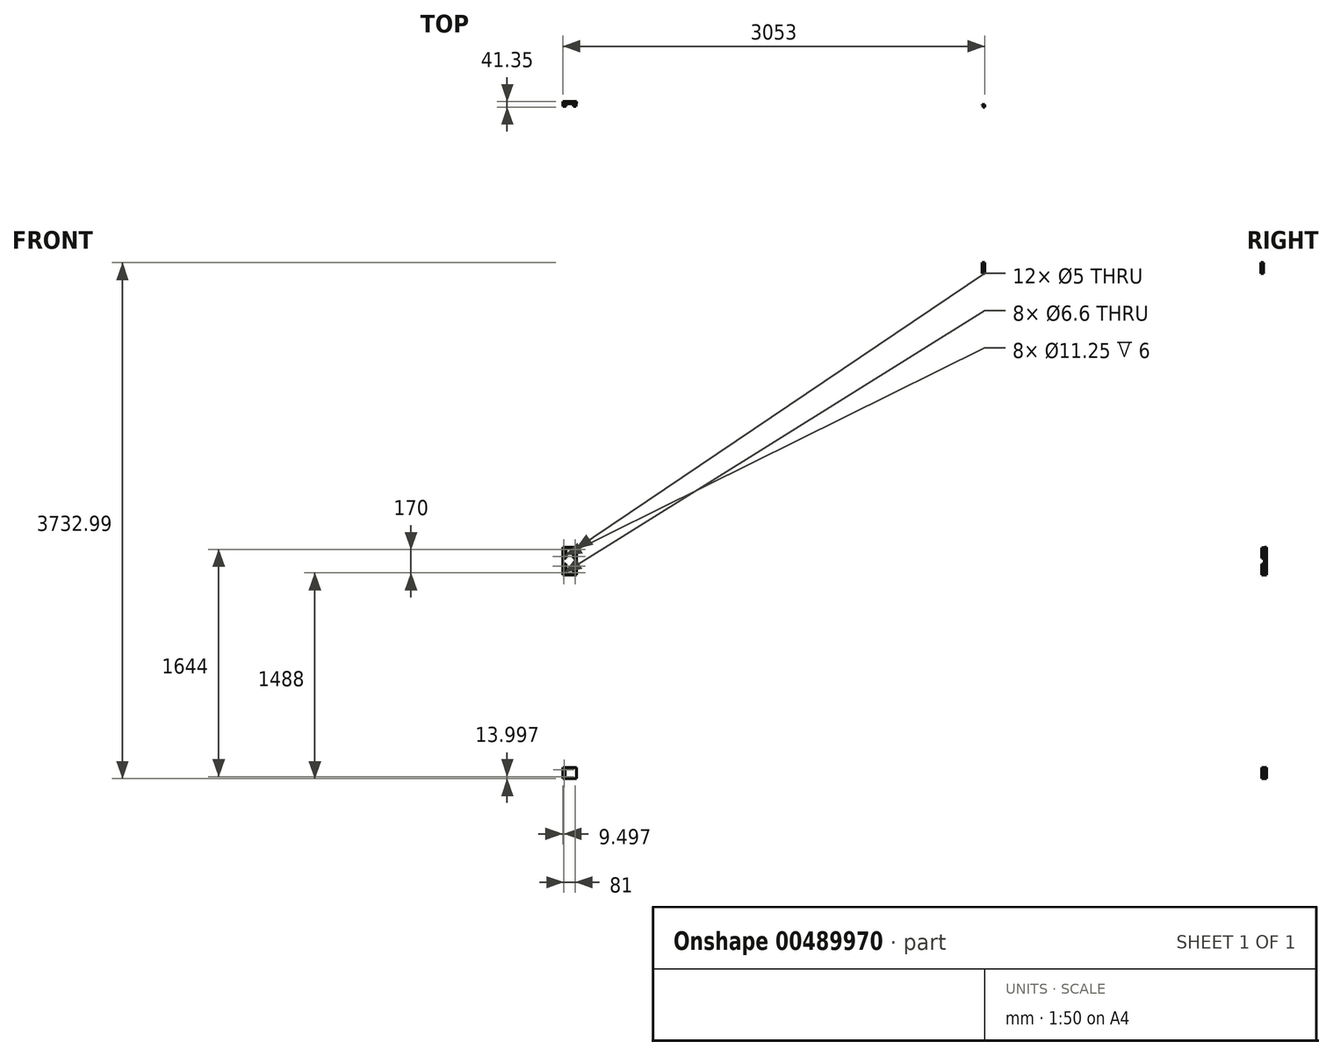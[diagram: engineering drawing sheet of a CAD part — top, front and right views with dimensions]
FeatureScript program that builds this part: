
annotation { "Feature Type Name" : "Feature", "Feature Type Description" : "" }
export const myFeature = defineFeature(function(context is Context, id is Id, definition is map)
    precondition{}
    {
        {
            var Q0;
            Q0=qCreatedBy(makeId("Front.planeOp"),FACE);
            var sketch = newSketch(context, id + "F0", { "sketchPlane" : qUnion([Q0])});
            skLineSegment(sketch, "E0", {"start": v(-4872.13, -1290) * mm, "end": v(-4872.13, -1364) * mm});
            skLineSegment(sketch, "E1", {"start": v(-2252.13, -1502) * mm, "end": v(-2252.13, -1432) * mm});
            skLineSegment(sketch, "E2", {"start": v(-2092.13, -1432) * mm, "end": v(-2092.13, -1502) * mm});
            skLineSegment(sketch, "E3", {"start": v(-2202.13, -1502) * mm, "end": v(-2252.13, -1502) * mm});
            skLineSegment(sketch, "E4", {"start": v(-2227.13, -1527.44) * mm, "end": v(-2227.13, -1552.44) * mm});
            skLineSegment(sketch, "E5", {"start": v(-2202.13, -1552.44) * mm, "end": v(-2241.95, -1552.44) * mm});
            skLineSegment(sketch, "E6", {"start": v(-2202.13, -1527.44) * mm, "end": v(-2252.13, -1527.44) * mm});
            skLineSegment(sketch, "E7", {"start": v(-2202.13, -1518.44) * mm, "end": v(-2252.13, -1518.44) * mm});
            skLineSegment(sketch, "E8", {"start": v(-2252.13, -1509.44) * mm, "end": v(-2202.13, -1509.44) * mm});
            skLineSegment(sketch, "E9", {"start": v(-2252.13, -1527.44) * mm, "end": v(-2252.13, -1509.44) * mm});
            skLineSegment(sketch, "E10", {"start": v(-2237.13, -1502) * mm, "end": v(-2237.13, -1509.44) * mm});
            skLineSegment(sketch, "E11", {"start": v(-2092.13, -1502) * mm, "end": v(-2142.13, -1502) * mm});
            skLineSegment(sketch, "E12", {"start": v(-2117.13, -1552.44) * mm, "end": v(-2117.13, -1527.44) * mm});
            skLineSegment(sketch, "E13", {"start": v(-2102.32, -1552.44) * mm, "end": v(-2142.13, -1552.44) * mm});
            skLineSegment(sketch, "E14", {"start": v(-2092.13, -1527.44) * mm, "end": v(-2142.13, -1527.44) * mm});
            skLineSegment(sketch, "E15", {"start": v(-2092.13, -1518.44) * mm, "end": v(-2142.13, -1518.44) * mm});
            skLineSegment(sketch, "E16", {"start": v(-2142.13, -1509.44) * mm, "end": v(-2092.13, -1509.44) * mm});
            skLineSegment(sketch, "E17", {"start": v(-2092.13, -1509.44) * mm, "end": v(-2092.13, -1527.44) * mm});
            skLineSegment(sketch, "E18", {"start": v(-2107.13, -1509.44) * mm, "end": v(-2107.13, -1502) * mm});
            skLineSegment(sketch, "E19", {"start": v(-2241.95, -1708.72) * mm, "end": v(-2241.95, -1552.44) * mm});
            skLineSegment(sketch, "E20", {"start": v(-2102.32, -1552.44) * mm, "end": v(-2102.32, -1708.72) * mm});
            skLineSegment(sketch, "E21", {"start": v(-2229.96, -1728.44) * mm, "end": v(-2202.13, -1728.44) * mm});
            skLineSegment(sketch, "E22", {"start": v(-2202.13, -1708.72) * mm, "end": v(-2241.95, -1708.72) * mm});
            skLineSegment(sketch, "E23", {"start": v(-2241.95, -1664.44) * mm, "end": v(-2202.13, -1664.44) * mm});
            skLineSegment(sketch, "E24", {"start": v(-2235.24, -1708.72) * mm, "end": v(-2229.96, -1728.44) * mm});
            skLineSegment(sketch, "E25", {"start": v(-2142.13, -1728.44) * mm, "end": v(-2114.3, -1728.44) * mm});
            skLineSegment(sketch, "E26", {"start": v(-2102.32, -1708.72) * mm, "end": v(-2142.13, -1708.72) * mm});
            skLineSegment(sketch, "E27", {"start": v(-2142.13, -1664.44) * mm, "end": v(-2102.32, -1664.44) * mm});
            skLineSegment(sketch, "E28", {"start": v(-2114.3, -1728.44) * mm, "end": v(-2109.02, -1708.72) * mm});
            skLineSegment(sketch, "E29", {"start": v(-2202.13, -1832) * mm, "end": v(-2202.13, -1432) * mm});
            skLineSegment(sketch, "E30", {"start": v(-2142.13, -1832) * mm, "end": v(-2142.13, -1432) * mm});
            skLineSegment(sketch, "E31", {"start": v(47.87, -1832) * mm, "end": v(47.87, -1432) * mm});
            skLineSegment(sketch, "E32", {"start": v(107.87, -1832) * mm, "end": v(107.87, -1432) * mm});
            skLineSegment(sketch, "E33", {"start": v(377.87, -1290) * mm, "end": v(377.87, -1364) * mm});
            skLineSegment(sketch, "E34", {"start": v(1373.62, -1832) * mm, "end": v(1373.62, -1432) * mm});
            skLineSegment(sketch, "E35", {"start": v(1433.62, -1832) * mm, "end": v(1433.62, -1432) * mm});
            skLineSegment(sketch, "E36", {"start": v(2247.87, -1502) * mm, "end": v(2247.87, -1432) * mm});
            skLineSegment(sketch, "E37", {"start": v(2407.87, -1432) * mm, "end": v(2407.87, -1502) * mm});
            skLineSegment(sketch, "E38", {"start": v(2297.87, -1502) * mm, "end": v(2247.87, -1502) * mm});
            skLineSegment(sketch, "E39", {"start": v(2272.87, -1527.44) * mm, "end": v(2272.87, -1552.44) * mm});
            skLineSegment(sketch, "E40", {"start": v(2297.87, -1552.44) * mm, "end": v(2258.05, -1552.44) * mm});
            skLineSegment(sketch, "E41", {"start": v(2297.87, -1527.44) * mm, "end": v(2247.87, -1527.44) * mm});
            skLineSegment(sketch, "E42", {"start": v(2297.87, -1518.44) * mm, "end": v(2247.87, -1518.44) * mm});
            skLineSegment(sketch, "E43", {"start": v(2247.87, -1509.44) * mm, "end": v(2297.87, -1509.44) * mm});
            skLineSegment(sketch, "E44", {"start": v(2247.87, -1527.44) * mm, "end": v(2247.87, -1509.44) * mm});
            skLineSegment(sketch, "E45", {"start": v(2262.87, -1502) * mm, "end": v(2262.87, -1509.44) * mm});
            skLineSegment(sketch, "E46", {"start": v(2407.87, -1502) * mm, "end": v(2357.87, -1502) * mm});
            skLineSegment(sketch, "E47", {"start": v(2382.87, -1552.44) * mm, "end": v(2382.87, -1527.44) * mm});
            skLineSegment(sketch, "E48", {"start": v(2397.68, -1552.44) * mm, "end": v(2357.87, -1552.44) * mm});
            skLineSegment(sketch, "E49", {"start": v(2407.87, -1527.44) * mm, "end": v(2357.87, -1527.44) * mm});
            skLineSegment(sketch, "E50", {"start": v(2407.87, -1518.44) * mm, "end": v(2357.87, -1518.44) * mm});
            skLineSegment(sketch, "E51", {"start": v(2357.87, -1509.44) * mm, "end": v(2407.87, -1509.44) * mm});
            skLineSegment(sketch, "E52", {"start": v(2407.87, -1509.44) * mm, "end": v(2407.87, -1527.44) * mm});
            skLineSegment(sketch, "E53", {"start": v(2392.87, -1509.44) * mm, "end": v(2392.87, -1502) * mm});
            skLineSegment(sketch, "E54", {"start": v(2258.05, -1664.44) * mm, "end": v(2297.87, -1664.44) * mm});
            skLineSegment(sketch, "E55", {"start": v(2357.87, -1664.44) * mm, "end": v(2397.68, -1664.44) * mm});
            skLineSegment(sketch, "E56", {"start": v(2397.68, -1552.44) * mm, "end": v(2397.68, -1708.72) * mm});
            skLineSegment(sketch, "E57", {"start": v(2258.05, -1708.72) * mm, "end": v(2258.05, -1552.44) * mm});
            skLineSegment(sketch, "E58", {"start": v(2270.04, -1728.44) * mm, "end": v(2297.87, -1728.44) * mm});
            skLineSegment(sketch, "E59", {"start": v(2297.87, -1708.72) * mm, "end": v(2258.05, -1708.72) * mm});
            skLineSegment(sketch, "E60", {"start": v(2264.76, -1708.72) * mm, "end": v(2270.04, -1728.44) * mm});
            skLineSegment(sketch, "E61", {"start": v(2397.68, -1708.72) * mm, "end": v(2357.87, -1708.72) * mm});
            skLineSegment(sketch, "E62", {"start": v(2385.7, -1728.44) * mm, "end": v(2390.98, -1708.72) * mm});
            skLineSegment(sketch, "E63", {"start": v(2357.87, -1728.44) * mm, "end": v(2385.7, -1728.44) * mm});
            skLineSegment(sketch, "E64", {"start": v(2357.87, -1832) * mm, "end": v(2357.87, -1432) * mm});
            skLineSegment(sketch, "E65", {"start": v(2297.87, -1832) * mm, "end": v(2297.87, -1432) * mm});
            skLineSegment(sketch, "E66", {"start": v(5047.87, -1832) * mm, "end": v(5047.87, -1907) * mm});
            skLineSegment(sketch, "E67", {"start": v(5027.87, -1364) * mm, "end": v(5027.87, -1290) * mm});
            skLineSegment(sketch, "E68", {"start": v(-813.13, -3157.5) * mm, "end": v(-1564.63, -3157.5) * mm});
            skLineSegment(sketch, "E69", {"start": v(-813.13, -3107.5) * mm, "end": v(-1564.63, -3107.5) * mm});
            skLineSegment(sketch, "E70", {"start": v(-4218.63, -3177.5) * mm, "end": v(-3029.63, -3177.5) * mm});
            skLineSegment(sketch, "E71", {"start": v(-813.13, -3177.5) * mm, "end": v(-813.13, -3087.5) * mm});
            skLineSegment(sketch, "E72", {"start": v(-813.13, -3087.5) * mm, "end": v(-1564.63, -3087.5) * mm});
            skLineSegment(sketch, "E73", {"start": v(-4245.63, -2962.5) * mm, "end": v(-4364.63, -2962.5) * mm});
            skLineSegment(sketch, "E74", {"start": v(-4245.63, -3302.5) * mm, "end": v(-4245.63, -2962.5) * mm});
            skLineSegment(sketch, "E75", {"start": v(-4245.63, -3072.5) * mm, "end": v(-4218.63, -3072.5) * mm});
            skLineSegment(sketch, "E76", {"start": v(-4218.63, -3072.5) * mm, "end": v(-4218.63, -3192.5) * mm});
            skLineSegment(sketch, "E77", {"start": v(-4218.63, -3192.5) * mm, "end": v(-4245.63, -3192.5) * mm});
            skLineSegment(sketch, "E78", {"start": v(-4245.63, -3007.5) * mm, "end": v(-4364.63, -3007.5) * mm});
            skLineSegment(sketch, "E79", {"start": v(-5062.13, -3735.9) * mm, "end": v(-4502.13, -3735.9) * mm});
            skLineSegment(sketch, "E80", {"start": v(-4567.13, -3735.9) * mm, "end": v(-4567.13, -3667.9) * mm});
            skLineSegment(sketch, "E81", {"start": v(-4928.15, -3475.9) * mm, "end": v(-4567.13, -3475.9) * mm});
            skLineSegment(sketch, "E82", {"start": v(-4586.13, -3265.9) * mm, "end": v(-4628.13, -3265.9) * mm});
            skLineSegment(sketch, "E83", {"start": v(-4579.63, -3250.02) * mm, "end": v(-4607.13, -3234.14) * mm});
            skLineSegment(sketch, "E84", {"start": v(-4579.63, -3281.77) * mm, "end": v(-4579.63, -3250.02) * mm});
            skLineSegment(sketch, "E85", {"start": v(-4607.13, -3297.65) * mm, "end": v(-4579.63, -3281.77) * mm});
            skLineSegment(sketch, "E86", {"start": v(-4628.13, -3685.9) * mm, "end": v(-4586.13, -3685.9) * mm});
            skLineSegment(sketch, "E87", {"start": v(-4607.13, -3717.65) * mm, "end": v(-4579.63, -3701.77) * mm});
            skLineSegment(sketch, "E88", {"start": v(-4579.63, -3701.77) * mm, "end": v(-4579.63, -3670.02) * mm});
            skLineSegment(sketch, "E89", {"start": v(-4579.63, -3670.02) * mm, "end": v(-4607.13, -3654.14) * mm});
            skLineSegment(sketch, "E90", {"start": v(-4502.13, -3215.9) * mm, "end": v(-5062.13, -3215.9) * mm});
            skLineSegment(sketch, "E91", {"start": v(-4567.13, -3302.5) * mm, "end": v(-4567.13, -3215.9) * mm});
            skLineSegment(sketch, "E92", {"start": v(-1779.63, -3321.5) * mm, "end": v(-1779.63, -3671.5) * mm});
            skLineSegment(sketch, "E93", {"start": v(-3228.13, -3760.9) * mm, "end": v(-3186.13, -3760.9) * mm});
            skLineSegment(sketch, "E94", {"start": v(-3207.13, -3781.9) * mm, "end": v(-3207.13, -3739.9) * mm});
            skLineSegment(sketch, "E95", {"start": v(-3207.13, -3774.75) * mm, "end": v(-3195.13, -3767.82) * mm});
            skLineSegment(sketch, "E96", {"start": v(-3195.13, -3767.82) * mm, "end": v(-3195.13, -3753.97) * mm});
            skLineSegment(sketch, "E97", {"start": v(-3195.13, -3753.97) * mm, "end": v(-3207.13, -3747.04) * mm});
            skLineSegment(sketch, "E98", {"start": v(-3207.13, -3747.04) * mm, "end": v(-3219.13, -3753.97) * mm});
            skLineSegment(sketch, "E99", {"start": v(-3219.13, -3753.97) * mm, "end": v(-3219.13, -3767.82) * mm});
            skLineSegment(sketch, "E100", {"start": v(-3219.13, -3767.82) * mm, "end": v(-3207.13, -3774.75) * mm});
            skLineSegment(sketch, "E101", {"start": v(-3186.13, -3190.9) * mm, "end": v(-3228.13, -3190.9) * mm});
            skLineSegment(sketch, "E102", {"start": v(-3207.13, -3211.9) * mm, "end": v(-3207.13, -3169.9) * mm});
            skLineSegment(sketch, "E103", {"start": v(-3195.13, -3183.97) * mm, "end": v(-3207.13, -3177.04) * mm});
            skLineSegment(sketch, "E104", {"start": v(-3195.13, -3197.82) * mm, "end": v(-3195.13, -3183.97) * mm});
            skLineSegment(sketch, "E105", {"start": v(-3207.13, -3204.75) * mm, "end": v(-3195.13, -3197.82) * mm});
            skLineSegment(sketch, "E106", {"start": v(-3219.13, -3197.82) * mm, "end": v(-3207.13, -3204.75) * mm});
            skLineSegment(sketch, "E107", {"start": v(-3219.13, -3183.97) * mm, "end": v(-3219.13, -3197.82) * mm});
            skLineSegment(sketch, "E108", {"start": v(-3207.13, -3177.04) * mm, "end": v(-3219.13, -3183.97) * mm});
            skLineSegment(sketch, "E109", {"start": v(-3557.13, -3169.9) * mm, "end": v(-3557.13, -3211.9) * mm});
            skLineSegment(sketch, "E110", {"start": v(-3536.13, -3190.9) * mm, "end": v(-3578.13, -3190.9) * mm});
            skLineSegment(sketch, "E111", {"start": v(-3557.13, -3177.04) * mm, "end": v(-3569.13, -3183.97) * mm});
            skLineSegment(sketch, "E112", {"start": v(-3569.13, -3183.97) * mm, "end": v(-3569.13, -3197.82) * mm});
            skLineSegment(sketch, "E113", {"start": v(-3569.13, -3197.82) * mm, "end": v(-3557.13, -3204.75) * mm});
            skLineSegment(sketch, "E114", {"start": v(-3557.13, -3204.75) * mm, "end": v(-3545.13, -3197.82) * mm});
            skLineSegment(sketch, "E115", {"start": v(-3545.13, -3197.82) * mm, "end": v(-3545.13, -3183.97) * mm});
            skLineSegment(sketch, "E116", {"start": v(-3545.13, -3183.97) * mm, "end": v(-3557.13, -3177.04) * mm});
            skLineSegment(sketch, "E117", {"start": v(-3569.13, -3767.82) * mm, "end": v(-3557.13, -3774.75) * mm});
            skLineSegment(sketch, "E118", {"start": v(-3569.13, -3753.97) * mm, "end": v(-3569.13, -3767.82) * mm});
            skLineSegment(sketch, "E119", {"start": v(-3557.13, -3747.04) * mm, "end": v(-3569.13, -3753.97) * mm});
            skLineSegment(sketch, "E120", {"start": v(-3545.13, -3753.97) * mm, "end": v(-3557.13, -3747.04) * mm});
            skLineSegment(sketch, "E121", {"start": v(-3545.13, -3767.82) * mm, "end": v(-3545.13, -3753.97) * mm});
            skLineSegment(sketch, "E122", {"start": v(-3557.13, -3774.75) * mm, "end": v(-3545.13, -3767.82) * mm});
            skLineSegment(sketch, "E123", {"start": v(-3557.13, -3739.9) * mm, "end": v(-3557.13, -3781.9) * mm});
            skLineSegment(sketch, "E124", {"start": v(-3578.13, -3760.9) * mm, "end": v(-3536.13, -3760.9) * mm});
            skLineSegment(sketch, "E125", {"start": v(-3597.13, -3790.9) * mm, "end": v(-3167.13, -3790.9) * mm});
            skLineSegment(sketch, "E126", {"start": v(-3597.13, -3160.9) * mm, "end": v(-3167.13, -3160.9) * mm});
            skLineSegment(sketch, "E127", {"start": v(-3377.13, -3496.5) * mm, "end": v(-3377.13, -3484.5) * mm});
            skLineSegment(sketch, "E128", {"start": v(-3427.13, -3358.55) * mm, "end": v(-3427.13, -3484.44) * mm});
            skLineSegment(sketch, "E129", {"start": v(-3377.13, -3496.5) * mm, "end": v(-3382.13, -3496.5) * mm});
            skLineSegment(sketch, "E130", {"start": v(-3377.13, -3484.5) * mm, "end": v(-3377.13, -3496.5) * mm});
            skLineSegment(sketch, "E131", {"start": v(-3382.13, -3496.5) * mm, "end": v(-3427.13, -3484.44) * mm});
            skLineSegment(sketch, "E132", {"start": v(-3382.13, -3346.5) * mm, "end": v(-3377.13, -3346.5) * mm});
            skLineSegment(sketch, "E133", {"start": v(-3427.13, -3358.55) * mm, "end": v(-3382.13, -3346.5) * mm});
            skLineSegment(sketch, "E134", {"start": v(-3382.13, -3582.8) * mm, "end": v(-3427.13, -3570.74) * mm});
            skLineSegment(sketch, "E135", {"start": v(-3377.13, -3517.2) * mm, "end": v(-3377.13, -3505.2) * mm});
            skLineSegment(sketch, "E136", {"start": v(-3377.13, -3570.8) * mm, "end": v(-3377.13, -3582.8) * mm});
            skLineSegment(sketch, "E137", {"start": v(-3377.13, -3582.8) * mm, "end": v(-3382.13, -3582.8) * mm});
            skLineSegment(sketch, "E138", {"start": v(-3427.13, -3505.2) * mm, "end": v(-3427.13, -3570.74) * mm});
            skLineSegment(sketch, "E139", {"start": v(-3427.13, -3505.2) * mm, "end": v(-3377.13, -3505.2) * mm});
            skLineSegment(sketch, "E140", {"start": v(-3282.13, -3595.9) * mm, "end": v(-3482.13, -3595.9) * mm});
            skLineSegment(sketch, "E141", {"start": v(-3482.13, -3355.9) * mm, "end": v(-3417.21, -3355.9) * mm});
            skLineSegment(sketch, "E142", {"start": v(-3463.73, -3383.9) * mm, "end": v(-3427.13, -3383.9) * mm});
            skLineSegment(sketch, "E143", {"start": v(-3482.13, -3375.9) * mm, "end": v(-3427.13, -3375.9) * mm});
            skLineSegment(sketch, "E144", {"start": v(-3463.73, -3567.9) * mm, "end": v(-3427.13, -3567.9) * mm});
            skLineSegment(sketch, "E145", {"start": v(-3482.13, -3575.9) * mm, "end": v(-3408.06, -3575.9) * mm});
            skLineSegment(sketch, "E146", {"start": v(-3474.13, -3394.3) * mm, "end": v(-3474.13, -3557.5) * mm});
            skLineSegment(sketch, "E147", {"start": v(-3497.13, -3602.9) * mm, "end": v(-3497.13, -3225.9) * mm});
            skLineSegment(sketch, "E148", {"start": v(-3482.13, -3225.9) * mm, "end": v(-3482.13, -3602.9) * mm});
            skLineSegment(sketch, "E149", {"start": v(-3497.13, -3225.9) * mm, "end": v(-3482.13, -3225.9) * mm});
            skLineSegment(sketch, "E150", {"start": v(-3597.13, -3160.9) * mm, "end": v(-3597.13, -3602.9) * mm});
            skLineSegment(sketch, "E151", {"start": v(-3597.13, -3735.9) * mm, "end": v(-3167.13, -3735.9) * mm});
            skLineSegment(sketch, "E152", {"start": v(-3536.13, -3265.9) * mm, "end": v(-3578.13, -3265.9) * mm});
            skLineSegment(sketch, "E153", {"start": v(-3557.13, -3244.9) * mm, "end": v(-3557.13, -3286.9) * mm});
            skLineSegment(sketch, "E154", {"start": v(-3167.13, -3790.9) * mm, "end": v(-3167.13, -3775.5) * mm});
            skLineSegment(sketch, "E155", {"start": v(-3167.13, -3215.9) * mm, "end": v(-3337.13, -3215.9) * mm});
            skLineSegment(sketch, "E156", {"start": v(-3528.15, -3475.9) * mm, "end": v(-3167.13, -3475.9) * mm});
            skLineSegment(sketch, "E157", {"start": v(-3557.13, -3234.14) * mm, "end": v(-3584.63, -3250.02) * mm});
            skLineSegment(sketch, "E158", {"start": v(-3584.63, -3250.02) * mm, "end": v(-3584.63, -3281.77) * mm});
            skLineSegment(sketch, "E159", {"start": v(-3584.63, -3281.77) * mm, "end": v(-3557.13, -3297.65) * mm});
            skLineSegment(sketch, "E160", {"start": v(-3557.13, -3297.65) * mm, "end": v(-3529.63, -3281.77) * mm});
            skLineSegment(sketch, "E161", {"start": v(-3529.63, -3281.77) * mm, "end": v(-3529.63, -3250.02) * mm});
            skLineSegment(sketch, "E162", {"start": v(-3529.63, -3250.02) * mm, "end": v(-3557.13, -3234.14) * mm});
            skLineSegment(sketch, "E163", {"start": v(-3578.13, -3685.9) * mm, "end": v(-3536.13, -3685.9) * mm});
            skLineSegment(sketch, "E164", {"start": v(-3557.13, -3664.9) * mm, "end": v(-3557.13, -3706.9) * mm});
            skLineSegment(sketch, "E165", {"start": v(-3584.63, -3701.77) * mm, "end": v(-3557.13, -3717.65) * mm});
            skLineSegment(sketch, "E166", {"start": v(-3584.63, -3670.02) * mm, "end": v(-3584.63, -3701.77) * mm});
            skLineSegment(sketch, "E167", {"start": v(-3557.13, -3654.14) * mm, "end": v(-3584.63, -3670.02) * mm});
            skLineSegment(sketch, "E168", {"start": v(-3529.63, -3670.02) * mm, "end": v(-3557.13, -3654.14) * mm});
            skLineSegment(sketch, "E169", {"start": v(-3529.63, -3701.77) * mm, "end": v(-3529.63, -3670.02) * mm});
            skLineSegment(sketch, "E170", {"start": v(-3557.13, -3717.65) * mm, "end": v(-3529.63, -3701.77) * mm});
            skLineSegment(sketch, "E171", {"start": v(-3186.13, -3265.9) * mm, "end": v(-3228.13, -3265.9) * mm});
            skLineSegment(sketch, "E172", {"start": v(-3207.13, -3286.9) * mm, "end": v(-3207.13, -3244.9) * mm});
            skLineSegment(sketch, "E173", {"start": v(-3179.63, -3250.02) * mm, "end": v(-3207.13, -3234.14) * mm});
            skLineSegment(sketch, "E174", {"start": v(-3179.63, -3281.77) * mm, "end": v(-3179.63, -3250.02) * mm});
            skLineSegment(sketch, "E175", {"start": v(-3207.13, -3297.65) * mm, "end": v(-3179.63, -3281.77) * mm});
            skLineSegment(sketch, "E176", {"start": v(-3234.63, -3281.77) * mm, "end": v(-3207.13, -3297.65) * mm});
            skLineSegment(sketch, "E177", {"start": v(-3234.63, -3250.02) * mm, "end": v(-3234.63, -3281.77) * mm});
            skLineSegment(sketch, "E178", {"start": v(-3207.13, -3234.14) * mm, "end": v(-3234.63, -3250.02) * mm});
            skLineSegment(sketch, "E179", {"start": v(-3359.63, -3431.4) * mm, "end": v(-3359.63, -3411.6) * mm});
            skLineSegment(sketch, "E180", {"start": v(-3389.63, -3409.8) * mm, "end": v(-3389.63, -3360.8) * mm});
            skLineSegment(sketch, "E181", {"start": v(-3304.63, -3360.8) * mm, "end": v(-3304.63, -3409.8) * mm});
            skLineSegment(sketch, "E182", {"start": v(-3389.13, -3360.3) * mm, "end": v(-3389.63, -3360.8) * mm});
            skLineSegment(sketch, "E183", {"start": v(-3389.13, -3410.3) * mm, "end": v(-3389.63, -3409.8) * mm});
            skLineSegment(sketch, "E184", {"start": v(-3305.13, -3410.3) * mm, "end": v(-3304.63, -3409.8) * mm});
            skLineSegment(sketch, "E185", {"start": v(-3305.13, -3360.3) * mm, "end": v(-3304.63, -3360.8) * mm});
            skLineSegment(sketch, "E186", {"start": v(-3305.13, -3410.3) * mm, "end": v(-3389.13, -3410.3) * mm});
            skLineSegment(sketch, "E187", {"start": v(-3389.13, -3360.3) * mm, "end": v(-3305.13, -3360.3) * mm});
            skLineSegment(sketch, "E188", {"start": v(-3347.13, -3375.54) * mm, "end": v(-3347.13, -3458.2) * mm});
            skLineSegment(sketch, "E189", {"start": v(-3377.13, -3358.5) * mm, "end": v(-3377.13, -3346.5) * mm});
            skLineSegment(sketch, "E190", {"start": v(-3317.13, -3346.5) * mm, "end": v(-3377.13, -3346.5) * mm});
            skLineSegment(sketch, "E191", {"start": v(-3317.13, -3505.2) * mm, "end": v(-3377.13, -3505.2) * mm});
            skLineSegment(sketch, "E192", {"start": v(-3389.63, -3568.5) * mm, "end": v(-3389.63, -3519.5) * mm});
            skLineSegment(sketch, "E193", {"start": v(-3305.13, -3569) * mm, "end": v(-3389.13, -3569) * mm});
            skLineSegment(sketch, "E194", {"start": v(-3304.63, -3519.5) * mm, "end": v(-3304.63, -3568.5) * mm});
            skLineSegment(sketch, "E195", {"start": v(-3389.63, -3568.5) * mm, "end": v(-3389.13, -3569) * mm});
            skLineSegment(sketch, "E196", {"start": v(-3389.63, -3519.5) * mm, "end": v(-3389.13, -3519) * mm});
            skLineSegment(sketch, "E197", {"start": v(-3304.63, -3519.5) * mm, "end": v(-3305.13, -3519) * mm});
            skLineSegment(sketch, "E198", {"start": v(-3304.63, -3568.5) * mm, "end": v(-3305.13, -3569) * mm});
            skLineSegment(sketch, "E199", {"start": v(-3389.13, -3519) * mm, "end": v(-3305.13, -3519) * mm});
            skLineSegment(sketch, "E200", {"start": v(-3347.13, -3485.8) * mm, "end": v(-3347.13, -3584.95) * mm});
            skLineSegment(sketch, "E201", {"start": v(-3377.13, -3582.8) * mm, "end": v(-3317.13, -3582.8) * mm});
            skLineSegment(sketch, "E202", {"start": v(-3389.63, -3482.2) * mm, "end": v(-3389.63, -3433.2) * mm});
            skLineSegment(sketch, "E203", {"start": v(-3305.13, -3482.7) * mm, "end": v(-3389.13, -3482.7) * mm});
            skLineSegment(sketch, "E204", {"start": v(-3304.63, -3433.2) * mm, "end": v(-3304.63, -3482.2) * mm});
            skLineSegment(sketch, "E205", {"start": v(-3389.63, -3482.2) * mm, "end": v(-3389.13, -3482.7) * mm});
            skLineSegment(sketch, "E206", {"start": v(-3389.63, -3433.2) * mm, "end": v(-3389.13, -3432.7) * mm});
            skLineSegment(sketch, "E207", {"start": v(-3304.63, -3433.2) * mm, "end": v(-3305.13, -3432.7) * mm});
            skLineSegment(sketch, "E208", {"start": v(-3304.63, -3482.2) * mm, "end": v(-3305.13, -3482.7) * mm});
            skLineSegment(sketch, "E209", {"start": v(-3389.13, -3432.7) * mm, "end": v(-3305.13, -3432.7) * mm});
            skLineSegment(sketch, "E210", {"start": v(-3334.63, -3411.6) * mm, "end": v(-3334.63, -3431.4) * mm});
            skLineSegment(sketch, "E211", {"start": v(-3377.13, -3496.5) * mm, "end": v(-3317.13, -3496.5) * mm});
            skLineSegment(sketch, "E212", {"start": v(-3387.13, -3432.7) * mm, "end": v(-3387.13, -3410.3) * mm});
            skLineSegment(sketch, "E213", {"start": v(-3307.13, -3432.7) * mm, "end": v(-3307.13, -3410.3) * mm});
            skLineSegment(sketch, "E214", {"start": v(-3317.13, -3346.5) * mm, "end": v(-3317.13, -3358.5) * mm});
            skLineSegment(sketch, "E215", {"start": v(-3317.13, -3484.5) * mm, "end": v(-3317.13, -3496.5) * mm});
            skLineSegment(sketch, "E216", {"start": v(-3317.13, -3505.2) * mm, "end": v(-3317.13, -3517.2) * mm});
            skLineSegment(sketch, "E217", {"start": v(-3317.13, -3570.8) * mm, "end": v(-3317.13, -3582.8) * mm});
            skLineSegment(sketch, "E218", {"start": v(-3317.13, -3579) * mm, "end": v(-3307.13, -3579) * mm});
            skLineSegment(sketch, "E219", {"start": v(-3307.13, -3579) * mm, "end": v(-3307.13, -3569) * mm});
            skLineSegment(sketch, "E220", {"start": v(-3317.13, -3509) * mm, "end": v(-3307.13, -3509) * mm});
            skLineSegment(sketch, "E221", {"start": v(-3307.13, -3509) * mm, "end": v(-3307.13, -3519) * mm});
            skLineSegment(sketch, "E222", {"start": v(-3317.13, -3352.5) * mm, "end": v(-3307.13, -3352.5) * mm});
            skLineSegment(sketch, "E223", {"start": v(-3307.13, -3352.5) * mm, "end": v(-3307.13, -3360.3) * mm});
            skLineSegment(sketch, "E224", {"start": v(-3317.13, -3490.5) * mm, "end": v(-3307.13, -3490.5) * mm});
            skLineSegment(sketch, "E225", {"start": v(-3307.13, -3490.5) * mm, "end": v(-3307.13, -3482.7) * mm});
            skLineSegment(sketch, "E226", {"start": v(-3282.13, -3602.9) * mm, "end": v(-3282.13, -3551.5) * mm});
            skLineSegment(sketch, "E227", {"start": v(-3282.13, -3225.9) * mm, "end": v(-3267.13, -3225.9) * mm});
            skLineSegment(sketch, "E228", {"start": v(-3267.13, -3225.9) * mm, "end": v(-3267.13, -3410) * mm});
            skLineSegment(sketch, "E229", {"start": v(-3228.13, -3685.9) * mm, "end": v(-3186.13, -3685.9) * mm});
            skLineSegment(sketch, "E230", {"start": v(-3207.13, -3706.9) * mm, "end": v(-3207.13, -3664.9) * mm});
            skLineSegment(sketch, "E231", {"start": v(-3207.13, -3717.65) * mm, "end": v(-3179.63, -3701.77) * mm});
            skLineSegment(sketch, "E232", {"start": v(-3179.63, -3701.77) * mm, "end": v(-3179.63, -3670.02) * mm});
            skLineSegment(sketch, "E233", {"start": v(-3179.63, -3670.02) * mm, "end": v(-3207.13, -3654.14) * mm});
            skLineSegment(sketch, "E234", {"start": v(-3207.13, -3654.14) * mm, "end": v(-3234.63, -3670.02) * mm});
            skLineSegment(sketch, "E235", {"start": v(-3234.63, -3670.02) * mm, "end": v(-3234.63, -3701.77) * mm});
            skLineSegment(sketch, "E236", {"start": v(-3234.63, -3701.77) * mm, "end": v(-3207.13, -3717.65) * mm});
            skLineSegment(sketch, "E237", {"start": v(-3282.13, -3575.9) * mm, "end": v(-3307.13, -3575.9) * mm});
            skLineSegment(sketch, "E238", {"start": v(-3282.13, -3375.9) * mm, "end": v(-3304.63, -3375.9) * mm});
            skLineSegment(sketch, "E239", {"start": v(-3290.13, -3557.5) * mm, "end": v(-3290.13, -3551.5) * mm});
            skLineSegment(sketch, "E240", {"start": v(-3307.13, -3355.9) * mm, "end": v(-3282.13, -3355.9) * mm});
            skLineSegment(sketch, "E241", {"start": v(-3300.53, -3383.9) * mm, "end": v(-3304.63, -3383.9) * mm});
            skLineSegment(sketch, "E242", {"start": v(-3300.53, -3567.9) * mm, "end": v(-3304.63, -3567.9) * mm});
            skLineSegment(sketch, "E243", {"start": v(-3304.63, -3536.5) * mm, "end": v(-3259, -3536.5) * mm});
            skLineSegment(sketch, "E244", {"start": v(-3259, -3536.5) * mm, "end": v(-3259, -3538) * mm});
            skLineSegment(sketch, "E245", {"start": v(-3259, -3538) * mm, "end": v(-3222, -3538) * mm});
            skLineSegment(sketch, "E246", {"start": v(-3259, -3550) * mm, "end": v(-3259, -3551.5) * mm});
            skLineSegment(sketch, "E247", {"start": v(-3259, -3551.5) * mm, "end": v(-3304.63, -3551.5) * mm});
            skLineSegment(sketch, "E248", {"start": v(-3234, -3535) * mm, "end": v(-3234, -3553) * mm});
            skLineSegment(sketch, "E249", {"start": v(-3222, -3550) * mm, "end": v(-3241, -3550) * mm});
            skLineSegment(sketch, "E250", {"start": v(-3241, -3550) * mm, "end": v(-3246, -3550) * mm});
            skLineSegment(sketch, "E251", {"start": v(-3246, -3550) * mm, "end": v(-3259, -3550) * mm});
            skLineSegment(sketch, "E252", {"start": v(-3259, -3410) * mm, "end": v(-3259, -3412) * mm});
            skLineSegment(sketch, "E253", {"start": v(-3259, -3412) * mm, "end": v(-3218, -3412) * mm});
            skLineSegment(sketch, "E254", {"start": v(-3259, -3428) * mm, "end": v(-3259, -3430) * mm});
            skLineSegment(sketch, "E255", {"start": v(-3234, -3408.5) * mm, "end": v(-3234, -3431.5) * mm});
            skLineSegment(sketch, "E256", {"start": v(-3218, -3433) * mm, "end": v(-3218, -3407) * mm});
            skLineSegment(sketch, "E257", {"start": v(-3218, -3428) * mm, "end": v(-3243, -3428) * mm});
            skLineSegment(sketch, "E258", {"start": v(-3246, -3428) * mm, "end": v(-3259, -3428) * mm});
            skLineSegment(sketch, "E259", {"start": v(-3304.63, -3410) * mm, "end": v(-3259, -3410) * mm});
            skLineSegment(sketch, "E260", {"start": v(-3259, -3430) * mm, "end": v(-3307.13, -3430) * mm});
            skLineSegment(sketch, "E261", {"start": v(-3219.07, -3420) * mm, "end": v(-3249.07, -3420) * mm});
            skLineSegment(sketch, "E262", {"start": v(-3259, -3412) * mm, "end": v(-3243, -3412) * mm});
            skLineSegment(sketch, "E263", {"start": v(-3243, -3428) * mm, "end": v(-3250, -3428) * mm});
            skLineSegment(sketch, "E264", {"start": v(-3250, -3428) * mm, "end": v(-3259, -3428) * mm});
            skLineSegment(sketch, "E265", {"start": v(-3246, -3534) * mm, "end": v(-3244, -3532) * mm});
            skLineSegment(sketch, "E266", {"start": v(-3224, -3532) * mm, "end": v(-3222, -3534) * mm});
            skLineSegment(sketch, "E267", {"start": v(-3224, -3532) * mm, "end": v(-3244, -3532) * mm});
            skLineSegment(sketch, "E268", {"start": v(-3222, -3554) * mm, "end": v(-3222, -3534) * mm});
            skLineSegment(sketch, "E269", {"start": v(-3246, -3554) * mm, "end": v(-3246, -3550) * mm});
            skLineSegment(sketch, "E270", {"start": v(-3224, -3556) * mm, "end": v(-3244, -3556) * mm});
            skLineSegment(sketch, "E271", {"start": v(-3246, -3554) * mm, "end": v(-3244, -3556) * mm});
            skLineSegment(sketch, "E272", {"start": v(-3224, -3556) * mm, "end": v(-3222, -3554) * mm});
            skLineSegment(sketch, "E273", {"start": v(-3246, -3538) * mm, "end": v(-3246, -3534) * mm});
            skLineSegment(sketch, "E274", {"start": v(-3209, -3525) * mm, "end": v(-3209, -3563) * mm});
            skLineSegment(sketch, "E275", {"start": v(-3259, -3563) * mm, "end": v(-3259, -3551.5) * mm});
            skLineSegment(sketch, "E276", {"start": v(-3215, -3519) * mm, "end": v(-3253, -3519) * mm});
            skLineSegment(sketch, "E277", {"start": v(-3215, -3569) * mm, "end": v(-3253, -3569) * mm});
            skLineSegment(sketch, "E278", {"start": v(-3259, -3536.5) * mm, "end": v(-3259, -3524.5) * mm});
            skLineSegment(sketch, "E279", {"start": v(-3290.13, -3536.5) * mm, "end": v(-3290.13, -3430) * mm});
            skLineSegment(sketch, "E280", {"start": v(-3282.13, -3536.5) * mm, "end": v(-3282.13, -3430) * mm});
            skLineSegment(sketch, "E281", {"start": v(-3267.13, -3551.5) * mm, "end": v(-3267.13, -3602.9) * mm});
            skLineSegment(sketch, "E282", {"start": v(-3290.13, -3410) * mm, "end": v(-3290.13, -3394.3) * mm});
            skLineSegment(sketch, "E283", {"start": v(-3282.13, -3410) * mm, "end": v(-3282.13, -3225.9) * mm});
            skLineSegment(sketch, "E284", {"start": v(-3267.13, -3430) * mm, "end": v(-3267.13, -3536.5) * mm});
            skLineSegment(sketch, "E285", {"start": v(-3203, -3394.76) * mm, "end": v(-3203, -3441.26) * mm});
            skLineSegment(sketch, "E286", {"start": v(-3210.54, -3388.75) * mm, "end": v(-3257.04, -3388.75) * mm});
            skLineSegment(sketch, "E287", {"start": v(-3210.54, -3451.24) * mm, "end": v(-3257.04, -3451.24) * mm});
            skLineSegment(sketch, "E288", {"start": v(-3265, -3441.26) * mm, "end": v(-3265, -3430) * mm});
            skLineSegment(sketch, "E289", {"start": v(-3218, -3407) * mm, "end": v(-3221, -3404) * mm});
            skLineSegment(sketch, "E290", {"start": v(-3221, -3404) * mm, "end": v(-3247, -3404) * mm});
            skLineSegment(sketch, "E291", {"start": v(-3225, -3404) * mm, "end": v(-3225, -3403) * mm});
            skLineSegment(sketch, "E292", {"start": v(-3221, -3436) * mm, "end": v(-3247, -3436) * mm});
            skLineSegment(sketch, "E293", {"start": v(-3250, -3433) * mm, "end": v(-3247, -3436) * mm});
            skLineSegment(sketch, "E294", {"start": v(-3250, -3433) * mm, "end": v(-3250, -3428) * mm});
            skLineSegment(sketch, "E295", {"start": v(-3247, -3404) * mm, "end": v(-3250, -3407) * mm});
            skLineSegment(sketch, "E296", {"start": v(-3221, -3436) * mm, "end": v(-3218, -3433) * mm});
            skLineSegment(sketch, "E297", {"start": v(-3250, -3412) * mm, "end": v(-3250, -3407) * mm});
            skLineSegment(sketch, "E298", {"start": v(-3265, -3410) * mm, "end": v(-3265, -3398.73) * mm});
            skLineSegment(sketch, "E299", {"start": v(-3282.13, -3338.9) * mm, "end": v(-3282.13, -3355.9) * mm});
            skLineSegment(sketch, "E300", {"start": v(-3382.13, -3776.6) * mm, "end": v(-3382.13, -3170) * mm});
            skLineSegment(sketch, "E301", {"start": v(-3337.13, -3177.5) * mm, "end": v(-3337.13, -3338.9) * mm});
            skLineSegment(sketch, "E302", {"start": v(-3427.13, -3177.5) * mm, "end": v(-3427.13, -3338.9) * mm});
            skLineSegment(sketch, "E303", {"start": v(-3482.13, -3355.9) * mm, "end": v(-3482.13, -3338.9) * mm});
            skLineSegment(sketch, "E304", {"start": v(-3482.13, -3338.9) * mm, "end": v(-3282.13, -3338.9) * mm});
            skLineSegment(sketch, "E305", {"start": v(-3427.13, -3215.9) * mm, "end": v(-3597.13, -3215.9) * mm});
            skLineSegment(sketch, "E306", {"start": v(-1779.63, -3671.5) * mm, "end": v(-5562.13, -3671.5) * mm});
            skLineSegment(sketch, "E307", {"start": v(-2592.13, -3321.5) * mm, "end": v(-2592.13, -3671.5) * mm});
            skLineSegment(sketch, "E308", {"start": v(-3167.13, -3602.9) * mm, "end": v(-3167.13, -3160.9) * mm});
            skLineSegment(sketch, "E309", {"start": v(-3167.13, -3775.5) * mm, "end": v(-3167.13, -3602.9) * mm});
            skLineSegment(sketch, "E310", {"start": v(-3597.13, -3602.9) * mm, "end": v(-3597.13, -3775.5) * mm});
            skLineSegment(sketch, "E311", {"start": v(-3597.13, -3775.5) * mm, "end": v(-3597.13, -3790.9) * mm});
            skLineSegment(sketch, "E312", {"start": v(-1828.13, -3760.9) * mm, "end": v(-1786.13, -3760.9) * mm});
            skLineSegment(sketch, "E313", {"start": v(-1807.13, -3781.9) * mm, "end": v(-1807.13, -3739.9) * mm});
            skLineSegment(sketch, "E314", {"start": v(-1807.13, -3774.75) * mm, "end": v(-1795.13, -3767.82) * mm});
            skLineSegment(sketch, "E315", {"start": v(-1795.13, -3767.82) * mm, "end": v(-1795.13, -3753.97) * mm});
            skLineSegment(sketch, "E316", {"start": v(-1795.13, -3753.97) * mm, "end": v(-1807.13, -3747.04) * mm});
            skLineSegment(sketch, "E317", {"start": v(-1807.13, -3747.04) * mm, "end": v(-1819.13, -3753.97) * mm});
            skLineSegment(sketch, "E318", {"start": v(-1819.13, -3753.97) * mm, "end": v(-1819.13, -3767.82) * mm});
            skLineSegment(sketch, "E319", {"start": v(-1819.13, -3767.82) * mm, "end": v(-1807.13, -3774.75) * mm});
            skLineSegment(sketch, "E320", {"start": v(-1786.13, -3190.9) * mm, "end": v(-1828.13, -3190.9) * mm});
            skLineSegment(sketch, "E321", {"start": v(-1807.13, -3211.9) * mm, "end": v(-1807.13, -3169.9) * mm});
            skLineSegment(sketch, "E322", {"start": v(-1795.13, -3183.97) * mm, "end": v(-1807.13, -3177.04) * mm});
            skLineSegment(sketch, "E323", {"start": v(-1795.13, -3197.82) * mm, "end": v(-1795.13, -3183.97) * mm});
            skLineSegment(sketch, "E324", {"start": v(-1807.13, -3204.75) * mm, "end": v(-1795.13, -3197.82) * mm});
            skLineSegment(sketch, "E325", {"start": v(-1819.13, -3197.82) * mm, "end": v(-1807.13, -3204.75) * mm});
            skLineSegment(sketch, "E326", {"start": v(-1819.13, -3183.97) * mm, "end": v(-1819.13, -3197.82) * mm});
            skLineSegment(sketch, "E327", {"start": v(-1807.13, -3177.04) * mm, "end": v(-1819.13, -3183.97) * mm});
            skLineSegment(sketch, "E328", {"start": v(-2157.13, -3169.9) * mm, "end": v(-2157.13, -3211.9) * mm});
            skLineSegment(sketch, "E329", {"start": v(-2136.13, -3190.9) * mm, "end": v(-2178.13, -3190.9) * mm});
            skLineSegment(sketch, "E330", {"start": v(-2157.13, -3177.04) * mm, "end": v(-2169.13, -3183.97) * mm});
            skLineSegment(sketch, "E331", {"start": v(-2169.13, -3183.97) * mm, "end": v(-2169.13, -3197.82) * mm});
            skLineSegment(sketch, "E332", {"start": v(-2169.13, -3197.82) * mm, "end": v(-2157.13, -3204.75) * mm});
            skLineSegment(sketch, "E333", {"start": v(-2157.13, -3204.75) * mm, "end": v(-2145.13, -3197.82) * mm});
            skLineSegment(sketch, "E334", {"start": v(-2145.13, -3197.82) * mm, "end": v(-2145.13, -3183.97) * mm});
            skLineSegment(sketch, "E335", {"start": v(-2145.13, -3183.97) * mm, "end": v(-2157.13, -3177.04) * mm});
            skLineSegment(sketch, "E336", {"start": v(-2169.13, -3767.82) * mm, "end": v(-2157.13, -3774.75) * mm});
            skLineSegment(sketch, "E337", {"start": v(-2169.13, -3753.97) * mm, "end": v(-2169.13, -3767.82) * mm});
            skLineSegment(sketch, "E338", {"start": v(-2157.13, -3747.04) * mm, "end": v(-2169.13, -3753.97) * mm});
            skLineSegment(sketch, "E339", {"start": v(-2145.13, -3753.97) * mm, "end": v(-2157.13, -3747.04) * mm});
            skLineSegment(sketch, "E340", {"start": v(-2145.13, -3767.82) * mm, "end": v(-2145.13, -3753.97) * mm});
            skLineSegment(sketch, "E341", {"start": v(-2157.13, -3774.75) * mm, "end": v(-2145.13, -3767.82) * mm});
            skLineSegment(sketch, "E342", {"start": v(-2157.13, -3739.9) * mm, "end": v(-2157.13, -3781.9) * mm});
            skLineSegment(sketch, "E343", {"start": v(-2178.13, -3760.9) * mm, "end": v(-2136.13, -3760.9) * mm});
            skLineSegment(sketch, "E344", {"start": v(-2197.13, -3790.9) * mm, "end": v(-1917.98, -3790.9) * mm});
            skLineSegment(sketch, "E345", {"start": v(-1977.13, -3496.5) * mm, "end": v(-1977.13, -3484.5) * mm});
            skLineSegment(sketch, "E346", {"start": v(-2027.13, -3358.55) * mm, "end": v(-2027.13, -3484.44) * mm});
            skLineSegment(sketch, "E347", {"start": v(-1977.13, -3496.5) * mm, "end": v(-1982.13, -3496.5) * mm});
            skLineSegment(sketch, "E348", {"start": v(-1977.13, -3484.5) * mm, "end": v(-1977.13, -3496.5) * mm});
            skLineSegment(sketch, "E349", {"start": v(-1982.13, -3496.5) * mm, "end": v(-2027.13, -3484.44) * mm});
            skLineSegment(sketch, "E350", {"start": v(-1982.13, -3346.5) * mm, "end": v(-1977.13, -3346.5) * mm});
            skLineSegment(sketch, "E351", {"start": v(-2027.13, -3358.55) * mm, "end": v(-1982.13, -3346.5) * mm});
            skLineSegment(sketch, "E352", {"start": v(-1982.13, -3582.8) * mm, "end": v(-2027.13, -3570.74) * mm});
            skLineSegment(sketch, "E353", {"start": v(-1977.13, -3517.2) * mm, "end": v(-1977.13, -3505.2) * mm});
            skLineSegment(sketch, "E354", {"start": v(-1977.13, -3570.8) * mm, "end": v(-1977.13, -3582.8) * mm});
            skLineSegment(sketch, "E355", {"start": v(-1977.13, -3582.8) * mm, "end": v(-1982.13, -3582.8) * mm});
            skLineSegment(sketch, "E356", {"start": v(-2027.13, -3505.2) * mm, "end": v(-2027.13, -3570.74) * mm});
            skLineSegment(sketch, "E357", {"start": v(-2027.13, -3505.2) * mm, "end": v(-1977.13, -3505.2) * mm});
            skLineSegment(sketch, "E358", {"start": v(-1882.13, -3595.9) * mm, "end": v(-2082.13, -3595.9) * mm});
            skLineSegment(sketch, "E359", {"start": v(-2082.13, -3355.9) * mm, "end": v(-2017.21, -3355.9) * mm});
            skLineSegment(sketch, "E360", {"start": v(-2063.73, -3383.9) * mm, "end": v(-2027.13, -3383.9) * mm});
            skLineSegment(sketch, "E361", {"start": v(-2082.13, -3375.9) * mm, "end": v(-2027.13, -3375.9) * mm});
            skLineSegment(sketch, "E362", {"start": v(-2063.73, -3567.9) * mm, "end": v(-2027.13, -3567.9) * mm});
            skLineSegment(sketch, "E363", {"start": v(-2082.13, -3575.9) * mm, "end": v(-2008.06, -3575.9) * mm});
            skLineSegment(sketch, "E364", {"start": v(-2074.13, -3394.3) * mm, "end": v(-2074.13, -3557.5) * mm});
            skLineSegment(sketch, "E365", {"start": v(-2097.13, -3602.9) * mm, "end": v(-2097.13, -3225.9) * mm});
            skLineSegment(sketch, "E366", {"start": v(-2082.13, -3225.9) * mm, "end": v(-2082.13, -3602.9) * mm});
            skLineSegment(sketch, "E367", {"start": v(-2097.13, -3225.9) * mm, "end": v(-2082.13, -3225.9) * mm});
            skLineSegment(sketch, "E368", {"start": v(-2197.13, -3160.9) * mm, "end": v(-2197.13, -3602.9) * mm});
            skLineSegment(sketch, "E369", {"start": v(-2197.13, -3735.9) * mm, "end": v(-1767.13, -3735.9) * mm});
            skLineSegment(sketch, "E370", {"start": v(-2136.13, -3265.9) * mm, "end": v(-2178.13, -3265.9) * mm});
            skLineSegment(sketch, "E371", {"start": v(-2157.13, -3244.9) * mm, "end": v(-2157.13, -3286.9) * mm});
            skLineSegment(sketch, "E372", {"start": v(-1767.13, -3215.9) * mm, "end": v(-1937.13, -3215.9) * mm});
            skLineSegment(sketch, "E373", {"start": v(-2128.15, -3475.9) * mm, "end": v(-1767.13, -3475.9) * mm});
            skLineSegment(sketch, "E374", {"start": v(-2157.13, -3234.14) * mm, "end": v(-2184.63, -3250.02) * mm});
            skLineSegment(sketch, "E375", {"start": v(-2184.63, -3250.02) * mm, "end": v(-2184.63, -3281.77) * mm});
            skLineSegment(sketch, "E376", {"start": v(-2184.63, -3281.77) * mm, "end": v(-2157.13, -3297.65) * mm});
            skLineSegment(sketch, "E377", {"start": v(-2157.13, -3297.65) * mm, "end": v(-2129.63, -3281.77) * mm});
            skLineSegment(sketch, "E378", {"start": v(-2129.63, -3281.77) * mm, "end": v(-2129.63, -3250.02) * mm});
            skLineSegment(sketch, "E379", {"start": v(-2129.63, -3250.02) * mm, "end": v(-2157.13, -3234.14) * mm});
            skLineSegment(sketch, "E380", {"start": v(-2178.13, -3685.9) * mm, "end": v(-2136.13, -3685.9) * mm});
            skLineSegment(sketch, "E381", {"start": v(-2157.13, -3664.9) * mm, "end": v(-2157.13, -3706.9) * mm});
            skLineSegment(sketch, "E382", {"start": v(-2184.63, -3701.77) * mm, "end": v(-2157.13, -3717.65) * mm});
            skLineSegment(sketch, "E383", {"start": v(-2184.63, -3670.02) * mm, "end": v(-2184.63, -3701.77) * mm});
            skLineSegment(sketch, "E384", {"start": v(-2157.13, -3654.14) * mm, "end": v(-2184.63, -3670.02) * mm});
            skLineSegment(sketch, "E385", {"start": v(-2129.63, -3670.02) * mm, "end": v(-2157.13, -3654.14) * mm});
            skLineSegment(sketch, "E386", {"start": v(-2129.63, -3701.77) * mm, "end": v(-2129.63, -3670.02) * mm});
            skLineSegment(sketch, "E387", {"start": v(-2157.13, -3717.65) * mm, "end": v(-2129.63, -3701.77) * mm});
            skLineSegment(sketch, "E388", {"start": v(-1786.13, -3265.9) * mm, "end": v(-1828.13, -3265.9) * mm});
            skLineSegment(sketch, "E389", {"start": v(-1807.13, -3286.9) * mm, "end": v(-1807.13, -3244.9) * mm});
            skLineSegment(sketch, "E390", {"start": v(-1779.63, -3250.02) * mm, "end": v(-1807.13, -3234.14) * mm});
            skLineSegment(sketch, "E391", {"start": v(-1779.63, -3281.77) * mm, "end": v(-1779.63, -3250.02) * mm});
            skLineSegment(sketch, "E392", {"start": v(-1807.13, -3297.65) * mm, "end": v(-1779.63, -3281.77) * mm});
            skLineSegment(sketch, "E393", {"start": v(-1834.63, -3281.77) * mm, "end": v(-1807.13, -3297.65) * mm});
            skLineSegment(sketch, "E394", {"start": v(-1834.63, -3250.02) * mm, "end": v(-1834.63, -3281.77) * mm});
            skLineSegment(sketch, "E395", {"start": v(-1807.13, -3234.14) * mm, "end": v(-1834.63, -3250.02) * mm});
            skLineSegment(sketch, "E396", {"start": v(-1959.63, -3431.4) * mm, "end": v(-1959.63, -3411.6) * mm});
            skLineSegment(sketch, "E397", {"start": v(-1989.63, -3409.8) * mm, "end": v(-1989.63, -3360.8) * mm});
            skLineSegment(sketch, "E398", {"start": v(-1904.63, -3360.8) * mm, "end": v(-1904.63, -3409.8) * mm});
            skLineSegment(sketch, "E399", {"start": v(-1989.13, -3360.3) * mm, "end": v(-1989.63, -3360.8) * mm});
            skLineSegment(sketch, "E400", {"start": v(-1989.13, -3410.3) * mm, "end": v(-1989.63, -3409.8) * mm});
            skLineSegment(sketch, "E401", {"start": v(-1905.13, -3410.3) * mm, "end": v(-1904.63, -3409.8) * mm});
            skLineSegment(sketch, "E402", {"start": v(-1905.13, -3360.3) * mm, "end": v(-1904.63, -3360.8) * mm});
            skLineSegment(sketch, "E403", {"start": v(-1905.13, -3410.3) * mm, "end": v(-1989.13, -3410.3) * mm});
            skLineSegment(sketch, "E404", {"start": v(-1989.13, -3360.3) * mm, "end": v(-1905.13, -3360.3) * mm});
            skLineSegment(sketch, "E405", {"start": v(-1947.13, -3375.54) * mm, "end": v(-1947.13, -3458.2) * mm});
            skLineSegment(sketch, "E406", {"start": v(-1977.13, -3358.5) * mm, "end": v(-1977.13, -3346.5) * mm});
            skLineSegment(sketch, "E407", {"start": v(-1917.13, -3346.5) * mm, "end": v(-1977.13, -3346.5) * mm});
            skLineSegment(sketch, "E408", {"start": v(-1917.13, -3505.2) * mm, "end": v(-1977.13, -3505.2) * mm});
            skLineSegment(sketch, "E409", {"start": v(-1989.63, -3568.5) * mm, "end": v(-1989.63, -3519.5) * mm});
            skLineSegment(sketch, "E410", {"start": v(-1905.13, -3569) * mm, "end": v(-1989.13, -3569) * mm});
            skLineSegment(sketch, "E411", {"start": v(-1904.63, -3519.5) * mm, "end": v(-1904.63, -3568.5) * mm});
            skLineSegment(sketch, "E412", {"start": v(-1989.63, -3568.5) * mm, "end": v(-1989.13, -3569) * mm});
            skLineSegment(sketch, "E413", {"start": v(-1989.63, -3519.5) * mm, "end": v(-1989.13, -3519) * mm});
            skLineSegment(sketch, "E414", {"start": v(-1904.63, -3519.5) * mm, "end": v(-1905.13, -3519) * mm});
            skLineSegment(sketch, "E415", {"start": v(-1904.63, -3568.5) * mm, "end": v(-1905.13, -3569) * mm});
            skLineSegment(sketch, "E416", {"start": v(-1989.13, -3519) * mm, "end": v(-1905.13, -3519) * mm});
            skLineSegment(sketch, "E417", {"start": v(-1947.13, -3485.8) * mm, "end": v(-1947.13, -3584.95) * mm});
            skLineSegment(sketch, "E418", {"start": v(-1977.13, -3582.8) * mm, "end": v(-1917.13, -3582.8) * mm});
            skLineSegment(sketch, "E419", {"start": v(-1989.63, -3482.2) * mm, "end": v(-1989.63, -3433.2) * mm});
            skLineSegment(sketch, "E420", {"start": v(-1905.13, -3482.7) * mm, "end": v(-1989.13, -3482.7) * mm});
            skLineSegment(sketch, "E421", {"start": v(-1904.63, -3433.2) * mm, "end": v(-1904.63, -3482.2) * mm});
            skLineSegment(sketch, "E422", {"start": v(-1989.63, -3482.2) * mm, "end": v(-1989.13, -3482.7) * mm});
            skLineSegment(sketch, "E423", {"start": v(-1989.63, -3433.2) * mm, "end": v(-1989.13, -3432.7) * mm});
            skLineSegment(sketch, "E424", {"start": v(-1904.63, -3433.2) * mm, "end": v(-1905.13, -3432.7) * mm});
            skLineSegment(sketch, "E425", {"start": v(-1904.63, -3482.2) * mm, "end": v(-1905.13, -3482.7) * mm});
            skLineSegment(sketch, "E426", {"start": v(-1989.13, -3432.7) * mm, "end": v(-1905.13, -3432.7) * mm});
            skLineSegment(sketch, "E427", {"start": v(-1934.63, -3411.6) * mm, "end": v(-1934.63, -3431.4) * mm});
            skLineSegment(sketch, "E428", {"start": v(-1977.13, -3496.5) * mm, "end": v(-1917.13, -3496.5) * mm});
            skLineSegment(sketch, "E429", {"start": v(-1987.13, -3432.7) * mm, "end": v(-1987.13, -3410.3) * mm});
            skLineSegment(sketch, "E430", {"start": v(-1907.13, -3432.7) * mm, "end": v(-1907.13, -3410.3) * mm});
            skLineSegment(sketch, "E431", {"start": v(-1917.13, -3346.5) * mm, "end": v(-1917.13, -3358.5) * mm});
            skLineSegment(sketch, "E432", {"start": v(-1917.13, -3484.5) * mm, "end": v(-1917.13, -3496.5) * mm});
            skLineSegment(sketch, "E433", {"start": v(-1917.13, -3505.2) * mm, "end": v(-1917.13, -3517.2) * mm});
            skLineSegment(sketch, "E434", {"start": v(-1917.13, -3570.8) * mm, "end": v(-1917.13, -3582.8) * mm});
            skLineSegment(sketch, "E435", {"start": v(-1917.13, -3579) * mm, "end": v(-1907.13, -3579) * mm});
            skLineSegment(sketch, "E436", {"start": v(-1907.13, -3579) * mm, "end": v(-1907.13, -3569) * mm});
            skLineSegment(sketch, "E437", {"start": v(-1917.13, -3509) * mm, "end": v(-1907.13, -3509) * mm});
            skLineSegment(sketch, "E438", {"start": v(-1907.13, -3509) * mm, "end": v(-1907.13, -3519) * mm});
            skLineSegment(sketch, "E439", {"start": v(-1917.13, -3352.5) * mm, "end": v(-1907.13, -3352.5) * mm});
            skLineSegment(sketch, "E440", {"start": v(-1907.13, -3352.5) * mm, "end": v(-1907.13, -3360.3) * mm});
            skLineSegment(sketch, "E441", {"start": v(-1917.13, -3490.5) * mm, "end": v(-1907.13, -3490.5) * mm});
            skLineSegment(sketch, "E442", {"start": v(-1907.13, -3490.5) * mm, "end": v(-1907.13, -3482.7) * mm});
            skLineSegment(sketch, "E443", {"start": v(-1882.13, -3602.9) * mm, "end": v(-1882.13, -3551.5) * mm});
            skLineSegment(sketch, "E444", {"start": v(-1882.13, -3225.9) * mm, "end": v(-1867.13, -3225.9) * mm});
            skLineSegment(sketch, "E445", {"start": v(-1867.13, -3225.9) * mm, "end": v(-1867.13, -3410) * mm});
            skLineSegment(sketch, "E446", {"start": v(-1828.13, -3685.9) * mm, "end": v(-1786.13, -3685.9) * mm});
            skLineSegment(sketch, "E447", {"start": v(-1807.13, -3706.9) * mm, "end": v(-1807.13, -3664.9) * mm});
            skLineSegment(sketch, "E448", {"start": v(-1807.13, -3717.65) * mm, "end": v(-1779.63, -3701.77) * mm});
            skLineSegment(sketch, "E449", {"start": v(-1779.63, -3701.77) * mm, "end": v(-1779.63, -3670.02) * mm});
            skLineSegment(sketch, "E450", {"start": v(-1779.63, -3670.02) * mm, "end": v(-1807.13, -3654.14) * mm});
            skLineSegment(sketch, "E451", {"start": v(-1807.13, -3654.14) * mm, "end": v(-1834.63, -3670.02) * mm});
            skLineSegment(sketch, "E452", {"start": v(-1834.63, -3670.02) * mm, "end": v(-1834.63, -3701.77) * mm});
            skLineSegment(sketch, "E453", {"start": v(-1834.63, -3701.77) * mm, "end": v(-1807.13, -3717.65) * mm});
            skLineSegment(sketch, "E454", {"start": v(-1882.13, -3575.9) * mm, "end": v(-1907.13, -3575.9) * mm});
            skLineSegment(sketch, "E455", {"start": v(-1882.13, -3375.9) * mm, "end": v(-1904.63, -3375.9) * mm});
            skLineSegment(sketch, "E456", {"start": v(-1890.13, -3557.5) * mm, "end": v(-1890.13, -3551.5) * mm});
            skLineSegment(sketch, "E457", {"start": v(-1907.13, -3355.9) * mm, "end": v(-1882.13, -3355.9) * mm});
            skLineSegment(sketch, "E458", {"start": v(-1900.53, -3383.9) * mm, "end": v(-1904.63, -3383.9) * mm});
            skLineSegment(sketch, "E459", {"start": v(-1900.53, -3567.9) * mm, "end": v(-1904.63, -3567.9) * mm});
            skLineSegment(sketch, "E460", {"start": v(-1904.63, -3536.5) * mm, "end": v(-1859, -3536.5) * mm});
            skLineSegment(sketch, "E461", {"start": v(-1859, -3536.5) * mm, "end": v(-1859, -3538) * mm});
            skLineSegment(sketch, "E462", {"start": v(-1859, -3538) * mm, "end": v(-1822, -3538) * mm});
            skLineSegment(sketch, "E463", {"start": v(-1859, -3550) * mm, "end": v(-1859, -3551.5) * mm});
            skLineSegment(sketch, "E464", {"start": v(-1859, -3551.5) * mm, "end": v(-1904.63, -3551.5) * mm});
            skLineSegment(sketch, "E465", {"start": v(-1834, -3535) * mm, "end": v(-1834, -3553) * mm});
            skLineSegment(sketch, "E466", {"start": v(-1822, -3550) * mm, "end": v(-1841, -3550) * mm});
            skLineSegment(sketch, "E467", {"start": v(-1841, -3550) * mm, "end": v(-1846, -3550) * mm});
            skLineSegment(sketch, "E468", {"start": v(-1846, -3550) * mm, "end": v(-1859, -3550) * mm});
            skLineSegment(sketch, "E469", {"start": v(-1859, -3410) * mm, "end": v(-1859, -3412) * mm});
            skLineSegment(sketch, "E470", {"start": v(-1859, -3412) * mm, "end": v(-1818, -3412) * mm});
            skLineSegment(sketch, "E471", {"start": v(-1859, -3428) * mm, "end": v(-1859, -3430) * mm});
            skLineSegment(sketch, "E472", {"start": v(-1834, -3408.5) * mm, "end": v(-1834, -3431.5) * mm});
            skLineSegment(sketch, "E473", {"start": v(-1818, -3433) * mm, "end": v(-1818, -3407) * mm});
            skLineSegment(sketch, "E474", {"start": v(-1818, -3428) * mm, "end": v(-1843, -3428) * mm});
            skLineSegment(sketch, "E475", {"start": v(-1846, -3428) * mm, "end": v(-1859, -3428) * mm});
            skLineSegment(sketch, "E476", {"start": v(-1904.63, -3410) * mm, "end": v(-1859, -3410) * mm});
            skLineSegment(sketch, "E477", {"start": v(-1859, -3430) * mm, "end": v(-1907.13, -3430) * mm});
            skLineSegment(sketch, "E478", {"start": v(-1819.07, -3420) * mm, "end": v(-1849.07, -3420) * mm});
            skLineSegment(sketch, "E479", {"start": v(-1859, -3412) * mm, "end": v(-1843, -3412) * mm});
            skLineSegment(sketch, "E480", {"start": v(-1843, -3428) * mm, "end": v(-1850, -3428) * mm});
            skLineSegment(sketch, "E481", {"start": v(-1850, -3428) * mm, "end": v(-1859, -3428) * mm});
            skLineSegment(sketch, "E482", {"start": v(-1846, -3534) * mm, "end": v(-1844, -3532) * mm});
            skLineSegment(sketch, "E483", {"start": v(-1824, -3532) * mm, "end": v(-1822, -3534) * mm});
            skLineSegment(sketch, "E484", {"start": v(-1824, -3532) * mm, "end": v(-1844, -3532) * mm});
            skLineSegment(sketch, "E485", {"start": v(-1822, -3554) * mm, "end": v(-1822, -3534) * mm});
            skLineSegment(sketch, "E486", {"start": v(-1846, -3554) * mm, "end": v(-1846, -3550) * mm});
            skLineSegment(sketch, "E487", {"start": v(-1824, -3556) * mm, "end": v(-1844, -3556) * mm});
            skLineSegment(sketch, "E488", {"start": v(-1846, -3554) * mm, "end": v(-1844, -3556) * mm});
            skLineSegment(sketch, "E489", {"start": v(-1824, -3556) * mm, "end": v(-1822, -3554) * mm});
            skLineSegment(sketch, "E490", {"start": v(-1846, -3538) * mm, "end": v(-1846, -3534) * mm});
            skLineSegment(sketch, "E491", {"start": v(-1809, -3525) * mm, "end": v(-1809, -3563) * mm});
            skLineSegment(sketch, "E492", {"start": v(-1859, -3563) * mm, "end": v(-1859, -3551.5) * mm});
            skLineSegment(sketch, "E493", {"start": v(-1815, -3519) * mm, "end": v(-1853, -3519) * mm});
            skLineSegment(sketch, "E494", {"start": v(-1815, -3569) * mm, "end": v(-1853, -3569) * mm});
            skLineSegment(sketch, "E495", {"start": v(-1859, -3536.5) * mm, "end": v(-1859, -3524.5) * mm});
            skLineSegment(sketch, "E496", {"start": v(-1890.13, -3536.5) * mm, "end": v(-1890.13, -3430) * mm});
            skLineSegment(sketch, "E497", {"start": v(-1882.13, -3536.5) * mm, "end": v(-1882.13, -3430) * mm});
            skLineSegment(sketch, "E498", {"start": v(-1867.13, -3551.5) * mm, "end": v(-1867.13, -3602.9) * mm});
            skLineSegment(sketch, "E499", {"start": v(-1890.13, -3410) * mm, "end": v(-1890.13, -3394.3) * mm});
            skLineSegment(sketch, "E500", {"start": v(-1882.13, -3410) * mm, "end": v(-1882.13, -3225.9) * mm});
            skLineSegment(sketch, "E501", {"start": v(-1867.13, -3430) * mm, "end": v(-1867.13, -3536.5) * mm});
            skLineSegment(sketch, "E502", {"start": v(-1803, -3394.76) * mm, "end": v(-1803, -3441.26) * mm});
            skLineSegment(sketch, "E503", {"start": v(-1810.54, -3388.75) * mm, "end": v(-1857.04, -3388.75) * mm});
            skLineSegment(sketch, "E504", {"start": v(-1810.54, -3451.24) * mm, "end": v(-1857.04, -3451.24) * mm});
            skLineSegment(sketch, "E505", {"start": v(-1865, -3441.26) * mm, "end": v(-1865, -3430) * mm});
            skLineSegment(sketch, "E506", {"start": v(-1818, -3407) * mm, "end": v(-1821, -3404) * mm});
            skLineSegment(sketch, "E507", {"start": v(-1821, -3404) * mm, "end": v(-1847, -3404) * mm});
            skLineSegment(sketch, "E508", {"start": v(-1825, -3404) * mm, "end": v(-1825, -3403) * mm});
            skLineSegment(sketch, "E509", {"start": v(-1821, -3436) * mm, "end": v(-1847, -3436) * mm});
            skLineSegment(sketch, "E510", {"start": v(-1850, -3433) * mm, "end": v(-1847, -3436) * mm});
            skLineSegment(sketch, "E511", {"start": v(-1850, -3433) * mm, "end": v(-1850, -3428) * mm});
            skLineSegment(sketch, "E512", {"start": v(-1847, -3404) * mm, "end": v(-1850, -3407) * mm});
            skLineSegment(sketch, "E513", {"start": v(-1821, -3436) * mm, "end": v(-1818, -3433) * mm});
            skLineSegment(sketch, "E514", {"start": v(-1850, -3412) * mm, "end": v(-1850, -3407) * mm});
            skLineSegment(sketch, "E515", {"start": v(-1865, -3410) * mm, "end": v(-1865, -3398.73) * mm});
            skLineSegment(sketch, "E516", {"start": v(-1882.13, -3338.9) * mm, "end": v(-1882.13, -3355.9) * mm});
            skLineSegment(sketch, "E517", {"start": v(-1982.13, -3776.6) * mm, "end": v(-1982.13, -3170) * mm});
            skLineSegment(sketch, "E518", {"start": v(-1937.13, -3177.5) * mm, "end": v(-1937.13, -3338.9) * mm});
            skLineSegment(sketch, "E519", {"start": v(-2027.13, -3177.5) * mm, "end": v(-2027.13, -3338.9) * mm});
            skLineSegment(sketch, "E520", {"start": v(-2082.13, -3355.9) * mm, "end": v(-2082.13, -3338.9) * mm});
            skLineSegment(sketch, "E521", {"start": v(-2082.13, -3338.9) * mm, "end": v(-1882.13, -3338.9) * mm});
            skLineSegment(sketch, "E522", {"start": v(-2027.13, -3215.9) * mm, "end": v(-2197.13, -3215.9) * mm});
            skLineSegment(sketch, "E523", {"start": v(-1767.13, -3602.9) * mm, "end": v(-1767.13, -3160.9) * mm});
            skLineSegment(sketch, "E524", {"start": v(-1767.13, -3790.9) * mm, "end": v(-1767.13, -3602.9) * mm});
            skLineSegment(sketch, "E525", {"start": v(-2197.13, -3602.9) * mm, "end": v(-2197.13, -3775.5) * mm});
            skLineSegment(sketch, "E526", {"start": v(-2197.13, -3775.5) * mm, "end": v(-2197.13, -3790.9) * mm});
            skLineSegment(sketch, "E527", {"start": v(371.87, -3760.9) * mm, "end": v(413.87, -3760.9) * mm});
            skLineSegment(sketch, "E528", {"start": v(392.87, -3781.9) * mm, "end": v(392.87, -3739.9) * mm});
            skLineSegment(sketch, "E529", {"start": v(392.87, -3774.75) * mm, "end": v(404.87, -3767.82) * mm});
            skLineSegment(sketch, "E530", {"start": v(404.87, -3767.82) * mm, "end": v(404.87, -3753.97) * mm});
            skLineSegment(sketch, "E531", {"start": v(404.87, -3753.97) * mm, "end": v(392.87, -3747.04) * mm});
            skLineSegment(sketch, "E532", {"start": v(392.87, -3747.04) * mm, "end": v(380.87, -3753.97) * mm});
            skLineSegment(sketch, "E533", {"start": v(380.87, -3753.97) * mm, "end": v(380.87, -3767.82) * mm});
            skLineSegment(sketch, "E534", {"start": v(380.87, -3767.82) * mm, "end": v(392.87, -3774.75) * mm});
            skLineSegment(sketch, "E535", {"start": v(413.87, -3190.9) * mm, "end": v(371.87, -3190.9) * mm});
            skLineSegment(sketch, "E536", {"start": v(392.87, -3211.9) * mm, "end": v(392.87, -3169.9) * mm});
            skLineSegment(sketch, "E537", {"start": v(404.87, -3183.97) * mm, "end": v(392.87, -3177.04) * mm});
            skLineSegment(sketch, "E538", {"start": v(404.87, -3197.82) * mm, "end": v(404.87, -3183.97) * mm});
            skLineSegment(sketch, "E539", {"start": v(392.87, -3204.75) * mm, "end": v(404.87, -3197.82) * mm});
            skLineSegment(sketch, "E540", {"start": v(380.87, -3197.82) * mm, "end": v(392.87, -3204.75) * mm});
            skLineSegment(sketch, "E541", {"start": v(380.87, -3183.97) * mm, "end": v(380.87, -3197.82) * mm});
            skLineSegment(sketch, "E542", {"start": v(392.87, -3177.04) * mm, "end": v(380.87, -3183.97) * mm});
            skLineSegment(sketch, "E543", {"start": v(42.87, -3169.9) * mm, "end": v(42.87, -3211.9) * mm});
            skLineSegment(sketch, "E544", {"start": v(63.87, -3190.9) * mm, "end": v(21.87, -3190.9) * mm});
            skLineSegment(sketch, "E545", {"start": v(42.87, -3177.04) * mm, "end": v(30.87, -3183.97) * mm});
            skLineSegment(sketch, "E546", {"start": v(30.87, -3183.97) * mm, "end": v(30.87, -3197.82) * mm});
            skLineSegment(sketch, "E547", {"start": v(30.87, -3197.82) * mm, "end": v(42.87, -3204.75) * mm});
            skLineSegment(sketch, "E548", {"start": v(42.87, -3204.75) * mm, "end": v(54.87, -3197.82) * mm});
            skLineSegment(sketch, "E549", {"start": v(54.87, -3197.82) * mm, "end": v(54.87, -3183.97) * mm});
            skLineSegment(sketch, "E550", {"start": v(54.87, -3183.97) * mm, "end": v(42.87, -3177.04) * mm});
            skLineSegment(sketch, "E551", {"start": v(30.87, -3767.82) * mm, "end": v(42.87, -3774.75) * mm});
            skLineSegment(sketch, "E552", {"start": v(30.87, -3753.97) * mm, "end": v(30.87, -3767.82) * mm});
            skLineSegment(sketch, "E553", {"start": v(42.87, -3747.04) * mm, "end": v(30.87, -3753.97) * mm});
            skLineSegment(sketch, "E554", {"start": v(54.87, -3753.97) * mm, "end": v(42.87, -3747.04) * mm});
            skLineSegment(sketch, "E555", {"start": v(54.87, -3767.82) * mm, "end": v(54.87, -3753.97) * mm});
            skLineSegment(sketch, "E556", {"start": v(42.87, -3774.75) * mm, "end": v(54.87, -3767.82) * mm});
            skLineSegment(sketch, "E557", {"start": v(42.87, -3739.9) * mm, "end": v(42.87, -3781.9) * mm});
            skLineSegment(sketch, "E558", {"start": v(21.87, -3760.9) * mm, "end": v(63.87, -3760.9) * mm});
            skLineSegment(sketch, "E559", {"start": v(2.87, -3790.9) * mm, "end": v(432.87, -3790.9) * mm});
            skLineSegment(sketch, "E560", {"start": v(2.87, -3160.9) * mm, "end": v(432.87, -3160.9) * mm});
            skLineSegment(sketch, "E561", {"start": v(222.87, -3496.5) * mm, "end": v(222.87, -3484.5) * mm});
            skLineSegment(sketch, "E562", {"start": v(172.87, -3358.55) * mm, "end": v(172.87, -3484.44) * mm});
            skLineSegment(sketch, "E563", {"start": v(222.87, -3496.5) * mm, "end": v(217.87, -3496.5) * mm});
            skLineSegment(sketch, "E564", {"start": v(222.87, -3484.5) * mm, "end": v(222.87, -3496.5) * mm});
            skLineSegment(sketch, "E565", {"start": v(217.87, -3496.5) * mm, "end": v(172.87, -3484.44) * mm});
            skLineSegment(sketch, "E566", {"start": v(217.87, -3346.5) * mm, "end": v(222.87, -3346.5) * mm});
            skLineSegment(sketch, "E567", {"start": v(172.87, -3358.55) * mm, "end": v(217.87, -3346.5) * mm});
            skLineSegment(sketch, "E568", {"start": v(217.87, -3582.8) * mm, "end": v(172.87, -3570.74) * mm});
            skLineSegment(sketch, "E569", {"start": v(222.87, -3517.2) * mm, "end": v(222.87, -3505.2) * mm});
            skLineSegment(sketch, "E570", {"start": v(222.87, -3570.8) * mm, "end": v(222.87, -3582.8) * mm});
            skLineSegment(sketch, "E571", {"start": v(222.87, -3582.8) * mm, "end": v(217.87, -3582.8) * mm});
            skLineSegment(sketch, "E572", {"start": v(172.87, -3505.2) * mm, "end": v(172.87, -3570.74) * mm});
            skLineSegment(sketch, "E573", {"start": v(172.87, -3505.2) * mm, "end": v(222.87, -3505.2) * mm});
            skLineSegment(sketch, "E574", {"start": v(317.87, -3595.9) * mm, "end": v(117.87, -3595.9) * mm});
            skLineSegment(sketch, "E575", {"start": v(117.87, -3355.9) * mm, "end": v(182.79, -3355.9) * mm});
            skLineSegment(sketch, "E576", {"start": v(136.27, -3383.9) * mm, "end": v(172.87, -3383.9) * mm});
            skLineSegment(sketch, "E577", {"start": v(117.87, -3375.9) * mm, "end": v(172.87, -3375.9) * mm});
            skLineSegment(sketch, "E578", {"start": v(136.27, -3567.9) * mm, "end": v(172.87, -3567.9) * mm});
            skLineSegment(sketch, "E579", {"start": v(117.87, -3575.9) * mm, "end": v(191.94, -3575.9) * mm});
            skLineSegment(sketch, "E580", {"start": v(125.87, -3394.3) * mm, "end": v(125.87, -3557.5) * mm});
            skLineSegment(sketch, "E581", {"start": v(102.87, -3602.9) * mm, "end": v(102.87, -3225.9) * mm});
            skLineSegment(sketch, "E582", {"start": v(117.87, -3225.9) * mm, "end": v(117.87, -3602.9) * mm});
            skLineSegment(sketch, "E583", {"start": v(102.87, -3225.9) * mm, "end": v(117.87, -3225.9) * mm});
            skLineSegment(sketch, "E584", {"start": v(2.87, -3160.9) * mm, "end": v(2.87, -3602.9) * mm});
            skLineSegment(sketch, "E585", {"start": v(2.87, -3735.9) * mm, "end": v(432.87, -3735.9) * mm});
            skLineSegment(sketch, "E586", {"start": v(63.87, -3265.9) * mm, "end": v(21.87, -3265.9) * mm});
            skLineSegment(sketch, "E587", {"start": v(42.87, -3244.9) * mm, "end": v(42.87, -3286.9) * mm});
            skLineSegment(sketch, "E588", {"start": v(432.87, -3790.9) * mm, "end": v(432.87, -3775.5) * mm});
            skLineSegment(sketch, "E589", {"start": v(71.85, -3475.9) * mm, "end": v(432.87, -3475.9) * mm});
            skLineSegment(sketch, "E590", {"start": v(42.87, -3234.14) * mm, "end": v(15.37, -3250.02) * mm});
            skLineSegment(sketch, "E591", {"start": v(15.37, -3250.02) * mm, "end": v(15.37, -3281.77) * mm});
            skLineSegment(sketch, "E592", {"start": v(15.37, -3281.77) * mm, "end": v(42.87, -3297.65) * mm});
            skLineSegment(sketch, "E593", {"start": v(42.87, -3297.65) * mm, "end": v(70.37, -3281.77) * mm});
            skLineSegment(sketch, "E594", {"start": v(70.37, -3281.77) * mm, "end": v(70.37, -3250.02) * mm});
            skLineSegment(sketch, "E595", {"start": v(70.37, -3250.02) * mm, "end": v(42.87, -3234.14) * mm});
            skLineSegment(sketch, "E596", {"start": v(21.87, -3685.9) * mm, "end": v(63.87, -3685.9) * mm});
            skLineSegment(sketch, "E597", {"start": v(42.87, -3664.9) * mm, "end": v(42.87, -3706.9) * mm});
            skLineSegment(sketch, "E598", {"start": v(15.37, -3701.77) * mm, "end": v(42.87, -3717.65) * mm});
            skLineSegment(sketch, "E599", {"start": v(15.37, -3670.02) * mm, "end": v(15.37, -3701.77) * mm});
            skLineSegment(sketch, "E600", {"start": v(42.87, -3654.14) * mm, "end": v(15.37, -3670.02) * mm});
            skLineSegment(sketch, "E601", {"start": v(70.37, -3670.02) * mm, "end": v(42.87, -3654.14) * mm});
            skLineSegment(sketch, "E602", {"start": v(70.37, -3701.77) * mm, "end": v(70.37, -3670.02) * mm});
            skLineSegment(sketch, "E603", {"start": v(42.87, -3717.65) * mm, "end": v(70.37, -3701.77) * mm});
            skLineSegment(sketch, "E604", {"start": v(413.87, -3265.9) * mm, "end": v(371.87, -3265.9) * mm});
            skLineSegment(sketch, "E605", {"start": v(392.87, -3286.9) * mm, "end": v(392.87, -3244.9) * mm});
            skLineSegment(sketch, "E606", {"start": v(420.37, -3250.02) * mm, "end": v(392.87, -3234.14) * mm});
            skLineSegment(sketch, "E607", {"start": v(420.37, -3281.77) * mm, "end": v(420.37, -3250.02) * mm});
            skLineSegment(sketch, "E608", {"start": v(392.87, -3297.65) * mm, "end": v(420.37, -3281.77) * mm});
            skLineSegment(sketch, "E609", {"start": v(365.37, -3281.77) * mm, "end": v(392.87, -3297.65) * mm});
            skLineSegment(sketch, "E610", {"start": v(365.37, -3250.02) * mm, "end": v(365.37, -3281.77) * mm});
            skLineSegment(sketch, "E611", {"start": v(392.87, -3234.14) * mm, "end": v(365.37, -3250.02) * mm});
            skLineSegment(sketch, "E612", {"start": v(240.37, -3431.4) * mm, "end": v(240.37, -3411.6) * mm});
            skLineSegment(sketch, "E613", {"start": v(210.37, -3409.8) * mm, "end": v(210.37, -3360.8) * mm});
            skLineSegment(sketch, "E614", {"start": v(295.37, -3360.8) * mm, "end": v(295.37, -3409.8) * mm});
            skLineSegment(sketch, "E615", {"start": v(210.87, -3360.3) * mm, "end": v(210.37, -3360.8) * mm});
            skLineSegment(sketch, "E616", {"start": v(210.87, -3410.3) * mm, "end": v(210.37, -3409.8) * mm});
            skLineSegment(sketch, "E617", {"start": v(294.87, -3410.3) * mm, "end": v(295.37, -3409.8) * mm});
            skLineSegment(sketch, "E618", {"start": v(294.87, -3360.3) * mm, "end": v(295.37, -3360.8) * mm});
            skLineSegment(sketch, "E619", {"start": v(294.87, -3410.3) * mm, "end": v(210.87, -3410.3) * mm});
            skLineSegment(sketch, "E620", {"start": v(210.87, -3360.3) * mm, "end": v(294.87, -3360.3) * mm});
            skLineSegment(sketch, "E621", {"start": v(252.87, -3375.54) * mm, "end": v(252.87, -3458.2) * mm});
            skLineSegment(sketch, "E622", {"start": v(222.87, -3358.5) * mm, "end": v(222.87, -3346.5) * mm});
            skLineSegment(sketch, "E623", {"start": v(282.87, -3346.5) * mm, "end": v(222.87, -3346.5) * mm});
            skLineSegment(sketch, "E624", {"start": v(282.87, -3505.2) * mm, "end": v(222.87, -3505.2) * mm});
            skLineSegment(sketch, "E625", {"start": v(210.37, -3568.5) * mm, "end": v(210.37, -3519.5) * mm});
            skLineSegment(sketch, "E626", {"start": v(294.87, -3569) * mm, "end": v(210.87, -3569) * mm});
            skLineSegment(sketch, "E627", {"start": v(295.37, -3519.5) * mm, "end": v(295.37, -3568.5) * mm});
            skLineSegment(sketch, "E628", {"start": v(210.37, -3568.5) * mm, "end": v(210.87, -3569) * mm});
            skLineSegment(sketch, "E629", {"start": v(210.37, -3519.5) * mm, "end": v(210.87, -3519) * mm});
            skLineSegment(sketch, "E630", {"start": v(295.37, -3519.5) * mm, "end": v(294.87, -3519) * mm});
            skLineSegment(sketch, "E631", {"start": v(295.37, -3568.5) * mm, "end": v(294.87, -3569) * mm});
            skLineSegment(sketch, "E632", {"start": v(210.87, -3519) * mm, "end": v(294.87, -3519) * mm});
            skLineSegment(sketch, "E633", {"start": v(252.87, -3485.8) * mm, "end": v(252.87, -3584.95) * mm});
            skLineSegment(sketch, "E634", {"start": v(222.87, -3582.8) * mm, "end": v(282.87, -3582.8) * mm});
            skLineSegment(sketch, "E635", {"start": v(210.37, -3482.2) * mm, "end": v(210.37, -3433.2) * mm});
            skLineSegment(sketch, "E636", {"start": v(294.87, -3482.7) * mm, "end": v(210.87, -3482.7) * mm});
            skLineSegment(sketch, "E637", {"start": v(295.37, -3433.2) * mm, "end": v(295.37, -3482.2) * mm});
            skLineSegment(sketch, "E638", {"start": v(210.37, -3482.2) * mm, "end": v(210.87, -3482.7) * mm});
            skLineSegment(sketch, "E639", {"start": v(210.37, -3433.2) * mm, "end": v(210.87, -3432.7) * mm});
            skLineSegment(sketch, "E640", {"start": v(295.37, -3433.2) * mm, "end": v(294.87, -3432.7) * mm});
            skLineSegment(sketch, "E641", {"start": v(295.37, -3482.2) * mm, "end": v(294.87, -3482.7) * mm});
            skLineSegment(sketch, "E642", {"start": v(210.87, -3432.7) * mm, "end": v(294.87, -3432.7) * mm});
            skLineSegment(sketch, "E643", {"start": v(265.37, -3411.6) * mm, "end": v(265.37, -3431.4) * mm});
            skLineSegment(sketch, "E644", {"start": v(222.87, -3496.5) * mm, "end": v(282.87, -3496.5) * mm});
            skLineSegment(sketch, "E645", {"start": v(212.87, -3432.7) * mm, "end": v(212.87, -3410.3) * mm});
            skLineSegment(sketch, "E646", {"start": v(292.87, -3432.7) * mm, "end": v(292.87, -3410.3) * mm});
            skLineSegment(sketch, "E647", {"start": v(282.87, -3346.5) * mm, "end": v(282.87, -3358.5) * mm});
            skLineSegment(sketch, "E648", {"start": v(282.87, -3484.5) * mm, "end": v(282.87, -3496.5) * mm});
            skLineSegment(sketch, "E649", {"start": v(282.87, -3505.2) * mm, "end": v(282.87, -3517.2) * mm});
            skLineSegment(sketch, "E650", {"start": v(282.87, -3570.8) * mm, "end": v(282.87, -3582.8) * mm});
            skLineSegment(sketch, "E651", {"start": v(282.87, -3579) * mm, "end": v(292.87, -3579) * mm});
            skLineSegment(sketch, "E652", {"start": v(292.87, -3579) * mm, "end": v(292.87, -3569) * mm});
            skLineSegment(sketch, "E653", {"start": v(282.87, -3509) * mm, "end": v(292.87, -3509) * mm});
            skLineSegment(sketch, "E654", {"start": v(292.87, -3509) * mm, "end": v(292.87, -3519) * mm});
            skLineSegment(sketch, "E655", {"start": v(282.87, -3352.5) * mm, "end": v(292.87, -3352.5) * mm});
            skLineSegment(sketch, "E656", {"start": v(292.87, -3352.5) * mm, "end": v(292.87, -3360.3) * mm});
            skLineSegment(sketch, "E657", {"start": v(282.87, -3490.5) * mm, "end": v(292.87, -3490.5) * mm});
            skLineSegment(sketch, "E658", {"start": v(292.87, -3490.5) * mm, "end": v(292.87, -3482.7) * mm});
            skLineSegment(sketch, "E659", {"start": v(317.87, -3602.9) * mm, "end": v(317.87, -3551.5) * mm});
            skLineSegment(sketch, "E660", {"start": v(317.87, -3225.9) * mm, "end": v(332.87, -3225.9) * mm});
            skLineSegment(sketch, "E661", {"start": v(332.87, -3225.9) * mm, "end": v(332.87, -3410) * mm});
            skLineSegment(sketch, "E662", {"start": v(371.87, -3685.9) * mm, "end": v(413.87, -3685.9) * mm});
            skLineSegment(sketch, "E663", {"start": v(392.87, -3706.9) * mm, "end": v(392.87, -3664.9) * mm});
            skLineSegment(sketch, "E664", {"start": v(392.87, -3717.65) * mm, "end": v(420.37, -3701.77) * mm});
            skLineSegment(sketch, "E665", {"start": v(420.37, -3701.77) * mm, "end": v(420.37, -3670.02) * mm});
            skLineSegment(sketch, "E666", {"start": v(420.37, -3670.02) * mm, "end": v(392.87, -3654.14) * mm});
            skLineSegment(sketch, "E667", {"start": v(392.87, -3654.14) * mm, "end": v(365.37, -3670.02) * mm});
            skLineSegment(sketch, "E668", {"start": v(365.37, -3670.02) * mm, "end": v(365.37, -3701.77) * mm});
            skLineSegment(sketch, "E669", {"start": v(365.37, -3701.77) * mm, "end": v(392.87, -3717.65) * mm});
            skLineSegment(sketch, "E670", {"start": v(317.87, -3575.9) * mm, "end": v(292.87, -3575.9) * mm});
            skLineSegment(sketch, "E671", {"start": v(317.87, -3375.9) * mm, "end": v(295.37, -3375.9) * mm});
            skLineSegment(sketch, "E672", {"start": v(309.87, -3557.5) * mm, "end": v(309.87, -3551.5) * mm});
            skLineSegment(sketch, "E673", {"start": v(292.87, -3355.9) * mm, "end": v(317.87, -3355.9) * mm});
            skLineSegment(sketch, "E674", {"start": v(299.47, -3383.9) * mm, "end": v(295.37, -3383.9) * mm});
            skLineSegment(sketch, "E675", {"start": v(299.47, -3567.9) * mm, "end": v(295.37, -3567.9) * mm});
            skLineSegment(sketch, "E676", {"start": v(295.37, -3536.5) * mm, "end": v(341, -3536.5) * mm});
            skLineSegment(sketch, "E677", {"start": v(341, -3536.5) * mm, "end": v(341, -3538) * mm});
            skLineSegment(sketch, "E678", {"start": v(341, -3538) * mm, "end": v(378, -3538) * mm});
            skLineSegment(sketch, "E679", {"start": v(341, -3550) * mm, "end": v(341, -3551.5) * mm});
            skLineSegment(sketch, "E680", {"start": v(341, -3551.5) * mm, "end": v(295.37, -3551.5) * mm});
            skLineSegment(sketch, "E681", {"start": v(366, -3535) * mm, "end": v(366, -3553) * mm});
            skLineSegment(sketch, "E682", {"start": v(378, -3550) * mm, "end": v(359, -3550) * mm});
            skLineSegment(sketch, "E683", {"start": v(359, -3550) * mm, "end": v(354, -3550) * mm});
            skLineSegment(sketch, "E684", {"start": v(354, -3550) * mm, "end": v(341, -3550) * mm});
            skLineSegment(sketch, "E685", {"start": v(341, -3410) * mm, "end": v(341, -3412) * mm});
            skLineSegment(sketch, "E686", {"start": v(341, -3412) * mm, "end": v(382, -3412) * mm});
            skLineSegment(sketch, "E687", {"start": v(341, -3428) * mm, "end": v(341, -3430) * mm});
            skLineSegment(sketch, "E688", {"start": v(366, -3408.5) * mm, "end": v(366, -3431.5) * mm});
            skLineSegment(sketch, "E689", {"start": v(382, -3433) * mm, "end": v(382, -3407) * mm});
            skLineSegment(sketch, "E690", {"start": v(382, -3428) * mm, "end": v(357, -3428) * mm});
            skLineSegment(sketch, "E691", {"start": v(354, -3428) * mm, "end": v(341, -3428) * mm});
            skLineSegment(sketch, "E692", {"start": v(295.37, -3410) * mm, "end": v(341, -3410) * mm});
            skLineSegment(sketch, "E693", {"start": v(341, -3430) * mm, "end": v(292.87, -3430) * mm});
            skLineSegment(sketch, "E694", {"start": v(380.93, -3420) * mm, "end": v(350.93, -3420) * mm});
            skLineSegment(sketch, "E695", {"start": v(341, -3412) * mm, "end": v(357, -3412) * mm});
            skLineSegment(sketch, "E696", {"start": v(357, -3428) * mm, "end": v(350, -3428) * mm});
            skLineSegment(sketch, "E697", {"start": v(350, -3428) * mm, "end": v(341, -3428) * mm});
            skLineSegment(sketch, "E698", {"start": v(354, -3534) * mm, "end": v(356, -3532) * mm});
            skLineSegment(sketch, "E699", {"start": v(376, -3532) * mm, "end": v(378, -3534) * mm});
            skLineSegment(sketch, "E700", {"start": v(376, -3532) * mm, "end": v(356, -3532) * mm});
            skLineSegment(sketch, "E701", {"start": v(378, -3554) * mm, "end": v(378, -3534) * mm});
            skLineSegment(sketch, "E702", {"start": v(354, -3554) * mm, "end": v(354, -3550) * mm});
            skLineSegment(sketch, "E703", {"start": v(376, -3556) * mm, "end": v(356, -3556) * mm});
            skLineSegment(sketch, "E704", {"start": v(354, -3554) * mm, "end": v(356, -3556) * mm});
            skLineSegment(sketch, "E705", {"start": v(376, -3556) * mm, "end": v(378, -3554) * mm});
            skLineSegment(sketch, "E706", {"start": v(354, -3538) * mm, "end": v(354, -3534) * mm});
            skLineSegment(sketch, "E707", {"start": v(391, -3525) * mm, "end": v(391, -3563) * mm});
            skLineSegment(sketch, "E708", {"start": v(341, -3563) * mm, "end": v(341, -3551.5) * mm});
            skLineSegment(sketch, "E709", {"start": v(385, -3519) * mm, "end": v(347, -3519) * mm});
            skLineSegment(sketch, "E710", {"start": v(385, -3569) * mm, "end": v(347, -3569) * mm});
            skLineSegment(sketch, "E711", {"start": v(341, -3536.5) * mm, "end": v(341, -3524.5) * mm});
            skLineSegment(sketch, "E712", {"start": v(309.87, -3536.5) * mm, "end": v(309.87, -3430) * mm});
            skLineSegment(sketch, "E713", {"start": v(317.87, -3536.5) * mm, "end": v(317.87, -3430) * mm});
            skLineSegment(sketch, "E714", {"start": v(332.87, -3551.5) * mm, "end": v(332.87, -3602.9) * mm});
            skLineSegment(sketch, "E715", {"start": v(309.87, -3410) * mm, "end": v(309.87, -3394.3) * mm});
            skLineSegment(sketch, "E716", {"start": v(317.87, -3410) * mm, "end": v(317.87, -3225.9) * mm});
            skLineSegment(sketch, "E717", {"start": v(332.87, -3430) * mm, "end": v(332.87, -3536.5) * mm});
            skLineSegment(sketch, "E718", {"start": v(397, -3394.76) * mm, "end": v(397, -3441.26) * mm});
            skLineSegment(sketch, "E719", {"start": v(389.46, -3388.75) * mm, "end": v(342.96, -3388.75) * mm});
            skLineSegment(sketch, "E720", {"start": v(389.46, -3451.24) * mm, "end": v(342.96, -3451.24) * mm});
            skLineSegment(sketch, "E721", {"start": v(335, -3441.26) * mm, "end": v(335, -3430) * mm});
            skLineSegment(sketch, "E722", {"start": v(382, -3407) * mm, "end": v(379, -3404) * mm});
            skLineSegment(sketch, "E723", {"start": v(379, -3404) * mm, "end": v(353, -3404) * mm});
            skLineSegment(sketch, "E724", {"start": v(375, -3404) * mm, "end": v(375, -3403) * mm});
            skLineSegment(sketch, "E725", {"start": v(379, -3436) * mm, "end": v(353, -3436) * mm});
            skLineSegment(sketch, "E726", {"start": v(350, -3433) * mm, "end": v(353, -3436) * mm});
            skLineSegment(sketch, "E727", {"start": v(350, -3433) * mm, "end": v(350, -3428) * mm});
            skLineSegment(sketch, "E728", {"start": v(353, -3404) * mm, "end": v(350, -3407) * mm});
            skLineSegment(sketch, "E729", {"start": v(379, -3436) * mm, "end": v(382, -3433) * mm});
            skLineSegment(sketch, "E730", {"start": v(350, -3412) * mm, "end": v(350, -3407) * mm});
            skLineSegment(sketch, "E731", {"start": v(335, -3410) * mm, "end": v(335, -3398.73) * mm});
            skLineSegment(sketch, "E732", {"start": v(317.87, -3338.9) * mm, "end": v(317.87, -3355.9) * mm});
            skLineSegment(sketch, "E733", {"start": v(217.87, -3776.6) * mm, "end": v(217.87, -3170) * mm});
            skLineSegment(sketch, "E734", {"start": v(117.87, -3355.9) * mm, "end": v(117.87, -3338.9) * mm});
            skLineSegment(sketch, "E735", {"start": v(117.87, -3338.9) * mm, "end": v(317.87, -3338.9) * mm});
            skLineSegment(sketch, "E736", {"start": v(432.87, -3215.9) * mm, "end": v(2.87, -3215.9) * mm});
            skLineSegment(sketch, "E737", {"start": v(432.87, -3602.9) * mm, "end": v(432.87, -3160.9) * mm});
            skLineSegment(sketch, "E738", {"start": v(432.87, -3775.5) * mm, "end": v(432.87, -3602.9) * mm});
            skLineSegment(sketch, "E739", {"start": v(2.87, -3602.9) * mm, "end": v(2.87, -3775.5) * mm});
            skLineSegment(sketch, "E740", {"start": v(2.87, -3775.5) * mm, "end": v(2.87, -3790.9) * mm});
            skLineSegment(sketch, "E741", {"start": v(2871.87, -3760.9) * mm, "end": v(2913.87, -3760.9) * mm});
            skLineSegment(sketch, "E742", {"start": v(2892.87, -3781.9) * mm, "end": v(2892.87, -3739.9) * mm});
            skLineSegment(sketch, "E743", {"start": v(2892.87, -3774.75) * mm, "end": v(2904.87, -3767.82) * mm});
            skLineSegment(sketch, "E744", {"start": v(2904.87, -3767.82) * mm, "end": v(2904.87, -3753.97) * mm});
            skLineSegment(sketch, "E745", {"start": v(2904.87, -3753.97) * mm, "end": v(2892.87, -3747.04) * mm});
            skLineSegment(sketch, "E746", {"start": v(2892.87, -3747.04) * mm, "end": v(2880.87, -3753.97) * mm});
            skLineSegment(sketch, "E747", {"start": v(2880.87, -3753.97) * mm, "end": v(2880.87, -3767.82) * mm});
            skLineSegment(sketch, "E748", {"start": v(2880.87, -3767.82) * mm, "end": v(2892.87, -3774.75) * mm});
            skLineSegment(sketch, "E749", {"start": v(2913.87, -3190.9) * mm, "end": v(2871.87, -3190.9) * mm});
            skLineSegment(sketch, "E750", {"start": v(2892.87, -3211.9) * mm, "end": v(2892.87, -3169.9) * mm});
            skLineSegment(sketch, "E751", {"start": v(2904.87, -3183.97) * mm, "end": v(2892.87, -3177.04) * mm});
            skLineSegment(sketch, "E752", {"start": v(2904.87, -3197.82) * mm, "end": v(2904.87, -3183.97) * mm});
            skLineSegment(sketch, "E753", {"start": v(2892.87, -3204.75) * mm, "end": v(2904.87, -3197.82) * mm});
            skLineSegment(sketch, "E754", {"start": v(2880.87, -3197.82) * mm, "end": v(2892.87, -3204.75) * mm});
            skLineSegment(sketch, "E755", {"start": v(2880.87, -3183.97) * mm, "end": v(2880.87, -3197.82) * mm});
            skLineSegment(sketch, "E756", {"start": v(2892.87, -3177.04) * mm, "end": v(2880.87, -3183.97) * mm});
            skLineSegment(sketch, "E757", {"start": v(2542.87, -3169.9) * mm, "end": v(2542.87, -3211.9) * mm});
            skLineSegment(sketch, "E758", {"start": v(2563.87, -3190.9) * mm, "end": v(2521.87, -3190.9) * mm});
            skLineSegment(sketch, "E759", {"start": v(2542.87, -3177.04) * mm, "end": v(2530.87, -3183.97) * mm});
            skLineSegment(sketch, "E760", {"start": v(2530.87, -3183.97) * mm, "end": v(2530.87, -3197.82) * mm});
            skLineSegment(sketch, "E761", {"start": v(2530.87, -3197.82) * mm, "end": v(2542.87, -3204.75) * mm});
            skLineSegment(sketch, "E762", {"start": v(2542.87, -3204.75) * mm, "end": v(2554.87, -3197.82) * mm});
            skLineSegment(sketch, "E763", {"start": v(2554.87, -3197.82) * mm, "end": v(2554.87, -3183.97) * mm});
            skLineSegment(sketch, "E764", {"start": v(2554.87, -3183.97) * mm, "end": v(2542.87, -3177.04) * mm});
            skLineSegment(sketch, "E765", {"start": v(2530.87, -3767.82) * mm, "end": v(2542.87, -3774.75) * mm});
            skLineSegment(sketch, "E766", {"start": v(2530.87, -3753.97) * mm, "end": v(2530.87, -3767.82) * mm});
            skLineSegment(sketch, "E767", {"start": v(2542.87, -3747.04) * mm, "end": v(2530.87, -3753.97) * mm});
            skLineSegment(sketch, "E768", {"start": v(2554.87, -3753.97) * mm, "end": v(2542.87, -3747.04) * mm});
            skLineSegment(sketch, "E769", {"start": v(2554.87, -3767.82) * mm, "end": v(2554.87, -3753.97) * mm});
            skLineSegment(sketch, "E770", {"start": v(2542.87, -3774.75) * mm, "end": v(2554.87, -3767.82) * mm});
            skLineSegment(sketch, "E771", {"start": v(2542.87, -3739.9) * mm, "end": v(2542.87, -3781.9) * mm});
            skLineSegment(sketch, "E772", {"start": v(2521.87, -3760.9) * mm, "end": v(2563.87, -3760.9) * mm});
            skLineSegment(sketch, "E773", {"start": v(2502.87, -3790.9) * mm, "end": v(2932.87, -3790.9) * mm});
            skLineSegment(sketch, "E774", {"start": v(2502.87, -3160.9) * mm, "end": v(2932.87, -3160.9) * mm});
            skLineSegment(sketch, "E775", {"start": v(2722.87, -3496.5) * mm, "end": v(2722.87, -3484.5) * mm});
            skLineSegment(sketch, "E776", {"start": v(2672.87, -3358.55) * mm, "end": v(2672.87, -3484.44) * mm});
            skLineSegment(sketch, "E777", {"start": v(2722.87, -3496.5) * mm, "end": v(2717.87, -3496.5) * mm});
            skLineSegment(sketch, "E778", {"start": v(2722.87, -3484.5) * mm, "end": v(2722.87, -3496.5) * mm});
            skLineSegment(sketch, "E779", {"start": v(2717.87, -3496.5) * mm, "end": v(2672.87, -3484.44) * mm});
            skLineSegment(sketch, "E780", {"start": v(2717.87, -3346.5) * mm, "end": v(2722.87, -3346.5) * mm});
            skLineSegment(sketch, "E781", {"start": v(2672.87, -3358.55) * mm, "end": v(2717.87, -3346.5) * mm});
            skLineSegment(sketch, "E782", {"start": v(2717.87, -3582.8) * mm, "end": v(2672.87, -3570.74) * mm});
            skLineSegment(sketch, "E783", {"start": v(2722.87, -3517.2) * mm, "end": v(2722.87, -3505.2) * mm});
            skLineSegment(sketch, "E784", {"start": v(2722.87, -3570.8) * mm, "end": v(2722.87, -3582.8) * mm});
            skLineSegment(sketch, "E785", {"start": v(2722.87, -3582.8) * mm, "end": v(2717.87, -3582.8) * mm});
            skLineSegment(sketch, "E786", {"start": v(2672.87, -3505.2) * mm, "end": v(2672.87, -3570.74) * mm});
            skLineSegment(sketch, "E787", {"start": v(2672.87, -3505.2) * mm, "end": v(2722.87, -3505.2) * mm});
            skLineSegment(sketch, "E788", {"start": v(2817.87, -3595.9) * mm, "end": v(2617.87, -3595.9) * mm});
            skLineSegment(sketch, "E789", {"start": v(2617.87, -3355.9) * mm, "end": v(2682.79, -3355.9) * mm});
            skLineSegment(sketch, "E790", {"start": v(2636.27, -3383.9) * mm, "end": v(2672.87, -3383.9) * mm});
            skLineSegment(sketch, "E791", {"start": v(2617.87, -3375.9) * mm, "end": v(2672.87, -3375.9) * mm});
            skLineSegment(sketch, "E792", {"start": v(2636.27, -3567.9) * mm, "end": v(2672.87, -3567.9) * mm});
            skLineSegment(sketch, "E793", {"start": v(2617.87, -3575.9) * mm, "end": v(2691.94, -3575.9) * mm});
            skLineSegment(sketch, "E794", {"start": v(2625.87, -3394.3) * mm, "end": v(2625.87, -3557.5) * mm});
            skLineSegment(sketch, "E795", {"start": v(2602.87, -3602.9) * mm, "end": v(2602.87, -3225.9) * mm});
            skLineSegment(sketch, "E796", {"start": v(2617.87, -3225.9) * mm, "end": v(2617.87, -3602.9) * mm});
            skLineSegment(sketch, "E797", {"start": v(2602.87, -3225.9) * mm, "end": v(2617.87, -3225.9) * mm});
            skLineSegment(sketch, "E798", {"start": v(2502.87, -3160.9) * mm, "end": v(2502.87, -3602.9) * mm});
            skLineSegment(sketch, "E799", {"start": v(2502.87, -3735.9) * mm, "end": v(2932.87, -3735.9) * mm});
            skLineSegment(sketch, "E800", {"start": v(2563.87, -3265.9) * mm, "end": v(2521.87, -3265.9) * mm});
            skLineSegment(sketch, "E801", {"start": v(2542.87, -3244.9) * mm, "end": v(2542.87, -3286.9) * mm});
            skLineSegment(sketch, "E802", {"start": v(2932.87, -3790.9) * mm, "end": v(2932.87, -3775.5) * mm});
            skLineSegment(sketch, "E803", {"start": v(2571.85, -3475.9) * mm, "end": v(2932.87, -3475.9) * mm});
            skLineSegment(sketch, "E804", {"start": v(2542.87, -3234.14) * mm, "end": v(2515.37, -3250.02) * mm});
            skLineSegment(sketch, "E805", {"start": v(2515.37, -3250.02) * mm, "end": v(2515.37, -3281.77) * mm});
            skLineSegment(sketch, "E806", {"start": v(2515.37, -3281.77) * mm, "end": v(2542.87, -3297.65) * mm});
            skLineSegment(sketch, "E807", {"start": v(2542.87, -3297.65) * mm, "end": v(2570.37, -3281.77) * mm});
            skLineSegment(sketch, "E808", {"start": v(2570.37, -3281.77) * mm, "end": v(2570.37, -3250.02) * mm});
            skLineSegment(sketch, "E809", {"start": v(2570.37, -3250.02) * mm, "end": v(2542.87, -3234.14) * mm});
            skLineSegment(sketch, "E810", {"start": v(2521.87, -3685.9) * mm, "end": v(2563.87, -3685.9) * mm});
            skLineSegment(sketch, "E811", {"start": v(2542.87, -3664.9) * mm, "end": v(2542.87, -3706.9) * mm});
            skLineSegment(sketch, "E812", {"start": v(2515.37, -3701.77) * mm, "end": v(2542.87, -3717.65) * mm});
            skLineSegment(sketch, "E813", {"start": v(2515.37, -3670.02) * mm, "end": v(2515.37, -3701.77) * mm});
            skLineSegment(sketch, "E814", {"start": v(2542.87, -3654.14) * mm, "end": v(2515.37, -3670.02) * mm});
            skLineSegment(sketch, "E815", {"start": v(2570.37, -3670.02) * mm, "end": v(2542.87, -3654.14) * mm});
            skLineSegment(sketch, "E816", {"start": v(2570.37, -3701.77) * mm, "end": v(2570.37, -3670.02) * mm});
            skLineSegment(sketch, "E817", {"start": v(2542.87, -3717.65) * mm, "end": v(2570.37, -3701.77) * mm});
            skLineSegment(sketch, "E818", {"start": v(2913.87, -3265.9) * mm, "end": v(2871.87, -3265.9) * mm});
            skLineSegment(sketch, "E819", {"start": v(2892.87, -3286.9) * mm, "end": v(2892.87, -3244.9) * mm});
            skLineSegment(sketch, "E820", {"start": v(2920.37, -3250.02) * mm, "end": v(2892.87, -3234.14) * mm});
            skLineSegment(sketch, "E821", {"start": v(2920.37, -3281.77) * mm, "end": v(2920.37, -3250.02) * mm});
            skLineSegment(sketch, "E822", {"start": v(2892.87, -3297.65) * mm, "end": v(2920.37, -3281.77) * mm});
            skLineSegment(sketch, "E823", {"start": v(2865.37, -3281.77) * mm, "end": v(2892.87, -3297.65) * mm});
            skLineSegment(sketch, "E824", {"start": v(2865.37, -3250.02) * mm, "end": v(2865.37, -3281.77) * mm});
            skLineSegment(sketch, "E825", {"start": v(2892.87, -3234.14) * mm, "end": v(2865.37, -3250.02) * mm});
            skLineSegment(sketch, "E826", {"start": v(2740.37, -3431.4) * mm, "end": v(2740.37, -3411.6) * mm});
            skLineSegment(sketch, "E827", {"start": v(2710.37, -3409.8) * mm, "end": v(2710.37, -3360.8) * mm});
            skLineSegment(sketch, "E828", {"start": v(2795.37, -3360.8) * mm, "end": v(2795.37, -3409.8) * mm});
            skLineSegment(sketch, "E829", {"start": v(2710.87, -3360.3) * mm, "end": v(2710.37, -3360.8) * mm});
            skLineSegment(sketch, "E830", {"start": v(2710.87, -3410.3) * mm, "end": v(2710.37, -3409.8) * mm});
            skLineSegment(sketch, "E831", {"start": v(2794.87, -3410.3) * mm, "end": v(2795.37, -3409.8) * mm});
            skLineSegment(sketch, "E832", {"start": v(2794.87, -3360.3) * mm, "end": v(2795.37, -3360.8) * mm});
            skLineSegment(sketch, "E833", {"start": v(2794.87, -3410.3) * mm, "end": v(2710.87, -3410.3) * mm});
            skLineSegment(sketch, "E834", {"start": v(2710.87, -3360.3) * mm, "end": v(2794.87, -3360.3) * mm});
            skLineSegment(sketch, "E835", {"start": v(2752.87, -3375.54) * mm, "end": v(2752.87, -3458.2) * mm});
            skLineSegment(sketch, "E836", {"start": v(2722.87, -3358.5) * mm, "end": v(2722.87, -3346.5) * mm});
            skLineSegment(sketch, "E837", {"start": v(2782.87, -3346.5) * mm, "end": v(2722.87, -3346.5) * mm});
            skLineSegment(sketch, "E838", {"start": v(2782.87, -3505.2) * mm, "end": v(2722.87, -3505.2) * mm});
            skLineSegment(sketch, "E839", {"start": v(2710.37, -3568.5) * mm, "end": v(2710.37, -3519.5) * mm});
            skLineSegment(sketch, "E840", {"start": v(2794.87, -3569) * mm, "end": v(2710.87, -3569) * mm});
            skLineSegment(sketch, "E841", {"start": v(2795.37, -3519.5) * mm, "end": v(2795.37, -3568.5) * mm});
            skLineSegment(sketch, "E842", {"start": v(2710.37, -3568.5) * mm, "end": v(2710.87, -3569) * mm});
            skLineSegment(sketch, "E843", {"start": v(2710.37, -3519.5) * mm, "end": v(2710.87, -3519) * mm});
            skLineSegment(sketch, "E844", {"start": v(2795.37, -3519.5) * mm, "end": v(2794.87, -3519) * mm});
            skLineSegment(sketch, "E845", {"start": v(2795.37, -3568.5) * mm, "end": v(2794.87, -3569) * mm});
            skLineSegment(sketch, "E846", {"start": v(2710.87, -3519) * mm, "end": v(2794.87, -3519) * mm});
            skLineSegment(sketch, "E847", {"start": v(2752.87, -3485.8) * mm, "end": v(2752.87, -3584.95) * mm});
            skLineSegment(sketch, "E848", {"start": v(2722.87, -3582.8) * mm, "end": v(2782.87, -3582.8) * mm});
            skLineSegment(sketch, "E849", {"start": v(2710.37, -3482.2) * mm, "end": v(2710.37, -3433.2) * mm});
            skLineSegment(sketch, "E850", {"start": v(2794.87, -3482.7) * mm, "end": v(2710.87, -3482.7) * mm});
            skLineSegment(sketch, "E851", {"start": v(2795.37, -3433.2) * mm, "end": v(2795.37, -3482.2) * mm});
            skLineSegment(sketch, "E852", {"start": v(2710.37, -3482.2) * mm, "end": v(2710.87, -3482.7) * mm});
            skLineSegment(sketch, "E853", {"start": v(2710.37, -3433.2) * mm, "end": v(2710.87, -3432.7) * mm});
            skLineSegment(sketch, "E854", {"start": v(2795.37, -3433.2) * mm, "end": v(2794.87, -3432.7) * mm});
            skLineSegment(sketch, "E855", {"start": v(2795.37, -3482.2) * mm, "end": v(2794.87, -3482.7) * mm});
            skLineSegment(sketch, "E856", {"start": v(2710.87, -3432.7) * mm, "end": v(2794.87, -3432.7) * mm});
            skLineSegment(sketch, "E857", {"start": v(2765.37, -3411.6) * mm, "end": v(2765.37, -3431.4) * mm});
            skLineSegment(sketch, "E858", {"start": v(2722.87, -3496.5) * mm, "end": v(2782.87, -3496.5) * mm});
            skLineSegment(sketch, "E859", {"start": v(2712.87, -3432.7) * mm, "end": v(2712.87, -3410.3) * mm});
            skLineSegment(sketch, "E860", {"start": v(2792.87, -3432.7) * mm, "end": v(2792.87, -3410.3) * mm});
            skLineSegment(sketch, "E861", {"start": v(2782.87, -3346.5) * mm, "end": v(2782.87, -3358.5) * mm});
            skLineSegment(sketch, "E862", {"start": v(2782.87, -3484.5) * mm, "end": v(2782.87, -3496.5) * mm});
            skLineSegment(sketch, "E863", {"start": v(2782.87, -3505.2) * mm, "end": v(2782.87, -3517.2) * mm});
            skLineSegment(sketch, "E864", {"start": v(2782.87, -3570.8) * mm, "end": v(2782.87, -3582.8) * mm});
            skLineSegment(sketch, "E865", {"start": v(2782.87, -3579) * mm, "end": v(2792.87, -3579) * mm});
            skLineSegment(sketch, "E866", {"start": v(2792.87, -3579) * mm, "end": v(2792.87, -3569) * mm});
            skLineSegment(sketch, "E867", {"start": v(2782.87, -3509) * mm, "end": v(2792.87, -3509) * mm});
            skLineSegment(sketch, "E868", {"start": v(2792.87, -3509) * mm, "end": v(2792.87, -3519) * mm});
            skLineSegment(sketch, "E869", {"start": v(2782.87, -3352.5) * mm, "end": v(2792.87, -3352.5) * mm});
            skLineSegment(sketch, "E870", {"start": v(2792.87, -3352.5) * mm, "end": v(2792.87, -3360.3) * mm});
            skLineSegment(sketch, "E871", {"start": v(2782.87, -3490.5) * mm, "end": v(2792.87, -3490.5) * mm});
            skLineSegment(sketch, "E872", {"start": v(2792.87, -3490.5) * mm, "end": v(2792.87, -3482.7) * mm});
            skLineSegment(sketch, "E873", {"start": v(2817.87, -3602.9) * mm, "end": v(2817.87, -3551.5) * mm});
            skLineSegment(sketch, "E874", {"start": v(2817.87, -3225.9) * mm, "end": v(2832.87, -3225.9) * mm});
            skLineSegment(sketch, "E875", {"start": v(2832.87, -3225.9) * mm, "end": v(2832.87, -3410) * mm});
            skLineSegment(sketch, "E876", {"start": v(2871.87, -3685.9) * mm, "end": v(2913.87, -3685.9) * mm});
            skLineSegment(sketch, "E877", {"start": v(2892.87, -3706.9) * mm, "end": v(2892.87, -3664.9) * mm});
            skLineSegment(sketch, "E878", {"start": v(2892.87, -3717.65) * mm, "end": v(2920.37, -3701.77) * mm});
            skLineSegment(sketch, "E879", {"start": v(2920.37, -3701.77) * mm, "end": v(2920.37, -3670.02) * mm});
            skLineSegment(sketch, "E880", {"start": v(2920.37, -3670.02) * mm, "end": v(2892.87, -3654.14) * mm});
            skLineSegment(sketch, "E881", {"start": v(2892.87, -3654.14) * mm, "end": v(2865.37, -3670.02) * mm});
            skLineSegment(sketch, "E882", {"start": v(2865.37, -3670.02) * mm, "end": v(2865.37, -3701.77) * mm});
            skLineSegment(sketch, "E883", {"start": v(2865.37, -3701.77) * mm, "end": v(2892.87, -3717.65) * mm});
            skLineSegment(sketch, "E884", {"start": v(2817.87, -3575.9) * mm, "end": v(2792.87, -3575.9) * mm});
            skLineSegment(sketch, "E885", {"start": v(2817.87, -3375.9) * mm, "end": v(2795.37, -3375.9) * mm});
            skLineSegment(sketch, "E886", {"start": v(2809.87, -3557.5) * mm, "end": v(2809.87, -3551.5) * mm});
            skLineSegment(sketch, "E887", {"start": v(2792.87, -3355.9) * mm, "end": v(2817.87, -3355.9) * mm});
            skLineSegment(sketch, "E888", {"start": v(2799.47, -3383.9) * mm, "end": v(2795.37, -3383.9) * mm});
            skLineSegment(sketch, "E889", {"start": v(2799.47, -3567.9) * mm, "end": v(2795.37, -3567.9) * mm});
            skLineSegment(sketch, "E890", {"start": v(2795.37, -3536.5) * mm, "end": v(2841, -3536.5) * mm});
            skLineSegment(sketch, "E891", {"start": v(2841, -3536.5) * mm, "end": v(2841, -3538) * mm});
            skLineSegment(sketch, "E892", {"start": v(2841, -3538) * mm, "end": v(2878, -3538) * mm});
            skLineSegment(sketch, "E893", {"start": v(2841, -3550) * mm, "end": v(2841, -3551.5) * mm});
            skLineSegment(sketch, "E894", {"start": v(2841, -3551.5) * mm, "end": v(2795.37, -3551.5) * mm});
            skLineSegment(sketch, "E895", {"start": v(2866, -3535) * mm, "end": v(2866, -3553) * mm});
            skLineSegment(sketch, "E896", {"start": v(2878, -3550) * mm, "end": v(2859, -3550) * mm});
            skLineSegment(sketch, "E897", {"start": v(2859, -3550) * mm, "end": v(2854, -3550) * mm});
            skLineSegment(sketch, "E898", {"start": v(2854, -3550) * mm, "end": v(2841, -3550) * mm});
            skLineSegment(sketch, "E899", {"start": v(2841, -3410) * mm, "end": v(2841, -3412) * mm});
            skLineSegment(sketch, "E900", {"start": v(2841, -3412) * mm, "end": v(2882, -3412) * mm});
            skLineSegment(sketch, "E901", {"start": v(2841, -3428) * mm, "end": v(2841, -3430) * mm});
            skLineSegment(sketch, "E902", {"start": v(2866, -3408.5) * mm, "end": v(2866, -3431.5) * mm});
            skLineSegment(sketch, "E903", {"start": v(2882, -3433) * mm, "end": v(2882, -3407) * mm});
            skLineSegment(sketch, "E904", {"start": v(2882, -3428) * mm, "end": v(2857, -3428) * mm});
            skLineSegment(sketch, "E905", {"start": v(2854, -3428) * mm, "end": v(2841, -3428) * mm});
            skLineSegment(sketch, "E906", {"start": v(2795.37, -3410) * mm, "end": v(2841, -3410) * mm});
            skLineSegment(sketch, "E907", {"start": v(2841, -3430) * mm, "end": v(2792.87, -3430) * mm});
            skLineSegment(sketch, "E908", {"start": v(2880.93, -3420) * mm, "end": v(2850.93, -3420) * mm});
            skLineSegment(sketch, "E909", {"start": v(2841, -3412) * mm, "end": v(2857, -3412) * mm});
            skLineSegment(sketch, "E910", {"start": v(2857, -3428) * mm, "end": v(2850, -3428) * mm});
            skLineSegment(sketch, "E911", {"start": v(2850, -3428) * mm, "end": v(2841, -3428) * mm});
            skLineSegment(sketch, "E912", {"start": v(2854, -3534) * mm, "end": v(2856, -3532) * mm});
            skLineSegment(sketch, "E913", {"start": v(2876, -3532) * mm, "end": v(2878, -3534) * mm});
            skLineSegment(sketch, "E914", {"start": v(2876, -3532) * mm, "end": v(2856, -3532) * mm});
            skLineSegment(sketch, "E915", {"start": v(2878, -3554) * mm, "end": v(2878, -3534) * mm});
            skLineSegment(sketch, "E916", {"start": v(2854, -3554) * mm, "end": v(2854, -3550) * mm});
            skLineSegment(sketch, "E917", {"start": v(2876, -3556) * mm, "end": v(2856, -3556) * mm});
            skLineSegment(sketch, "E918", {"start": v(2854, -3554) * mm, "end": v(2856, -3556) * mm});
            skLineSegment(sketch, "E919", {"start": v(2876, -3556) * mm, "end": v(2878, -3554) * mm});
            skLineSegment(sketch, "E920", {"start": v(2854, -3538) * mm, "end": v(2854, -3534) * mm});
            skLineSegment(sketch, "E921", {"start": v(2891, -3525) * mm, "end": v(2891, -3563) * mm});
            skLineSegment(sketch, "E922", {"start": v(2841, -3563) * mm, "end": v(2841, -3551.5) * mm});
            skLineSegment(sketch, "E923", {"start": v(2885, -3519) * mm, "end": v(2847, -3519) * mm});
            skLineSegment(sketch, "E924", {"start": v(2885, -3569) * mm, "end": v(2847, -3569) * mm});
            skLineSegment(sketch, "E925", {"start": v(2841, -3536.5) * mm, "end": v(2841, -3524.5) * mm});
            skLineSegment(sketch, "E926", {"start": v(2809.87, -3536.5) * mm, "end": v(2809.87, -3430) * mm});
            skLineSegment(sketch, "E927", {"start": v(2817.87, -3536.5) * mm, "end": v(2817.87, -3430) * mm});
            skLineSegment(sketch, "E928", {"start": v(2832.87, -3551.5) * mm, "end": v(2832.87, -3602.9) * mm});
            skLineSegment(sketch, "E929", {"start": v(2809.87, -3410) * mm, "end": v(2809.87, -3394.3) * mm});
            skLineSegment(sketch, "E930", {"start": v(2817.87, -3410) * mm, "end": v(2817.87, -3225.9) * mm});
            skLineSegment(sketch, "E931", {"start": v(2832.87, -3430) * mm, "end": v(2832.87, -3536.5) * mm});
            skLineSegment(sketch, "E932", {"start": v(2897, -3394.76) * mm, "end": v(2897, -3441.26) * mm});
            skLineSegment(sketch, "E933", {"start": v(2889.46, -3388.75) * mm, "end": v(2842.96, -3388.75) * mm});
            skLineSegment(sketch, "E934", {"start": v(2889.46, -3451.24) * mm, "end": v(2842.96, -3451.24) * mm});
            skLineSegment(sketch, "E935", {"start": v(2835, -3441.26) * mm, "end": v(2835, -3430) * mm});
            skLineSegment(sketch, "E936", {"start": v(2882, -3407) * mm, "end": v(2879, -3404) * mm});
            skLineSegment(sketch, "E937", {"start": v(2879, -3404) * mm, "end": v(2853, -3404) * mm});
            skLineSegment(sketch, "E938", {"start": v(2875, -3404) * mm, "end": v(2875, -3403) * mm});
            skLineSegment(sketch, "E939", {"start": v(2879, -3436) * mm, "end": v(2853, -3436) * mm});
            skLineSegment(sketch, "E940", {"start": v(2850, -3433) * mm, "end": v(2853, -3436) * mm});
            skLineSegment(sketch, "E941", {"start": v(2850, -3433) * mm, "end": v(2850, -3428) * mm});
            skLineSegment(sketch, "E942", {"start": v(2853, -3404) * mm, "end": v(2850, -3407) * mm});
            skLineSegment(sketch, "E943", {"start": v(2879, -3436) * mm, "end": v(2882, -3433) * mm});
            skLineSegment(sketch, "E944", {"start": v(2850, -3412) * mm, "end": v(2850, -3407) * mm});
            skLineSegment(sketch, "E945", {"start": v(2835, -3410) * mm, "end": v(2835, -3398.73) * mm});
            skLineSegment(sketch, "E946", {"start": v(2817.87, -3338.9) * mm, "end": v(2817.87, -3355.9) * mm});
            skLineSegment(sketch, "E947", {"start": v(2717.87, -3776.6) * mm, "end": v(2717.87, -3170) * mm});
            skLineSegment(sketch, "E948", {"start": v(2617.87, -3355.9) * mm, "end": v(2617.87, -3338.9) * mm});
            skLineSegment(sketch, "E949", {"start": v(2617.87, -3338.9) * mm, "end": v(2817.87, -3338.9) * mm});
            skLineSegment(sketch, "E950", {"start": v(2932.87, -3215.9) * mm, "end": v(2502.87, -3215.9) * mm});
            skLineSegment(sketch, "E951", {"start": v(2932.87, -3602.9) * mm, "end": v(2932.87, -3160.9) * mm});
            skLineSegment(sketch, "E952", {"start": v(2932.87, -3775.5) * mm, "end": v(2932.87, -3602.9) * mm});
            skLineSegment(sketch, "E953", {"start": v(2502.87, -3602.9) * mm, "end": v(2502.87, -3775.5) * mm});
            skLineSegment(sketch, "E954", {"start": v(2502.87, -3775.5) * mm, "end": v(2502.87, -3790.9) * mm});
            skLineSegment(sketch, "E955", {"start": v(678.87, -3735.5) * mm, "end": v(2999.87, -3735.5) * mm});
            skLineSegment(sketch, "E956", {"start": v(-1526.13, -3735.5) * mm, "end": v(499.87, -3735.5) * mm});
            skLineSegment(sketch, "E957", {"start": v(-1747.13, -3679.5) * mm, "end": v(-1747.13, -3667.9) * mm});
            skLineSegment(sketch, "E958", {"start": v(-1867.13, -3679.5) * mm, "end": v(-1747.13, -3679.5) * mm});
            skLineSegment(sketch, "E959", {"start": v(-1867.13, -3667.9) * mm, "end": v(-1867.13, -3679.5) * mm});
            skLineSegment(sketch, "E960", {"start": v(-4428.13, -3700) * mm, "end": v(-4428.13, -3280) * mm});
            skLineSegment(sketch, "E961", {"start": v(-4428.13, -3280) * mm, "end": v(-4366.13, -3280) * mm});
            skLineSegment(sketch, "E962", {"start": v(-4366.13, -3280) * mm, "end": v(-4366.13, -3700) * mm});
            skLineSegment(sketch, "E963", {"start": v(-4366.13, -3700) * mm, "end": v(-4428.13, -3700) * mm});
            skLineSegment(sketch, "E964", {"start": v(-4428.13, -3290) * mm, "end": v(-4366.13, -3290) * mm});
            skLineSegment(sketch, "E965", {"start": v(-4428.13, -3690) * mm, "end": v(-4366.13, -3690) * mm});
            skLineSegment(sketch, "E966", {"start": v(-4368.13, -3290) * mm, "end": v(-4368.13, -3690) * mm});
            skLineSegment(sketch, "E967", {"start": v(-4382.13, -3290) * mm, "end": v(-4382.13, -3690) * mm});
            skLineSegment(sketch, "E968", {"start": v(-4412.13, -3290) * mm, "end": v(-4412.13, -3690) * mm});
            skLineSegment(sketch, "E969", {"start": v(-4426.13, -3290) * mm, "end": v(-4426.13, -3690) * mm});
            skLineSegment(sketch, "E970", {"start": v(-4447.13, -3655) * mm, "end": v(-4447.13, -3575) * mm});
            skLineSegment(sketch, "E971", {"start": v(-4447.13, -3575) * mm, "end": v(-4429.63, -3575) * mm});
            skLineSegment(sketch, "E972", {"start": v(-4347.13, -3575) * mm, "end": v(-4347.13, -3655) * mm});
            skLineSegment(sketch, "E973", {"start": v(-4347.13, -3655) * mm, "end": v(-4364.63, -3655) * mm});
            skLineSegment(sketch, "E974", {"start": v(-4429.63, -3654) * mm, "end": v(-4444.63, -3654) * mm});
            skLineSegment(sketch, "E975", {"start": v(-4444.63, -3654) * mm, "end": v(-4444.63, -3576) * mm});
            skLineSegment(sketch, "E976", {"start": v(-4444.63, -3576) * mm, "end": v(-4429.63, -3576) * mm});
            skLineSegment(sketch, "E977", {"start": v(-4429.63, -3655) * mm, "end": v(-4447.13, -3655) * mm});
            skLineSegment(sketch, "E978", {"start": v(-4364.63, -3575) * mm, "end": v(-4347.13, -3575) * mm});
            skLineSegment(sketch, "E979", {"start": v(-4349.63, -3576) * mm, "end": v(-4349.63, -3654) * mm});
            skLineSegment(sketch, "E980", {"start": v(-4349.63, -3654) * mm, "end": v(-4364.63, -3654) * mm});
            skLineSegment(sketch, "E981", {"start": v(-4364.63, -3576) * mm, "end": v(-4349.63, -3576) * mm});
            skLineSegment(sketch, "E982", {"start": v(-3028.13, -3700) * mm, "end": v(-3028.13, -3280) * mm});
            skLineSegment(sketch, "E983", {"start": v(-3028.13, -3280) * mm, "end": v(-2966.13, -3280) * mm});
            skLineSegment(sketch, "E984", {"start": v(-2966.13, -3280) * mm, "end": v(-2966.13, -3700) * mm});
            skLineSegment(sketch, "E985", {"start": v(-2966.13, -3700) * mm, "end": v(-3028.13, -3700) * mm});
            skLineSegment(sketch, "E986", {"start": v(-3028.13, -3290) * mm, "end": v(-2966.13, -3290) * mm});
            skLineSegment(sketch, "E987", {"start": v(-3028.13, -3690) * mm, "end": v(-2966.13, -3690) * mm});
            skLineSegment(sketch, "E988", {"start": v(-2968.13, -3290) * mm, "end": v(-2968.13, -3690) * mm});
            skLineSegment(sketch, "E989", {"start": v(-2982.13, -3290) * mm, "end": v(-2982.13, -3690) * mm});
            skLineSegment(sketch, "E990", {"start": v(-3012.13, -3290) * mm, "end": v(-3012.13, -3690) * mm});
            skLineSegment(sketch, "E991", {"start": v(-3026.13, -3290) * mm, "end": v(-3026.13, -3690) * mm});
            skLineSegment(sketch, "E992", {"start": v(-3047.13, -3655) * mm, "end": v(-3047.13, -3575) * mm});
            skLineSegment(sketch, "E993", {"start": v(-3047.13, -3575) * mm, "end": v(-3029.63, -3575) * mm});
            skLineSegment(sketch, "E994", {"start": v(-2947.13, -3575) * mm, "end": v(-2947.13, -3655) * mm});
            skLineSegment(sketch, "E995", {"start": v(-2947.13, -3655) * mm, "end": v(-2964.63, -3655) * mm});
            skLineSegment(sketch, "E996", {"start": v(-3029.63, -3654) * mm, "end": v(-3044.63, -3654) * mm});
            skLineSegment(sketch, "E997", {"start": v(-3044.63, -3654) * mm, "end": v(-3044.63, -3576) * mm});
            skLineSegment(sketch, "E998", {"start": v(-3044.63, -3576) * mm, "end": v(-3029.63, -3576) * mm});
            skLineSegment(sketch, "E999", {"start": v(-3029.63, -3655) * mm, "end": v(-3047.13, -3655) * mm});
            skLineSegment(sketch, "E1000", {"start": v(-2964.63, -3575) * mm, "end": v(-2947.13, -3575) * mm});
            skLineSegment(sketch, "E1001", {"start": v(-2949.63, -3576) * mm, "end": v(-2949.63, -3654) * mm});
            skLineSegment(sketch, "E1002", {"start": v(-2949.63, -3654) * mm, "end": v(-2964.63, -3654) * mm});
            skLineSegment(sketch, "E1003", {"start": v(-2964.63, -3576) * mm, "end": v(-2949.63, -3576) * mm});
            skLineSegment(sketch, "E1004", {"start": v(-1628.13, -3700) * mm, "end": v(-1628.13, -3280) * mm});
            skLineSegment(sketch, "E1005", {"start": v(-1628.13, -3280) * mm, "end": v(-1566.13, -3280) * mm});
            skLineSegment(sketch, "E1006", {"start": v(-1566.13, -3280) * mm, "end": v(-1566.13, -3700) * mm});
            skLineSegment(sketch, "E1007", {"start": v(-1566.13, -3700) * mm, "end": v(-1628.13, -3700) * mm});
            skLineSegment(sketch, "E1008", {"start": v(-1628.13, -3290) * mm, "end": v(-1566.13, -3290) * mm});
            skLineSegment(sketch, "E1009", {"start": v(-1628.13, -3690) * mm, "end": v(-1566.13, -3690) * mm});
            skLineSegment(sketch, "E1010", {"start": v(-1568.13, -3290) * mm, "end": v(-1568.13, -3690) * mm});
            skLineSegment(sketch, "E1011", {"start": v(-1582.13, -3290) * mm, "end": v(-1582.13, -3690) * mm});
            skLineSegment(sketch, "E1012", {"start": v(-1612.13, -3290) * mm, "end": v(-1612.13, -3690) * mm});
            skLineSegment(sketch, "E1013", {"start": v(-1626.13, -3290) * mm, "end": v(-1626.13, -3690) * mm});
            skLineSegment(sketch, "E1014", {"start": v(-1647.13, -3655) * mm, "end": v(-1647.13, -3575) * mm});
            skLineSegment(sketch, "E1015", {"start": v(-1647.13, -3575) * mm, "end": v(-1629.63, -3575) * mm});
            skLineSegment(sketch, "E1016", {"start": v(-1547.13, -3575) * mm, "end": v(-1547.13, -3655) * mm});
            skLineSegment(sketch, "E1017", {"start": v(-1547.13, -3655) * mm, "end": v(-1564.63, -3655) * mm});
            skLineSegment(sketch, "E1018", {"start": v(-1629.63, -3654) * mm, "end": v(-1644.63, -3654) * mm});
            skLineSegment(sketch, "E1019", {"start": v(-1644.63, -3654) * mm, "end": v(-1644.63, -3576) * mm});
            skLineSegment(sketch, "E1020", {"start": v(-1644.63, -3576) * mm, "end": v(-1629.63, -3576) * mm});
            skLineSegment(sketch, "E1021", {"start": v(-1629.63, -3655) * mm, "end": v(-1647.13, -3655) * mm});
            skLineSegment(sketch, "E1022", {"start": v(-1564.63, -3575) * mm, "end": v(-1547.13, -3575) * mm});
            skLineSegment(sketch, "E1023", {"start": v(-1549.63, -3576) * mm, "end": v(-1549.63, -3654) * mm});
            skLineSegment(sketch, "E1024", {"start": v(-1549.63, -3654) * mm, "end": v(-1564.63, -3654) * mm});
            skLineSegment(sketch, "E1025", {"start": v(-1564.63, -3576) * mm, "end": v(-1549.63, -3576) * mm});
            skLineSegment(sketch, "E1026", {"start": v(571.87, -3700) * mm, "end": v(571.87, -3280) * mm});
            skLineSegment(sketch, "E1027", {"start": v(571.87, -3280) * mm, "end": v(633.87, -3280) * mm});
            skLineSegment(sketch, "E1028", {"start": v(633.87, -3280) * mm, "end": v(633.87, -3700) * mm});
            skLineSegment(sketch, "E1029", {"start": v(633.87, -3700) * mm, "end": v(571.87, -3700) * mm});
            skLineSegment(sketch, "E1030", {"start": v(571.87, -3290) * mm, "end": v(633.87, -3290) * mm});
            skLineSegment(sketch, "E1031", {"start": v(571.87, -3690) * mm, "end": v(633.87, -3690) * mm});
            skLineSegment(sketch, "E1032", {"start": v(631.87, -3290) * mm, "end": v(631.87, -3690) * mm});
            skLineSegment(sketch, "E1033", {"start": v(617.87, -3290) * mm, "end": v(617.87, -3690) * mm});
            skLineSegment(sketch, "E1034", {"start": v(587.87, -3290) * mm, "end": v(587.87, -3690) * mm});
            skLineSegment(sketch, "E1035", {"start": v(573.87, -3290) * mm, "end": v(573.87, -3690) * mm});
            skLineSegment(sketch, "E1036", {"start": v(552.87, -3655) * mm, "end": v(552.87, -3575) * mm});
            skLineSegment(sketch, "E1037", {"start": v(552.87, -3575) * mm, "end": v(570.37, -3575) * mm});
            skLineSegment(sketch, "E1038", {"start": v(652.87, -3575) * mm, "end": v(652.87, -3655) * mm});
            skLineSegment(sketch, "E1039", {"start": v(652.87, -3655) * mm, "end": v(635.37, -3655) * mm});
            skLineSegment(sketch, "E1040", {"start": v(570.37, -3654) * mm, "end": v(555.37, -3654) * mm});
            skLineSegment(sketch, "E1041", {"start": v(555.37, -3654) * mm, "end": v(555.37, -3576) * mm});
            skLineSegment(sketch, "E1042", {"start": v(555.37, -3576) * mm, "end": v(570.37, -3576) * mm});
            skLineSegment(sketch, "E1043", {"start": v(570.37, -3655) * mm, "end": v(552.87, -3655) * mm});
            skLineSegment(sketch, "E1044", {"start": v(635.37, -3575) * mm, "end": v(652.87, -3575) * mm});
            skLineSegment(sketch, "E1045", {"start": v(650.37, -3576) * mm, "end": v(650.37, -3654) * mm});
            skLineSegment(sketch, "E1046", {"start": v(650.37, -3654) * mm, "end": v(635.37, -3654) * mm});
            skLineSegment(sketch, "E1047", {"start": v(635.37, -3576) * mm, "end": v(650.37, -3576) * mm});
            skLineSegment(sketch, "E1048", {"start": v(3071.87, -3700) * mm, "end": v(3071.87, -3280) * mm});
            skLineSegment(sketch, "E1049", {"start": v(3071.87, -3280) * mm, "end": v(3133.87, -3280) * mm});
            skLineSegment(sketch, "E1050", {"start": v(3133.87, -3280) * mm, "end": v(3133.87, -3700) * mm});
            skLineSegment(sketch, "E1051", {"start": v(3133.87, -3700) * mm, "end": v(3071.87, -3700) * mm});
            skLineSegment(sketch, "E1052", {"start": v(3071.87, -3290) * mm, "end": v(3133.87, -3290) * mm});
            skLineSegment(sketch, "E1053", {"start": v(3071.87, -3690) * mm, "end": v(3133.87, -3690) * mm});
            skLineSegment(sketch, "E1054", {"start": v(3131.87, -3290) * mm, "end": v(3131.87, -3690) * mm});
            skLineSegment(sketch, "E1055", {"start": v(3117.87, -3290) * mm, "end": v(3117.87, -3690) * mm});
            skLineSegment(sketch, "E1056", {"start": v(3087.87, -3290) * mm, "end": v(3087.87, -3690) * mm});
            skLineSegment(sketch, "E1057", {"start": v(3073.87, -3290) * mm, "end": v(3073.87, -3690) * mm});
            skLineSegment(sketch, "E1058", {"start": v(3052.87, -3655) * mm, "end": v(3052.87, -3575) * mm});
            skLineSegment(sketch, "E1059", {"start": v(3052.87, -3575) * mm, "end": v(3070.37, -3575) * mm});
            skLineSegment(sketch, "E1060", {"start": v(3152.87, -3575) * mm, "end": v(3152.87, -3655) * mm});
            skLineSegment(sketch, "E1061", {"start": v(3152.87, -3655) * mm, "end": v(3135.37, -3655) * mm});
            skLineSegment(sketch, "E1062", {"start": v(3070.37, -3654) * mm, "end": v(3055.37, -3654) * mm});
            skLineSegment(sketch, "E1063", {"start": v(3055.37, -3654) * mm, "end": v(3055.37, -3576) * mm});
            skLineSegment(sketch, "E1064", {"start": v(3055.37, -3576) * mm, "end": v(3070.37, -3576) * mm});
            skLineSegment(sketch, "E1065", {"start": v(3070.37, -3655) * mm, "end": v(3052.87, -3655) * mm});
            skLineSegment(sketch, "E1066", {"start": v(3135.37, -3575) * mm, "end": v(3152.87, -3575) * mm});
            skLineSegment(sketch, "E1067", {"start": v(3150.37, -3576) * mm, "end": v(3150.37, -3654) * mm});
            skLineSegment(sketch, "E1068", {"start": v(3150.37, -3654) * mm, "end": v(3135.37, -3654) * mm});
            skLineSegment(sketch, "E1069", {"start": v(3135.37, -3576) * mm, "end": v(3150.37, -3576) * mm});
            skLineSegment(sketch, "E1070", {"start": v(-3047.13, -2182) * mm, "end": v(-3047.13, -1982) * mm});
            skLineSegment(sketch, "E1071", {"start": v(-3047.13, -1982) * mm, "end": v(-3029.63, -1982) * mm});
            skLineSegment(sketch, "E1072", {"start": v(-2947.13, -1982) * mm, "end": v(-2947.13, -2182) * mm});
            skLineSegment(sketch, "E1073", {"start": v(-2947.13, -2182) * mm, "end": v(-2964.63, -2182) * mm});
            skLineSegment(sketch, "E1074", {"start": v(-3029.63, -2181) * mm, "end": v(-3044.63, -2181) * mm});
            skLineSegment(sketch, "E1075", {"start": v(-3044.63, -2181) * mm, "end": v(-3044.63, -2103) * mm});
            skLineSegment(sketch, "E1076", {"start": v(-3044.63, -2103) * mm, "end": v(-3029.63, -2103) * mm});
            skLineSegment(sketch, "E1077", {"start": v(-3029.63, -1982) * mm, "end": v(-2964.63, -1982) * mm});
            skLineSegment(sketch, "E1078", {"start": v(-3029.63, -2182) * mm, "end": v(-3047.13, -2182) * mm});
            skLineSegment(sketch, "E1079", {"start": v(-3037.63, -2164.1) * mm, "end": v(-3040.13, -2165.55) * mm});
            skLineSegment(sketch, "E1080", {"start": v(-3040.13, -2165.55) * mm, "end": v(-3040.13, -2168.44) * mm});
            skLineSegment(sketch, "E1081", {"start": v(-3040.13, -2168.44) * mm, "end": v(-3037.63, -2169.88) * mm});
            skLineSegment(sketch, "E1082", {"start": v(-3037.63, -2169.88) * mm, "end": v(-3035.13, -2168.44) * mm});
            skLineSegment(sketch, "E1083", {"start": v(-3035.13, -2168.44) * mm, "end": v(-3035.13, -2165.55) * mm});
            skLineSegment(sketch, "E1084", {"start": v(-3035.13, -2165.55) * mm, "end": v(-3037.63, -2164.1) * mm});
            skLineSegment(sketch, "E1085", {"start": v(-3037.63, -2114.1) * mm, "end": v(-3040.13, -2115.55) * mm});
            skLineSegment(sketch, "E1086", {"start": v(-3040.13, -2115.55) * mm, "end": v(-3040.13, -2118.44) * mm});
            skLineSegment(sketch, "E1087", {"start": v(-3040.13, -2118.44) * mm, "end": v(-3037.63, -2119.88) * mm});
            skLineSegment(sketch, "E1088", {"start": v(-3037.63, -2119.88) * mm, "end": v(-3035.13, -2118.44) * mm});
            skLineSegment(sketch, "E1089", {"start": v(-3035.13, -2118.44) * mm, "end": v(-3035.13, -2115.55) * mm});
            skLineSegment(sketch, "E1090", {"start": v(-3035.13, -2115.55) * mm, "end": v(-3037.63, -2114.1) * mm});
            skLineSegment(sketch, "E1091", {"start": v(-3037.63, -2125) * mm, "end": v(-3037.63, -2109) * mm});
            skLineSegment(sketch, "E1092", {"start": v(-3029.63, -2117) * mm, "end": v(-3045.63, -2117) * mm});
            skLineSegment(sketch, "E1093", {"start": v(-3037.63, -2175) * mm, "end": v(-3037.63, -2159) * mm});
            skLineSegment(sketch, "E1094", {"start": v(-3029.63, -2167) * mm, "end": v(-3045.63, -2167) * mm});
            skLineSegment(sketch, "E1095", {"start": v(-2964.63, -1982) * mm, "end": v(-2947.13, -1982) * mm});
            skLineSegment(sketch, "E1096", {"start": v(-2964.63, -2182) * mm, "end": v(-3029.63, -2182) * mm});
            skLineSegment(sketch, "E1097", {"start": v(-2954.13, -2165.55) * mm, "end": v(-2956.63, -2164.1) * mm});
            skLineSegment(sketch, "E1098", {"start": v(-2954.13, -2168.44) * mm, "end": v(-2954.13, -2165.55) * mm});
            skLineSegment(sketch, "E1099", {"start": v(-2956.63, -2169.88) * mm, "end": v(-2954.13, -2168.44) * mm});
            skLineSegment(sketch, "E1100", {"start": v(-2959.13, -2168.44) * mm, "end": v(-2956.63, -2169.88) * mm});
            skLineSegment(sketch, "E1101", {"start": v(-2959.13, -2165.55) * mm, "end": v(-2959.13, -2168.44) * mm});
            skLineSegment(sketch, "E1102", {"start": v(-2956.63, -2164.1) * mm, "end": v(-2959.13, -2165.55) * mm});
            skLineSegment(sketch, "E1103", {"start": v(-2954.13, -2115.55) * mm, "end": v(-2956.63, -2114.1) * mm});
            skLineSegment(sketch, "E1104", {"start": v(-2954.13, -2118.44) * mm, "end": v(-2954.13, -2115.55) * mm});
            skLineSegment(sketch, "E1105", {"start": v(-2956.63, -2119.88) * mm, "end": v(-2954.13, -2118.44) * mm});
            skLineSegment(sketch, "E1106", {"start": v(-2959.13, -2118.44) * mm, "end": v(-2956.63, -2119.88) * mm});
            skLineSegment(sketch, "E1107", {"start": v(-2959.13, -2115.55) * mm, "end": v(-2959.13, -2118.44) * mm});
            skLineSegment(sketch, "E1108", {"start": v(-2956.63, -2114.1) * mm, "end": v(-2959.13, -2115.55) * mm});
            skLineSegment(sketch, "E1109", {"start": v(-2956.63, -2109) * mm, "end": v(-2956.63, -2125) * mm});
            skLineSegment(sketch, "E1110", {"start": v(-2948.63, -2117) * mm, "end": v(-2964.63, -2117) * mm});
            skLineSegment(sketch, "E1111", {"start": v(-2956.63, -2159) * mm, "end": v(-2956.63, -2175) * mm});
            skLineSegment(sketch, "E1112", {"start": v(-2948.63, -2167) * mm, "end": v(-2964.63, -2167) * mm});
            skLineSegment(sketch, "E1113", {"start": v(-2949.63, -2103) * mm, "end": v(-2949.63, -2181) * mm});
            skLineSegment(sketch, "E1114", {"start": v(-2949.63, -2181) * mm, "end": v(-2964.63, -2181) * mm});
            skLineSegment(sketch, "E1115", {"start": v(-2964.63, -2103) * mm, "end": v(-2949.63, -2103) * mm});
            skLineSegment(sketch, "E1116", {"start": v(-3029.63, -2061) * mm, "end": v(-3044.63, -2061) * mm});
            skLineSegment(sketch, "E1117", {"start": v(-3040.13, -1998.44) * mm, "end": v(-3037.63, -1999.88) * mm});
            skLineSegment(sketch, "E1118", {"start": v(-3040.13, -1995.55) * mm, "end": v(-3040.13, -1998.44) * mm});
            skLineSegment(sketch, "E1119", {"start": v(-3037.63, -1994.1) * mm, "end": v(-3040.13, -1995.55) * mm});
            skLineSegment(sketch, "E1120", {"start": v(-3035.13, -1995.55) * mm, "end": v(-3037.63, -1994.1) * mm});
            skLineSegment(sketch, "E1121", {"start": v(-3035.13, -1998.44) * mm, "end": v(-3035.13, -1995.55) * mm});
            skLineSegment(sketch, "E1122", {"start": v(-3037.63, -1999.88) * mm, "end": v(-3035.13, -1998.44) * mm});
            skLineSegment(sketch, "E1123", {"start": v(-3040.13, -2048.44) * mm, "end": v(-3037.63, -2049.88) * mm});
            skLineSegment(sketch, "E1124", {"start": v(-3040.13, -2045.55) * mm, "end": v(-3040.13, -2048.44) * mm});
            skLineSegment(sketch, "E1125", {"start": v(-3037.63, -2044.1) * mm, "end": v(-3040.13, -2045.55) * mm});
            skLineSegment(sketch, "E1126", {"start": v(-3035.13, -2045.55) * mm, "end": v(-3037.63, -2044.1) * mm});
            skLineSegment(sketch, "E1127", {"start": v(-3035.13, -2048.44) * mm, "end": v(-3035.13, -2045.55) * mm});
            skLineSegment(sketch, "E1128", {"start": v(-3037.63, -2049.88) * mm, "end": v(-3035.13, -2048.44) * mm});
            skLineSegment(sketch, "E1129", {"start": v(-3037.63, -2055) * mm, "end": v(-3037.63, -2039) * mm});
            skLineSegment(sketch, "E1130", {"start": v(-3045.63, -2047) * mm, "end": v(-3029.63, -2047) * mm});
            skLineSegment(sketch, "E1131", {"start": v(-3037.63, -2005) * mm, "end": v(-3037.63, -1989) * mm});
            skLineSegment(sketch, "E1132", {"start": v(-3045.63, -1997) * mm, "end": v(-3029.63, -1997) * mm});
            skLineSegment(sketch, "E1133", {"start": v(-2956.63, -1999.88) * mm, "end": v(-2954.13, -1998.44) * mm});
            skLineSegment(sketch, "E1134", {"start": v(-2954.13, -1998.44) * mm, "end": v(-2954.13, -1995.55) * mm});
            skLineSegment(sketch, "E1135", {"start": v(-2954.13, -1995.55) * mm, "end": v(-2956.63, -1994.1) * mm});
            skLineSegment(sketch, "E1136", {"start": v(-2956.63, -1994.1) * mm, "end": v(-2959.13, -1995.55) * mm});
            skLineSegment(sketch, "E1137", {"start": v(-2959.13, -1995.55) * mm, "end": v(-2959.13, -1998.44) * mm});
            skLineSegment(sketch, "E1138", {"start": v(-2959.13, -1998.44) * mm, "end": v(-2956.63, -1999.88) * mm});
            skLineSegment(sketch, "E1139", {"start": v(-2956.63, -2049.88) * mm, "end": v(-2954.13, -2048.44) * mm});
            skLineSegment(sketch, "E1140", {"start": v(-2954.13, -2048.44) * mm, "end": v(-2954.13, -2045.55) * mm});
            skLineSegment(sketch, "E1141", {"start": v(-2954.13, -2045.55) * mm, "end": v(-2956.63, -2044.1) * mm});
            skLineSegment(sketch, "E1142", {"start": v(-2956.63, -2044.1) * mm, "end": v(-2959.13, -2045.55) * mm});
            skLineSegment(sketch, "E1143", {"start": v(-2959.13, -2045.55) * mm, "end": v(-2959.13, -2048.44) * mm});
            skLineSegment(sketch, "E1144", {"start": v(-2959.13, -2048.44) * mm, "end": v(-2956.63, -2049.88) * mm});
            skLineSegment(sketch, "E1145", {"start": v(-2956.63, -2039) * mm, "end": v(-2956.63, -2055) * mm});
            skLineSegment(sketch, "E1146", {"start": v(-2964.63, -2047) * mm, "end": v(-2948.63, -2047) * mm});
            skLineSegment(sketch, "E1147", {"start": v(-2956.63, -1989) * mm, "end": v(-2956.63, -2005) * mm});
            skLineSegment(sketch, "E1148", {"start": v(-2964.63, -1997) * mm, "end": v(-2948.63, -1997) * mm});
            skLineSegment(sketch, "E1149", {"start": v(-2949.63, -2061) * mm, "end": v(-2964.63, -2061) * mm});
            skLineSegment(sketch, "E1150", {"start": v(-2949.63, -1983) * mm, "end": v(-2949.63, -2061) * mm});
            skLineSegment(sketch, "E1151", {"start": v(-2964.63, -1983) * mm, "end": v(-2949.63, -1983) * mm});
            skLineSegment(sketch, "E1152", {"start": v(-3044.63, -1983) * mm, "end": v(-3029.63, -1983) * mm});
            skLineSegment(sketch, "E1153", {"start": v(-3044.63, -2061) * mm, "end": v(-3044.63, -1983) * mm});
            skLineSegment(sketch, "E1154", {"start": v(-4447.13, -2182) * mm, "end": v(-4447.13, -1982) * mm});
            skLineSegment(sketch, "E1155", {"start": v(-4447.13, -1982) * mm, "end": v(-4429.63, -1982) * mm});
            skLineSegment(sketch, "E1156", {"start": v(-4347.13, -1982) * mm, "end": v(-4347.13, -2182) * mm});
            skLineSegment(sketch, "E1157", {"start": v(-4347.13, -2182) * mm, "end": v(-4364.63, -2182) * mm});
            skLineSegment(sketch, "E1158", {"start": v(-4429.63, -2181) * mm, "end": v(-4444.63, -2181) * mm});
            skLineSegment(sketch, "E1159", {"start": v(-4444.63, -2181) * mm, "end": v(-4444.63, -2103) * mm});
            skLineSegment(sketch, "E1160", {"start": v(-4444.63, -2103) * mm, "end": v(-4429.63, -2103) * mm});
            skLineSegment(sketch, "E1161", {"start": v(-4429.63, -2182) * mm, "end": v(-4447.13, -2182) * mm});
            skLineSegment(sketch, "E1162", {"start": v(-4364.63, -1982) * mm, "end": v(-4347.13, -1982) * mm});
            skLineSegment(sketch, "E1163", {"start": v(-4349.63, -2103) * mm, "end": v(-4349.63, -2181) * mm});
            skLineSegment(sketch, "E1164", {"start": v(-4349.63, -2181) * mm, "end": v(-4364.63, -2181) * mm});
            skLineSegment(sketch, "E1165", {"start": v(-4364.63, -2103) * mm, "end": v(-4349.63, -2103) * mm});
            skLineSegment(sketch, "E1166", {"start": v(-4429.63, -2061) * mm, "end": v(-4444.63, -2061) * mm});
            skLineSegment(sketch, "E1167", {"start": v(-4349.63, -2061) * mm, "end": v(-4364.63, -2061) * mm});
            skLineSegment(sketch, "E1168", {"start": v(-4349.63, -1983) * mm, "end": v(-4349.63, -2061) * mm});
            skLineSegment(sketch, "E1169", {"start": v(-4364.63, -1983) * mm, "end": v(-4349.63, -1983) * mm});
            skLineSegment(sketch, "E1170", {"start": v(-4444.63, -1983) * mm, "end": v(-4429.63, -1983) * mm});
            skLineSegment(sketch, "E1171", {"start": v(-4444.63, -2061) * mm, "end": v(-4444.63, -1983) * mm});
            skLineSegment(sketch, "E1172", {"start": v(-1647.13, -2182) * mm, "end": v(-1647.13, -1982) * mm});
            skLineSegment(sketch, "E1173", {"start": v(-1647.13, -1982) * mm, "end": v(-1629.63, -1982) * mm});
            skLineSegment(sketch, "E1174", {"start": v(-1547.13, -1982) * mm, "end": v(-1547.13, -2182) * mm});
            skLineSegment(sketch, "E1175", {"start": v(-1547.13, -2182) * mm, "end": v(-1564.63, -2182) * mm});
            skLineSegment(sketch, "E1176", {"start": v(-1629.63, -2181) * mm, "end": v(-1644.63, -2181) * mm});
            skLineSegment(sketch, "E1177", {"start": v(-1644.63, -2181) * mm, "end": v(-1644.63, -2103) * mm});
            skLineSegment(sketch, "E1178", {"start": v(-1644.63, -2103) * mm, "end": v(-1629.63, -2103) * mm});
            skLineSegment(sketch, "E1179", {"start": v(-1629.63, -2182) * mm, "end": v(-1647.13, -2182) * mm});
            skLineSegment(sketch, "E1180", {"start": v(-1564.63, -1982) * mm, "end": v(-1547.13, -1982) * mm});
            skLineSegment(sketch, "E1181", {"start": v(-1549.63, -2103) * mm, "end": v(-1549.63, -2181) * mm});
            skLineSegment(sketch, "E1182", {"start": v(-1549.63, -2181) * mm, "end": v(-1564.63, -2181) * mm});
            skLineSegment(sketch, "E1183", {"start": v(-1564.63, -2103) * mm, "end": v(-1549.63, -2103) * mm});
            skLineSegment(sketch, "E1184", {"start": v(-1629.63, -2061) * mm, "end": v(-1644.63, -2061) * mm});
            skLineSegment(sketch, "E1185", {"start": v(-1549.63, -2061) * mm, "end": v(-1564.63, -2061) * mm});
            skLineSegment(sketch, "E1186", {"start": v(-1549.63, -1983) * mm, "end": v(-1549.63, -2061) * mm});
            skLineSegment(sketch, "E1187", {"start": v(-1564.63, -1983) * mm, "end": v(-1549.63, -1983) * mm});
            skLineSegment(sketch, "E1188", {"start": v(-1644.63, -1983) * mm, "end": v(-1629.63, -1983) * mm});
            skLineSegment(sketch, "E1189", {"start": v(-1644.63, -2061) * mm, "end": v(-1644.63, -1983) * mm});
            skLineSegment(sketch, "E1190", {"start": v(552.87, -2182) * mm, "end": v(552.87, -1982) * mm});
            skLineSegment(sketch, "E1191", {"start": v(552.87, -1982) * mm, "end": v(570.37, -1982) * mm});
            skLineSegment(sketch, "E1192", {"start": v(652.87, -1982) * mm, "end": v(652.87, -2182) * mm});
            skLineSegment(sketch, "E1193", {"start": v(652.87, -2182) * mm, "end": v(635.37, -2182) * mm});
            skLineSegment(sketch, "E1194", {"start": v(570.37, -2181) * mm, "end": v(555.37, -2181) * mm});
            skLineSegment(sketch, "E1195", {"start": v(555.37, -2181) * mm, "end": v(555.37, -2103) * mm});
            skLineSegment(sketch, "E1196", {"start": v(555.37, -2103) * mm, "end": v(570.37, -2103) * mm});
            skLineSegment(sketch, "E1197", {"start": v(570.37, -2182) * mm, "end": v(552.87, -2182) * mm});
            skLineSegment(sketch, "E1198", {"start": v(635.37, -1982) * mm, "end": v(652.87, -1982) * mm});
            skLineSegment(sketch, "E1199", {"start": v(650.37, -2103) * mm, "end": v(650.37, -2181) * mm});
            skLineSegment(sketch, "E1200", {"start": v(650.37, -2181) * mm, "end": v(635.37, -2181) * mm});
            skLineSegment(sketch, "E1201", {"start": v(635.37, -2103) * mm, "end": v(650.37, -2103) * mm});
            skLineSegment(sketch, "E1202", {"start": v(570.37, -2061) * mm, "end": v(555.37, -2061) * mm});
            skLineSegment(sketch, "E1203", {"start": v(650.37, -2061) * mm, "end": v(635.37, -2061) * mm});
            skLineSegment(sketch, "E1204", {"start": v(650.37, -1983) * mm, "end": v(650.37, -2061) * mm});
            skLineSegment(sketch, "E1205", {"start": v(635.37, -1983) * mm, "end": v(650.37, -1983) * mm});
            skLineSegment(sketch, "E1206", {"start": v(555.37, -1983) * mm, "end": v(570.37, -1983) * mm});
            skLineSegment(sketch, "E1207", {"start": v(555.37, -2061) * mm, "end": v(555.37, -1983) * mm});
            skLineSegment(sketch, "E1208", {"start": v(3052.87, -2182) * mm, "end": v(3052.87, -1982) * mm});
            skLineSegment(sketch, "E1209", {"start": v(3052.87, -1982) * mm, "end": v(3070.37, -1982) * mm});
            skLineSegment(sketch, "E1210", {"start": v(3152.87, -1982) * mm, "end": v(3152.87, -2182) * mm});
            skLineSegment(sketch, "E1211", {"start": v(3152.87, -2182) * mm, "end": v(3135.37, -2182) * mm});
            skLineSegment(sketch, "E1212", {"start": v(3070.37, -2181) * mm, "end": v(3055.37, -2181) * mm});
            skLineSegment(sketch, "E1213", {"start": v(3055.37, -2181) * mm, "end": v(3055.37, -2103) * mm});
            skLineSegment(sketch, "E1214", {"start": v(3055.37, -2103) * mm, "end": v(3070.37, -2103) * mm});
            skLineSegment(sketch, "E1215", {"start": v(3070.37, -2182) * mm, "end": v(3052.87, -2182) * mm});
            skLineSegment(sketch, "E1216", {"start": v(3135.37, -1982) * mm, "end": v(3152.87, -1982) * mm});
            skLineSegment(sketch, "E1217", {"start": v(3150.37, -2103) * mm, "end": v(3150.37, -2181) * mm});
            skLineSegment(sketch, "E1218", {"start": v(3150.37, -2181) * mm, "end": v(3135.37, -2181) * mm});
            skLineSegment(sketch, "E1219", {"start": v(3135.37, -2103) * mm, "end": v(3150.37, -2103) * mm});
            skLineSegment(sketch, "E1220", {"start": v(3070.37, -2061) * mm, "end": v(3055.37, -2061) * mm});
            skLineSegment(sketch, "E1221", {"start": v(3150.37, -2061) * mm, "end": v(3135.37, -2061) * mm});
            skLineSegment(sketch, "E1222", {"start": v(3150.37, -1983) * mm, "end": v(3150.37, -2061) * mm});
            skLineSegment(sketch, "E1223", {"start": v(3135.37, -1983) * mm, "end": v(3150.37, -1983) * mm});
            skLineSegment(sketch, "E1224", {"start": v(3055.37, -1983) * mm, "end": v(3070.37, -1983) * mm});
            skLineSegment(sketch, "E1225", {"start": v(3055.37, -2061) * mm, "end": v(3055.37, -1983) * mm});
            skLineSegment(sketch, "E1226", {"start": v(3157.87, -2044.5) * mm, "end": v(3157.87, -2119.5) * mm});
            skLineSegment(sketch, "E1227", {"start": v(3157.87, -2119.5) * mm, "end": v(3152.87, -2119.5) * mm});
            skLineSegment(sketch, "E1228", {"start": v(-4452.13, -2119.5) * mm, "end": v(-4452.13, -2044.5) * mm});
            skLineSegment(sketch, "E1229", {"start": v(-4452.13, -2044.5) * mm, "end": v(-4447.13, -2044.5) * mm});
            skLineSegment(sketch, "E1230", {"start": v(-4347.13, -2044.5) * mm, "end": v(-3047.13, -2044.5) * mm});
            skLineSegment(sketch, "E1231", {"start": v(-4447.13, -2119.5) * mm, "end": v(-4452.13, -2119.5) * mm});
            skLineSegment(sketch, "E1232", {"start": v(-2947.13, -2119.5) * mm, "end": v(-3047.13, -2119.5) * mm});
            skLineSegment(sketch, "E1233", {"start": v(-2947.13, -2044.5) * mm, "end": v(-1647.13, -2044.5) * mm});
            skLineSegment(sketch, "E1234", {"start": v(-3047.13, -2044.5) * mm, "end": v(-2947.13, -2044.5) * mm});
            skLineSegment(sketch, "E1235", {"start": v(-3047.13, -2119.5) * mm, "end": v(-4347.13, -2119.5) * mm});
            skLineSegment(sketch, "E1236", {"start": v(-1547.13, -2044.5) * mm, "end": v(552.87, -2044.5) * mm});
            skLineSegment(sketch, "E1237", {"start": v(-1647.13, -2119.5) * mm, "end": v(-2947.13, -2119.5) * mm});
            skLineSegment(sketch, "E1238", {"start": v(652.87, -2044.5) * mm, "end": v(3052.87, -2044.5) * mm});
            skLineSegment(sketch, "E1239", {"start": v(552.87, -2119.5) * mm, "end": v(-1547.13, -2119.5) * mm});
            skLineSegment(sketch, "E1240", {"start": v(3052.87, -2119.5) * mm, "end": v(652.87, -2119.5) * mm});
            skLineSegment(sketch, "E1241", {"start": v(3152.87, -2044.5) * mm, "end": v(3157.87, -2044.5) * mm});
            skLineSegment(sketch, "E1242", {"start": v(-4447.13, -3602.9) * mm, "end": v(-4882.13, -3602.9) * mm});
            skLineSegment(sketch, "E1243", {"start": v(-4882.13, -3667.9) * mm, "end": v(-4435.63, -3667.9) * mm});
            skLineSegment(sketch, "E1244", {"start": v(-3047.13, -3602.9) * mm, "end": v(-4347.13, -3602.9) * mm});
            skLineSegment(sketch, "E1245", {"start": v(-4358.63, -3667.9) * mm, "end": v(-3035.63, -3667.9) * mm});
            skLineSegment(sketch, "E1246", {"start": v(-3482.13, -3602.9) * mm, "end": v(-3482.13, -3595.9) * mm});
            skLineSegment(sketch, "E1247", {"start": v(-3282.13, -3595.9) * mm, "end": v(-3282.13, -3602.9) * mm});
            skLineSegment(sketch, "E1248", {"start": v(-1647.13, -3602.9) * mm, "end": v(-2947.13, -3602.9) * mm});
            skLineSegment(sketch, "E1249", {"start": v(-2958.63, -3667.9) * mm, "end": v(-1635.63, -3667.9) * mm});
            skLineSegment(sketch, "E1250", {"start": v(-1859.13, -3667.9) * mm, "end": v(-1859.13, -3607.9) * mm});
            skLineSegment(sketch, "E1251", {"start": v(-1859.13, -3607.9) * mm, "end": v(-1853.13, -3607.9) * mm});
            skLineSegment(sketch, "E1252", {"start": v(-1853.13, -3607.9) * mm, "end": v(-1853.13, -3667.9) * mm});
            skLineSegment(sketch, "E1253", {"start": v(-1761.13, -3607.9) * mm, "end": v(-1755.13, -3607.9) * mm});
            skLineSegment(sketch, "E1254", {"start": v(-1761.13, -3667.9) * mm, "end": v(-1761.13, -3607.9) * mm});
            skLineSegment(sketch, "E1255", {"start": v(-1755.13, -3607.9) * mm, "end": v(-1755.13, -3667.9) * mm});
            skLineSegment(sketch, "E1256", {"start": v(-2082.13, -3602.9) * mm, "end": v(-2082.13, -3595.9) * mm});
            skLineSegment(sketch, "E1257", {"start": v(-1882.13, -3595.9) * mm, "end": v(-1882.13, -3602.9) * mm});
            skLineSegment(sketch, "E1258", {"start": v(552.87, -3602.9) * mm, "end": v(-1547.13, -3602.9) * mm});
            skLineSegment(sketch, "E1259", {"start": v(-1558.63, -3667.9) * mm, "end": v(564.37, -3667.9) * mm});
            skLineSegment(sketch, "E1260", {"start": v(117.87, -3602.9) * mm, "end": v(117.87, -3595.9) * mm});
            skLineSegment(sketch, "E1261", {"start": v(317.87, -3595.9) * mm, "end": v(317.87, -3602.9) * mm});
            skLineSegment(sketch, "E1262", {"start": v(3052.87, -3602.9) * mm, "end": v(652.87, -3602.9) * mm});
            skLineSegment(sketch, "E1263", {"start": v(641.37, -3667.9) * mm, "end": v(3064.37, -3667.9) * mm});
            skLineSegment(sketch, "E1264", {"start": v(3152.87, -3602.9) * mm, "end": v(3157.87, -3602.9) * mm});
            skLineSegment(sketch, "E1265", {"start": v(3141.37, -3667.9) * mm, "end": v(3157.87, -3667.9) * mm});
            skLineSegment(sketch, "E1266", {"start": v(3157.87, -3602.9) * mm, "end": v(3157.87, -3667.9) * mm});
            skLineSegment(sketch, "E1267", {"start": v(2617.87, -3602.9) * mm, "end": v(2617.87, -3595.9) * mm});
            skLineSegment(sketch, "E1268", {"start": v(2817.87, -3595.9) * mm, "end": v(2817.87, -3602.9) * mm});
            skLineSegment(sketch, "E1269", {"start": v(-4358.63, -3775.5) * mm, "end": v(-4358.63, -3695.5) * mm});
            skLineSegment(sketch, "E1270", {"start": v(-3035.83, -3775.5) * mm, "end": v(-4358.63, -3775.5) * mm});
            skLineSegment(sketch, "E1271", {"start": v(-3035.83, -3695.5) * mm, "end": v(-3035.83, -3775.5) * mm});
            skLineSegment(sketch, "E1272", {"start": v(-4358.63, -3695.5) * mm, "end": v(-3035.83, -3695.5) * mm});
            skLineSegment(sketch, "E1273", {"start": v(-2958.43, -3695.5) * mm, "end": v(-1858.63, -3695.5) * mm});
            skLineSegment(sketch, "E1274", {"start": v(-2958.43, -3775.5) * mm, "end": v(-2958.43, -3695.5) * mm});
            skLineSegment(sketch, "E1275", {"start": v(-1635.63, -3775.5) * mm, "end": v(-1755.63, -3775.5) * mm});
            skLineSegment(sketch, "E1276", {"start": v(-1755.63, -3695.5) * mm, "end": v(-1755.63, -3775.5) * mm});
            skLineSegment(sketch, "E1277", {"start": v(-1858.63, -3775.5) * mm, "end": v(-1858.63, -3695.5) * mm});
            skLineSegment(sketch, "E1278", {"start": v(-1755.63, -3695.5) * mm, "end": v(-1635.63, -3695.5) * mm});
            skLineSegment(sketch, "E1279", {"start": v(-1858.63, -3775.5) * mm, "end": v(-2958.43, -3775.5) * mm});
            skLineSegment(sketch, "E1280", {"start": v(564.37, -3775.5) * mm, "end": v(-1558.63, -3775.5) * mm});
            skLineSegment(sketch, "E1281", {"start": v(-1558.63, -3695.5) * mm, "end": v(564.37, -3695.5) * mm});
            skLineSegment(sketch, "E1282", {"start": v(641.37, -3695.5) * mm, "end": v(3064.37, -3695.5) * mm});
            skLineSegment(sketch, "E1283", {"start": v(3064.37, -3775.5) * mm, "end": v(641.37, -3775.5) * mm});
            skLineSegment(sketch, "E1284", {"start": v(-1763.13, -3789.5) * mm, "end": v(-1758.13, -3784.5) * mm});
            skLineSegment(sketch, "E1285", {"start": v(-1758.13, -3784.5) * mm, "end": v(-1758.13, -3686.5) * mm});
            skLineSegment(sketch, "E1286", {"start": v(-1758.13, -3686.5) * mm, "end": v(-1763.13, -3681.5) * mm});
            skLineSegment(sketch, "E1287", {"start": v(-1856.13, -3784.5) * mm, "end": v(-1851.13, -3789.5) * mm});
            skLineSegment(sketch, "E1288", {"start": v(-1856.13, -3686.5) * mm, "end": v(-1856.13, -3784.5) * mm});
            skLineSegment(sketch, "E1289", {"start": v(-1851.13, -3681.5) * mm, "end": v(-1856.13, -3686.5) * mm});
            skLineSegment(sketch, "E1290", {"start": v(-1864.13, -3735.5) * mm, "end": v(-1750.13, -3735.5) * mm});
            skLineSegment(sketch, "E1291", {"start": v(-1763.13, -3819.5) * mm, "end": v(-1851.13, -3819.5) * mm});
            skLineSegment(sketch, "E1292", {"start": v(-1763.13, -3679.5) * mm, "end": v(-1763.13, -3819.5) * mm});
            skLineSegment(sketch, "E1293", {"start": v(-1851.13, -3819.5) * mm, "end": v(-1851.13, -3679.5) * mm});
            skLineSegment(sketch, "E1294", {"start": v(-1807.13, -3708) * mm, "end": v(-1807.13, -3853) * mm});
            skLineSegment(sketch, "E1295", {"start": v(-1734.63, -3780.5) * mm, "end": v(-1879.63, -3780.5) * mm});
            skLineSegment(sketch, "E1296", {"start": v(-1881.52, -3775.5) * mm, "end": v(-1881.52, -3823.6) * mm});
            skLineSegment(sketch, "E1297", {"start": v(-1861.65, -3823.6) * mm, "end": v(-1915.47, -3823.6) * mm});
            skLineSegment(sketch, "E1298", {"start": v(-1915.47, -3775.5) * mm, "end": v(-1915.47, -3823.6) * mm});
            skLineSegment(sketch, "E1299", {"start": v(-1597.13, -1375.1) * mm, "end": v(-1597.13, -3774) * mm});
            skLineSegment(sketch, "E1300", {"start": v(-1627.93, -1470.6) * mm, "end": v(-1627.93, -1459.1) * mm});
            skLineSegment(sketch, "E1301", {"start": v(-1627.93, -3685.5) * mm, "end": v(-1635.63, -3685.5) * mm});
            skLineSegment(sketch, "E1302", {"start": v(-1627.93, -3690.5) * mm, "end": v(-1633.63, -3690.5) * mm});
            skLineSegment(sketch, "E1303", {"start": v(-1621.63, -3700) * mm, "end": v(-1621.63, -3704.5) * mm});
            skLineSegment(sketch, "E1304", {"start": v(-1627.93, -3676.5) * mm, "end": v(-1635.63, -3676.5) * mm});
            skLineSegment(sketch, "E1305", {"start": v(-1628.13, -3665) * mm, "end": v(-1635.63, -3665) * mm});
            skLineSegment(sketch, "E1306", {"start": v(-1558.63, -3685.5) * mm, "end": v(-1558.63, -3676.5) * mm});
            skLineSegment(sketch, "E1307", {"start": v(-1635.63, -3695.5) * mm, "end": v(-1635.63, -3775.5) * mm});
            skLineSegment(sketch, "E1308", {"start": v(-1564.63, -1470.6) * mm, "end": v(-1564.63, -3665) * mm});
            skLineSegment(sketch, "E1309", {"start": v(-1629.63, -1470.6) * mm, "end": v(-1629.63, -3665) * mm});
            skLineSegment(sketch, "E1310", {"start": v(-1647.63, -3735.5) * mm, "end": v(-1548.67, -3735.5) * mm});
            skLineSegment(sketch, "E1311", {"start": v(-1621.63, -3704.5) * mm, "end": v(-1635.63, -3704.5) * mm});
            skLineSegment(sketch, "E1312", {"start": v(-1633.63, -3690.5) * mm, "end": v(-1634.4, -3690.05) * mm});
            skLineSegment(sketch, "E1313", {"start": v(-1634.4, -3685.94) * mm, "end": v(-1633.63, -3685.5) * mm});
            skLineSegment(sketch, "E1314", {"start": v(-1634.4, -3690.05) * mm, "end": v(-1634.4, -3685.94) * mm});
            skLineSegment(sketch, "E1315", {"start": v(-1572.63, -3704.5) * mm, "end": v(-1572.63, -3700) * mm});
            skLineSegment(sketch, "E1316", {"start": v(-1564.63, -1388.1) * mm, "end": v(-1629.63, -1388.1) * mm});
            skLineSegment(sketch, "E1317", {"start": v(-1566.33, -1459.1) * mm, "end": v(-1566.33, -1470.6) * mm});
            skLineSegment(sketch, "E1318", {"start": v(-1629.63, -1470.6) * mm, "end": v(-1564.63, -1470.6) * mm});
            skLineSegment(sketch, "E1319", {"start": v(-1629.63, -1378.1) * mm, "end": v(-1629.63, -1459.1) * mm});
            skLineSegment(sketch, "E1320", {"start": v(-1564.63, -1378.1) * mm, "end": v(-1629.63, -1378.1) * mm});
            skLineSegment(sketch, "E1321", {"start": v(-1564.63, -1459.1) * mm, "end": v(-1564.63, -1378.1) * mm});
            skLineSegment(sketch, "E1322", {"start": v(-1627.93, -1459.1) * mm, "end": v(-1566.33, -1459.1) * mm});
            skLineSegment(sketch, "E1323", {"start": v(-1559.86, -3690.05) * mm, "end": v(-1560.63, -3690.5) * mm});
            skLineSegment(sketch, "E1324", {"start": v(-1560.63, -3690.5) * mm, "end": v(-1565.93, -3690.5) * mm});
            skLineSegment(sketch, "E1325", {"start": v(-1560.63, -3685.5) * mm, "end": v(-1559.86, -3685.94) * mm});
            skLineSegment(sketch, "E1326", {"start": v(-1559.86, -3685.94) * mm, "end": v(-1559.86, -3690.05) * mm});
            skLineSegment(sketch, "E1327", {"start": v(-1558.63, -3685.5) * mm, "end": v(-1565.93, -3685.5) * mm});
            skLineSegment(sketch, "E1328", {"start": v(-1558.63, -3704.5) * mm, "end": v(-1572.63, -3704.5) * mm});
            skLineSegment(sketch, "E1329", {"start": v(-1562.03, -3676.5) * mm, "end": v(-1562.03, -3665) * mm});
            skLineSegment(sketch, "E1330", {"start": v(-1632.23, -3676.5) * mm, "end": v(-1632.23, -3665) * mm});
            skLineSegment(sketch, "E1331", {"start": v(-1558.63, -3665) * mm, "end": v(-1558.63, -3676.5) * mm});
            skLineSegment(sketch, "E1332", {"start": v(-1558.63, -3665) * mm, "end": v(-1566.13, -3665) * mm});
            skLineSegment(sketch, "E1333", {"start": v(-1635.63, -3676.5) * mm, "end": v(-1635.63, -3685.5) * mm});
            skLineSegment(sketch, "E1334", {"start": v(-1635.63, -3766.5) * mm, "end": v(-1558.63, -3766.5) * mm});
            skLineSegment(sketch, "E1335", {"start": v(-1558.63, -3775.5) * mm, "end": v(-1558.63, -3695.5) * mm});
            skLineSegment(sketch, "E1336", {"start": v(-1558.63, -3676.5) * mm, "end": v(-1565.93, -3676.5) * mm});
            skLineSegment(sketch, "E1337", {"start": v(-1635.63, -3676.5) * mm, "end": v(-1635.63, -3665) * mm});
            skLineSegment(sketch, "E1338", {"start": v(-3035.63, -3676.5) * mm, "end": v(-3035.63, -3665) * mm});
            skLineSegment(sketch, "E1339", {"start": v(-2958.63, -3676.5) * mm, "end": v(-2965.93, -3676.5) * mm});
            skLineSegment(sketch, "E1340", {"start": v(-2958.63, -3766.5) * mm, "end": v(-2958.63, -3704.5) * mm});
            skLineSegment(sketch, "E1341", {"start": v(-3035.63, -3766.5) * mm, "end": v(-2958.63, -3766.5) * mm});
            skLineSegment(sketch, "E1342", {"start": v(-3035.63, -3676.5) * mm, "end": v(-3035.63, -3685.5) * mm});
            skLineSegment(sketch, "E1343", {"start": v(-2958.63, -3665) * mm, "end": v(-2966.13, -3665) * mm});
            skLineSegment(sketch, "E1344", {"start": v(-2958.63, -3665) * mm, "end": v(-2958.63, -3676.5) * mm});
            skLineSegment(sketch, "E1345", {"start": v(-3032.23, -3676.5) * mm, "end": v(-3032.23, -3665) * mm});
            skLineSegment(sketch, "E1346", {"start": v(-2962.03, -3676.5) * mm, "end": v(-2962.03, -3665) * mm});
            skLineSegment(sketch, "E1347", {"start": v(-2958.63, -3704.5) * mm, "end": v(-2972.63, -3704.5) * mm});
            skLineSegment(sketch, "E1348", {"start": v(-2958.63, -3685.5) * mm, "end": v(-2965.93, -3685.5) * mm});
            skLineSegment(sketch, "E1349", {"start": v(-2962.75, -3685.94) * mm, "end": v(-2962.75, -3690.05) * mm});
            skLineSegment(sketch, "E1350", {"start": v(-2959.86, -3685.94) * mm, "end": v(-2959.86, -3690.05) * mm});
            skLineSegment(sketch, "E1351", {"start": v(-2960.63, -3685.5) * mm, "end": v(-2959.86, -3685.94) * mm});
            skLineSegment(sketch, "E1352", {"start": v(-2960.63, -3690.5) * mm, "end": v(-2965.93, -3690.5) * mm});
            skLineSegment(sketch, "E1353", {"start": v(-2959.86, -3690.05) * mm, "end": v(-2960.63, -3690.5) * mm});
            skLineSegment(sketch, "E1354", {"start": v(-3027.93, -1459.1) * mm, "end": v(-2966.33, -1459.1) * mm});
            skLineSegment(sketch, "E1355", {"start": v(-2964.63, -1459.1) * mm, "end": v(-2964.63, -1378.1) * mm});
            skLineSegment(sketch, "E1356", {"start": v(-2964.63, -1378.1) * mm, "end": v(-3029.63, -1378.1) * mm});
            skLineSegment(sketch, "E1357", {"start": v(-3029.63, -1378.1) * mm, "end": v(-3029.63, -1459.1) * mm});
            skLineSegment(sketch, "E1358", {"start": v(-3029.63, -1470.6) * mm, "end": v(-2964.63, -1470.6) * mm});
            skLineSegment(sketch, "E1359", {"start": v(-2966.33, -1459.1) * mm, "end": v(-2966.33, -1470.6) * mm});
            skLineSegment(sketch, "E1360", {"start": v(-2964.63, -1388.1) * mm, "end": v(-3029.63, -1388.1) * mm});
            skLineSegment(sketch, "E1361", {"start": v(-2972.63, -3704.5) * mm, "end": v(-2972.63, -3700) * mm});
            skLineSegment(sketch, "E1362", {"start": v(-3031.52, -3690.05) * mm, "end": v(-3031.52, -3685.94) * mm});
            skLineSegment(sketch, "E1363", {"start": v(-3034.4, -3690.05) * mm, "end": v(-3034.4, -3685.94) * mm});
            skLineSegment(sketch, "E1364", {"start": v(-3034.4, -3685.94) * mm, "end": v(-3033.63, -3685.5) * mm});
            skLineSegment(sketch, "E1365", {"start": v(-3033.63, -3690.5) * mm, "end": v(-3034.4, -3690.05) * mm});
            skLineSegment(sketch, "E1366", {"start": v(-3021.63, -3704.5) * mm, "end": v(-3035.63, -3704.5) * mm});
            skLineSegment(sketch, "E1367", {"start": v(-3047.63, -3735.5) * mm, "end": v(-2948.67, -3735.5) * mm});
            skLineSegment(sketch, "E1368", {"start": v(-3029.63, -1470.6) * mm, "end": v(-3029.63, -3665) * mm});
            skLineSegment(sketch, "E1369", {"start": v(-2964.63, -1470.6) * mm, "end": v(-2964.63, -3665) * mm});
            skLineSegment(sketch, "E1370", {"start": v(-3035.63, -3704.5) * mm, "end": v(-3035.63, -3766.5) * mm});
            skLineSegment(sketch, "E1371", {"start": v(-2958.63, -3685.5) * mm, "end": v(-2958.63, -3676.5) * mm});
            skLineSegment(sketch, "E1372", {"start": v(-3028.13, -3665) * mm, "end": v(-3035.63, -3665) * mm});
            skLineSegment(sketch, "E1373", {"start": v(-3027.93, -3676.5) * mm, "end": v(-3035.63, -3676.5) * mm});
            skLineSegment(sketch, "E1374", {"start": v(-3021.63, -3700) * mm, "end": v(-3021.63, -3704.5) * mm});
            skLineSegment(sketch, "E1375", {"start": v(-3027.93, -3690.5) * mm, "end": v(-3033.63, -3690.5) * mm});
            skLineSegment(sketch, "E1376", {"start": v(-3027.93, -3685.5) * mm, "end": v(-3035.63, -3685.5) * mm});
            skLineSegment(sketch, "E1377", {"start": v(-3027.93, -1470.6) * mm, "end": v(-3027.93, -1459.1) * mm});
            skLineSegment(sketch, "E1378", {"start": v(-2997.13, -1375.1) * mm, "end": v(-2997.13, -3774) * mm});
            skLineSegment(sketch, "E1379", {"start": v(-4397.13, -1375.1) * mm, "end": v(-4397.13, -3774) * mm});
            skLineSegment(sketch, "E1380", {"start": v(-4427.93, -1470.6) * mm, "end": v(-4427.93, -1459.1) * mm});
            skLineSegment(sketch, "E1381", {"start": v(-4427.93, -3685.5) * mm, "end": v(-4435.63, -3685.5) * mm});
            skLineSegment(sketch, "E1382", {"start": v(-4427.93, -3690.5) * mm, "end": v(-4433.63, -3690.5) * mm});
            skLineSegment(sketch, "E1383", {"start": v(-4421.63, -3700) * mm, "end": v(-4421.63, -3704.5) * mm});
            skLineSegment(sketch, "E1384", {"start": v(-4427.93, -3676.5) * mm, "end": v(-4435.63, -3676.5) * mm});
            skLineSegment(sketch, "E1385", {"start": v(-4428.13, -3665) * mm, "end": v(-4435.63, -3665) * mm});
            skLineSegment(sketch, "E1386", {"start": v(-4358.63, -3685.5) * mm, "end": v(-4358.63, -3676.5) * mm});
            skLineSegment(sketch, "E1387", {"start": v(-4435.63, -3704.5) * mm, "end": v(-4435.63, -3766.5) * mm});
            skLineSegment(sketch, "E1388", {"start": v(-4364.63, -1470.6) * mm, "end": v(-4364.63, -3665) * mm});
            skLineSegment(sketch, "E1389", {"start": v(-4429.63, -1470.6) * mm, "end": v(-4429.63, -3665) * mm});
            skLineSegment(sketch, "E1390", {"start": v(-4447.63, -3735.5) * mm, "end": v(-4348.67, -3735.5) * mm});
            skLineSegment(sketch, "E1391", {"start": v(-4435.63, -3743.5) * mm, "end": v(-4466.63, -3743.5) * mm});
            skLineSegment(sketch, "E1392", {"start": v(-4467.13, -3743) * mm, "end": v(-4467.13, -3728) * mm});
            skLineSegment(sketch, "E1393", {"start": v(-4466.63, -3727.5) * mm, "end": v(-4435.63, -3727.5) * mm});
            skLineSegment(sketch, "E1394", {"start": v(-4467.13, -3743) * mm, "end": v(-4466.63, -3743.5) * mm});
            skLineSegment(sketch, "E1395", {"start": v(-4466.63, -3727.5) * mm, "end": v(-4467.13, -3728) * mm});
            skLineSegment(sketch, "E1396", {"start": v(-4421.63, -3704.5) * mm, "end": v(-4435.63, -3704.5) * mm});
            skLineSegment(sketch, "E1397", {"start": v(-4433.63, -3690.5) * mm, "end": v(-4434.4, -3690.05) * mm});
            skLineSegment(sketch, "E1398", {"start": v(-4434.4, -3685.94) * mm, "end": v(-4433.63, -3685.5) * mm});
            skLineSegment(sketch, "E1399", {"start": v(-4434.4, -3690.05) * mm, "end": v(-4434.4, -3685.94) * mm});
            skLineSegment(sketch, "E1400", {"start": v(-4431.52, -3690.05) * mm, "end": v(-4431.52, -3685.94) * mm});
            skLineSegment(sketch, "E1401", {"start": v(-4372.63, -3704.5) * mm, "end": v(-4372.63, -3700) * mm});
            skLineSegment(sketch, "E1402", {"start": v(-4364.63, -1388.1) * mm, "end": v(-4429.63, -1388.1) * mm});
            skLineSegment(sketch, "E1403", {"start": v(-4366.33, -1459.1) * mm, "end": v(-4366.33, -1470.6) * mm});
            skLineSegment(sketch, "E1404", {"start": v(-4429.63, -1470.6) * mm, "end": v(-4364.63, -1470.6) * mm});
            skLineSegment(sketch, "E1405", {"start": v(-4429.63, -1378.1) * mm, "end": v(-4429.63, -1459.1) * mm});
            skLineSegment(sketch, "E1406", {"start": v(-4364.63, -1378.1) * mm, "end": v(-4429.63, -1378.1) * mm});
            skLineSegment(sketch, "E1407", {"start": v(-4364.63, -1459.1) * mm, "end": v(-4364.63, -1378.1) * mm});
            skLineSegment(sketch, "E1408", {"start": v(-4427.93, -1459.1) * mm, "end": v(-4366.33, -1459.1) * mm});
            skLineSegment(sketch, "E1409", {"start": v(-4359.86, -3690.05) * mm, "end": v(-4360.63, -3690.5) * mm});
            skLineSegment(sketch, "E1410", {"start": v(-4360.63, -3690.5) * mm, "end": v(-4365.93, -3690.5) * mm});
            skLineSegment(sketch, "E1411", {"start": v(-4360.63, -3685.5) * mm, "end": v(-4359.86, -3685.94) * mm});
            skLineSegment(sketch, "E1412", {"start": v(-4359.86, -3685.94) * mm, "end": v(-4359.86, -3690.05) * mm});
            skLineSegment(sketch, "E1413", {"start": v(-4362.75, -3685.94) * mm, "end": v(-4362.75, -3690.05) * mm});
            skLineSegment(sketch, "E1414", {"start": v(-4358.63, -3685.5) * mm, "end": v(-4365.93, -3685.5) * mm});
            skLineSegment(sketch, "E1415", {"start": v(-4358.63, -3704.5) * mm, "end": v(-4372.63, -3704.5) * mm});
            skLineSegment(sketch, "E1416", {"start": v(-4362.03, -3676.5) * mm, "end": v(-4362.03, -3665) * mm});
            skLineSegment(sketch, "E1417", {"start": v(-4432.23, -3676.5) * mm, "end": v(-4432.23, -3665) * mm});
            skLineSegment(sketch, "E1418", {"start": v(-4358.63, -3665) * mm, "end": v(-4358.63, -3676.5) * mm});
            skLineSegment(sketch, "E1419", {"start": v(-4358.63, -3665) * mm, "end": v(-4366.13, -3665) * mm});
            skLineSegment(sketch, "E1420", {"start": v(-4435.63, -3676.5) * mm, "end": v(-4435.63, -3685.5) * mm});
            skLineSegment(sketch, "E1421", {"start": v(-4435.63, -3766.5) * mm, "end": v(-4358.63, -3766.5) * mm});
            skLineSegment(sketch, "E1422", {"start": v(-4358.63, -3766.5) * mm, "end": v(-4358.63, -3704.5) * mm});
            skLineSegment(sketch, "E1423", {"start": v(-4358.63, -3676.5) * mm, "end": v(-4365.93, -3676.5) * mm});
            skLineSegment(sketch, "E1424", {"start": v(-4435.63, -3676.5) * mm, "end": v(-4435.63, -3665) * mm});
            skLineSegment(sketch, "E1425", {"start": v(602.87, -1375.1) * mm, "end": v(602.87, -3774) * mm});
            skLineSegment(sketch, "E1426", {"start": v(572.07, -1470.6) * mm, "end": v(572.07, -1459.1) * mm});
            skLineSegment(sketch, "E1427", {"start": v(572.07, -3685.5) * mm, "end": v(564.37, -3685.5) * mm});
            skLineSegment(sketch, "E1428", {"start": v(572.07, -3690.5) * mm, "end": v(566.37, -3690.5) * mm});
            skLineSegment(sketch, "E1429", {"start": v(578.37, -3700) * mm, "end": v(578.37, -3704.5) * mm});
            skLineSegment(sketch, "E1430", {"start": v(572.07, -3676.5) * mm, "end": v(564.37, -3676.5) * mm});
            skLineSegment(sketch, "E1431", {"start": v(571.87, -3665) * mm, "end": v(564.37, -3665) * mm});
            skLineSegment(sketch, "E1432", {"start": v(641.37, -3685.5) * mm, "end": v(641.37, -3676.5) * mm});
            skLineSegment(sketch, "E1433", {"start": v(564.37, -3695.5) * mm, "end": v(564.37, -3775.5) * mm});
            skLineSegment(sketch, "E1434", {"start": v(635.37, -1470.6) * mm, "end": v(635.37, -3665) * mm});
            skLineSegment(sketch, "E1435", {"start": v(570.37, -1470.6) * mm, "end": v(570.37, -3665) * mm});
            skLineSegment(sketch, "E1436", {"start": v(552.37, -3735.5) * mm, "end": v(651.33, -3735.5) * mm});
            skLineSegment(sketch, "E1437", {"start": v(578.37, -3704.5) * mm, "end": v(564.37, -3704.5) * mm});
            skLineSegment(sketch, "E1438", {"start": v(566.37, -3690.5) * mm, "end": v(565.6, -3690.05) * mm});
            skLineSegment(sketch, "E1439", {"start": v(565.6, -3685.94) * mm, "end": v(566.37, -3685.5) * mm});
            skLineSegment(sketch, "E1440", {"start": v(565.6, -3690.05) * mm, "end": v(565.6, -3685.94) * mm});
            skLineSegment(sketch, "E1441", {"start": v(627.37, -3704.5) * mm, "end": v(627.37, -3700) * mm});
            skLineSegment(sketch, "E1442", {"start": v(635.37, -1388.1) * mm, "end": v(570.37, -1388.1) * mm});
            skLineSegment(sketch, "E1443", {"start": v(633.67, -1459.1) * mm, "end": v(633.67, -1470.6) * mm});
            skLineSegment(sketch, "E1444", {"start": v(570.37, -1470.6) * mm, "end": v(635.37, -1470.6) * mm});
            skLineSegment(sketch, "E1445", {"start": v(570.37, -1378.1) * mm, "end": v(570.37, -1459.1) * mm});
            skLineSegment(sketch, "E1446", {"start": v(635.37, -1378.1) * mm, "end": v(570.37, -1378.1) * mm});
            skLineSegment(sketch, "E1447", {"start": v(635.37, -1459.1) * mm, "end": v(635.37, -1378.1) * mm});
            skLineSegment(sketch, "E1448", {"start": v(572.07, -1459.1) * mm, "end": v(633.67, -1459.1) * mm});
            skLineSegment(sketch, "E1449", {"start": v(640.14, -3690.05) * mm, "end": v(639.37, -3690.5) * mm});
            skLineSegment(sketch, "E1450", {"start": v(639.37, -3690.5) * mm, "end": v(634.07, -3690.5) * mm});
            skLineSegment(sketch, "E1451", {"start": v(639.37, -3685.5) * mm, "end": v(640.14, -3685.94) * mm});
            skLineSegment(sketch, "E1452", {"start": v(640.14, -3685.94) * mm, "end": v(640.14, -3690.05) * mm});
            skLineSegment(sketch, "E1453", {"start": v(641.37, -3685.5) * mm, "end": v(634.07, -3685.5) * mm});
            skLineSegment(sketch, "E1454", {"start": v(641.37, -3704.5) * mm, "end": v(627.37, -3704.5) * mm});
            skLineSegment(sketch, "E1455", {"start": v(637.97, -3676.5) * mm, "end": v(637.97, -3665) * mm});
            skLineSegment(sketch, "E1456", {"start": v(567.77, -3676.5) * mm, "end": v(567.77, -3665) * mm});
            skLineSegment(sketch, "E1457", {"start": v(641.37, -3665) * mm, "end": v(641.37, -3676.5) * mm});
            skLineSegment(sketch, "E1458", {"start": v(641.37, -3665) * mm, "end": v(633.87, -3665) * mm});
            skLineSegment(sketch, "E1459", {"start": v(564.37, -3676.5) * mm, "end": v(564.37, -3685.5) * mm});
            skLineSegment(sketch, "E1460", {"start": v(564.37, -3766.5) * mm, "end": v(641.37, -3766.5) * mm});
            skLineSegment(sketch, "E1461", {"start": v(641.37, -3775.5) * mm, "end": v(641.37, -3695.5) * mm});
            skLineSegment(sketch, "E1462", {"start": v(641.37, -3676.5) * mm, "end": v(634.07, -3676.5) * mm});
            skLineSegment(sketch, "E1463", {"start": v(564.37, -3676.5) * mm, "end": v(564.37, -3665) * mm});
            skLineSegment(sketch, "E1464", {"start": v(3102.87, -1375.1) * mm, "end": v(3102.87, -3774) * mm});
            skLineSegment(sketch, "E1465", {"start": v(3072.07, -1470.6) * mm, "end": v(3072.07, -1459.1) * mm});
            skLineSegment(sketch, "E1466", {"start": v(3072.07, -3685.5) * mm, "end": v(3064.37, -3685.5) * mm});
            skLineSegment(sketch, "E1467", {"start": v(3072.07, -3690.5) * mm, "end": v(3066.37, -3690.5) * mm});
            skLineSegment(sketch, "E1468", {"start": v(3078.37, -3700) * mm, "end": v(3078.37, -3704.5) * mm});
            skLineSegment(sketch, "E1469", {"start": v(3072.07, -3676.5) * mm, "end": v(3064.37, -3676.5) * mm});
            skLineSegment(sketch, "E1470", {"start": v(3071.87, -3665) * mm, "end": v(3064.37, -3665) * mm});
            skLineSegment(sketch, "E1471", {"start": v(3141.37, -3685.5) * mm, "end": v(3141.37, -3676.5) * mm});
            skLineSegment(sketch, "E1472", {"start": v(3064.37, -3695.5) * mm, "end": v(3064.37, -3775.5) * mm});
            skLineSegment(sketch, "E1473", {"start": v(3135.37, -1470.6) * mm, "end": v(3135.37, -3665) * mm});
            skLineSegment(sketch, "E1474", {"start": v(3070.37, -1470.6) * mm, "end": v(3070.37, -3665) * mm});
            skLineSegment(sketch, "E1475", {"start": v(3052.37, -3735.5) * mm, "end": v(3151.33, -3735.5) * mm});
            skLineSegment(sketch, "E1476", {"start": v(3078.37, -3704.5) * mm, "end": v(3064.37, -3704.5) * mm});
            skLineSegment(sketch, "E1477", {"start": v(3066.37, -3690.5) * mm, "end": v(3065.6, -3690.05) * mm});
            skLineSegment(sketch, "E1478", {"start": v(3065.6, -3685.94) * mm, "end": v(3066.37, -3685.5) * mm});
            skLineSegment(sketch, "E1479", {"start": v(3065.6, -3690.05) * mm, "end": v(3065.6, -3685.94) * mm});
            skLineSegment(sketch, "E1480", {"start": v(3127.37, -3704.5) * mm, "end": v(3127.37, -3700) * mm});
            skLineSegment(sketch, "E1481", {"start": v(3135.37, -1388.1) * mm, "end": v(3070.37, -1388.1) * mm});
            skLineSegment(sketch, "E1482", {"start": v(3133.67, -1459.1) * mm, "end": v(3133.67, -1470.6) * mm});
            skLineSegment(sketch, "E1483", {"start": v(3070.37, -1470.6) * mm, "end": v(3135.37, -1470.6) * mm});
            skLineSegment(sketch, "E1484", {"start": v(3070.37, -1378.1) * mm, "end": v(3070.37, -1459.1) * mm});
            skLineSegment(sketch, "E1485", {"start": v(3135.37, -1378.1) * mm, "end": v(3070.37, -1378.1) * mm});
            skLineSegment(sketch, "E1486", {"start": v(3135.37, -1459.1) * mm, "end": v(3135.37, -1378.1) * mm});
            skLineSegment(sketch, "E1487", {"start": v(3072.07, -1459.1) * mm, "end": v(3133.67, -1459.1) * mm});
            skLineSegment(sketch, "E1488", {"start": v(3140.14, -3690.05) * mm, "end": v(3139.37, -3690.5) * mm});
            skLineSegment(sketch, "E1489", {"start": v(3139.37, -3690.5) * mm, "end": v(3134.07, -3690.5) * mm});
            skLineSegment(sketch, "E1490", {"start": v(3139.37, -3685.5) * mm, "end": v(3140.14, -3685.94) * mm});
            skLineSegment(sketch, "E1491", {"start": v(3140.14, -3685.94) * mm, "end": v(3140.14, -3690.05) * mm});
            skLineSegment(sketch, "E1492", {"start": v(3141.37, -3685.5) * mm, "end": v(3134.07, -3685.5) * mm});
            skLineSegment(sketch, "E1493", {"start": v(3141.37, -3704.5) * mm, "end": v(3127.37, -3704.5) * mm});
            skLineSegment(sketch, "E1494", {"start": v(3137.97, -3676.5) * mm, "end": v(3137.97, -3665) * mm});
            skLineSegment(sketch, "E1495", {"start": v(3067.77, -3676.5) * mm, "end": v(3067.77, -3665) * mm});
            skLineSegment(sketch, "E1496", {"start": v(3141.37, -3665) * mm, "end": v(3141.37, -3676.5) * mm});
            skLineSegment(sketch, "E1497", {"start": v(3141.37, -3665) * mm, "end": v(3133.87, -3665) * mm});
            skLineSegment(sketch, "E1498", {"start": v(3064.37, -3676.5) * mm, "end": v(3064.37, -3685.5) * mm});
            skLineSegment(sketch, "E1499", {"start": v(3064.37, -3766.5) * mm, "end": v(3141.37, -3766.5) * mm});
            skLineSegment(sketch, "E1500", {"start": v(3141.37, -3766.5) * mm, "end": v(3141.37, -3704.5) * mm});
            skLineSegment(sketch, "E1501", {"start": v(3141.37, -3676.5) * mm, "end": v(3134.07, -3676.5) * mm});
            skLineSegment(sketch, "E1502", {"start": v(3064.37, -3676.5) * mm, "end": v(3064.37, -3665) * mm});
            skLineSegment(sketch, "E1503", {"start": v(3135.37, -2157.5) * mm, "end": v(3182.87, -2157.5) * mm});
            skLineSegment(sketch, "E1504", {"start": v(3022.87, -2042.02) * mm, "end": v(2852.87, -2042.02) * mm});
            skLineSegment(sketch, "E1505", {"start": v(3022.87, -1987.02) * mm, "end": v(2852.87, -1987.02) * mm});
            skLineSegment(sketch, "E1506", {"start": v(-2964.63, -2157.5) * mm, "end": v(-2917.13, -2157.5) * mm});
            skLineSegment(sketch, "E1507", {"start": v(3182.87, -2157.5) * mm, "end": v(3182.87, -1907) * mm});
            skLineSegment(sketch, "E1508", {"start": v(3022.87, -2157.5) * mm, "end": v(3070.37, -2157.5) * mm});
            skLineSegment(sketch, "E1509", {"start": v(3022.87, -1907) * mm, "end": v(3022.87, -2157.5) * mm});
            skLineSegment(sketch, "E1510", {"start": v(-222.13, -1357) * mm, "end": v(377.87, -1357) * mm});
            skLineSegment(sketch, "E1511", {"start": v(-4872.13, -1832) * mm, "end": v(-4872.13, -1432) * mm});
            skLineSegment(sketch, "E1512", {"start": v(-4809.63, -1899.5) * mm, "end": v(-4809.13, -1900) * mm});
            skLineSegment(sketch, "E1513", {"start": v(-4812.13, -1865) * mm, "end": v(-4812.13, -1860) * mm});
            skLineSegment(sketch, "E1514", {"start": v(-4830.63, -1860) * mm, "end": v(-4838.63, -1852) * mm});
            skLineSegment(sketch, "E1515", {"start": v(-4838.63, -1852) * mm, "end": v(-4838.63, -1846.5) * mm});
            skLineSegment(sketch, "E1516", {"start": v(-4841.13, -1844) * mm, "end": v(-4838.63, -1846.5) * mm});
            skLineSegment(sketch, "E1517", {"start": v(-4844.63, -1840) * mm, "end": v(-4841.13, -1843.5) * mm});
            skLineSegment(sketch, "E1518", {"start": v(-4841.13, -1843.5) * mm, "end": v(-4841.13, -1844) * mm});
            skLineSegment(sketch, "E1519", {"start": v(-4852.13, -1840) * mm, "end": v(-4852.13, -1834.67) * mm});
            skLineSegment(sketch, "E1520", {"start": v(-4852.13, -1834.67) * mm, "end": v(-4842.13, -1832) * mm});
            skLineSegment(sketch, "E1521", {"start": v(-4842.13, -1832) * mm, "end": v(-4842.13, -1432) * mm});
            skLineSegment(sketch, "E1522", {"start": v(-4782.13, -1860) * mm, "end": v(-4782.13, -1865) * mm});
            skLineSegment(sketch, "E1523", {"start": v(-4742.13, -1834.67) * mm, "end": v(-4852.13, -1834.67) * mm});
            skLineSegment(sketch, "E1524", {"start": v(-4755.63, -1852) * mm, "end": v(-4838.63, -1852) * mm});
            skLineSegment(sketch, "E1525", {"start": v(-4763.63, -1860) * mm, "end": v(-4830.63, -1860) * mm});
            skLineSegment(sketch, "E1526", {"start": v(-4755.63, -1852) * mm, "end": v(-4763.63, -1860) * mm});
            skLineSegment(sketch, "E1527", {"start": v(-4755.63, -1846.5) * mm, "end": v(-4755.63, -1852) * mm});
            skLineSegment(sketch, "E1528", {"start": v(-4755.63, -1846.5) * mm, "end": v(-4753.13, -1844) * mm});
            skLineSegment(sketch, "E1529", {"start": v(-4753.13, -1843.5) * mm, "end": v(-4749.63, -1840) * mm});
            skLineSegment(sketch, "E1530", {"start": v(-4753.13, -1844) * mm, "end": v(-4753.13, -1843.5) * mm});
            skLineSegment(sketch, "E1531", {"start": v(-4842.13, -1832) * mm, "end": v(-4752.13, -1832) * mm});
            skLineSegment(sketch, "E1532", {"start": v(-4852.13, -1840) * mm, "end": v(-4742.13, -1840) * mm});
            skLineSegment(sketch, "E1533", {"start": v(-4742.13, -1834.67) * mm, "end": v(-4742.13, -1840) * mm});
            skLineSegment(sketch, "E1534", {"start": v(-4752.13, -1832) * mm, "end": v(-4742.13, -1834.67) * mm});
            skLineSegment(sketch, "E1535", {"start": v(-4797.13, -1405.05) * mm, "end": v(-4797.13, -1854) * mm});
            skLineSegment(sketch, "E1536", {"start": v(-4752.13, -1432) * mm, "end": v(-4752.13, -1832) * mm});
            skLineSegment(sketch, "E1537", {"start": v(-4892.13, -1832) * mm, "end": v(-4892.13, -1907) * mm});
            skLineSegment(sketch, "E1538", {"start": v(-4364.63, -1832) * mm, "end": v(-3029.63, -1832) * mm});
            skLineSegment(sketch, "E1539", {"start": v(-4364.63, -1907) * mm, "end": v(-3029.63, -1907) * mm});
            skLineSegment(sketch, "E1540", {"start": v(-4364.63, -1432) * mm, "end": v(-3029.63, -1432) * mm});
            skLineSegment(sketch, "E1541", {"start": v(-2964.63, -1907) * mm, "end": v(-1629.63, -1907) * mm});
            skLineSegment(sketch, "E1542", {"start": v(-2964.63, -1832) * mm, "end": v(-1629.63, -1832) * mm});
            skLineSegment(sketch, "E1543", {"start": v(-2964.63, -1432) * mm, "end": v(-1629.63, -1432) * mm});
            skLineSegment(sketch, "E1544", {"start": v(-1564.63, -1832) * mm, "end": v(570.37, -1832) * mm});
            skLineSegment(sketch, "E1545", {"start": v(-1564.63, -1907) * mm, "end": v(570.37, -1907) * mm});
            skLineSegment(sketch, "E1546", {"start": v(-1564.63, -1432) * mm, "end": v(570.37, -1432) * mm});
            skLineSegment(sketch, "E1547", {"start": v(635.37, -1832) * mm, "end": v(3070.37, -1832) * mm});
            skLineSegment(sketch, "E1548", {"start": v(635.37, -1907) * mm, "end": v(3070.37, -1907) * mm});
            skLineSegment(sketch, "E1549", {"start": v(635.37, -1432) * mm, "end": v(3070.37, -1432) * mm});
            skLineSegment(sketch, "E1550", {"start": v(3135.37, -1907) * mm, "end": v(5047.87, -1907) * mm});
            skLineSegment(sketch, "E1551", {"start": v(3135.37, -1832) * mm, "end": v(5047.87, -1832) * mm});
            skLineSegment(sketch, "E1552", {"start": v(3135.37, -1432) * mm, "end": v(5047.87, -1432) * mm});
            skLineSegment(sketch, "E1553", {"start": v(5047.87, -1364) * mm, "end": v(5047.87, -1432) * mm});
            skLineSegment(sketch, "E1554", {"start": v(-4892.13, -1364) * mm, "end": v(-4892.13, -1432) * mm});
            skLineSegment(sketch, "E1555", {"start": v(-4892.13, -1907) * mm, "end": v(-4429.63, -1907) * mm});
            skLineSegment(sketch, "E1556", {"start": v(-4892.13, -1832) * mm, "end": v(-4841.13, -1832) * mm});
            skLineSegment(sketch, "E1557", {"start": v(-4892.13, -1432) * mm, "end": v(-4429.63, -1432) * mm});
            skLineSegment(sketch, "E1558", {"start": v(-2744.13, -1632) * mm, "end": v(-3250.13, -1632) * mm});
            skLineSegment(sketch, "E1559", {"start": v(-2997.13, -1229) * mm, "end": v(-2997.13, -2055.02) * mm});
            skLineSegment(sketch, "E1560", {"start": v(-3181.26, -1964.52) * mm, "end": v(-3165.38, -1937.02) * mm});
            skLineSegment(sketch, "E1561", {"start": v(-3213, -1964.52) * mm, "end": v(-3181.26, -1964.52) * mm});
            skLineSegment(sketch, "E1562", {"start": v(-3228.89, -1937.02) * mm, "end": v(-3213, -1964.52) * mm});
            skLineSegment(sketch, "E1563", {"start": v(-3217.32, -1917) * mm, "end": v(-3228.89, -1937.02) * mm});
            skLineSegment(sketch, "E1564", {"start": v(-3165.38, -1937.02) * mm, "end": v(-3176.94, -1917) * mm});
            skLineSegment(sketch, "E1565", {"start": v(-2781.26, -1964.52) * mm, "end": v(-2765.38, -1937.02) * mm});
            skLineSegment(sketch, "E1566", {"start": v(-2813, -1964.52) * mm, "end": v(-2781.26, -1964.52) * mm});
            skLineSegment(sketch, "E1567", {"start": v(-2828.89, -1937.02) * mm, "end": v(-2813, -1964.52) * mm});
            skLineSegment(sketch, "E1568", {"start": v(-2817.32, -1917) * mm, "end": v(-2828.89, -1937.02) * mm});
            skLineSegment(sketch, "E1569", {"start": v(-2765.38, -1937.02) * mm, "end": v(-2776.94, -1917) * mm});
            skLineSegment(sketch, "E1570", {"start": v(-3176.93, -1347) * mm, "end": v(-3165.38, -1327) * mm});
            skLineSegment(sketch, "E1571", {"start": v(-3228.89, -1327) * mm, "end": v(-3217.34, -1347) * mm});
            skLineSegment(sketch, "E1572", {"start": v(-3213, -1299.5) * mm, "end": v(-3228.89, -1327) * mm});
            skLineSegment(sketch, "E1573", {"start": v(-3165.38, -1327) * mm, "end": v(-3181.26, -1299.5) * mm});
            skLineSegment(sketch, "E1574", {"start": v(-2776.93, -1347) * mm, "end": v(-2765.38, -1327) * mm});
            skLineSegment(sketch, "E1575", {"start": v(-2828.89, -1327) * mm, "end": v(-2817.34, -1347) * mm});
            skLineSegment(sketch, "E1576", {"start": v(-2813, -1299.5) * mm, "end": v(-2828.89, -1327) * mm});
            skLineSegment(sketch, "E1577", {"start": v(-2765.38, -1327) * mm, "end": v(-2781.26, -1299.5) * mm});
            skLineSegment(sketch, "E1578", {"start": v(-2790.2, -1339) * mm, "end": v(-2783.28, -1327) * mm});
            skLineSegment(sketch, "E1579", {"start": v(-2804.06, -1339) * mm, "end": v(-2790.2, -1339) * mm});
            skLineSegment(sketch, "E1580", {"start": v(-2810.99, -1327) * mm, "end": v(-2804.06, -1339) * mm});
            skLineSegment(sketch, "E1581", {"start": v(-2804.06, -1315) * mm, "end": v(-2810.99, -1327) * mm});
            skLineSegment(sketch, "E1582", {"start": v(-2783.28, -1327) * mm, "end": v(-2790.2, -1315) * mm});
            skLineSegment(sketch, "E1583", {"start": v(-3190.2, -1339) * mm, "end": v(-3183.28, -1327) * mm});
            skLineSegment(sketch, "E1584", {"start": v(-3204.06, -1339) * mm, "end": v(-3190.2, -1339) * mm});
            skLineSegment(sketch, "E1585", {"start": v(-3210.99, -1327) * mm, "end": v(-3204.06, -1339) * mm});
            skLineSegment(sketch, "E1586", {"start": v(-3204.06, -1315) * mm, "end": v(-3210.99, -1327) * mm});
            skLineSegment(sketch, "E1587", {"start": v(-3183.28, -1327) * mm, "end": v(-3190.2, -1315) * mm});
            skLineSegment(sketch, "E1588", {"start": v(-3190.2, -1949.02) * mm, "end": v(-3183.28, -1937.02) * mm});
            skLineSegment(sketch, "E1589", {"start": v(-3204.06, -1949.02) * mm, "end": v(-3190.2, -1949.02) * mm});
            skLineSegment(sketch, "E1590", {"start": v(-3210.99, -1937.02) * mm, "end": v(-3204.06, -1949.02) * mm});
            skLineSegment(sketch, "E1591", {"start": v(-3204.06, -1925.02) * mm, "end": v(-3210.99, -1937.02) * mm});
            skLineSegment(sketch, "E1592", {"start": v(-3190.2, -1925.02) * mm, "end": v(-3204.06, -1925.02) * mm});
            skLineSegment(sketch, "E1593", {"start": v(-3183.28, -1937.02) * mm, "end": v(-3190.2, -1925.02) * mm});
            skLineSegment(sketch, "E1594", {"start": v(-2790.2, -1949.02) * mm, "end": v(-2783.28, -1937.02) * mm});
            skLineSegment(sketch, "E1595", {"start": v(-2804.06, -1949.02) * mm, "end": v(-2790.2, -1949.02) * mm});
            skLineSegment(sketch, "E1596", {"start": v(-2810.99, -1937.02) * mm, "end": v(-2804.06, -1949.02) * mm});
            skLineSegment(sketch, "E1597", {"start": v(-2804.06, -1925.02) * mm, "end": v(-2810.99, -1937.02) * mm});
            skLineSegment(sketch, "E1598", {"start": v(-2790.2, -1925.02) * mm, "end": v(-2804.06, -1925.02) * mm});
            skLineSegment(sketch, "E1599", {"start": v(-2783.28, -1937.02) * mm, "end": v(-2790.2, -1925.02) * mm});
            skLineSegment(sketch, "E1600", {"start": v(-2790.2, -2024.02) * mm, "end": v(-2783.28, -2012.02) * mm});
            skLineSegment(sketch, "E1601", {"start": v(-2804.06, -2024.02) * mm, "end": v(-2790.2, -2024.02) * mm});
            skLineSegment(sketch, "E1602", {"start": v(-2810.99, -2012.02) * mm, "end": v(-2804.06, -2024.02) * mm});
            skLineSegment(sketch, "E1603", {"start": v(-2804.06, -2000.02) * mm, "end": v(-2810.99, -2012.02) * mm});
            skLineSegment(sketch, "E1604", {"start": v(-2790.2, -2000.02) * mm, "end": v(-2804.06, -2000.02) * mm});
            skLineSegment(sketch, "E1605", {"start": v(-2783.28, -2012.02) * mm, "end": v(-2790.2, -2000.02) * mm});
            skLineSegment(sketch, "E1606", {"start": v(-3190.2, -2024.02) * mm, "end": v(-3183.28, -2012.02) * mm});
            skLineSegment(sketch, "E1607", {"start": v(-3204.06, -2024.02) * mm, "end": v(-3190.2, -2024.02) * mm});
            skLineSegment(sketch, "E1608", {"start": v(-3210.99, -2012.02) * mm, "end": v(-3204.06, -2024.02) * mm});
            skLineSegment(sketch, "E1609", {"start": v(-3204.06, -2000.02) * mm, "end": v(-3210.99, -2012.02) * mm});
            skLineSegment(sketch, "E1610", {"start": v(-3190.2, -2000.02) * mm, "end": v(-3204.06, -2000.02) * mm});
            skLineSegment(sketch, "E1611", {"start": v(-3183.28, -2012.02) * mm, "end": v(-3190.2, -2000.02) * mm});
            skLineSegment(sketch, "E1612", {"start": v(-3190.2, -1264) * mm, "end": v(-3183.28, -1252) * mm});
            skLineSegment(sketch, "E1613", {"start": v(-3204.06, -1264) * mm, "end": v(-3190.2, -1264) * mm});
            skLineSegment(sketch, "E1614", {"start": v(-3210.99, -1252) * mm, "end": v(-3204.06, -1264) * mm});
            skLineSegment(sketch, "E1615", {"start": v(-3204.06, -1240) * mm, "end": v(-3210.99, -1252) * mm});
            skLineSegment(sketch, "E1616", {"start": v(-3190.2, -1240) * mm, "end": v(-3204.06, -1240) * mm});
            skLineSegment(sketch, "E1617", {"start": v(-3183.28, -1252) * mm, "end": v(-3190.2, -1240) * mm});
            skLineSegment(sketch, "E1618", {"start": v(-2790.2, -1264) * mm, "end": v(-2783.28, -1252) * mm});
            skLineSegment(sketch, "E1619", {"start": v(-2804.06, -1264) * mm, "end": v(-2790.2, -1264) * mm});
            skLineSegment(sketch, "E1620", {"start": v(-2810.99, -1252) * mm, "end": v(-2804.06, -1264) * mm});
            skLineSegment(sketch, "E1621", {"start": v(-2804.06, -1240) * mm, "end": v(-2810.99, -1252) * mm});
            skLineSegment(sketch, "E1622", {"start": v(-2790.2, -1240) * mm, "end": v(-2804.06, -1240) * mm});
            skLineSegment(sketch, "E1623", {"start": v(-2783.28, -1252) * mm, "end": v(-2790.2, -1240) * mm});
            skLineSegment(sketch, "E1624", {"start": v(-2747.13, -1277) * mm, "end": v(-3247.13, -1277) * mm});
            skLineSegment(sketch, "E1625", {"start": v(-2747.13, -1987.02) * mm, "end": v(-2917.13, -1987.02) * mm});
            skLineSegment(sketch, "E1626", {"start": v(-3247.13, -1222) * mm, "end": v(-2747.13, -1222) * mm});
            skLineSegment(sketch, "E1627", {"start": v(-3247.13, -2042.02) * mm, "end": v(-3247.13, -1907) * mm});
            skLineSegment(sketch, "E1628", {"start": v(-2747.13, -2042.02) * mm, "end": v(-2917.13, -2042.02) * mm});
            skLineSegment(sketch, "E1629", {"start": v(-2747.13, -1222) * mm, "end": v(-2747.13, -1290) * mm});
            skLineSegment(sketch, "E1630", {"start": v(3102.87, -1229) * mm, "end": v(3102.87, -2055.02) * mm});
            skLineSegment(sketch, "E1631", {"start": v(-3247.13, -1290) * mm, "end": v(-3247.13, -1222) * mm});
            skLineSegment(sketch, "E1632", {"start": v(-2747.13, -1432) * mm, "end": v(-2747.13, -1832) * mm});
            skLineSegment(sketch, "E1633", {"start": v(-2747.13, -1907) * mm, "end": v(-2747.13, -2042.02) * mm});
            skLineSegment(sketch, "E1634", {"start": v(3355.87, -1632) * mm, "end": v(2849.87, -1632) * mm});
            skLineSegment(sketch, "E1635", {"start": v(2918.74, -1964.52) * mm, "end": v(2934.62, -1937.02) * mm});
            skLineSegment(sketch, "E1636", {"start": v(2887, -1964.52) * mm, "end": v(2918.74, -1964.52) * mm});
            skLineSegment(sketch, "E1637", {"start": v(2871.11, -1937.02) * mm, "end": v(2887, -1964.52) * mm});
            skLineSegment(sketch, "E1638", {"start": v(2882.68, -1917) * mm, "end": v(2871.11, -1937.02) * mm});
            skLineSegment(sketch, "E1639", {"start": v(2934.62, -1937.02) * mm, "end": v(2923.06, -1917) * mm});
            skLineSegment(sketch, "E1640", {"start": v(3318.74, -1964.52) * mm, "end": v(3334.62, -1937.02) * mm});
            skLineSegment(sketch, "E1641", {"start": v(3287, -1964.52) * mm, "end": v(3318.74, -1964.52) * mm});
            skLineSegment(sketch, "E1642", {"start": v(3271.11, -1937.02) * mm, "end": v(3287, -1964.52) * mm});
            skLineSegment(sketch, "E1643", {"start": v(3282.68, -1917) * mm, "end": v(3271.11, -1937.02) * mm});
            skLineSegment(sketch, "E1644", {"start": v(3334.62, -1937.02) * mm, "end": v(3323.06, -1917) * mm});
            skLineSegment(sketch, "E1645", {"start": v(2923.07, -1347) * mm, "end": v(2934.62, -1327) * mm});
            skLineSegment(sketch, "E1646", {"start": v(2871.11, -1327) * mm, "end": v(2882.66, -1347) * mm});
            skLineSegment(sketch, "E1647", {"start": v(2887, -1299.5) * mm, "end": v(2871.11, -1327) * mm});
            skLineSegment(sketch, "E1648", {"start": v(2934.62, -1327) * mm, "end": v(2918.74, -1299.5) * mm});
            skLineSegment(sketch, "E1649", {"start": v(3323.07, -1347) * mm, "end": v(3334.62, -1327) * mm});
            skLineSegment(sketch, "E1650", {"start": v(3271.11, -1327) * mm, "end": v(3282.66, -1347) * mm});
            skLineSegment(sketch, "E1651", {"start": v(3287, -1299.5) * mm, "end": v(3271.11, -1327) * mm});
            skLineSegment(sketch, "E1652", {"start": v(3334.62, -1327) * mm, "end": v(3318.74, -1299.5) * mm});
            skLineSegment(sketch, "E1653", {"start": v(3309.8, -1339) * mm, "end": v(3316.72, -1327) * mm});
            skLineSegment(sketch, "E1654", {"start": v(3295.94, -1339) * mm, "end": v(3309.8, -1339) * mm});
            skLineSegment(sketch, "E1655", {"start": v(3289.01, -1327) * mm, "end": v(3295.94, -1339) * mm});
            skLineSegment(sketch, "E1656", {"start": v(3295.94, -1315) * mm, "end": v(3289.01, -1327) * mm});
            skLineSegment(sketch, "E1657", {"start": v(3316.72, -1327) * mm, "end": v(3309.8, -1315) * mm});
            skLineSegment(sketch, "E1658", {"start": v(2909.8, -1339) * mm, "end": v(2916.72, -1327) * mm});
            skLineSegment(sketch, "E1659", {"start": v(2895.94, -1339) * mm, "end": v(2909.8, -1339) * mm});
            skLineSegment(sketch, "E1660", {"start": v(2889.01, -1327) * mm, "end": v(2895.94, -1339) * mm});
            skLineSegment(sketch, "E1661", {"start": v(2895.94, -1315) * mm, "end": v(2889.01, -1327) * mm});
            skLineSegment(sketch, "E1662", {"start": v(2916.72, -1327) * mm, "end": v(2909.8, -1315) * mm});
            skLineSegment(sketch, "E1663", {"start": v(2909.8, -1949.02) * mm, "end": v(2916.72, -1937.02) * mm});
            skLineSegment(sketch, "E1664", {"start": v(2895.94, -1949.02) * mm, "end": v(2909.8, -1949.02) * mm});
            skLineSegment(sketch, "E1665", {"start": v(2889.01, -1937.02) * mm, "end": v(2895.94, -1949.02) * mm});
            skLineSegment(sketch, "E1666", {"start": v(2895.94, -1925.02) * mm, "end": v(2889.01, -1937.02) * mm});
            skLineSegment(sketch, "E1667", {"start": v(2909.8, -1925.02) * mm, "end": v(2895.94, -1925.02) * mm});
            skLineSegment(sketch, "E1668", {"start": v(2916.72, -1937.02) * mm, "end": v(2909.8, -1925.02) * mm});
            skLineSegment(sketch, "E1669", {"start": v(3309.8, -1949.02) * mm, "end": v(3316.72, -1937.02) * mm});
            skLineSegment(sketch, "E1670", {"start": v(3295.94, -1949.02) * mm, "end": v(3309.8, -1949.02) * mm});
            skLineSegment(sketch, "E1671", {"start": v(3289.01, -1937.02) * mm, "end": v(3295.94, -1949.02) * mm});
            skLineSegment(sketch, "E1672", {"start": v(3295.94, -1925.02) * mm, "end": v(3289.01, -1937.02) * mm});
            skLineSegment(sketch, "E1673", {"start": v(3309.8, -1925.02) * mm, "end": v(3295.94, -1925.02) * mm});
            skLineSegment(sketch, "E1674", {"start": v(3316.72, -1937.02) * mm, "end": v(3309.8, -1925.02) * mm});
            skLineSegment(sketch, "E1675", {"start": v(3309.8, -2024.02) * mm, "end": v(3316.72, -2012.02) * mm});
            skLineSegment(sketch, "E1676", {"start": v(3295.94, -2024.02) * mm, "end": v(3309.8, -2024.02) * mm});
            skLineSegment(sketch, "E1677", {"start": v(3289.01, -2012.02) * mm, "end": v(3295.94, -2024.02) * mm});
            skLineSegment(sketch, "E1678", {"start": v(3295.94, -2000.02) * mm, "end": v(3289.01, -2012.02) * mm});
            skLineSegment(sketch, "E1679", {"start": v(3309.8, -2000.02) * mm, "end": v(3295.94, -2000.02) * mm});
            skLineSegment(sketch, "E1680", {"start": v(3316.72, -2012.02) * mm, "end": v(3309.8, -2000.02) * mm});
            skLineSegment(sketch, "E1681", {"start": v(2909.8, -2024.02) * mm, "end": v(2916.72, -2012.02) * mm});
            skLineSegment(sketch, "E1682", {"start": v(2895.94, -2024.02) * mm, "end": v(2909.8, -2024.02) * mm});
            skLineSegment(sketch, "E1683", {"start": v(2889.01, -2012.02) * mm, "end": v(2895.94, -2024.02) * mm});
            skLineSegment(sketch, "E1684", {"start": v(2895.94, -2000.02) * mm, "end": v(2889.01, -2012.02) * mm});
            skLineSegment(sketch, "E1685", {"start": v(2909.8, -2000.02) * mm, "end": v(2895.94, -2000.02) * mm});
            skLineSegment(sketch, "E1686", {"start": v(2916.72, -2012.02) * mm, "end": v(2909.8, -2000.02) * mm});
            skLineSegment(sketch, "E1687", {"start": v(2909.8, -1264) * mm, "end": v(2916.72, -1252) * mm});
            skLineSegment(sketch, "E1688", {"start": v(2895.94, -1264) * mm, "end": v(2909.8, -1264) * mm});
            skLineSegment(sketch, "E1689", {"start": v(2889.01, -1252) * mm, "end": v(2895.94, -1264) * mm});
            skLineSegment(sketch, "E1690", {"start": v(2895.94, -1240) * mm, "end": v(2889.01, -1252) * mm});
            skLineSegment(sketch, "E1691", {"start": v(2909.8, -1240) * mm, "end": v(2895.94, -1240) * mm});
            skLineSegment(sketch, "E1692", {"start": v(2916.72, -1252) * mm, "end": v(2909.8, -1240) * mm});
            skLineSegment(sketch, "E1693", {"start": v(3309.8, -1264) * mm, "end": v(3316.72, -1252) * mm});
            skLineSegment(sketch, "E1694", {"start": v(3295.94, -1264) * mm, "end": v(3309.8, -1264) * mm});
            skLineSegment(sketch, "E1695", {"start": v(3289.01, -1252) * mm, "end": v(3295.94, -1264) * mm});
            skLineSegment(sketch, "E1696", {"start": v(3295.94, -1240) * mm, "end": v(3289.01, -1252) * mm});
            skLineSegment(sketch, "E1697", {"start": v(3309.8, -1240) * mm, "end": v(3295.94, -1240) * mm});
            skLineSegment(sketch, "E1698", {"start": v(3316.72, -1252) * mm, "end": v(3309.8, -1240) * mm});
            skLineSegment(sketch, "E1699", {"start": v(3352.87, -1277) * mm, "end": v(2852.87, -1277) * mm});
            skLineSegment(sketch, "E1700", {"start": v(3352.87, -1987.02) * mm, "end": v(3182.87, -1987.02) * mm});
            skLineSegment(sketch, "E1701", {"start": v(2852.87, -1222) * mm, "end": v(3352.87, -1222) * mm});
            skLineSegment(sketch, "E1702", {"start": v(2852.87, -2042.02) * mm, "end": v(2852.87, -1907) * mm});
            skLineSegment(sketch, "E1703", {"start": v(3352.87, -2042.02) * mm, "end": v(3182.87, -2042.02) * mm});
            skLineSegment(sketch, "E1704", {"start": v(3352.87, -1222) * mm, "end": v(3352.87, -1290) * mm});
            skLineSegment(sketch, "E1705", {"start": v(2852.87, -1832) * mm, "end": v(2852.87, -1432) * mm});
            skLineSegment(sketch, "E1706", {"start": v(2852.87, -1290) * mm, "end": v(2852.87, -1222) * mm});
            skLineSegment(sketch, "E1707", {"start": v(3352.87, -1432) * mm, "end": v(3352.87, -1832) * mm});
            skLineSegment(sketch, "E1708", {"start": v(3352.87, -1907) * mm, "end": v(3352.87, -2042.02) * mm});
            skLineSegment(sketch, "E1709", {"start": v(-4758.53, -1893.1) * mm, "end": v(-4758.53, -1865.94) * mm});
            skLineSegment(sketch, "E1710", {"start": v(-4722.04, -1879.5) * mm, "end": v(-4872.23, -1879.5) * mm});
            skLineSegment(sketch, "E1711", {"start": v(-4744.63, -1891.3) * mm, "end": v(-4744.63, -1867.6) * mm});
            skLineSegment(sketch, "E1712", {"start": v(-4769.13, -1863.9) * mm, "end": v(-4769.13, -1864.6) * mm});
            skLineSegment(sketch, "E1713", {"start": v(-4730.53, -1860.5) * mm, "end": v(-4765.73, -1860.5) * mm});
            skLineSegment(sketch, "E1714", {"start": v(-4727.13, -1895.1) * mm, "end": v(-4727.13, -1863.9) * mm});
            skLineSegment(sketch, "E1715", {"start": v(-4765.73, -1898.5) * mm, "end": v(-4730.53, -1898.5) * mm});
            skLineSegment(sketch, "E1716", {"start": v(-4797.13, -1906.75) * mm, "end": v(-4797.13, -1854) * mm});
            skLineSegment(sketch, "E1717", {"start": v(-4777.43, -1867.82) * mm, "end": v(-4758.53, -1860.5) * mm});
            skLineSegment(sketch, "E1718", {"start": v(-4811.14, -1869.07) * mm, "end": v(-4783.12, -1869.07) * mm});
            skLineSegment(sketch, "E1719", {"start": v(-4783.12, -1889.92) * mm, "end": v(-4811.14, -1889.92) * mm});
            skLineSegment(sketch, "E1720", {"start": v(-4758.53, -1898.5) * mm, "end": v(-4777.43, -1891.17) * mm});
            skLineSegment(sketch, "E1721", {"start": v(-4769.13, -1894.38) * mm, "end": v(-4769.13, -1895.1) * mm});
            skLineSegment(sketch, "E1722", {"start": v(-4835.73, -1865.94) * mm, "end": v(-4835.73, -1893.1) * mm});
            skLineSegment(sketch, "E1723", {"start": v(-4849.63, -1867.6) * mm, "end": v(-4849.63, -1891.3) * mm});
            skLineSegment(sketch, "E1724", {"start": v(-4825.13, -1864.6) * mm, "end": v(-4825.13, -1863.9) * mm});
            skLineSegment(sketch, "E1725", {"start": v(-4828.53, -1860.5) * mm, "end": v(-4863.73, -1860.5) * mm});
            skLineSegment(sketch, "E1726", {"start": v(-4867.13, -1863.9) * mm, "end": v(-4867.13, -1895.1) * mm});
            skLineSegment(sketch, "E1727", {"start": v(-4863.73, -1898.5) * mm, "end": v(-4828.53, -1898.5) * mm});
            skLineSegment(sketch, "E1728", {"start": v(-4825.13, -1895.1) * mm, "end": v(-4825.13, -1894.38) * mm});
            skLineSegment(sketch, "E1729", {"start": v(-4835.73, -1860.5) * mm, "end": v(-4816.83, -1867.82) * mm});
            skLineSegment(sketch, "E1730", {"start": v(-4816.83, -1891.17) * mm, "end": v(-4835.73, -1898.5) * mm});
            skLineSegment(sketch, "E1731", {"start": v(-4814.08, -1890.24) * mm, "end": v(-4814.08, -1899.2) * mm});
            skLineSegment(sketch, "E1732", {"start": v(-4814.08, -1899.2) * mm, "end": v(-4780.18, -1899.2) * mm});
            skLineSegment(sketch, "E1733", {"start": v(-4780.18, -1899.2) * mm, "end": v(-4780.18, -1890.24) * mm});
            skLineSegment(sketch, "E1734", {"start": v(-4814.08, -1868.75) * mm, "end": v(-4814.08, -1865.2) * mm});
            skLineSegment(sketch, "E1735", {"start": v(-4814.08, -1865.2) * mm, "end": v(-4780.18, -1865.2) * mm});
            skLineSegment(sketch, "E1736", {"start": v(-4780.18, -1865.2) * mm, "end": v(-4780.18, -1868.75) * mm});
            skLineSegment(sketch, "E1737", {"start": v(-4753.13, -1832) * mm, "end": v(-4429.63, -1832) * mm});
            skLineSegment(sketch, "E1738", {"start": v(-4812.13, -1404) * mm, "end": v(-4812.13, -1399) * mm});
            skLineSegment(sketch, "E1739", {"start": v(-4838.63, -1412) * mm, "end": v(-4830.63, -1404) * mm});
            skLineSegment(sketch, "E1740", {"start": v(-4838.63, -1417.5) * mm, "end": v(-4838.63, -1412) * mm});
            skLineSegment(sketch, "E1741", {"start": v(-4838.63, -1417.5) * mm, "end": v(-4841.13, -1420) * mm});
            skLineSegment(sketch, "E1742", {"start": v(-4841.13, -1420.5) * mm, "end": v(-4844.63, -1424) * mm});
            skLineSegment(sketch, "E1743", {"start": v(-4841.13, -1420) * mm, "end": v(-4841.13, -1420.5) * mm});
            skLineSegment(sketch, "E1744", {"start": v(-4852.13, -1429.31) * mm, "end": v(-4852.13, -1424) * mm});
            skLineSegment(sketch, "E1745", {"start": v(-4842.13, -1432) * mm, "end": v(-4852.13, -1429.31) * mm});
            skLineSegment(sketch, "E1746", {"start": v(-4782.13, -1399) * mm, "end": v(-4782.13, -1404) * mm});
            skLineSegment(sketch, "E1747", {"start": v(-4852.13, -1429.31) * mm, "end": v(-4742.13, -1429.31) * mm});
            skLineSegment(sketch, "E1748", {"start": v(-4838.63, -1412) * mm, "end": v(-4755.63, -1412) * mm});
            skLineSegment(sketch, "E1749", {"start": v(-4830.63, -1404) * mm, "end": v(-4763.63, -1404) * mm});
            skLineSegment(sketch, "E1750", {"start": v(-4763.63, -1404) * mm, "end": v(-4755.63, -1412) * mm});
            skLineSegment(sketch, "E1751", {"start": v(-4755.63, -1412) * mm, "end": v(-4755.63, -1417.5) * mm});
            skLineSegment(sketch, "E1752", {"start": v(-4753.13, -1420) * mm, "end": v(-4755.63, -1417.5) * mm});
            skLineSegment(sketch, "E1753", {"start": v(-4749.63, -1424) * mm, "end": v(-4753.13, -1420.5) * mm});
            skLineSegment(sketch, "E1754", {"start": v(-4753.13, -1420.5) * mm, "end": v(-4753.13, -1420) * mm});
            skLineSegment(sketch, "E1755", {"start": v(-4752.13, -1432) * mm, "end": v(-4842.13, -1432) * mm});
            skLineSegment(sketch, "E1756", {"start": v(-4742.13, -1424) * mm, "end": v(-4852.13, -1424) * mm});
            skLineSegment(sketch, "E1757", {"start": v(-4742.13, -1424) * mm, "end": v(-4742.13, -1429.31) * mm});
            skLineSegment(sketch, "E1758", {"start": v(-4742.13, -1429.31) * mm, "end": v(-4752.13, -1432) * mm});
            skLineSegment(sketch, "E1759", {"start": v(-4758.53, -1398.05) * mm, "end": v(-4758.53, -1370.9) * mm});
            skLineSegment(sketch, "E1760", {"start": v(-4872.23, -1384.5) * mm, "end": v(-4722.04, -1384.5) * mm});
            skLineSegment(sketch, "E1761", {"start": v(-4744.63, -1396.39) * mm, "end": v(-4744.63, -1372.68) * mm});
            skLineSegment(sketch, "E1762", {"start": v(-4769.13, -1399.38) * mm, "end": v(-4769.13, -1400.1) * mm});
            skLineSegment(sketch, "E1763", {"start": v(-4765.73, -1403.5) * mm, "end": v(-4730.53, -1403.5) * mm});
            skLineSegment(sketch, "E1764", {"start": v(-4727.13, -1400.1) * mm, "end": v(-4727.13, -1368.9) * mm});
            skLineSegment(sketch, "E1765", {"start": v(-4730.53, -1365.5) * mm, "end": v(-4765.73, -1365.5) * mm});
            skLineSegment(sketch, "E1766", {"start": v(-4783.12, -1394.92) * mm, "end": v(-4811.14, -1394.92) * mm});
            skLineSegment(sketch, "E1767", {"start": v(-4758.53, -1403.5) * mm, "end": v(-4777.43, -1396.17) * mm});
            skLineSegment(sketch, "E1768", {"start": v(-4811.14, -1374.07) * mm, "end": v(-4783.12, -1374.07) * mm});
            skLineSegment(sketch, "E1769", {"start": v(-4777.43, -1372.82) * mm, "end": v(-4758.53, -1365.5) * mm});
            skLineSegment(sketch, "E1770", {"start": v(-4769.13, -1368.9) * mm, "end": v(-4769.13, -1369.6) * mm});
            skLineSegment(sketch, "E1771", {"start": v(-4835.73, -1370.9) * mm, "end": v(-4835.73, -1398.05) * mm});
            skLineSegment(sketch, "E1772", {"start": v(-4849.63, -1372.68) * mm, "end": v(-4849.63, -1396.39) * mm});
            skLineSegment(sketch, "E1773", {"start": v(-4825.13, -1400.1) * mm, "end": v(-4825.13, -1399.38) * mm});
            skLineSegment(sketch, "E1774", {"start": v(-4863.73, -1403.5) * mm, "end": v(-4828.53, -1403.5) * mm});
            skLineSegment(sketch, "E1775", {"start": v(-4867.13, -1368.9) * mm, "end": v(-4867.13, -1400.1) * mm});
            skLineSegment(sketch, "E1776", {"start": v(-4828.53, -1365.5) * mm, "end": v(-4863.73, -1365.5) * mm});
            skLineSegment(sketch, "E1777", {"start": v(-4825.13, -1369.6) * mm, "end": v(-4825.13, -1368.9) * mm});
            skLineSegment(sketch, "E1778", {"start": v(-4816.83, -1396.17) * mm, "end": v(-4835.73, -1403.5) * mm});
            skLineSegment(sketch, "E1779", {"start": v(-4835.73, -1365.5) * mm, "end": v(-4816.83, -1372.82) * mm});
            skLineSegment(sketch, "E1780", {"start": v(-4814.08, -1364.8) * mm, "end": v(-4814.08, -1373.75) * mm});
            skLineSegment(sketch, "E1781", {"start": v(-4780.18, -1373.75) * mm, "end": v(-4780.18, -1364.8) * mm});
            skLineSegment(sketch, "E1782", {"start": v(-4814.08, -1398.8) * mm, "end": v(-4814.08, -1395.24) * mm});
            skLineSegment(sketch, "E1783", {"start": v(-4780.18, -1398.8) * mm, "end": v(-4814.08, -1398.8) * mm});
            skLineSegment(sketch, "E1784", {"start": v(-4780.18, -1395.24) * mm, "end": v(-4780.18, -1398.8) * mm});
            skLineSegment(sketch, "E1785", {"start": v(-4062.13, -1865) * mm, "end": v(-4062.13, -1860) * mm});
            skLineSegment(sketch, "E1786", {"start": v(-4080.63, -1860) * mm, "end": v(-4088.63, -1852) * mm});
            skLineSegment(sketch, "E1787", {"start": v(-4088.63, -1852) * mm, "end": v(-4088.63, -1846.5) * mm});
            skLineSegment(sketch, "E1788", {"start": v(-4091.13, -1844) * mm, "end": v(-4088.63, -1846.5) * mm});
            skLineSegment(sketch, "E1789", {"start": v(-4094.63, -1840) * mm, "end": v(-4091.13, -1843.5) * mm});
            skLineSegment(sketch, "E1790", {"start": v(-4091.13, -1843.5) * mm, "end": v(-4091.13, -1844) * mm});
            skLineSegment(sketch, "E1791", {"start": v(-4102.13, -1840) * mm, "end": v(-4102.13, -1834.67) * mm});
            skLineSegment(sketch, "E1792", {"start": v(-4102.13, -1834.67) * mm, "end": v(-4092.13, -1832) * mm});
            skLineSegment(sketch, "E1793", {"start": v(-4092.13, -1832) * mm, "end": v(-4092.13, -1432) * mm});
            skLineSegment(sketch, "E1794", {"start": v(-4032.13, -1860) * mm, "end": v(-4032.13, -1865) * mm});
            skLineSegment(sketch, "E1795", {"start": v(-3992.13, -1834.67) * mm, "end": v(-4102.13, -1834.67) * mm});
            skLineSegment(sketch, "E1796", {"start": v(-4005.63, -1852) * mm, "end": v(-4088.63, -1852) * mm});
            skLineSegment(sketch, "E1797", {"start": v(-4013.63, -1860) * mm, "end": v(-4080.63, -1860) * mm});
            skLineSegment(sketch, "E1798", {"start": v(-4005.63, -1852) * mm, "end": v(-4013.63, -1860) * mm});
            skLineSegment(sketch, "E1799", {"start": v(-4005.63, -1846.5) * mm, "end": v(-4005.63, -1852) * mm});
            skLineSegment(sketch, "E1800", {"start": v(-4005.63, -1846.5) * mm, "end": v(-4003.13, -1844) * mm});
            skLineSegment(sketch, "E1801", {"start": v(-4003.13, -1843.5) * mm, "end": v(-3999.63, -1840) * mm});
            skLineSegment(sketch, "E1802", {"start": v(-4003.13, -1844) * mm, "end": v(-4003.13, -1843.5) * mm});
            skLineSegment(sketch, "E1803", {"start": v(-4092.13, -1832) * mm, "end": v(-4002.13, -1832) * mm});
            skLineSegment(sketch, "E1804", {"start": v(-4102.13, -1840) * mm, "end": v(-3992.13, -1840) * mm});
            skLineSegment(sketch, "E1805", {"start": v(-3992.13, -1834.67) * mm, "end": v(-3992.13, -1840) * mm});
            skLineSegment(sketch, "E1806", {"start": v(-4002.13, -1832) * mm, "end": v(-3992.13, -1834.67) * mm});
            skLineSegment(sketch, "E1807", {"start": v(-4047.13, -1405.05) * mm, "end": v(-4047.13, -1854) * mm});
            skLineSegment(sketch, "E1808", {"start": v(-4002.13, -1432) * mm, "end": v(-4002.13, -1832) * mm});
            skLineSegment(sketch, "E1809", {"start": v(-4008.53, -1893.1) * mm, "end": v(-4008.53, -1865.94) * mm});
            skLineSegment(sketch, "E1810", {"start": v(-3972.04, -1879.5) * mm, "end": v(-4122.23, -1879.5) * mm});
            skLineSegment(sketch, "E1811", {"start": v(-3994.63, -1891.3) * mm, "end": v(-3994.63, -1867.6) * mm});
            skLineSegment(sketch, "E1812", {"start": v(-4019.13, -1863.9) * mm, "end": v(-4019.13, -1864.6) * mm});
            skLineSegment(sketch, "E1813", {"start": v(-3980.53, -1860.5) * mm, "end": v(-4015.73, -1860.5) * mm});
            skLineSegment(sketch, "E1814", {"start": v(-3977.13, -1895.1) * mm, "end": v(-3977.13, -1863.9) * mm});
            skLineSegment(sketch, "E1815", {"start": v(-4015.73, -1898.5) * mm, "end": v(-3980.53, -1898.5) * mm});
            skLineSegment(sketch, "E1816", {"start": v(-4047.13, -1906.75) * mm, "end": v(-4047.13, -1854) * mm});
            skLineSegment(sketch, "E1817", {"start": v(-4061.14, -1869.07) * mm, "end": v(-4033.12, -1869.07) * mm});
            skLineSegment(sketch, "E1818", {"start": v(-4027.43, -1867.82) * mm, "end": v(-4008.53, -1860.5) * mm});
            skLineSegment(sketch, "E1819", {"start": v(-4033.12, -1889.92) * mm, "end": v(-4061.14, -1889.92) * mm});
            skLineSegment(sketch, "E1820", {"start": v(-4008.53, -1898.5) * mm, "end": v(-4027.43, -1891.17) * mm});
            skLineSegment(sketch, "E1821", {"start": v(-4019.13, -1894.38) * mm, "end": v(-4019.13, -1895.1) * mm});
            skLineSegment(sketch, "E1822", {"start": v(-4085.73, -1865.94) * mm, "end": v(-4085.73, -1893.1) * mm});
            skLineSegment(sketch, "E1823", {"start": v(-4099.63, -1867.6) * mm, "end": v(-4099.63, -1891.3) * mm});
            skLineSegment(sketch, "E1824", {"start": v(-4075.13, -1864.6) * mm, "end": v(-4075.13, -1863.9) * mm});
            skLineSegment(sketch, "E1825", {"start": v(-4078.53, -1860.5) * mm, "end": v(-4113.73, -1860.5) * mm});
            skLineSegment(sketch, "E1826", {"start": v(-4117.13, -1863.9) * mm, "end": v(-4117.13, -1895.1) * mm});
            skLineSegment(sketch, "E1827", {"start": v(-4113.73, -1898.5) * mm, "end": v(-4078.53, -1898.5) * mm});
            skLineSegment(sketch, "E1828", {"start": v(-4075.13, -1895.1) * mm, "end": v(-4075.13, -1894.38) * mm});
            skLineSegment(sketch, "E1829", {"start": v(-4085.73, -1860.5) * mm, "end": v(-4066.83, -1867.82) * mm});
            skLineSegment(sketch, "E1830", {"start": v(-4066.83, -1891.17) * mm, "end": v(-4085.73, -1898.5) * mm});
            skLineSegment(sketch, "E1831", {"start": v(-4064.08, -1890.24) * mm, "end": v(-4064.08, -1899.2) * mm});
            skLineSegment(sketch, "E1832", {"start": v(-4064.08, -1899.2) * mm, "end": v(-4030.18, -1899.2) * mm});
            skLineSegment(sketch, "E1833", {"start": v(-4030.18, -1899.2) * mm, "end": v(-4030.18, -1890.24) * mm});
            skLineSegment(sketch, "E1834", {"start": v(-4064.08, -1868.75) * mm, "end": v(-4064.08, -1865.2) * mm});
            skLineSegment(sketch, "E1835", {"start": v(-4064.08, -1865.2) * mm, "end": v(-4030.18, -1865.2) * mm});
            skLineSegment(sketch, "E1836", {"start": v(-4030.18, -1865.2) * mm, "end": v(-4030.18, -1868.75) * mm});
            skLineSegment(sketch, "E1837", {"start": v(-4062.13, -1404) * mm, "end": v(-4062.13, -1399) * mm});
            skLineSegment(sketch, "E1838", {"start": v(-4088.63, -1412) * mm, "end": v(-4080.63, -1404) * mm});
            skLineSegment(sketch, "E1839", {"start": v(-4088.63, -1417.5) * mm, "end": v(-4088.63, -1412) * mm});
            skLineSegment(sketch, "E1840", {"start": v(-4088.63, -1417.5) * mm, "end": v(-4091.13, -1420) * mm});
            skLineSegment(sketch, "E1841", {"start": v(-4091.13, -1420.5) * mm, "end": v(-4094.63, -1424) * mm});
            skLineSegment(sketch, "E1842", {"start": v(-4091.13, -1420) * mm, "end": v(-4091.13, -1420.5) * mm});
            skLineSegment(sketch, "E1843", {"start": v(-4102.13, -1429.31) * mm, "end": v(-4102.13, -1424) * mm});
            skLineSegment(sketch, "E1844", {"start": v(-4092.13, -1432) * mm, "end": v(-4102.13, -1429.31) * mm});
            skLineSegment(sketch, "E1845", {"start": v(-4032.13, -1399) * mm, "end": v(-4032.13, -1404) * mm});
            skLineSegment(sketch, "E1846", {"start": v(-4102.13, -1429.31) * mm, "end": v(-3992.13, -1429.31) * mm});
            skLineSegment(sketch, "E1847", {"start": v(-4088.63, -1412) * mm, "end": v(-4005.63, -1412) * mm});
            skLineSegment(sketch, "E1848", {"start": v(-4080.63, -1404) * mm, "end": v(-4013.63, -1404) * mm});
            skLineSegment(sketch, "E1849", {"start": v(-4013.63, -1404) * mm, "end": v(-4005.63, -1412) * mm});
            skLineSegment(sketch, "E1850", {"start": v(-4005.63, -1412) * mm, "end": v(-4005.63, -1417.5) * mm});
            skLineSegment(sketch, "E1851", {"start": v(-4003.13, -1420) * mm, "end": v(-4005.63, -1417.5) * mm});
            skLineSegment(sketch, "E1852", {"start": v(-3999.63, -1424) * mm, "end": v(-4003.13, -1420.5) * mm});
            skLineSegment(sketch, "E1853", {"start": v(-4003.13, -1420.5) * mm, "end": v(-4003.13, -1420) * mm});
            skLineSegment(sketch, "E1854", {"start": v(-4002.13, -1432) * mm, "end": v(-4092.13, -1432) * mm});
            skLineSegment(sketch, "E1855", {"start": v(-3992.13, -1424) * mm, "end": v(-4102.13, -1424) * mm});
            skLineSegment(sketch, "E1856", {"start": v(-3992.13, -1424) * mm, "end": v(-3992.13, -1429.31) * mm});
            skLineSegment(sketch, "E1857", {"start": v(-3992.13, -1429.31) * mm, "end": v(-4002.13, -1432) * mm});
            skLineSegment(sketch, "E1858", {"start": v(-4008.53, -1398.05) * mm, "end": v(-4008.53, -1370.9) * mm});
            skLineSegment(sketch, "E1859", {"start": v(-4122.23, -1384.5) * mm, "end": v(-3972.04, -1384.5) * mm});
            skLineSegment(sketch, "E1860", {"start": v(-3994.63, -1396.39) * mm, "end": v(-3994.63, -1372.68) * mm});
            skLineSegment(sketch, "E1861", {"start": v(-4019.13, -1399.38) * mm, "end": v(-4019.13, -1400.1) * mm});
            skLineSegment(sketch, "E1862", {"start": v(-4015.73, -1403.5) * mm, "end": v(-3980.53, -1403.5) * mm});
            skLineSegment(sketch, "E1863", {"start": v(-3977.13, -1400.1) * mm, "end": v(-3977.13, -1368.9) * mm});
            skLineSegment(sketch, "E1864", {"start": v(-3980.53, -1365.5) * mm, "end": v(-4015.73, -1365.5) * mm});
            skLineSegment(sketch, "E1865", {"start": v(-4047.13, -1399.98) * mm, "end": v(-4047.13, -1357.24) * mm});
            skLineSegment(sketch, "E1866", {"start": v(-4008.53, -1403.5) * mm, "end": v(-4027.43, -1396.17) * mm});
            skLineSegment(sketch, "E1867", {"start": v(-4033.12, -1394.92) * mm, "end": v(-4061.14, -1394.92) * mm});
            skLineSegment(sketch, "E1868", {"start": v(-4061.14, -1374.07) * mm, "end": v(-4033.12, -1374.07) * mm});
            skLineSegment(sketch, "E1869", {"start": v(-4027.43, -1372.82) * mm, "end": v(-4008.53, -1365.5) * mm});
            skLineSegment(sketch, "E1870", {"start": v(-4019.13, -1368.9) * mm, "end": v(-4019.13, -1369.6) * mm});
            skLineSegment(sketch, "E1871", {"start": v(-4085.73, -1370.9) * mm, "end": v(-4085.73, -1398.05) * mm});
            skLineSegment(sketch, "E1872", {"start": v(-4099.63, -1372.68) * mm, "end": v(-4099.63, -1396.39) * mm});
            skLineSegment(sketch, "E1873", {"start": v(-4075.13, -1400.1) * mm, "end": v(-4075.13, -1399.38) * mm});
            skLineSegment(sketch, "E1874", {"start": v(-4113.73, -1403.5) * mm, "end": v(-4078.53, -1403.5) * mm});
            skLineSegment(sketch, "E1875", {"start": v(-4117.13, -1368.9) * mm, "end": v(-4117.13, -1400.1) * mm});
            skLineSegment(sketch, "E1876", {"start": v(-4078.53, -1365.5) * mm, "end": v(-4113.73, -1365.5) * mm});
            skLineSegment(sketch, "E1877", {"start": v(-4075.13, -1369.6) * mm, "end": v(-4075.13, -1368.9) * mm});
            skLineSegment(sketch, "E1878", {"start": v(-4066.83, -1396.17) * mm, "end": v(-4085.73, -1403.5) * mm});
            skLineSegment(sketch, "E1879", {"start": v(-4085.73, -1365.5) * mm, "end": v(-4066.83, -1372.82) * mm});
            skLineSegment(sketch, "E1880", {"start": v(-4064.08, -1364.8) * mm, "end": v(-4064.08, -1373.75) * mm});
            skLineSegment(sketch, "E1881", {"start": v(-4030.18, -1364.8) * mm, "end": v(-4064.08, -1364.8) * mm});
            skLineSegment(sketch, "E1882", {"start": v(-4030.18, -1373.75) * mm, "end": v(-4030.18, -1364.8) * mm});
            skLineSegment(sketch, "E1883", {"start": v(-4064.08, -1398.8) * mm, "end": v(-4064.08, -1395.24) * mm});
            skLineSegment(sketch, "E1884", {"start": v(-4030.18, -1398.8) * mm, "end": v(-4064.08, -1398.8) * mm});
            skLineSegment(sketch, "E1885", {"start": v(-4030.18, -1395.24) * mm, "end": v(-4030.18, -1398.8) * mm});
            skLineSegment(sketch, "E1886", {"start": v(-3312.13, -1865) * mm, "end": v(-3312.13, -1860) * mm});
            skLineSegment(sketch, "E1887", {"start": v(-3330.63, -1860) * mm, "end": v(-3338.63, -1852) * mm});
            skLineSegment(sketch, "E1888", {"start": v(-3338.63, -1852) * mm, "end": v(-3338.63, -1846.5) * mm});
            skLineSegment(sketch, "E1889", {"start": v(-3341.13, -1844) * mm, "end": v(-3338.63, -1846.5) * mm});
            skLineSegment(sketch, "E1890", {"start": v(-3344.63, -1840) * mm, "end": v(-3341.13, -1843.5) * mm});
            skLineSegment(sketch, "E1891", {"start": v(-3341.13, -1843.5) * mm, "end": v(-3341.13, -1844) * mm});
            skLineSegment(sketch, "E1892", {"start": v(-3352.13, -1840) * mm, "end": v(-3352.13, -1834.67) * mm});
            skLineSegment(sketch, "E1893", {"start": v(-3352.13, -1834.67) * mm, "end": v(-3342.13, -1832) * mm});
            skLineSegment(sketch, "E1894", {"start": v(-3342.13, -1832) * mm, "end": v(-3342.13, -1432) * mm});
            skLineSegment(sketch, "E1895", {"start": v(-3282.13, -1860) * mm, "end": v(-3282.13, -1865) * mm});
            skLineSegment(sketch, "E1896", {"start": v(-3242.13, -1834.67) * mm, "end": v(-3352.13, -1834.67) * mm});
            skLineSegment(sketch, "E1897", {"start": v(-3255.63, -1852) * mm, "end": v(-3338.63, -1852) * mm});
            skLineSegment(sketch, "E1898", {"start": v(-3263.63, -1860) * mm, "end": v(-3330.63, -1860) * mm});
            skLineSegment(sketch, "E1899", {"start": v(-3255.63, -1852) * mm, "end": v(-3263.63, -1860) * mm});
            skLineSegment(sketch, "E1900", {"start": v(-3255.63, -1846.5) * mm, "end": v(-3255.63, -1852) * mm});
            skLineSegment(sketch, "E1901", {"start": v(-3255.63, -1846.5) * mm, "end": v(-3253.13, -1844) * mm});
            skLineSegment(sketch, "E1902", {"start": v(-3253.13, -1843.5) * mm, "end": v(-3249.63, -1840) * mm});
            skLineSegment(sketch, "E1903", {"start": v(-3253.13, -1844) * mm, "end": v(-3253.13, -1843.5) * mm});
            skLineSegment(sketch, "E1904", {"start": v(-3342.13, -1832) * mm, "end": v(-3252.13, -1832) * mm});
            skLineSegment(sketch, "E1905", {"start": v(-3352.13, -1840) * mm, "end": v(-3242.13, -1840) * mm});
            skLineSegment(sketch, "E1906", {"start": v(-3242.13, -1834.67) * mm, "end": v(-3242.13, -1840) * mm});
            skLineSegment(sketch, "E1907", {"start": v(-3252.13, -1832) * mm, "end": v(-3242.13, -1834.67) * mm});
            skLineSegment(sketch, "E1908", {"start": v(-3297.13, -1405.05) * mm, "end": v(-3297.13, -1864) * mm});
            skLineSegment(sketch, "E1909", {"start": v(-3252.13, -1432) * mm, "end": v(-3252.13, -1832) * mm});
            skLineSegment(sketch, "E1910", {"start": v(-3258.53, -1893.1) * mm, "end": v(-3258.53, -1865.94) * mm});
            skLineSegment(sketch, "E1911", {"start": v(-3222.04, -1879.5) * mm, "end": v(-3372.23, -1879.5) * mm});
            skLineSegment(sketch, "E1912", {"start": v(-3244.63, -1891.3) * mm, "end": v(-3244.63, -1867.6) * mm});
            skLineSegment(sketch, "E1913", {"start": v(-3269.13, -1863.9) * mm, "end": v(-3269.13, -1864.6) * mm});
            skLineSegment(sketch, "E1914", {"start": v(-3230.53, -1860.5) * mm, "end": v(-3265.73, -1860.5) * mm});
            skLineSegment(sketch, "E1915", {"start": v(-3227.13, -1895.1) * mm, "end": v(-3227.13, -1863.9) * mm});
            skLineSegment(sketch, "E1916", {"start": v(-3265.73, -1898.5) * mm, "end": v(-3230.53, -1898.5) * mm});
            skLineSegment(sketch, "E1917", {"start": v(-3297.13, -1916.75) * mm, "end": v(-3297.13, -1864) * mm});
            skLineSegment(sketch, "E1918", {"start": v(-3277.43, -1867.82) * mm, "end": v(-3258.53, -1860.5) * mm});
            skLineSegment(sketch, "E1919", {"start": v(-3311.14, -1869.07) * mm, "end": v(-3283.12, -1869.07) * mm});
            skLineSegment(sketch, "E1920", {"start": v(-3283.12, -1889.92) * mm, "end": v(-3311.14, -1889.92) * mm});
            skLineSegment(sketch, "E1921", {"start": v(-3258.53, -1898.5) * mm, "end": v(-3277.43, -1891.17) * mm});
            skLineSegment(sketch, "E1922", {"start": v(-3269.13, -1894.38) * mm, "end": v(-3269.13, -1895.1) * mm});
            skLineSegment(sketch, "E1923", {"start": v(-3335.73, -1865.94) * mm, "end": v(-3335.73, -1893.1) * mm});
            skLineSegment(sketch, "E1924", {"start": v(-3349.63, -1867.6) * mm, "end": v(-3349.63, -1891.3) * mm});
            skLineSegment(sketch, "E1925", {"start": v(-3325.13, -1864.6) * mm, "end": v(-3325.13, -1863.9) * mm});
            skLineSegment(sketch, "E1926", {"start": v(-3328.53, -1860.5) * mm, "end": v(-3363.73, -1860.5) * mm});
            skLineSegment(sketch, "E1927", {"start": v(-3367.13, -1863.9) * mm, "end": v(-3367.13, -1895.1) * mm});
            skLineSegment(sketch, "E1928", {"start": v(-3363.73, -1898.5) * mm, "end": v(-3328.53, -1898.5) * mm});
            skLineSegment(sketch, "E1929", {"start": v(-3325.13, -1895.1) * mm, "end": v(-3325.13, -1894.38) * mm});
            skLineSegment(sketch, "E1930", {"start": v(-3335.73, -1860.5) * mm, "end": v(-3316.83, -1867.82) * mm});
            skLineSegment(sketch, "E1931", {"start": v(-3316.83, -1891.17) * mm, "end": v(-3335.73, -1898.5) * mm});
            skLineSegment(sketch, "E1932", {"start": v(-3314.08, -1890.24) * mm, "end": v(-3314.08, -1899.2) * mm});
            skLineSegment(sketch, "E1933", {"start": v(-3314.08, -1899.2) * mm, "end": v(-3280.18, -1899.2) * mm});
            skLineSegment(sketch, "E1934", {"start": v(-3280.18, -1899.2) * mm, "end": v(-3280.18, -1890.24) * mm});
            skLineSegment(sketch, "E1935", {"start": v(-3314.08, -1868.75) * mm, "end": v(-3314.08, -1865.2) * mm});
            skLineSegment(sketch, "E1936", {"start": v(-3314.08, -1865.2) * mm, "end": v(-3280.18, -1865.2) * mm});
            skLineSegment(sketch, "E1937", {"start": v(-3280.18, -1865.2) * mm, "end": v(-3280.18, -1868.75) * mm});
            skLineSegment(sketch, "E1938", {"start": v(-3312.13, -1404) * mm, "end": v(-3312.13, -1399) * mm});
            skLineSegment(sketch, "E1939", {"start": v(-3338.63, -1412) * mm, "end": v(-3330.63, -1404) * mm});
            skLineSegment(sketch, "E1940", {"start": v(-3338.63, -1417.5) * mm, "end": v(-3338.63, -1412) * mm});
            skLineSegment(sketch, "E1941", {"start": v(-3338.63, -1417.5) * mm, "end": v(-3341.13, -1420) * mm});
            skLineSegment(sketch, "E1942", {"start": v(-3341.13, -1420.5) * mm, "end": v(-3344.63, -1424) * mm});
            skLineSegment(sketch, "E1943", {"start": v(-3341.13, -1420) * mm, "end": v(-3341.13, -1420.5) * mm});
            skLineSegment(sketch, "E1944", {"start": v(-3352.13, -1429.31) * mm, "end": v(-3352.13, -1424) * mm});
            skLineSegment(sketch, "E1945", {"start": v(-3342.13, -1432) * mm, "end": v(-3352.13, -1429.31) * mm});
            skLineSegment(sketch, "E1946", {"start": v(-3282.13, -1399) * mm, "end": v(-3282.13, -1404) * mm});
            skLineSegment(sketch, "E1947", {"start": v(-3352.13, -1429.31) * mm, "end": v(-3242.13, -1429.31) * mm});
            skLineSegment(sketch, "E1948", {"start": v(-3338.63, -1412) * mm, "end": v(-3255.63, -1412) * mm});
            skLineSegment(sketch, "E1949", {"start": v(-3330.63, -1404) * mm, "end": v(-3263.63, -1404) * mm});
            skLineSegment(sketch, "E1950", {"start": v(-3263.63, -1404) * mm, "end": v(-3255.63, -1412) * mm});
            skLineSegment(sketch, "E1951", {"start": v(-3255.63, -1412) * mm, "end": v(-3255.63, -1417.5) * mm});
            skLineSegment(sketch, "E1952", {"start": v(-3253.13, -1420) * mm, "end": v(-3255.63, -1417.5) * mm});
            skLineSegment(sketch, "E1953", {"start": v(-3249.63, -1424) * mm, "end": v(-3253.13, -1420.5) * mm});
            skLineSegment(sketch, "E1954", {"start": v(-3253.13, -1420.5) * mm, "end": v(-3253.13, -1420) * mm});
            skLineSegment(sketch, "E1955", {"start": v(-3252.13, -1432) * mm, "end": v(-3342.13, -1432) * mm});
            skLineSegment(sketch, "E1956", {"start": v(-3242.13, -1424) * mm, "end": v(-3352.13, -1424) * mm});
            skLineSegment(sketch, "E1957", {"start": v(-3242.13, -1424) * mm, "end": v(-3242.13, -1429.31) * mm});
            skLineSegment(sketch, "E1958", {"start": v(-3242.13, -1429.31) * mm, "end": v(-3252.13, -1432) * mm});
            skLineSegment(sketch, "E1959", {"start": v(-3258.53, -1398.05) * mm, "end": v(-3258.53, -1370.9) * mm});
            skLineSegment(sketch, "E1960", {"start": v(-3372.23, -1384.5) * mm, "end": v(-3222.04, -1384.5) * mm});
            skLineSegment(sketch, "E1961", {"start": v(-3244.63, -1396.39) * mm, "end": v(-3244.63, -1372.68) * mm});
            skLineSegment(sketch, "E1962", {"start": v(-3269.13, -1399.38) * mm, "end": v(-3269.13, -1400.1) * mm});
            skLineSegment(sketch, "E1963", {"start": v(-3265.73, -1403.5) * mm, "end": v(-3230.53, -1403.5) * mm});
            skLineSegment(sketch, "E1964", {"start": v(-3227.13, -1400.1) * mm, "end": v(-3227.13, -1368.9) * mm});
            skLineSegment(sketch, "E1965", {"start": v(-3230.53, -1365.5) * mm, "end": v(-3265.73, -1365.5) * mm});
            skLineSegment(sketch, "E1966", {"start": v(-3283.12, -1394.92) * mm, "end": v(-3311.14, -1394.92) * mm});
            skLineSegment(sketch, "E1967", {"start": v(-3258.53, -1403.5) * mm, "end": v(-3277.43, -1396.17) * mm});
            skLineSegment(sketch, "E1968", {"start": v(-3311.14, -1374.07) * mm, "end": v(-3283.12, -1374.07) * mm});
            skLineSegment(sketch, "E1969", {"start": v(-3277.43, -1372.82) * mm, "end": v(-3258.53, -1365.5) * mm});
            skLineSegment(sketch, "E1970", {"start": v(-3269.13, -1368.9) * mm, "end": v(-3269.13, -1369.6) * mm});
            skLineSegment(sketch, "E1971", {"start": v(-3335.73, -1370.9) * mm, "end": v(-3335.73, -1398.05) * mm});
            skLineSegment(sketch, "E1972", {"start": v(-3349.63, -1372.68) * mm, "end": v(-3349.63, -1396.39) * mm});
            skLineSegment(sketch, "E1973", {"start": v(-3325.13, -1400.1) * mm, "end": v(-3325.13, -1399.38) * mm});
            skLineSegment(sketch, "E1974", {"start": v(-3363.73, -1403.5) * mm, "end": v(-3328.53, -1403.5) * mm});
            skLineSegment(sketch, "E1975", {"start": v(-3367.13, -1368.9) * mm, "end": v(-3367.13, -1400.1) * mm});
            skLineSegment(sketch, "E1976", {"start": v(-3328.53, -1365.5) * mm, "end": v(-3363.73, -1365.5) * mm});
            skLineSegment(sketch, "E1977", {"start": v(-3325.13, -1369.6) * mm, "end": v(-3325.13, -1368.9) * mm});
            skLineSegment(sketch, "E1978", {"start": v(-3316.83, -1396.17) * mm, "end": v(-3335.73, -1403.5) * mm});
            skLineSegment(sketch, "E1979", {"start": v(-3335.73, -1365.5) * mm, "end": v(-3316.83, -1372.82) * mm});
            skLineSegment(sketch, "E1980", {"start": v(-3314.08, -1364.8) * mm, "end": v(-3314.08, -1373.75) * mm});
            skLineSegment(sketch, "E1981", {"start": v(-3280.18, -1364.8) * mm, "end": v(-3314.08, -1364.8) * mm});
            skLineSegment(sketch, "E1982", {"start": v(-3280.18, -1373.75) * mm, "end": v(-3280.18, -1364.8) * mm});
            skLineSegment(sketch, "E1983", {"start": v(-3314.08, -1398.8) * mm, "end": v(-3314.08, -1395.24) * mm});
            skLineSegment(sketch, "E1984", {"start": v(-3280.18, -1398.8) * mm, "end": v(-3314.08, -1398.8) * mm});
            skLineSegment(sketch, "E1985", {"start": v(-3280.18, -1395.24) * mm, "end": v(-3280.18, -1398.8) * mm});
            skLineSegment(sketch, "E1986", {"start": v(-2562.13, -1865) * mm, "end": v(-2562.13, -1860) * mm});
            skLineSegment(sketch, "E1987", {"start": v(-2580.63, -1860) * mm, "end": v(-2588.63, -1852) * mm});
            skLineSegment(sketch, "E1988", {"start": v(-2588.63, -1852) * mm, "end": v(-2588.63, -1846.5) * mm});
            skLineSegment(sketch, "E1989", {"start": v(-2591.13, -1844) * mm, "end": v(-2588.63, -1846.5) * mm});
            skLineSegment(sketch, "E1990", {"start": v(-2594.63, -1840) * mm, "end": v(-2591.13, -1843.5) * mm});
            skLineSegment(sketch, "E1991", {"start": v(-2591.13, -1843.5) * mm, "end": v(-2591.13, -1844) * mm});
            skLineSegment(sketch, "E1992", {"start": v(-2602.13, -1840) * mm, "end": v(-2602.13, -1834.67) * mm});
            skLineSegment(sketch, "E1993", {"start": v(-2602.13, -1834.67) * mm, "end": v(-2592.13, -1832) * mm});
            skLineSegment(sketch, "E1994", {"start": v(-2592.13, -1832) * mm, "end": v(-2592.13, -1432) * mm});
            skLineSegment(sketch, "E1995", {"start": v(-2532.13, -1860) * mm, "end": v(-2532.13, -1865) * mm});
            skLineSegment(sketch, "E1996", {"start": v(-2492.13, -1834.67) * mm, "end": v(-2602.13, -1834.67) * mm});
            skLineSegment(sketch, "E1997", {"start": v(-2505.63, -1852) * mm, "end": v(-2588.63, -1852) * mm});
            skLineSegment(sketch, "E1998", {"start": v(-2513.63, -1860) * mm, "end": v(-2580.63, -1860) * mm});
            skLineSegment(sketch, "E1999", {"start": v(-2505.63, -1852) * mm, "end": v(-2513.63, -1860) * mm});
            skLineSegment(sketch, "E2000", {"start": v(-2505.63, -1846.5) * mm, "end": v(-2505.63, -1852) * mm});
            skLineSegment(sketch, "E2001", {"start": v(-2505.63, -1846.5) * mm, "end": v(-2503.13, -1844) * mm});
            skLineSegment(sketch, "E2002", {"start": v(-2503.13, -1843.5) * mm, "end": v(-2499.63, -1840) * mm});
            skLineSegment(sketch, "E2003", {"start": v(-2503.13, -1844) * mm, "end": v(-2503.13, -1843.5) * mm});
            skLineSegment(sketch, "E2004", {"start": v(-2592.13, -1832) * mm, "end": v(-2502.13, -1832) * mm});
            skLineSegment(sketch, "E2005", {"start": v(-2602.13, -1840) * mm, "end": v(-2492.13, -1840) * mm});
            skLineSegment(sketch, "E2006", {"start": v(-2492.13, -1834.67) * mm, "end": v(-2492.13, -1840) * mm});
            skLineSegment(sketch, "E2007", {"start": v(-2502.13, -1832) * mm, "end": v(-2492.13, -1834.67) * mm});
            skLineSegment(sketch, "E2008", {"start": v(-2547.13, -1405.05) * mm, "end": v(-2547.13, -1854) * mm});
            skLineSegment(sketch, "E2009", {"start": v(-2502.13, -1432) * mm, "end": v(-2502.13, -1832) * mm});
            skLineSegment(sketch, "E2010", {"start": v(-2508.53, -1893.1) * mm, "end": v(-2508.53, -1865.94) * mm});
            skLineSegment(sketch, "E2011", {"start": v(-2472.04, -1879.5) * mm, "end": v(-2622.23, -1879.5) * mm});
            skLineSegment(sketch, "E2012", {"start": v(-2494.63, -1891.3) * mm, "end": v(-2494.63, -1867.6) * mm});
            skLineSegment(sketch, "E2013", {"start": v(-2519.13, -1863.9) * mm, "end": v(-2519.13, -1864.6) * mm});
            skLineSegment(sketch, "E2014", {"start": v(-2480.53, -1860.5) * mm, "end": v(-2515.73, -1860.5) * mm});
            skLineSegment(sketch, "E2015", {"start": v(-2477.13, -1895.1) * mm, "end": v(-2477.13, -1863.9) * mm});
            skLineSegment(sketch, "E2016", {"start": v(-2515.73, -1898.5) * mm, "end": v(-2480.53, -1898.5) * mm});
            skLineSegment(sketch, "E2017", {"start": v(-2547.13, -1906.75) * mm, "end": v(-2547.13, -1854) * mm});
            skLineSegment(sketch, "E2018", {"start": v(-2561.14, -1869.07) * mm, "end": v(-2533.12, -1869.07) * mm});
            skLineSegment(sketch, "E2019", {"start": v(-2527.43, -1867.82) * mm, "end": v(-2508.53, -1860.5) * mm});
            skLineSegment(sketch, "E2020", {"start": v(-2533.12, -1889.92) * mm, "end": v(-2561.14, -1889.92) * mm});
            skLineSegment(sketch, "E2021", {"start": v(-2508.53, -1898.5) * mm, "end": v(-2527.43, -1891.17) * mm});
            skLineSegment(sketch, "E2022", {"start": v(-2519.13, -1894.38) * mm, "end": v(-2519.13, -1895.1) * mm});
            skLineSegment(sketch, "E2023", {"start": v(-2585.73, -1865.94) * mm, "end": v(-2585.73, -1893.1) * mm});
            skLineSegment(sketch, "E2024", {"start": v(-2599.63, -1867.6) * mm, "end": v(-2599.63, -1891.3) * mm});
            skLineSegment(sketch, "E2025", {"start": v(-2575.13, -1864.6) * mm, "end": v(-2575.13, -1863.9) * mm});
            skLineSegment(sketch, "E2026", {"start": v(-2578.53, -1860.5) * mm, "end": v(-2613.73, -1860.5) * mm});
            skLineSegment(sketch, "E2027", {"start": v(-2617.13, -1863.9) * mm, "end": v(-2617.13, -1895.1) * mm});
            skLineSegment(sketch, "E2028", {"start": v(-2613.73, -1898.5) * mm, "end": v(-2578.53, -1898.5) * mm});
            skLineSegment(sketch, "E2029", {"start": v(-2575.13, -1895.1) * mm, "end": v(-2575.13, -1894.38) * mm});
            skLineSegment(sketch, "E2030", {"start": v(-2585.73, -1860.5) * mm, "end": v(-2566.83, -1867.82) * mm});
            skLineSegment(sketch, "E2031", {"start": v(-2566.83, -1891.17) * mm, "end": v(-2585.73, -1898.5) * mm});
            skLineSegment(sketch, "E2032", {"start": v(-2564.08, -1890.24) * mm, "end": v(-2564.08, -1899.2) * mm});
            skLineSegment(sketch, "E2033", {"start": v(-2564.08, -1899.2) * mm, "end": v(-2530.18, -1899.2) * mm});
            skLineSegment(sketch, "E2034", {"start": v(-2530.18, -1899.2) * mm, "end": v(-2530.18, -1890.24) * mm});
            skLineSegment(sketch, "E2035", {"start": v(-2564.08, -1868.75) * mm, "end": v(-2564.08, -1865.2) * mm});
            skLineSegment(sketch, "E2036", {"start": v(-2564.08, -1865.2) * mm, "end": v(-2530.18, -1865.2) * mm});
            skLineSegment(sketch, "E2037", {"start": v(-2530.18, -1865.2) * mm, "end": v(-2530.18, -1868.75) * mm});
            skLineSegment(sketch, "E2038", {"start": v(-2562.13, -1404) * mm, "end": v(-2562.13, -1399) * mm});
            skLineSegment(sketch, "E2039", {"start": v(-2588.63, -1412) * mm, "end": v(-2580.63, -1404) * mm});
            skLineSegment(sketch, "E2040", {"start": v(-2588.63, -1417.5) * mm, "end": v(-2588.63, -1412) * mm});
            skLineSegment(sketch, "E2041", {"start": v(-2588.63, -1417.5) * mm, "end": v(-2591.13, -1420) * mm});
            skLineSegment(sketch, "E2042", {"start": v(-2591.13, -1420.5) * mm, "end": v(-2594.63, -1424) * mm});
            skLineSegment(sketch, "E2043", {"start": v(-2591.13, -1420) * mm, "end": v(-2591.13, -1420.5) * mm});
            skLineSegment(sketch, "E2044", {"start": v(-2602.13, -1429.31) * mm, "end": v(-2602.13, -1424) * mm});
            skLineSegment(sketch, "E2045", {"start": v(-2592.13, -1432) * mm, "end": v(-2602.13, -1429.31) * mm});
            skLineSegment(sketch, "E2046", {"start": v(-2532.13, -1399) * mm, "end": v(-2532.13, -1404) * mm});
            skLineSegment(sketch, "E2047", {"start": v(-2602.13, -1429.31) * mm, "end": v(-2492.13, -1429.31) * mm});
            skLineSegment(sketch, "E2048", {"start": v(-2588.63, -1412) * mm, "end": v(-2505.63, -1412) * mm});
            skLineSegment(sketch, "E2049", {"start": v(-2580.63, -1404) * mm, "end": v(-2513.63, -1404) * mm});
            skLineSegment(sketch, "E2050", {"start": v(-2513.63, -1404) * mm, "end": v(-2505.63, -1412) * mm});
            skLineSegment(sketch, "E2051", {"start": v(-2505.63, -1412) * mm, "end": v(-2505.63, -1417.5) * mm});
            skLineSegment(sketch, "E2052", {"start": v(-2503.13, -1420) * mm, "end": v(-2505.63, -1417.5) * mm});
            skLineSegment(sketch, "E2053", {"start": v(-2499.63, -1424) * mm, "end": v(-2503.13, -1420.5) * mm});
            skLineSegment(sketch, "E2054", {"start": v(-2503.13, -1420.5) * mm, "end": v(-2503.13, -1420) * mm});
            skLineSegment(sketch, "E2055", {"start": v(-2502.13, -1432) * mm, "end": v(-2592.13, -1432) * mm});
            skLineSegment(sketch, "E2056", {"start": v(-2492.13, -1424) * mm, "end": v(-2602.13, -1424) * mm});
            skLineSegment(sketch, "E2057", {"start": v(-2492.13, -1424) * mm, "end": v(-2492.13, -1429.31) * mm});
            skLineSegment(sketch, "E2058", {"start": v(-2492.13, -1429.31) * mm, "end": v(-2502.13, -1432) * mm});
            skLineSegment(sketch, "E2059", {"start": v(-2508.53, -1398.05) * mm, "end": v(-2508.53, -1370.9) * mm});
            skLineSegment(sketch, "E2060", {"start": v(-2622.23, -1384.5) * mm, "end": v(-2472.04, -1384.5) * mm});
            skLineSegment(sketch, "E2061", {"start": v(-2494.63, -1396.39) * mm, "end": v(-2494.63, -1372.68) * mm});
            skLineSegment(sketch, "E2062", {"start": v(-2519.13, -1399.38) * mm, "end": v(-2519.13, -1400.1) * mm});
            skLineSegment(sketch, "E2063", {"start": v(-2515.73, -1403.5) * mm, "end": v(-2480.53, -1403.5) * mm});
            skLineSegment(sketch, "E2064", {"start": v(-2477.13, -1400.1) * mm, "end": v(-2477.13, -1368.9) * mm});
            skLineSegment(sketch, "E2065", {"start": v(-2480.53, -1365.5) * mm, "end": v(-2515.73, -1365.5) * mm});
            skLineSegment(sketch, "E2066", {"start": v(-2533.12, -1394.92) * mm, "end": v(-2561.14, -1394.92) * mm});
            skLineSegment(sketch, "E2067", {"start": v(-2508.53, -1403.5) * mm, "end": v(-2527.43, -1396.17) * mm});
            skLineSegment(sketch, "E2068", {"start": v(-2561.14, -1374.07) * mm, "end": v(-2533.12, -1374.07) * mm});
            skLineSegment(sketch, "E2069", {"start": v(-2527.43, -1372.82) * mm, "end": v(-2508.53, -1365.5) * mm});
            skLineSegment(sketch, "E2070", {"start": v(-2519.13, -1368.9) * mm, "end": v(-2519.13, -1369.6) * mm});
            skLineSegment(sketch, "E2071", {"start": v(-2585.73, -1370.9) * mm, "end": v(-2585.73, -1398.05) * mm});
            skLineSegment(sketch, "E2072", {"start": v(-2599.63, -1372.68) * mm, "end": v(-2599.63, -1396.39) * mm});
            skLineSegment(sketch, "E2073", {"start": v(-2575.13, -1400.1) * mm, "end": v(-2575.13, -1399.38) * mm});
            skLineSegment(sketch, "E2074", {"start": v(-2613.73, -1403.5) * mm, "end": v(-2578.53, -1403.5) * mm});
            skLineSegment(sketch, "E2075", {"start": v(-2617.13, -1368.9) * mm, "end": v(-2617.13, -1400.1) * mm});
            skLineSegment(sketch, "E2076", {"start": v(-2578.53, -1365.5) * mm, "end": v(-2613.73, -1365.5) * mm});
            skLineSegment(sketch, "E2077", {"start": v(-2575.13, -1369.6) * mm, "end": v(-2575.13, -1368.9) * mm});
            skLineSegment(sketch, "E2078", {"start": v(-2566.83, -1396.17) * mm, "end": v(-2585.73, -1403.5) * mm});
            skLineSegment(sketch, "E2079", {"start": v(-2585.73, -1365.5) * mm, "end": v(-2566.83, -1372.82) * mm});
            skLineSegment(sketch, "E2080", {"start": v(-2564.08, -1364.8) * mm, "end": v(-2564.08, -1373.75) * mm});
            skLineSegment(sketch, "E2081", {"start": v(-2530.18, -1364.8) * mm, "end": v(-2564.08, -1364.8) * mm});
            skLineSegment(sketch, "E2082", {"start": v(-2530.18, -1373.75) * mm, "end": v(-2530.18, -1364.8) * mm});
            skLineSegment(sketch, "E2083", {"start": v(-2564.08, -1398.8) * mm, "end": v(-2564.08, -1395.24) * mm});
            skLineSegment(sketch, "E2084", {"start": v(-2530.18, -1398.8) * mm, "end": v(-2564.08, -1398.8) * mm});
            skLineSegment(sketch, "E2085", {"start": v(-2530.18, -1395.24) * mm, "end": v(-2530.18, -1398.8) * mm});
            skLineSegment(sketch, "E2086", {"start": v(-1812.13, -1865) * mm, "end": v(-1812.13, -1860) * mm});
            skLineSegment(sketch, "E2087", {"start": v(-1830.63, -1860) * mm, "end": v(-1838.63, -1852) * mm});
            skLineSegment(sketch, "E2088", {"start": v(-1838.63, -1852) * mm, "end": v(-1838.63, -1846.5) * mm});
            skLineSegment(sketch, "E2089", {"start": v(-1841.13, -1844) * mm, "end": v(-1838.63, -1846.5) * mm});
            skLineSegment(sketch, "E2090", {"start": v(-1844.63, -1840) * mm, "end": v(-1841.13, -1843.5) * mm});
            skLineSegment(sketch, "E2091", {"start": v(-1841.13, -1843.5) * mm, "end": v(-1841.13, -1844) * mm});
            skLineSegment(sketch, "E2092", {"start": v(-1852.13, -1840) * mm, "end": v(-1852.13, -1834.67) * mm});
            skLineSegment(sketch, "E2093", {"start": v(-1852.13, -1834.67) * mm, "end": v(-1842.13, -1832) * mm});
            skLineSegment(sketch, "E2094", {"start": v(-1842.13, -1832) * mm, "end": v(-1842.13, -1432) * mm});
            skLineSegment(sketch, "E2095", {"start": v(-1782.13, -1860) * mm, "end": v(-1782.13, -1865) * mm});
            skLineSegment(sketch, "E2096", {"start": v(-1742.13, -1834.67) * mm, "end": v(-1852.13, -1834.67) * mm});
            skLineSegment(sketch, "E2097", {"start": v(-1755.63, -1852) * mm, "end": v(-1838.63, -1852) * mm});
            skLineSegment(sketch, "E2098", {"start": v(-1763.63, -1860) * mm, "end": v(-1830.63, -1860) * mm});
            skLineSegment(sketch, "E2099", {"start": v(-1755.63, -1852) * mm, "end": v(-1763.63, -1860) * mm});
            skLineSegment(sketch, "E2100", {"start": v(-1755.63, -1846.5) * mm, "end": v(-1755.63, -1852) * mm});
            skLineSegment(sketch, "E2101", {"start": v(-1755.63, -1846.5) * mm, "end": v(-1753.13, -1844) * mm});
            skLineSegment(sketch, "E2102", {"start": v(-1753.13, -1843.5) * mm, "end": v(-1749.63, -1840) * mm});
            skLineSegment(sketch, "E2103", {"start": v(-1753.13, -1844) * mm, "end": v(-1753.13, -1843.5) * mm});
            skLineSegment(sketch, "E2104", {"start": v(-1842.13, -1832) * mm, "end": v(-1752.13, -1832) * mm});
            skLineSegment(sketch, "E2105", {"start": v(-1852.13, -1840) * mm, "end": v(-1742.13, -1840) * mm});
            skLineSegment(sketch, "E2106", {"start": v(-1742.13, -1834.67) * mm, "end": v(-1742.13, -1840) * mm});
            skLineSegment(sketch, "E2107", {"start": v(-1752.13, -1832) * mm, "end": v(-1742.13, -1834.67) * mm});
            skLineSegment(sketch, "E2108", {"start": v(-1797.13, -1405.05) * mm, "end": v(-1797.13, -1854) * mm});
            skLineSegment(sketch, "E2109", {"start": v(-1752.13, -1432) * mm, "end": v(-1752.13, -1832) * mm});
            skLineSegment(sketch, "E2110", {"start": v(-1758.53, -1893.1) * mm, "end": v(-1758.53, -1865.94) * mm});
            skLineSegment(sketch, "E2111", {"start": v(-1722.04, -1879.5) * mm, "end": v(-1872.23, -1879.5) * mm});
            skLineSegment(sketch, "E2112", {"start": v(-1744.63, -1891.3) * mm, "end": v(-1744.63, -1867.6) * mm});
            skLineSegment(sketch, "E2113", {"start": v(-1769.13, -1863.9) * mm, "end": v(-1769.13, -1864.6) * mm});
            skLineSegment(sketch, "E2114", {"start": v(-1730.53, -1860.5) * mm, "end": v(-1765.73, -1860.5) * mm});
            skLineSegment(sketch, "E2115", {"start": v(-1727.13, -1895.1) * mm, "end": v(-1727.13, -1863.9) * mm});
            skLineSegment(sketch, "E2116", {"start": v(-1765.73, -1898.5) * mm, "end": v(-1730.53, -1898.5) * mm});
            skLineSegment(sketch, "E2117", {"start": v(-1797.13, -1906.75) * mm, "end": v(-1797.13, -1854) * mm});
            skLineSegment(sketch, "E2118", {"start": v(-1811.14, -1869.07) * mm, "end": v(-1783.12, -1869.07) * mm});
            skLineSegment(sketch, "E2119", {"start": v(-1777.43, -1867.82) * mm, "end": v(-1758.53, -1860.5) * mm});
            skLineSegment(sketch, "E2120", {"start": v(-1783.12, -1889.92) * mm, "end": v(-1811.14, -1889.92) * mm});
            skLineSegment(sketch, "E2121", {"start": v(-1758.53, -1898.5) * mm, "end": v(-1777.43, -1891.17) * mm});
            skLineSegment(sketch, "E2122", {"start": v(-1769.13, -1894.38) * mm, "end": v(-1769.13, -1895.1) * mm});
            skLineSegment(sketch, "E2123", {"start": v(-1835.73, -1865.94) * mm, "end": v(-1835.73, -1893.1) * mm});
            skLineSegment(sketch, "E2124", {"start": v(-1849.63, -1867.6) * mm, "end": v(-1849.63, -1891.3) * mm});
            skLineSegment(sketch, "E2125", {"start": v(-1825.13, -1864.6) * mm, "end": v(-1825.13, -1863.9) * mm});
            skLineSegment(sketch, "E2126", {"start": v(-1828.53, -1860.5) * mm, "end": v(-1863.73, -1860.5) * mm});
            skLineSegment(sketch, "E2127", {"start": v(-1867.13, -1863.9) * mm, "end": v(-1867.13, -1895.1) * mm});
            skLineSegment(sketch, "E2128", {"start": v(-1863.73, -1898.5) * mm, "end": v(-1828.53, -1898.5) * mm});
            skLineSegment(sketch, "E2129", {"start": v(-1825.13, -1895.1) * mm, "end": v(-1825.13, -1894.38) * mm});
            skLineSegment(sketch, "E2130", {"start": v(-1835.73, -1860.5) * mm, "end": v(-1816.83, -1867.82) * mm});
            skLineSegment(sketch, "E2131", {"start": v(-1816.83, -1891.17) * mm, "end": v(-1835.73, -1898.5) * mm});
            skLineSegment(sketch, "E2132", {"start": v(-1814.08, -1890.24) * mm, "end": v(-1814.08, -1899.2) * mm});
            skLineSegment(sketch, "E2133", {"start": v(-1814.08, -1899.2) * mm, "end": v(-1780.18, -1899.2) * mm});
            skLineSegment(sketch, "E2134", {"start": v(-1780.18, -1899.2) * mm, "end": v(-1780.18, -1890.24) * mm});
            skLineSegment(sketch, "E2135", {"start": v(-1814.08, -1868.75) * mm, "end": v(-1814.08, -1865.2) * mm});
            skLineSegment(sketch, "E2136", {"start": v(-1814.08, -1865.2) * mm, "end": v(-1780.18, -1865.2) * mm});
            skLineSegment(sketch, "E2137", {"start": v(-1780.18, -1865.2) * mm, "end": v(-1780.18, -1868.75) * mm});
            skLineSegment(sketch, "E2138", {"start": v(-1812.13, -1404) * mm, "end": v(-1812.13, -1399) * mm});
            skLineSegment(sketch, "E2139", {"start": v(-1838.63, -1412) * mm, "end": v(-1830.63, -1404) * mm});
            skLineSegment(sketch, "E2140", {"start": v(-1838.63, -1417.5) * mm, "end": v(-1838.63, -1412) * mm});
            skLineSegment(sketch, "E2141", {"start": v(-1838.63, -1417.5) * mm, "end": v(-1841.13, -1420) * mm});
            skLineSegment(sketch, "E2142", {"start": v(-1841.13, -1420.5) * mm, "end": v(-1844.63, -1424) * mm});
            skLineSegment(sketch, "E2143", {"start": v(-1841.13, -1420) * mm, "end": v(-1841.13, -1420.5) * mm});
            skLineSegment(sketch, "E2144", {"start": v(-1852.13, -1429.31) * mm, "end": v(-1852.13, -1424) * mm});
            skLineSegment(sketch, "E2145", {"start": v(-1842.13, -1432) * mm, "end": v(-1852.13, -1429.31) * mm});
            skLineSegment(sketch, "E2146", {"start": v(-1782.13, -1399) * mm, "end": v(-1782.13, -1404) * mm});
            skLineSegment(sketch, "E2147", {"start": v(-1852.13, -1429.31) * mm, "end": v(-1742.13, -1429.31) * mm});
            skLineSegment(sketch, "E2148", {"start": v(-1838.63, -1412) * mm, "end": v(-1755.63, -1412) * mm});
            skLineSegment(sketch, "E2149", {"start": v(-1830.63, -1404) * mm, "end": v(-1763.63, -1404) * mm});
            skLineSegment(sketch, "E2150", {"start": v(-1763.63, -1404) * mm, "end": v(-1755.63, -1412) * mm});
            skLineSegment(sketch, "E2151", {"start": v(-1755.63, -1412) * mm, "end": v(-1755.63, -1417.5) * mm});
            skLineSegment(sketch, "E2152", {"start": v(-1753.13, -1420) * mm, "end": v(-1755.63, -1417.5) * mm});
            skLineSegment(sketch, "E2153", {"start": v(-1749.63, -1424) * mm, "end": v(-1753.13, -1420.5) * mm});
            skLineSegment(sketch, "E2154", {"start": v(-1753.13, -1420.5) * mm, "end": v(-1753.13, -1420) * mm});
            skLineSegment(sketch, "E2155", {"start": v(-1752.13, -1432) * mm, "end": v(-1842.13, -1432) * mm});
            skLineSegment(sketch, "E2156", {"start": v(-1742.13, -1424) * mm, "end": v(-1852.13, -1424) * mm});
            skLineSegment(sketch, "E2157", {"start": v(-1742.13, -1424) * mm, "end": v(-1742.13, -1429.31) * mm});
            skLineSegment(sketch, "E2158", {"start": v(-1742.13, -1429.31) * mm, "end": v(-1752.13, -1432) * mm});
            skLineSegment(sketch, "E2159", {"start": v(-1758.53, -1398.05) * mm, "end": v(-1758.53, -1370.9) * mm});
            skLineSegment(sketch, "E2160", {"start": v(-1872.23, -1384.5) * mm, "end": v(-1722.04, -1384.5) * mm});
            skLineSegment(sketch, "E2161", {"start": v(-1744.63, -1396.39) * mm, "end": v(-1744.63, -1372.68) * mm});
            skLineSegment(sketch, "E2162", {"start": v(-1769.13, -1399.38) * mm, "end": v(-1769.13, -1400.1) * mm});
            skLineSegment(sketch, "E2163", {"start": v(-1765.73, -1403.5) * mm, "end": v(-1730.53, -1403.5) * mm});
            skLineSegment(sketch, "E2164", {"start": v(-1727.13, -1400.1) * mm, "end": v(-1727.13, -1368.9) * mm});
            skLineSegment(sketch, "E2165", {"start": v(-1730.53, -1365.5) * mm, "end": v(-1765.73, -1365.5) * mm});
            skLineSegment(sketch, "E2166", {"start": v(-1758.53, -1403.5) * mm, "end": v(-1777.43, -1396.17) * mm});
            skLineSegment(sketch, "E2167", {"start": v(-1783.12, -1394.92) * mm, "end": v(-1811.14, -1394.92) * mm});
            skLineSegment(sketch, "E2168", {"start": v(-1811.14, -1374.07) * mm, "end": v(-1783.12, -1374.07) * mm});
            skLineSegment(sketch, "E2169", {"start": v(-1777.43, -1372.82) * mm, "end": v(-1758.53, -1365.5) * mm});
            skLineSegment(sketch, "E2170", {"start": v(-1769.13, -1368.9) * mm, "end": v(-1769.13, -1369.6) * mm});
            skLineSegment(sketch, "E2171", {"start": v(-1835.73, -1370.9) * mm, "end": v(-1835.73, -1398.05) * mm});
            skLineSegment(sketch, "E2172", {"start": v(-1849.63, -1372.68) * mm, "end": v(-1849.63, -1396.39) * mm});
            skLineSegment(sketch, "E2173", {"start": v(-1825.13, -1400.1) * mm, "end": v(-1825.13, -1399.38) * mm});
            skLineSegment(sketch, "E2174", {"start": v(-1863.73, -1403.5) * mm, "end": v(-1828.53, -1403.5) * mm});
            skLineSegment(sketch, "E2175", {"start": v(-1867.13, -1368.9) * mm, "end": v(-1867.13, -1400.1) * mm});
            skLineSegment(sketch, "E2176", {"start": v(-1828.53, -1365.5) * mm, "end": v(-1863.73, -1365.5) * mm});
            skLineSegment(sketch, "E2177", {"start": v(-1825.13, -1369.6) * mm, "end": v(-1825.13, -1368.9) * mm});
            skLineSegment(sketch, "E2178", {"start": v(-1816.83, -1396.17) * mm, "end": v(-1835.73, -1403.5) * mm});
            skLineSegment(sketch, "E2179", {"start": v(-1835.73, -1365.5) * mm, "end": v(-1816.83, -1372.82) * mm});
            skLineSegment(sketch, "E2180", {"start": v(-1814.08, -1364.8) * mm, "end": v(-1814.08, -1373.75) * mm});
            skLineSegment(sketch, "E2181", {"start": v(-1780.18, -1364.8) * mm, "end": v(-1814.08, -1364.8) * mm});
            skLineSegment(sketch, "E2182", {"start": v(-1780.18, -1373.75) * mm, "end": v(-1780.18, -1364.8) * mm});
            skLineSegment(sketch, "E2183", {"start": v(-1814.08, -1398.8) * mm, "end": v(-1814.08, -1395.24) * mm});
            skLineSegment(sketch, "E2184", {"start": v(-1780.18, -1398.8) * mm, "end": v(-1814.08, -1398.8) * mm});
            skLineSegment(sketch, "E2185", {"start": v(-1780.18, -1395.24) * mm, "end": v(-1780.18, -1398.8) * mm});
            skLineSegment(sketch, "E2186", {"start": v(-1062.13, -1865) * mm, "end": v(-1062.13, -1860) * mm});
            skLineSegment(sketch, "E2187", {"start": v(-1080.63, -1860) * mm, "end": v(-1088.63, -1852) * mm});
            skLineSegment(sketch, "E2188", {"start": v(-1088.63, -1852) * mm, "end": v(-1088.63, -1846.5) * mm});
            skLineSegment(sketch, "E2189", {"start": v(-1091.13, -1844) * mm, "end": v(-1088.63, -1846.5) * mm});
            skLineSegment(sketch, "E2190", {"start": v(-1094.63, -1840) * mm, "end": v(-1091.13, -1843.5) * mm});
            skLineSegment(sketch, "E2191", {"start": v(-1091.13, -1843.5) * mm, "end": v(-1091.13, -1844) * mm});
            skLineSegment(sketch, "E2192", {"start": v(-1102.13, -1840) * mm, "end": v(-1102.13, -1834.67) * mm});
            skLineSegment(sketch, "E2193", {"start": v(-1102.13, -1834.67) * mm, "end": v(-1092.13, -1832) * mm});
            skLineSegment(sketch, "E2194", {"start": v(-1092.13, -1832) * mm, "end": v(-1092.13, -1432) * mm});
            skLineSegment(sketch, "E2195", {"start": v(-1032.13, -1860) * mm, "end": v(-1032.13, -1865) * mm});
            skLineSegment(sketch, "E2196", {"start": v(-992.13, -1834.67) * mm, "end": v(-1102.13, -1834.67) * mm});
            skLineSegment(sketch, "E2197", {"start": v(-1005.63, -1852) * mm, "end": v(-1088.63, -1852) * mm});
            skLineSegment(sketch, "E2198", {"start": v(-1013.63, -1860) * mm, "end": v(-1080.63, -1860) * mm});
            skLineSegment(sketch, "E2199", {"start": v(-1005.63, -1852) * mm, "end": v(-1013.63, -1860) * mm});
            skLineSegment(sketch, "E2200", {"start": v(-1005.63, -1846.5) * mm, "end": v(-1005.63, -1852) * mm});
            skLineSegment(sketch, "E2201", {"start": v(-1005.63, -1846.5) * mm, "end": v(-1003.13, -1844) * mm});
            skLineSegment(sketch, "E2202", {"start": v(-1003.13, -1843.5) * mm, "end": v(-999.63, -1840) * mm});
            skLineSegment(sketch, "E2203", {"start": v(-1003.13, -1844) * mm, "end": v(-1003.13, -1843.5) * mm});
            skLineSegment(sketch, "E2204", {"start": v(-1092.13, -1832) * mm, "end": v(-1002.13, -1832) * mm});
            skLineSegment(sketch, "E2205", {"start": v(-1102.13, -1840) * mm, "end": v(-992.13, -1840) * mm});
            skLineSegment(sketch, "E2206", {"start": v(-992.13, -1834.67) * mm, "end": v(-992.13, -1840) * mm});
            skLineSegment(sketch, "E2207", {"start": v(-1002.13, -1832) * mm, "end": v(-992.13, -1834.67) * mm});
            skLineSegment(sketch, "E2208", {"start": v(-1047.13, -1405.05) * mm, "end": v(-1047.13, -1864) * mm});
            skLineSegment(sketch, "E2209", {"start": v(-1002.13, -1432) * mm, "end": v(-1002.13, -1832) * mm});
            skLineSegment(sketch, "E2210", {"start": v(-1008.53, -1893.1) * mm, "end": v(-1008.53, -1865.94) * mm});
            skLineSegment(sketch, "E2211", {"start": v(-972.04, -1879.5) * mm, "end": v(-1122.23, -1879.5) * mm});
            skLineSegment(sketch, "E2212", {"start": v(-994.63, -1891.3) * mm, "end": v(-994.63, -1867.6) * mm});
            skLineSegment(sketch, "E2213", {"start": v(-1019.13, -1863.9) * mm, "end": v(-1019.13, -1864.6) * mm});
            skLineSegment(sketch, "E2214", {"start": v(-980.53, -1860.5) * mm, "end": v(-1015.73, -1860.5) * mm});
            skLineSegment(sketch, "E2215", {"start": v(-977.13, -1895.1) * mm, "end": v(-977.13, -1863.9) * mm});
            skLineSegment(sketch, "E2216", {"start": v(-1015.73, -1898.5) * mm, "end": v(-980.53, -1898.5) * mm});
            skLineSegment(sketch, "E2217", {"start": v(-1047.13, -1906.75) * mm, "end": v(-1047.13, -1864) * mm});
            skLineSegment(sketch, "E2218", {"start": v(-1027.43, -1867.82) * mm, "end": v(-1008.53, -1860.5) * mm});
            skLineSegment(sketch, "E2219", {"start": v(-1061.14, -1869.07) * mm, "end": v(-1033.12, -1869.07) * mm});
            skLineSegment(sketch, "E2220", {"start": v(-1033.12, -1889.92) * mm, "end": v(-1061.14, -1889.92) * mm});
            skLineSegment(sketch, "E2221", {"start": v(-1008.53, -1898.5) * mm, "end": v(-1027.43, -1891.17) * mm});
            skLineSegment(sketch, "E2222", {"start": v(-1019.13, -1894.38) * mm, "end": v(-1019.13, -1895.1) * mm});
            skLineSegment(sketch, "E2223", {"start": v(-1085.73, -1865.94) * mm, "end": v(-1085.73, -1893.1) * mm});
            skLineSegment(sketch, "E2224", {"start": v(-1099.63, -1867.6) * mm, "end": v(-1099.63, -1891.3) * mm});
            skLineSegment(sketch, "E2225", {"start": v(-1075.13, -1864.6) * mm, "end": v(-1075.13, -1863.9) * mm});
            skLineSegment(sketch, "E2226", {"start": v(-1078.53, -1860.5) * mm, "end": v(-1113.73, -1860.5) * mm});
            skLineSegment(sketch, "E2227", {"start": v(-1117.13, -1863.9) * mm, "end": v(-1117.13, -1895.1) * mm});
            skLineSegment(sketch, "E2228", {"start": v(-1113.73, -1898.5) * mm, "end": v(-1078.53, -1898.5) * mm});
            skLineSegment(sketch, "E2229", {"start": v(-1075.13, -1895.1) * mm, "end": v(-1075.13, -1894.38) * mm});
            skLineSegment(sketch, "E2230", {"start": v(-1085.73, -1860.5) * mm, "end": v(-1066.83, -1867.82) * mm});
            skLineSegment(sketch, "E2231", {"start": v(-1066.83, -1891.17) * mm, "end": v(-1085.73, -1898.5) * mm});
            skLineSegment(sketch, "E2232", {"start": v(-1064.08, -1890.24) * mm, "end": v(-1064.08, -1899.2) * mm});
            skLineSegment(sketch, "E2233", {"start": v(-1064.08, -1899.2) * mm, "end": v(-1030.18, -1899.2) * mm});
            skLineSegment(sketch, "E2234", {"start": v(-1030.18, -1899.2) * mm, "end": v(-1030.18, -1890.24) * mm});
            skLineSegment(sketch, "E2235", {"start": v(-1064.08, -1868.75) * mm, "end": v(-1064.08, -1865.2) * mm});
            skLineSegment(sketch, "E2236", {"start": v(-1064.08, -1865.2) * mm, "end": v(-1030.18, -1865.2) * mm});
            skLineSegment(sketch, "E2237", {"start": v(-1030.18, -1865.2) * mm, "end": v(-1030.18, -1868.75) * mm});
            skLineSegment(sketch, "E2238", {"start": v(-1062.13, -1404) * mm, "end": v(-1062.13, -1399) * mm});
            skLineSegment(sketch, "E2239", {"start": v(-1088.63, -1412) * mm, "end": v(-1080.63, -1404) * mm});
            skLineSegment(sketch, "E2240", {"start": v(-1088.63, -1417.5) * mm, "end": v(-1088.63, -1412) * mm});
            skLineSegment(sketch, "E2241", {"start": v(-1088.63, -1417.5) * mm, "end": v(-1091.13, -1420) * mm});
            skLineSegment(sketch, "E2242", {"start": v(-1091.13, -1420.5) * mm, "end": v(-1094.63, -1424) * mm});
            skLineSegment(sketch, "E2243", {"start": v(-1091.13, -1420) * mm, "end": v(-1091.13, -1420.5) * mm});
            skLineSegment(sketch, "E2244", {"start": v(-1102.13, -1429.31) * mm, "end": v(-1102.13, -1424) * mm});
            skLineSegment(sketch, "E2245", {"start": v(-1092.13, -1432) * mm, "end": v(-1102.13, -1429.31) * mm});
            skLineSegment(sketch, "E2246", {"start": v(-1032.13, -1399) * mm, "end": v(-1032.13, -1404) * mm});
            skLineSegment(sketch, "E2247", {"start": v(-1102.13, -1429.31) * mm, "end": v(-992.13, -1429.31) * mm});
            skLineSegment(sketch, "E2248", {"start": v(-1088.63, -1412) * mm, "end": v(-1005.63, -1412) * mm});
            skLineSegment(sketch, "E2249", {"start": v(-1080.63, -1404) * mm, "end": v(-1013.63, -1404) * mm});
            skLineSegment(sketch, "E2250", {"start": v(-1013.63, -1404) * mm, "end": v(-1005.63, -1412) * mm});
            skLineSegment(sketch, "E2251", {"start": v(-1005.63, -1412) * mm, "end": v(-1005.63, -1417.5) * mm});
            skLineSegment(sketch, "E2252", {"start": v(-1003.13, -1420) * mm, "end": v(-1005.63, -1417.5) * mm});
            skLineSegment(sketch, "E2253", {"start": v(-999.63, -1424) * mm, "end": v(-1003.13, -1420.5) * mm});
            skLineSegment(sketch, "E2254", {"start": v(-1003.13, -1420.5) * mm, "end": v(-1003.13, -1420) * mm});
            skLineSegment(sketch, "E2255", {"start": v(-1002.13, -1432) * mm, "end": v(-1092.13, -1432) * mm});
            skLineSegment(sketch, "E2256", {"start": v(-992.13, -1424) * mm, "end": v(-1102.13, -1424) * mm});
            skLineSegment(sketch, "E2257", {"start": v(-992.13, -1424) * mm, "end": v(-992.13, -1429.31) * mm});
            skLineSegment(sketch, "E2258", {"start": v(-992.13, -1429.31) * mm, "end": v(-1002.13, -1432) * mm});
            skLineSegment(sketch, "E2259", {"start": v(-1008.53, -1398.05) * mm, "end": v(-1008.53, -1370.9) * mm});
            skLineSegment(sketch, "E2260", {"start": v(-1122.23, -1384.5) * mm, "end": v(-972.04, -1384.5) * mm});
            skLineSegment(sketch, "E2261", {"start": v(-994.63, -1396.39) * mm, "end": v(-994.63, -1372.68) * mm});
            skLineSegment(sketch, "E2262", {"start": v(-1019.13, -1399.38) * mm, "end": v(-1019.13, -1400.1) * mm});
            skLineSegment(sketch, "E2263", {"start": v(-1015.73, -1403.5) * mm, "end": v(-980.53, -1403.5) * mm});
            skLineSegment(sketch, "E2264", {"start": v(-977.13, -1400.1) * mm, "end": v(-977.13, -1368.9) * mm});
            skLineSegment(sketch, "E2265", {"start": v(-980.53, -1365.5) * mm, "end": v(-1015.73, -1365.5) * mm});
            skLineSegment(sketch, "E2266", {"start": v(-1033.12, -1394.92) * mm, "end": v(-1061.14, -1394.92) * mm});
            skLineSegment(sketch, "E2267", {"start": v(-1008.53, -1403.5) * mm, "end": v(-1027.43, -1396.17) * mm});
            skLineSegment(sketch, "E2268", {"start": v(-1061.14, -1374.07) * mm, "end": v(-1033.12, -1374.07) * mm});
            skLineSegment(sketch, "E2269", {"start": v(-1027.43, -1372.82) * mm, "end": v(-1008.53, -1365.5) * mm});
            skLineSegment(sketch, "E2270", {"start": v(-1019.13, -1368.9) * mm, "end": v(-1019.13, -1369.6) * mm});
            skLineSegment(sketch, "E2271", {"start": v(-1085.73, -1370.9) * mm, "end": v(-1085.73, -1398.05) * mm});
            skLineSegment(sketch, "E2272", {"start": v(-1099.63, -1372.68) * mm, "end": v(-1099.63, -1396.39) * mm});
            skLineSegment(sketch, "E2273", {"start": v(-1075.13, -1400.1) * mm, "end": v(-1075.13, -1399.38) * mm});
            skLineSegment(sketch, "E2274", {"start": v(-1113.73, -1403.5) * mm, "end": v(-1078.53, -1403.5) * mm});
            skLineSegment(sketch, "E2275", {"start": v(-1117.13, -1368.9) * mm, "end": v(-1117.13, -1400.1) * mm});
            skLineSegment(sketch, "E2276", {"start": v(-1078.53, -1365.5) * mm, "end": v(-1113.73, -1365.5) * mm});
            skLineSegment(sketch, "E2277", {"start": v(-1075.13, -1369.6) * mm, "end": v(-1075.13, -1368.9) * mm});
            skLineSegment(sketch, "E2278", {"start": v(-1066.83, -1396.17) * mm, "end": v(-1085.73, -1403.5) * mm});
            skLineSegment(sketch, "E2279", {"start": v(-1085.73, -1365.5) * mm, "end": v(-1066.83, -1372.82) * mm});
            skLineSegment(sketch, "E2280", {"start": v(-1064.08, -1364.8) * mm, "end": v(-1064.08, -1373.75) * mm});
            skLineSegment(sketch, "E2281", {"start": v(-1030.18, -1364.8) * mm, "end": v(-1064.08, -1364.8) * mm});
            skLineSegment(sketch, "E2282", {"start": v(-1030.18, -1373.75) * mm, "end": v(-1030.18, -1364.8) * mm});
            skLineSegment(sketch, "E2283", {"start": v(-1064.08, -1398.8) * mm, "end": v(-1064.08, -1395.24) * mm});
            skLineSegment(sketch, "E2284", {"start": v(-1030.18, -1398.8) * mm, "end": v(-1064.08, -1398.8) * mm});
            skLineSegment(sketch, "E2285", {"start": v(-1030.18, -1395.24) * mm, "end": v(-1030.18, -1398.8) * mm});
            skLineSegment(sketch, "E2286", {"start": v(-312.13, -1865) * mm, "end": v(-312.13, -1860) * mm});
            skLineSegment(sketch, "E2287", {"start": v(-330.63, -1860) * mm, "end": v(-338.63, -1852) * mm});
            skLineSegment(sketch, "E2288", {"start": v(-338.63, -1852) * mm, "end": v(-338.63, -1846.5) * mm});
            skLineSegment(sketch, "E2289", {"start": v(-341.13, -1844) * mm, "end": v(-338.63, -1846.5) * mm});
            skLineSegment(sketch, "E2290", {"start": v(-344.63, -1840) * mm, "end": v(-341.13, -1843.5) * mm});
            skLineSegment(sketch, "E2291", {"start": v(-341.13, -1843.5) * mm, "end": v(-341.13, -1844) * mm});
            skLineSegment(sketch, "E2292", {"start": v(-352.13, -1840) * mm, "end": v(-352.13, -1834.67) * mm});
            skLineSegment(sketch, "E2293", {"start": v(-352.13, -1834.67) * mm, "end": v(-342.13, -1832) * mm});
            skLineSegment(sketch, "E2294", {"start": v(-342.13, -1832) * mm, "end": v(-342.13, -1432) * mm});
            skLineSegment(sketch, "E2295", {"start": v(-282.13, -1860) * mm, "end": v(-282.13, -1865) * mm});
            skLineSegment(sketch, "E2296", {"start": v(-242.13, -1834.67) * mm, "end": v(-352.13, -1834.67) * mm});
            skLineSegment(sketch, "E2297", {"start": v(-255.63, -1852) * mm, "end": v(-338.63, -1852) * mm});
            skLineSegment(sketch, "E2298", {"start": v(-263.63, -1860) * mm, "end": v(-330.63, -1860) * mm});
            skLineSegment(sketch, "E2299", {"start": v(-255.63, -1852) * mm, "end": v(-263.63, -1860) * mm});
            skLineSegment(sketch, "E2300", {"start": v(-255.63, -1846.5) * mm, "end": v(-255.63, -1852) * mm});
            skLineSegment(sketch, "E2301", {"start": v(-255.63, -1846.5) * mm, "end": v(-253.13, -1844) * mm});
            skLineSegment(sketch, "E2302", {"start": v(-253.13, -1843.5) * mm, "end": v(-249.63, -1840) * mm});
            skLineSegment(sketch, "E2303", {"start": v(-253.13, -1844) * mm, "end": v(-253.13, -1843.5) * mm});
            skLineSegment(sketch, "E2304", {"start": v(-342.13, -1832) * mm, "end": v(-252.13, -1832) * mm});
            skLineSegment(sketch, "E2305", {"start": v(-352.13, -1840) * mm, "end": v(-242.13, -1840) * mm});
            skLineSegment(sketch, "E2306", {"start": v(-242.13, -1834.67) * mm, "end": v(-242.13, -1840) * mm});
            skLineSegment(sketch, "E2307", {"start": v(-252.13, -1832) * mm, "end": v(-242.13, -1834.67) * mm});
            skLineSegment(sketch, "E2308", {"start": v(-297.13, -1405.05) * mm, "end": v(-297.13, -1854) * mm});
            skLineSegment(sketch, "E2309", {"start": v(-252.13, -1432) * mm, "end": v(-252.13, -1832) * mm});
            skLineSegment(sketch, "E2310", {"start": v(-258.53, -1893.1) * mm, "end": v(-258.53, -1865.94) * mm});
            skLineSegment(sketch, "E2311", {"start": v(-222.04, -1879.5) * mm, "end": v(-372.23, -1879.5) * mm});
            skLineSegment(sketch, "E2312", {"start": v(-244.63, -1891.3) * mm, "end": v(-244.63, -1867.6) * mm});
            skLineSegment(sketch, "E2313", {"start": v(-269.13, -1863.9) * mm, "end": v(-269.13, -1864.6) * mm});
            skLineSegment(sketch, "E2314", {"start": v(-230.53, -1860.5) * mm, "end": v(-265.73, -1860.5) * mm});
            skLineSegment(sketch, "E2315", {"start": v(-227.13, -1895.1) * mm, "end": v(-227.13, -1863.9) * mm});
            skLineSegment(sketch, "E2316", {"start": v(-265.73, -1898.5) * mm, "end": v(-230.53, -1898.5) * mm});
            skLineSegment(sketch, "E2317", {"start": v(-297.13, -1906.75) * mm, "end": v(-297.13, -1854) * mm});
            skLineSegment(sketch, "E2318", {"start": v(-277.43, -1867.82) * mm, "end": v(-258.53, -1860.5) * mm});
            skLineSegment(sketch, "E2319", {"start": v(-311.14, -1869.07) * mm, "end": v(-283.12, -1869.07) * mm});
            skLineSegment(sketch, "E2320", {"start": v(-283.12, -1889.92) * mm, "end": v(-311.14, -1889.92) * mm});
            skLineSegment(sketch, "E2321", {"start": v(-258.53, -1898.5) * mm, "end": v(-277.43, -1891.17) * mm});
            skLineSegment(sketch, "E2322", {"start": v(-269.13, -1894.38) * mm, "end": v(-269.13, -1895.1) * mm});
            skLineSegment(sketch, "E2323", {"start": v(-335.73, -1865.94) * mm, "end": v(-335.73, -1893.1) * mm});
            skLineSegment(sketch, "E2324", {"start": v(-349.63, -1867.6) * mm, "end": v(-349.63, -1891.3) * mm});
            skLineSegment(sketch, "E2325", {"start": v(-325.13, -1864.6) * mm, "end": v(-325.13, -1863.9) * mm});
            skLineSegment(sketch, "E2326", {"start": v(-328.53, -1860.5) * mm, "end": v(-363.73, -1860.5) * mm});
            skLineSegment(sketch, "E2327", {"start": v(-367.13, -1863.9) * mm, "end": v(-367.13, -1895.1) * mm});
            skLineSegment(sketch, "E2328", {"start": v(-363.73, -1898.5) * mm, "end": v(-328.53, -1898.5) * mm});
            skLineSegment(sketch, "E2329", {"start": v(-325.13, -1895.1) * mm, "end": v(-325.13, -1894.38) * mm});
            skLineSegment(sketch, "E2330", {"start": v(-335.73, -1860.5) * mm, "end": v(-316.83, -1867.82) * mm});
            skLineSegment(sketch, "E2331", {"start": v(-316.83, -1891.17) * mm, "end": v(-335.73, -1898.5) * mm});
            skLineSegment(sketch, "E2332", {"start": v(-314.08, -1890.24) * mm, "end": v(-314.08, -1899.2) * mm});
            skLineSegment(sketch, "E2333", {"start": v(-314.08, -1899.2) * mm, "end": v(-280.18, -1899.2) * mm});
            skLineSegment(sketch, "E2334", {"start": v(-280.18, -1899.2) * mm, "end": v(-280.18, -1890.24) * mm});
            skLineSegment(sketch, "E2335", {"start": v(-314.08, -1868.75) * mm, "end": v(-314.08, -1865.2) * mm});
            skLineSegment(sketch, "E2336", {"start": v(-314.08, -1865.2) * mm, "end": v(-280.18, -1865.2) * mm});
            skLineSegment(sketch, "E2337", {"start": v(-280.18, -1865.2) * mm, "end": v(-280.18, -1868.75) * mm});
            skLineSegment(sketch, "E2338", {"start": v(-312.13, -1404) * mm, "end": v(-312.13, -1399) * mm});
            skLineSegment(sketch, "E2339", {"start": v(-338.63, -1412) * mm, "end": v(-330.63, -1404) * mm});
            skLineSegment(sketch, "E2340", {"start": v(-338.63, -1417.5) * mm, "end": v(-338.63, -1412) * mm});
            skLineSegment(sketch, "E2341", {"start": v(-338.63, -1417.5) * mm, "end": v(-341.13, -1420) * mm});
            skLineSegment(sketch, "E2342", {"start": v(-341.13, -1420.5) * mm, "end": v(-344.63, -1424) * mm});
            skLineSegment(sketch, "E2343", {"start": v(-341.13, -1420) * mm, "end": v(-341.13, -1420.5) * mm});
            skLineSegment(sketch, "E2344", {"start": v(-352.13, -1429.31) * mm, "end": v(-352.13, -1424) * mm});
            skLineSegment(sketch, "E2345", {"start": v(-342.13, -1432) * mm, "end": v(-352.13, -1429.31) * mm});
            skLineSegment(sketch, "E2346", {"start": v(-282.13, -1399) * mm, "end": v(-282.13, -1404) * mm});
            skLineSegment(sketch, "E2347", {"start": v(-352.13, -1429.31) * mm, "end": v(-242.13, -1429.31) * mm});
            skLineSegment(sketch, "E2348", {"start": v(-338.63, -1412) * mm, "end": v(-255.63, -1412) * mm});
            skLineSegment(sketch, "E2349", {"start": v(-330.63, -1404) * mm, "end": v(-263.63, -1404) * mm});
            skLineSegment(sketch, "E2350", {"start": v(-263.63, -1404) * mm, "end": v(-255.63, -1412) * mm});
            skLineSegment(sketch, "E2351", {"start": v(-255.63, -1412) * mm, "end": v(-255.63, -1417.5) * mm});
            skLineSegment(sketch, "E2352", {"start": v(-253.13, -1420) * mm, "end": v(-255.63, -1417.5) * mm});
            skLineSegment(sketch, "E2353", {"start": v(-249.63, -1424) * mm, "end": v(-253.13, -1420.5) * mm});
            skLineSegment(sketch, "E2354", {"start": v(-253.13, -1420.5) * mm, "end": v(-253.13, -1420) * mm});
            skLineSegment(sketch, "E2355", {"start": v(-252.13, -1432) * mm, "end": v(-342.13, -1432) * mm});
            skLineSegment(sketch, "E2356", {"start": v(-242.13, -1424) * mm, "end": v(-352.13, -1424) * mm});
            skLineSegment(sketch, "E2357", {"start": v(-242.13, -1424) * mm, "end": v(-242.13, -1429.31) * mm});
            skLineSegment(sketch, "E2358", {"start": v(-242.13, -1429.31) * mm, "end": v(-252.13, -1432) * mm});
            skLineSegment(sketch, "E2359", {"start": v(-258.53, -1398.05) * mm, "end": v(-258.53, -1370.9) * mm});
            skLineSegment(sketch, "E2360", {"start": v(-372.23, -1384.5) * mm, "end": v(-222.04, -1384.5) * mm});
            skLineSegment(sketch, "E2361", {"start": v(-244.63, -1396.39) * mm, "end": v(-244.63, -1372.68) * mm});
            skLineSegment(sketch, "E2362", {"start": v(-269.13, -1399.38) * mm, "end": v(-269.13, -1400.1) * mm});
            skLineSegment(sketch, "E2363", {"start": v(-265.73, -1403.5) * mm, "end": v(-230.53, -1403.5) * mm});
            skLineSegment(sketch, "E2364", {"start": v(-227.13, -1400.1) * mm, "end": v(-227.13, -1368.9) * mm});
            skLineSegment(sketch, "E2365", {"start": v(-230.53, -1365.5) * mm, "end": v(-265.73, -1365.5) * mm});
            skLineSegment(sketch, "E2366", {"start": v(-283.12, -1394.92) * mm, "end": v(-311.14, -1394.92) * mm});
            skLineSegment(sketch, "E2367", {"start": v(-258.53, -1403.5) * mm, "end": v(-277.43, -1396.17) * mm});
            skLineSegment(sketch, "E2368", {"start": v(-311.14, -1374.07) * mm, "end": v(-283.12, -1374.07) * mm});
            skLineSegment(sketch, "E2369", {"start": v(-277.43, -1372.82) * mm, "end": v(-258.53, -1365.5) * mm});
            skLineSegment(sketch, "E2370", {"start": v(-269.13, -1368.9) * mm, "end": v(-269.13, -1369.6) * mm});
            skLineSegment(sketch, "E2371", {"start": v(-335.73, -1370.9) * mm, "end": v(-335.73, -1398.05) * mm});
            skLineSegment(sketch, "E2372", {"start": v(-349.63, -1372.68) * mm, "end": v(-349.63, -1396.39) * mm});
            skLineSegment(sketch, "E2373", {"start": v(-325.13, -1400.1) * mm, "end": v(-325.13, -1399.38) * mm});
            skLineSegment(sketch, "E2374", {"start": v(-363.73, -1403.5) * mm, "end": v(-328.53, -1403.5) * mm});
            skLineSegment(sketch, "E2375", {"start": v(-367.13, -1368.9) * mm, "end": v(-367.13, -1400.1) * mm});
            skLineSegment(sketch, "E2376", {"start": v(-328.53, -1365.5) * mm, "end": v(-363.73, -1365.5) * mm});
            skLineSegment(sketch, "E2377", {"start": v(-325.13, -1369.6) * mm, "end": v(-325.13, -1368.9) * mm});
            skLineSegment(sketch, "E2378", {"start": v(-316.83, -1396.17) * mm, "end": v(-335.73, -1403.5) * mm});
            skLineSegment(sketch, "E2379", {"start": v(-335.73, -1365.5) * mm, "end": v(-316.83, -1372.82) * mm});
            skLineSegment(sketch, "E2380", {"start": v(-314.08, -1364.8) * mm, "end": v(-314.08, -1373.75) * mm});
            skLineSegment(sketch, "E2381", {"start": v(-280.18, -1364.8) * mm, "end": v(-314.08, -1364.8) * mm});
            skLineSegment(sketch, "E2382", {"start": v(-280.18, -1373.75) * mm, "end": v(-280.18, -1364.8) * mm});
            skLineSegment(sketch, "E2383", {"start": v(-314.08, -1398.8) * mm, "end": v(-314.08, -1395.24) * mm});
            skLineSegment(sketch, "E2384", {"start": v(-280.18, -1398.8) * mm, "end": v(-314.08, -1398.8) * mm});
            skLineSegment(sketch, "E2385", {"start": v(-280.18, -1395.24) * mm, "end": v(-280.18, -1398.8) * mm});
            skLineSegment(sketch, "E2386", {"start": v(437.87, -1865) * mm, "end": v(437.87, -1860) * mm});
            skLineSegment(sketch, "E2387", {"start": v(419.37, -1860) * mm, "end": v(411.37, -1852) * mm});
            skLineSegment(sketch, "E2388", {"start": v(411.37, -1852) * mm, "end": v(411.37, -1846.5) * mm});
            skLineSegment(sketch, "E2389", {"start": v(408.87, -1844) * mm, "end": v(411.37, -1846.5) * mm});
            skLineSegment(sketch, "E2390", {"start": v(405.37, -1840) * mm, "end": v(408.87, -1843.5) * mm});
            skLineSegment(sketch, "E2391", {"start": v(408.87, -1843.5) * mm, "end": v(408.87, -1844) * mm});
            skLineSegment(sketch, "E2392", {"start": v(397.87, -1840) * mm, "end": v(397.87, -1834.67) * mm});
            skLineSegment(sketch, "E2393", {"start": v(397.87, -1834.67) * mm, "end": v(407.87, -1832) * mm});
            skLineSegment(sketch, "E2394", {"start": v(407.87, -1832) * mm, "end": v(407.87, -1432) * mm});
            skLineSegment(sketch, "E2395", {"start": v(467.87, -1860) * mm, "end": v(467.87, -1865) * mm});
            skLineSegment(sketch, "E2396", {"start": v(507.87, -1834.67) * mm, "end": v(397.87, -1834.67) * mm});
            skLineSegment(sketch, "E2397", {"start": v(494.37, -1852) * mm, "end": v(411.37, -1852) * mm});
            skLineSegment(sketch, "E2398", {"start": v(486.37, -1860) * mm, "end": v(419.37, -1860) * mm});
            skLineSegment(sketch, "E2399", {"start": v(494.37, -1852) * mm, "end": v(486.37, -1860) * mm});
            skLineSegment(sketch, "E2400", {"start": v(494.37, -1846.5) * mm, "end": v(494.37, -1852) * mm});
            skLineSegment(sketch, "E2401", {"start": v(494.37, -1846.5) * mm, "end": v(496.87, -1844) * mm});
            skLineSegment(sketch, "E2402", {"start": v(496.87, -1843.5) * mm, "end": v(500.37, -1840) * mm});
            skLineSegment(sketch, "E2403", {"start": v(496.87, -1844) * mm, "end": v(496.87, -1843.5) * mm});
            skLineSegment(sketch, "E2404", {"start": v(407.87, -1832) * mm, "end": v(497.87, -1832) * mm});
            skLineSegment(sketch, "E2405", {"start": v(397.87, -1840) * mm, "end": v(507.87, -1840) * mm});
            skLineSegment(sketch, "E2406", {"start": v(507.87, -1834.67) * mm, "end": v(507.87, -1840) * mm});
            skLineSegment(sketch, "E2407", {"start": v(497.87, -1832) * mm, "end": v(507.87, -1834.67) * mm});
            skLineSegment(sketch, "E2408", {"start": v(452.87, -1405.05) * mm, "end": v(452.87, -1854) * mm});
            skLineSegment(sketch, "E2409", {"start": v(497.87, -1432) * mm, "end": v(497.87, -1832) * mm});
            skLineSegment(sketch, "E2410", {"start": v(491.47, -1893.1) * mm, "end": v(491.47, -1865.94) * mm});
            skLineSegment(sketch, "E2411", {"start": v(527.96, -1879.5) * mm, "end": v(377.77, -1879.5) * mm});
            skLineSegment(sketch, "E2412", {"start": v(505.37, -1891.3) * mm, "end": v(505.37, -1867.6) * mm});
            skLineSegment(sketch, "E2413", {"start": v(480.87, -1863.9) * mm, "end": v(480.87, -1864.6) * mm});
            skLineSegment(sketch, "E2414", {"start": v(519.47, -1860.5) * mm, "end": v(484.27, -1860.5) * mm});
            skLineSegment(sketch, "E2415", {"start": v(522.87, -1895.1) * mm, "end": v(522.87, -1863.9) * mm});
            skLineSegment(sketch, "E2416", {"start": v(484.27, -1898.5) * mm, "end": v(519.47, -1898.5) * mm});
            skLineSegment(sketch, "E2417", {"start": v(452.87, -1906.75) * mm, "end": v(452.87, -1854) * mm});
            skLineSegment(sketch, "E2418", {"start": v(472.57, -1867.82) * mm, "end": v(491.47, -1860.5) * mm});
            skLineSegment(sketch, "E2419", {"start": v(438.86, -1869.07) * mm, "end": v(466.88, -1869.07) * mm});
            skLineSegment(sketch, "E2420", {"start": v(466.88, -1889.92) * mm, "end": v(438.86, -1889.92) * mm});
            skLineSegment(sketch, "E2421", {"start": v(491.47, -1898.5) * mm, "end": v(472.57, -1891.17) * mm});
            skLineSegment(sketch, "E2422", {"start": v(480.87, -1894.38) * mm, "end": v(480.87, -1895.1) * mm});
            skLineSegment(sketch, "E2423", {"start": v(414.27, -1865.94) * mm, "end": v(414.27, -1893.1) * mm});
            skLineSegment(sketch, "E2424", {"start": v(400.37, -1867.6) * mm, "end": v(400.37, -1891.3) * mm});
            skLineSegment(sketch, "E2425", {"start": v(424.87, -1864.6) * mm, "end": v(424.87, -1863.9) * mm});
            skLineSegment(sketch, "E2426", {"start": v(421.47, -1860.5) * mm, "end": v(386.27, -1860.5) * mm});
            skLineSegment(sketch, "E2427", {"start": v(382.87, -1863.9) * mm, "end": v(382.87, -1895.1) * mm});
            skLineSegment(sketch, "E2428", {"start": v(386.27, -1898.5) * mm, "end": v(421.47, -1898.5) * mm});
            skLineSegment(sketch, "E2429", {"start": v(424.87, -1895.1) * mm, "end": v(424.87, -1894.38) * mm});
            skLineSegment(sketch, "E2430", {"start": v(414.27, -1860.5) * mm, "end": v(433.17, -1867.82) * mm});
            skLineSegment(sketch, "E2431", {"start": v(433.17, -1891.17) * mm, "end": v(414.27, -1898.5) * mm});
            skLineSegment(sketch, "E2432", {"start": v(435.92, -1890.24) * mm, "end": v(435.92, -1899.2) * mm});
            skLineSegment(sketch, "E2433", {"start": v(435.92, -1899.2) * mm, "end": v(469.82, -1899.2) * mm});
            skLineSegment(sketch, "E2434", {"start": v(469.82, -1899.2) * mm, "end": v(469.82, -1890.24) * mm});
            skLineSegment(sketch, "E2435", {"start": v(435.92, -1868.75) * mm, "end": v(435.92, -1865.2) * mm});
            skLineSegment(sketch, "E2436", {"start": v(435.92, -1865.2) * mm, "end": v(469.82, -1865.2) * mm});
            skLineSegment(sketch, "E2437", {"start": v(469.82, -1865.2) * mm, "end": v(469.82, -1868.75) * mm});
            skLineSegment(sketch, "E2438", {"start": v(437.87, -1404) * mm, "end": v(437.87, -1399) * mm});
            skLineSegment(sketch, "E2439", {"start": v(411.37, -1412) * mm, "end": v(419.37, -1404) * mm});
            skLineSegment(sketch, "E2440", {"start": v(411.37, -1417.5) * mm, "end": v(411.37, -1412) * mm});
            skLineSegment(sketch, "E2441", {"start": v(411.37, -1417.5) * mm, "end": v(408.87, -1420) * mm});
            skLineSegment(sketch, "E2442", {"start": v(408.87, -1420.5) * mm, "end": v(405.37, -1424) * mm});
            skLineSegment(sketch, "E2443", {"start": v(408.87, -1420) * mm, "end": v(408.87, -1420.5) * mm});
            skLineSegment(sketch, "E2444", {"start": v(397.87, -1429.31) * mm, "end": v(397.87, -1424) * mm});
            skLineSegment(sketch, "E2445", {"start": v(407.87, -1432) * mm, "end": v(397.87, -1429.31) * mm});
            skLineSegment(sketch, "E2446", {"start": v(467.87, -1399) * mm, "end": v(467.87, -1404) * mm});
            skLineSegment(sketch, "E2447", {"start": v(397.87, -1429.31) * mm, "end": v(507.87, -1429.31) * mm});
            skLineSegment(sketch, "E2448", {"start": v(411.37, -1412) * mm, "end": v(494.37, -1412) * mm});
            skLineSegment(sketch, "E2449", {"start": v(419.37, -1404) * mm, "end": v(486.37, -1404) * mm});
            skLineSegment(sketch, "E2450", {"start": v(486.37, -1404) * mm, "end": v(494.37, -1412) * mm});
            skLineSegment(sketch, "E2451", {"start": v(494.37, -1412) * mm, "end": v(494.37, -1417.5) * mm});
            skLineSegment(sketch, "E2452", {"start": v(496.87, -1420) * mm, "end": v(494.37, -1417.5) * mm});
            skLineSegment(sketch, "E2453", {"start": v(500.37, -1424) * mm, "end": v(496.87, -1420.5) * mm});
            skLineSegment(sketch, "E2454", {"start": v(496.87, -1420.5) * mm, "end": v(496.87, -1420) * mm});
            skLineSegment(sketch, "E2455", {"start": v(497.87, -1432) * mm, "end": v(407.87, -1432) * mm});
            skLineSegment(sketch, "E2456", {"start": v(507.87, -1424) * mm, "end": v(397.87, -1424) * mm});
            skLineSegment(sketch, "E2457", {"start": v(507.87, -1424) * mm, "end": v(507.87, -1429.31) * mm});
            skLineSegment(sketch, "E2458", {"start": v(507.87, -1429.31) * mm, "end": v(497.87, -1432) * mm});
            skLineSegment(sketch, "E2459", {"start": v(491.47, -1398.05) * mm, "end": v(491.47, -1370.9) * mm});
            skLineSegment(sketch, "E2460", {"start": v(377.77, -1384.5) * mm, "end": v(527.96, -1384.5) * mm});
            skLineSegment(sketch, "E2461", {"start": v(505.37, -1396.39) * mm, "end": v(505.37, -1372.68) * mm});
            skLineSegment(sketch, "E2462", {"start": v(480.87, -1399.38) * mm, "end": v(480.87, -1400.1) * mm});
            skLineSegment(sketch, "E2463", {"start": v(484.27, -1403.5) * mm, "end": v(519.47, -1403.5) * mm});
            skLineSegment(sketch, "E2464", {"start": v(522.87, -1400.1) * mm, "end": v(522.87, -1368.9) * mm});
            skLineSegment(sketch, "E2465", {"start": v(519.47, -1365.5) * mm, "end": v(484.27, -1365.5) * mm});
            skLineSegment(sketch, "E2466", {"start": v(491.47, -1403.5) * mm, "end": v(472.57, -1396.17) * mm});
            skLineSegment(sketch, "E2467", {"start": v(466.88, -1394.92) * mm, "end": v(438.86, -1394.92) * mm});
            skLineSegment(sketch, "E2468", {"start": v(438.86, -1374.07) * mm, "end": v(466.88, -1374.07) * mm});
            skLineSegment(sketch, "E2469", {"start": v(472.57, -1372.82) * mm, "end": v(491.47, -1365.5) * mm});
            skLineSegment(sketch, "E2470", {"start": v(480.87, -1368.9) * mm, "end": v(480.87, -1369.6) * mm});
            skLineSegment(sketch, "E2471", {"start": v(414.27, -1370.9) * mm, "end": v(414.27, -1398.05) * mm});
            skLineSegment(sketch, "E2472", {"start": v(400.37, -1372.68) * mm, "end": v(400.37, -1396.39) * mm});
            skLineSegment(sketch, "E2473", {"start": v(424.87, -1400.1) * mm, "end": v(424.87, -1399.38) * mm});
            skLineSegment(sketch, "E2474", {"start": v(386.27, -1403.5) * mm, "end": v(421.47, -1403.5) * mm});
            skLineSegment(sketch, "E2475", {"start": v(382.87, -1368.9) * mm, "end": v(382.87, -1400.1) * mm});
            skLineSegment(sketch, "E2476", {"start": v(421.47, -1365.5) * mm, "end": v(386.27, -1365.5) * mm});
            skLineSegment(sketch, "E2477", {"start": v(424.87, -1369.6) * mm, "end": v(424.87, -1368.9) * mm});
            skLineSegment(sketch, "E2478", {"start": v(433.17, -1396.17) * mm, "end": v(414.27, -1403.5) * mm});
            skLineSegment(sketch, "E2479", {"start": v(414.27, -1365.5) * mm, "end": v(433.17, -1372.82) * mm});
            skLineSegment(sketch, "E2480", {"start": v(435.92, -1364.8) * mm, "end": v(435.92, -1373.75) * mm});
            skLineSegment(sketch, "E2481", {"start": v(469.82, -1373.75) * mm, "end": v(469.82, -1364.8) * mm});
            skLineSegment(sketch, "E2482", {"start": v(435.92, -1398.8) * mm, "end": v(435.92, -1395.24) * mm});
            skLineSegment(sketch, "E2483", {"start": v(469.82, -1398.8) * mm, "end": v(435.92, -1398.8) * mm});
            skLineSegment(sketch, "E2484", {"start": v(469.82, -1395.24) * mm, "end": v(469.82, -1398.8) * mm});
            skLineSegment(sketch, "E2485", {"start": v(1187.87, -1865) * mm, "end": v(1187.87, -1860) * mm});
            skLineSegment(sketch, "E2486", {"start": v(1169.37, -1860) * mm, "end": v(1161.37, -1852) * mm});
            skLineSegment(sketch, "E2487", {"start": v(1161.37, -1852) * mm, "end": v(1161.37, -1846.5) * mm});
            skLineSegment(sketch, "E2488", {"start": v(1158.87, -1844) * mm, "end": v(1161.37, -1846.5) * mm});
            skLineSegment(sketch, "E2489", {"start": v(1155.37, -1840) * mm, "end": v(1158.87, -1843.5) * mm});
            skLineSegment(sketch, "E2490", {"start": v(1158.87, -1843.5) * mm, "end": v(1158.87, -1844) * mm});
            skLineSegment(sketch, "E2491", {"start": v(1147.87, -1840) * mm, "end": v(1147.87, -1834.67) * mm});
            skLineSegment(sketch, "E2492", {"start": v(1147.87, -1834.67) * mm, "end": v(1157.87, -1832) * mm});
            skLineSegment(sketch, "E2493", {"start": v(1157.87, -1832) * mm, "end": v(1157.87, -1432) * mm});
            skLineSegment(sketch, "E2494", {"start": v(1217.87, -1860) * mm, "end": v(1217.87, -1865) * mm});
            skLineSegment(sketch, "E2495", {"start": v(1257.87, -1834.67) * mm, "end": v(1147.87, -1834.67) * mm});
            skLineSegment(sketch, "E2496", {"start": v(1244.37, -1852) * mm, "end": v(1161.37, -1852) * mm});
            skLineSegment(sketch, "E2497", {"start": v(1236.37, -1860) * mm, "end": v(1169.37, -1860) * mm});
            skLineSegment(sketch, "E2498", {"start": v(1244.37, -1852) * mm, "end": v(1236.37, -1860) * mm});
            skLineSegment(sketch, "E2499", {"start": v(1244.37, -1846.5) * mm, "end": v(1244.37, -1852) * mm});
            skLineSegment(sketch, "E2500", {"start": v(1244.37, -1846.5) * mm, "end": v(1246.87, -1844) * mm});
            skLineSegment(sketch, "E2501", {"start": v(1246.87, -1843.5) * mm, "end": v(1250.37, -1840) * mm});
            skLineSegment(sketch, "E2502", {"start": v(1246.87, -1844) * mm, "end": v(1246.87, -1843.5) * mm});
            skLineSegment(sketch, "E2503", {"start": v(1157.87, -1832) * mm, "end": v(1247.87, -1832) * mm});
            skLineSegment(sketch, "E2504", {"start": v(1147.87, -1840) * mm, "end": v(1257.87, -1840) * mm});
            skLineSegment(sketch, "E2505", {"start": v(1257.87, -1834.67) * mm, "end": v(1257.87, -1840) * mm});
            skLineSegment(sketch, "E2506", {"start": v(1247.87, -1832) * mm, "end": v(1257.87, -1834.67) * mm});
            skLineSegment(sketch, "E2507", {"start": v(1202.87, -1405.05) * mm, "end": v(1202.87, -1912.7) * mm});
            skLineSegment(sketch, "E2508", {"start": v(1247.87, -1432) * mm, "end": v(1247.87, -1832) * mm});
            skLineSegment(sketch, "E2509", {"start": v(1241.47, -1893.1) * mm, "end": v(1241.47, -1865.94) * mm});
            skLineSegment(sketch, "E2510", {"start": v(1277.96, -1879.5) * mm, "end": v(1127.77, -1879.5) * mm});
            skLineSegment(sketch, "E2511", {"start": v(1255.37, -1891.3) * mm, "end": v(1255.37, -1867.6) * mm});
            skLineSegment(sketch, "E2512", {"start": v(1230.87, -1863.9) * mm, "end": v(1230.87, -1864.6) * mm});
            skLineSegment(sketch, "E2513", {"start": v(1269.47, -1860.5) * mm, "end": v(1234.27, -1860.5) * mm});
            skLineSegment(sketch, "E2514", {"start": v(1272.87, -1895.1) * mm, "end": v(1272.87, -1863.9) * mm});
            skLineSegment(sketch, "E2515", {"start": v(1234.27, -1898.5) * mm, "end": v(1269.47, -1898.5) * mm});
            skLineSegment(sketch, "E2516", {"start": v(1188.86, -1869.07) * mm, "end": v(1216.88, -1869.07) * mm});
            skLineSegment(sketch, "E2517", {"start": v(1222.57, -1867.82) * mm, "end": v(1241.47, -1860.5) * mm});
            skLineSegment(sketch, "E2518", {"start": v(1216.88, -1889.92) * mm, "end": v(1188.86, -1889.92) * mm});
            skLineSegment(sketch, "E2519", {"start": v(1241.47, -1898.5) * mm, "end": v(1222.57, -1891.17) * mm});
            skLineSegment(sketch, "E2520", {"start": v(1230.87, -1894.38) * mm, "end": v(1230.87, -1895.1) * mm});
            skLineSegment(sketch, "E2521", {"start": v(1164.27, -1865.94) * mm, "end": v(1164.27, -1893.1) * mm});
            skLineSegment(sketch, "E2522", {"start": v(1150.37, -1867.6) * mm, "end": v(1150.37, -1891.3) * mm});
            skLineSegment(sketch, "E2523", {"start": v(1174.87, -1864.6) * mm, "end": v(1174.87, -1863.9) * mm});
            skLineSegment(sketch, "E2524", {"start": v(1171.47, -1860.5) * mm, "end": v(1136.27, -1860.5) * mm});
            skLineSegment(sketch, "E2525", {"start": v(1132.87, -1863.9) * mm, "end": v(1132.87, -1895.1) * mm});
            skLineSegment(sketch, "E2526", {"start": v(1136.27, -1898.5) * mm, "end": v(1171.47, -1898.5) * mm});
            skLineSegment(sketch, "E2527", {"start": v(1174.87, -1895.1) * mm, "end": v(1174.87, -1894.38) * mm});
            skLineSegment(sketch, "E2528", {"start": v(1164.27, -1860.5) * mm, "end": v(1183.17, -1867.82) * mm});
            skLineSegment(sketch, "E2529", {"start": v(1183.17, -1891.17) * mm, "end": v(1164.27, -1898.5) * mm});
            skLineSegment(sketch, "E2530", {"start": v(1185.92, -1890.24) * mm, "end": v(1185.92, -1899.2) * mm});
            skLineSegment(sketch, "E2531", {"start": v(1185.92, -1899.2) * mm, "end": v(1219.82, -1899.2) * mm});
            skLineSegment(sketch, "E2532", {"start": v(1219.82, -1899.2) * mm, "end": v(1219.82, -1890.24) * mm});
            skLineSegment(sketch, "E2533", {"start": v(1185.92, -1868.75) * mm, "end": v(1185.92, -1865.2) * mm});
            skLineSegment(sketch, "E2534", {"start": v(1185.92, -1865.2) * mm, "end": v(1219.82, -1865.2) * mm});
            skLineSegment(sketch, "E2535", {"start": v(1219.82, -1865.2) * mm, "end": v(1219.82, -1868.75) * mm});
            skLineSegment(sketch, "E2536", {"start": v(1187.87, -1404) * mm, "end": v(1187.87, -1399) * mm});
            skLineSegment(sketch, "E2537", {"start": v(1161.37, -1412) * mm, "end": v(1169.37, -1404) * mm});
            skLineSegment(sketch, "E2538", {"start": v(1161.37, -1417.5) * mm, "end": v(1161.37, -1412) * mm});
            skLineSegment(sketch, "E2539", {"start": v(1161.37, -1417.5) * mm, "end": v(1158.87, -1420) * mm});
            skLineSegment(sketch, "E2540", {"start": v(1158.87, -1420.5) * mm, "end": v(1155.37, -1424) * mm});
            skLineSegment(sketch, "E2541", {"start": v(1158.87, -1420) * mm, "end": v(1158.87, -1420.5) * mm});
            skLineSegment(sketch, "E2542", {"start": v(1147.87, -1429.31) * mm, "end": v(1147.87, -1424) * mm});
            skLineSegment(sketch, "E2543", {"start": v(1157.87, -1432) * mm, "end": v(1147.87, -1429.31) * mm});
            skLineSegment(sketch, "E2544", {"start": v(1217.87, -1399) * mm, "end": v(1217.87, -1404) * mm});
            skLineSegment(sketch, "E2545", {"start": v(1147.87, -1429.31) * mm, "end": v(1257.87, -1429.31) * mm});
            skLineSegment(sketch, "E2546", {"start": v(1161.37, -1412) * mm, "end": v(1244.37, -1412) * mm});
            skLineSegment(sketch, "E2547", {"start": v(1169.37, -1404) * mm, "end": v(1236.37, -1404) * mm});
            skLineSegment(sketch, "E2548", {"start": v(1236.37, -1404) * mm, "end": v(1244.37, -1412) * mm});
            skLineSegment(sketch, "E2549", {"start": v(1244.37, -1412) * mm, "end": v(1244.37, -1417.5) * mm});
            skLineSegment(sketch, "E2550", {"start": v(1246.87, -1420) * mm, "end": v(1244.37, -1417.5) * mm});
            skLineSegment(sketch, "E2551", {"start": v(1250.37, -1424) * mm, "end": v(1246.87, -1420.5) * mm});
            skLineSegment(sketch, "E2552", {"start": v(1246.87, -1420.5) * mm, "end": v(1246.87, -1420) * mm});
            skLineSegment(sketch, "E2553", {"start": v(1247.87, -1432) * mm, "end": v(1157.87, -1432) * mm});
            skLineSegment(sketch, "E2554", {"start": v(1257.87, -1424) * mm, "end": v(1147.87, -1424) * mm});
            skLineSegment(sketch, "E2555", {"start": v(1257.87, -1424) * mm, "end": v(1257.87, -1429.31) * mm});
            skLineSegment(sketch, "E2556", {"start": v(1257.87, -1429.31) * mm, "end": v(1247.87, -1432) * mm});
            skLineSegment(sketch, "E2557", {"start": v(1241.47, -1398.05) * mm, "end": v(1241.47, -1370.9) * mm});
            skLineSegment(sketch, "E2558", {"start": v(1127.77, -1384.5) * mm, "end": v(1277.96, -1384.5) * mm});
            skLineSegment(sketch, "E2559", {"start": v(1255.37, -1396.39) * mm, "end": v(1255.37, -1372.68) * mm});
            skLineSegment(sketch, "E2560", {"start": v(1230.87, -1399.38) * mm, "end": v(1230.87, -1400.1) * mm});
            skLineSegment(sketch, "E2561", {"start": v(1234.27, -1403.5) * mm, "end": v(1269.47, -1403.5) * mm});
            skLineSegment(sketch, "E2562", {"start": v(1272.87, -1400.1) * mm, "end": v(1272.87, -1368.9) * mm});
            skLineSegment(sketch, "E2563", {"start": v(1269.47, -1365.5) * mm, "end": v(1234.27, -1365.5) * mm});
            skLineSegment(sketch, "E2564", {"start": v(1202.87, -1357.24) * mm, "end": v(1202.87, -1409.98) * mm});
            skLineSegment(sketch, "E2565", {"start": v(1241.47, -1403.5) * mm, "end": v(1222.57, -1396.17) * mm});
            skLineSegment(sketch, "E2566", {"start": v(1216.88, -1394.92) * mm, "end": v(1188.86, -1394.92) * mm});
            skLineSegment(sketch, "E2567", {"start": v(1188.86, -1374.07) * mm, "end": v(1216.88, -1374.07) * mm});
            skLineSegment(sketch, "E2568", {"start": v(1222.57, -1372.82) * mm, "end": v(1241.47, -1365.5) * mm});
            skLineSegment(sketch, "E2569", {"start": v(1230.87, -1368.9) * mm, "end": v(1230.87, -1369.6) * mm});
            skLineSegment(sketch, "E2570", {"start": v(1164.27, -1370.9) * mm, "end": v(1164.27, -1398.05) * mm});
            skLineSegment(sketch, "E2571", {"start": v(1150.37, -1372.68) * mm, "end": v(1150.37, -1396.39) * mm});
            skLineSegment(sketch, "E2572", {"start": v(1174.87, -1400.1) * mm, "end": v(1174.87, -1399.38) * mm});
            skLineSegment(sketch, "E2573", {"start": v(1136.27, -1403.5) * mm, "end": v(1171.47, -1403.5) * mm});
            skLineSegment(sketch, "E2574", {"start": v(1132.87, -1368.9) * mm, "end": v(1132.87, -1400.1) * mm});
            skLineSegment(sketch, "E2575", {"start": v(1171.47, -1365.5) * mm, "end": v(1136.27, -1365.5) * mm});
            skLineSegment(sketch, "E2576", {"start": v(1174.87, -1369.6) * mm, "end": v(1174.87, -1368.9) * mm});
            skLineSegment(sketch, "E2577", {"start": v(1183.17, -1396.17) * mm, "end": v(1164.27, -1403.5) * mm});
            skLineSegment(sketch, "E2578", {"start": v(1164.27, -1365.5) * mm, "end": v(1183.17, -1372.82) * mm});
            skLineSegment(sketch, "E2579", {"start": v(1185.92, -1364.8) * mm, "end": v(1185.92, -1373.75) * mm});
            skLineSegment(sketch, "E2580", {"start": v(1219.82, -1364.8) * mm, "end": v(1185.92, -1364.8) * mm});
            skLineSegment(sketch, "E2581", {"start": v(1219.82, -1373.75) * mm, "end": v(1219.82, -1364.8) * mm});
            skLineSegment(sketch, "E2582", {"start": v(1185.92, -1398.8) * mm, "end": v(1185.92, -1395.24) * mm});
            skLineSegment(sketch, "E2583", {"start": v(1219.82, -1398.8) * mm, "end": v(1185.92, -1398.8) * mm});
            skLineSegment(sketch, "E2584", {"start": v(1219.82, -1395.24) * mm, "end": v(1219.82, -1398.8) * mm});
            skLineSegment(sketch, "E2585", {"start": v(1937.87, -1865) * mm, "end": v(1937.87, -1860) * mm});
            skLineSegment(sketch, "E2586", {"start": v(1919.37, -1860) * mm, "end": v(1911.37, -1852) * mm});
            skLineSegment(sketch, "E2587", {"start": v(1911.37, -1852) * mm, "end": v(1911.37, -1846.5) * mm});
            skLineSegment(sketch, "E2588", {"start": v(1908.87, -1844) * mm, "end": v(1911.37, -1846.5) * mm});
            skLineSegment(sketch, "E2589", {"start": v(1905.37, -1840) * mm, "end": v(1908.87, -1843.5) * mm});
            skLineSegment(sketch, "E2590", {"start": v(1908.87, -1843.5) * mm, "end": v(1908.87, -1844) * mm});
            skLineSegment(sketch, "E2591", {"start": v(1897.87, -1840) * mm, "end": v(1897.87, -1834.67) * mm});
            skLineSegment(sketch, "E2592", {"start": v(1897.87, -1834.67) * mm, "end": v(1907.87, -1832) * mm});
            skLineSegment(sketch, "E2593", {"start": v(1907.87, -1832) * mm, "end": v(1907.87, -1432) * mm});
            skLineSegment(sketch, "E2594", {"start": v(1967.87, -1860) * mm, "end": v(1967.87, -1865) * mm});
            skLineSegment(sketch, "E2595", {"start": v(2007.87, -1834.67) * mm, "end": v(1897.87, -1834.67) * mm});
            skLineSegment(sketch, "E2596", {"start": v(1994.37, -1852) * mm, "end": v(1911.37, -1852) * mm});
            skLineSegment(sketch, "E2597", {"start": v(1986.37, -1860) * mm, "end": v(1919.37, -1860) * mm});
            skLineSegment(sketch, "E2598", {"start": v(1994.37, -1852) * mm, "end": v(1986.37, -1860) * mm});
            skLineSegment(sketch, "E2599", {"start": v(1994.37, -1846.5) * mm, "end": v(1994.37, -1852) * mm});
            skLineSegment(sketch, "E2600", {"start": v(1994.37, -1846.5) * mm, "end": v(1996.87, -1844) * mm});
            skLineSegment(sketch, "E2601", {"start": v(1996.87, -1843.5) * mm, "end": v(2000.37, -1840) * mm});
            skLineSegment(sketch, "E2602", {"start": v(1996.87, -1844) * mm, "end": v(1996.87, -1843.5) * mm});
            skLineSegment(sketch, "E2603", {"start": v(1907.87, -1832) * mm, "end": v(1997.87, -1832) * mm});
            skLineSegment(sketch, "E2604", {"start": v(1897.87, -1840) * mm, "end": v(2007.87, -1840) * mm});
            skLineSegment(sketch, "E2605", {"start": v(2007.87, -1834.67) * mm, "end": v(2007.87, -1840) * mm});
            skLineSegment(sketch, "E2606", {"start": v(1997.87, -1832) * mm, "end": v(2007.87, -1834.67) * mm});
            skLineSegment(sketch, "E2607", {"start": v(1952.87, -1405.05) * mm, "end": v(1952.87, -1912.7) * mm});
            skLineSegment(sketch, "E2608", {"start": v(1997.87, -1432) * mm, "end": v(1997.87, -1832) * mm});
            skLineSegment(sketch, "E2609", {"start": v(1991.47, -1893.1) * mm, "end": v(1991.47, -1865.94) * mm});
            skLineSegment(sketch, "E2610", {"start": v(2027.96, -1879.5) * mm, "end": v(1877.77, -1879.5) * mm});
            skLineSegment(sketch, "E2611", {"start": v(2005.37, -1891.3) * mm, "end": v(2005.37, -1867.6) * mm});
            skLineSegment(sketch, "E2612", {"start": v(1980.87, -1863.9) * mm, "end": v(1980.87, -1864.6) * mm});
            skLineSegment(sketch, "E2613", {"start": v(2019.47, -1860.5) * mm, "end": v(1984.27, -1860.5) * mm});
            skLineSegment(sketch, "E2614", {"start": v(2022.87, -1895.1) * mm, "end": v(2022.87, -1863.9) * mm});
            skLineSegment(sketch, "E2615", {"start": v(1984.27, -1898.5) * mm, "end": v(2019.47, -1898.5) * mm});
            skLineSegment(sketch, "E2616", {"start": v(1972.57, -1867.82) * mm, "end": v(1991.47, -1860.5) * mm});
            skLineSegment(sketch, "E2617", {"start": v(1938.86, -1869.07) * mm, "end": v(1966.88, -1869.07) * mm});
            skLineSegment(sketch, "E2618", {"start": v(1966.88, -1889.92) * mm, "end": v(1938.86, -1889.92) * mm});
            skLineSegment(sketch, "E2619", {"start": v(1991.47, -1898.5) * mm, "end": v(1972.57, -1891.17) * mm});
            skLineSegment(sketch, "E2620", {"start": v(1980.87, -1894.38) * mm, "end": v(1980.87, -1895.1) * mm});
            skLineSegment(sketch, "E2621", {"start": v(1914.27, -1865.94) * mm, "end": v(1914.27, -1893.1) * mm});
            skLineSegment(sketch, "E2622", {"start": v(1900.37, -1867.6) * mm, "end": v(1900.37, -1891.3) * mm});
            skLineSegment(sketch, "E2623", {"start": v(1924.87, -1864.6) * mm, "end": v(1924.87, -1863.9) * mm});
            skLineSegment(sketch, "E2624", {"start": v(1921.47, -1860.5) * mm, "end": v(1886.27, -1860.5) * mm});
            skLineSegment(sketch, "E2625", {"start": v(1882.87, -1863.9) * mm, "end": v(1882.87, -1895.1) * mm});
            skLineSegment(sketch, "E2626", {"start": v(1886.27, -1898.5) * mm, "end": v(1921.47, -1898.5) * mm});
            skLineSegment(sketch, "E2627", {"start": v(1924.87, -1895.1) * mm, "end": v(1924.87, -1894.38) * mm});
            skLineSegment(sketch, "E2628", {"start": v(1914.27, -1860.5) * mm, "end": v(1933.17, -1867.82) * mm});
            skLineSegment(sketch, "E2629", {"start": v(1933.17, -1891.17) * mm, "end": v(1914.27, -1898.5) * mm});
            skLineSegment(sketch, "E2630", {"start": v(1935.92, -1890.24) * mm, "end": v(1935.92, -1899.2) * mm});
            skLineSegment(sketch, "E2631", {"start": v(1935.92, -1899.2) * mm, "end": v(1969.82, -1899.2) * mm});
            skLineSegment(sketch, "E2632", {"start": v(1969.82, -1899.2) * mm, "end": v(1969.82, -1890.24) * mm});
            skLineSegment(sketch, "E2633", {"start": v(1935.92, -1868.75) * mm, "end": v(1935.92, -1865.2) * mm});
            skLineSegment(sketch, "E2634", {"start": v(1935.92, -1865.2) * mm, "end": v(1969.82, -1865.2) * mm});
            skLineSegment(sketch, "E2635", {"start": v(1969.82, -1865.2) * mm, "end": v(1969.82, -1868.75) * mm});
            skLineSegment(sketch, "E2636", {"start": v(1952.87, -1409.98) * mm, "end": v(1952.87, -1357.24) * mm});
            skLineSegment(sketch, "E2637", {"start": v(1937.87, -1404) * mm, "end": v(1937.87, -1399) * mm});
            skLineSegment(sketch, "E2638", {"start": v(1911.37, -1412) * mm, "end": v(1919.37, -1404) * mm});
            skLineSegment(sketch, "E2639", {"start": v(1911.37, -1417.5) * mm, "end": v(1911.37, -1412) * mm});
            skLineSegment(sketch, "E2640", {"start": v(1911.37, -1417.5) * mm, "end": v(1908.87, -1420) * mm});
            skLineSegment(sketch, "E2641", {"start": v(1908.87, -1420.5) * mm, "end": v(1905.37, -1424) * mm});
            skLineSegment(sketch, "E2642", {"start": v(1908.87, -1420) * mm, "end": v(1908.87, -1420.5) * mm});
            skLineSegment(sketch, "E2643", {"start": v(1897.87, -1429.31) * mm, "end": v(1897.87, -1424) * mm});
            skLineSegment(sketch, "E2644", {"start": v(1907.87, -1432) * mm, "end": v(1897.87, -1429.31) * mm});
            skLineSegment(sketch, "E2645", {"start": v(1967.87, -1399) * mm, "end": v(1967.87, -1404) * mm});
            skLineSegment(sketch, "E2646", {"start": v(1897.87, -1429.31) * mm, "end": v(2007.87, -1429.31) * mm});
            skLineSegment(sketch, "E2647", {"start": v(1911.37, -1412) * mm, "end": v(1994.37, -1412) * mm});
            skLineSegment(sketch, "E2648", {"start": v(1919.37, -1404) * mm, "end": v(1986.37, -1404) * mm});
            skLineSegment(sketch, "E2649", {"start": v(1986.37, -1404) * mm, "end": v(1994.37, -1412) * mm});
            skLineSegment(sketch, "E2650", {"start": v(1994.37, -1412) * mm, "end": v(1994.37, -1417.5) * mm});
            skLineSegment(sketch, "E2651", {"start": v(1996.87, -1420) * mm, "end": v(1994.37, -1417.5) * mm});
            skLineSegment(sketch, "E2652", {"start": v(2000.37, -1424) * mm, "end": v(1996.87, -1420.5) * mm});
            skLineSegment(sketch, "E2653", {"start": v(1996.87, -1420.5) * mm, "end": v(1996.87, -1420) * mm});
            skLineSegment(sketch, "E2654", {"start": v(1997.87, -1432) * mm, "end": v(1907.87, -1432) * mm});
            skLineSegment(sketch, "E2655", {"start": v(2007.87, -1424) * mm, "end": v(1897.87, -1424) * mm});
            skLineSegment(sketch, "E2656", {"start": v(2007.87, -1424) * mm, "end": v(2007.87, -1429.31) * mm});
            skLineSegment(sketch, "E2657", {"start": v(2007.87, -1429.31) * mm, "end": v(1997.87, -1432) * mm});
            skLineSegment(sketch, "E2658", {"start": v(1991.47, -1398.05) * mm, "end": v(1991.47, -1370.9) * mm});
            skLineSegment(sketch, "E2659", {"start": v(1877.77, -1384.5) * mm, "end": v(2027.96, -1384.5) * mm});
            skLineSegment(sketch, "E2660", {"start": v(2005.37, -1396.39) * mm, "end": v(2005.37, -1372.68) * mm});
            skLineSegment(sketch, "E2661", {"start": v(1980.87, -1399.38) * mm, "end": v(1980.87, -1400.1) * mm});
            skLineSegment(sketch, "E2662", {"start": v(1984.27, -1403.5) * mm, "end": v(2019.47, -1403.5) * mm});
            skLineSegment(sketch, "E2663", {"start": v(2022.87, -1400.1) * mm, "end": v(2022.87, -1368.9) * mm});
            skLineSegment(sketch, "E2664", {"start": v(2019.47, -1365.5) * mm, "end": v(1984.27, -1365.5) * mm});
            skLineSegment(sketch, "E2665", {"start": v(1966.88, -1394.92) * mm, "end": v(1938.86, -1394.92) * mm});
            skLineSegment(sketch, "E2666", {"start": v(1991.47, -1403.5) * mm, "end": v(1972.57, -1396.17) * mm});
            skLineSegment(sketch, "E2667", {"start": v(1938.86, -1374.07) * mm, "end": v(1966.88, -1374.07) * mm});
            skLineSegment(sketch, "E2668", {"start": v(1972.57, -1372.82) * mm, "end": v(1991.47, -1365.5) * mm});
            skLineSegment(sketch, "E2669", {"start": v(1980.87, -1368.9) * mm, "end": v(1980.87, -1369.6) * mm});
            skLineSegment(sketch, "E2670", {"start": v(1914.27, -1370.9) * mm, "end": v(1914.27, -1398.05) * mm});
            skLineSegment(sketch, "E2671", {"start": v(1900.37, -1372.68) * mm, "end": v(1900.37, -1396.39) * mm});
            skLineSegment(sketch, "E2672", {"start": v(1924.87, -1400.1) * mm, "end": v(1924.87, -1399.38) * mm});
            skLineSegment(sketch, "E2673", {"start": v(1886.27, -1403.5) * mm, "end": v(1921.47, -1403.5) * mm});
            skLineSegment(sketch, "E2674", {"start": v(1882.87, -1368.9) * mm, "end": v(1882.87, -1400.1) * mm});
            skLineSegment(sketch, "E2675", {"start": v(1921.47, -1365.5) * mm, "end": v(1886.27, -1365.5) * mm});
            skLineSegment(sketch, "E2676", {"start": v(1924.87, -1369.6) * mm, "end": v(1924.87, -1368.9) * mm});
            skLineSegment(sketch, "E2677", {"start": v(1933.17, -1396.17) * mm, "end": v(1914.27, -1403.5) * mm});
            skLineSegment(sketch, "E2678", {"start": v(1914.27, -1365.5) * mm, "end": v(1933.17, -1372.82) * mm});
            skLineSegment(sketch, "E2679", {"start": v(1935.92, -1364.8) * mm, "end": v(1935.92, -1373.75) * mm});
            skLineSegment(sketch, "E2680", {"start": v(1969.82, -1364.8) * mm, "end": v(1935.92, -1364.8) * mm});
            skLineSegment(sketch, "E2681", {"start": v(1969.82, -1373.75) * mm, "end": v(1969.82, -1364.8) * mm});
            skLineSegment(sketch, "E2682", {"start": v(1935.92, -1398.8) * mm, "end": v(1935.92, -1395.24) * mm});
            skLineSegment(sketch, "E2683", {"start": v(1969.82, -1398.8) * mm, "end": v(1935.92, -1398.8) * mm});
            skLineSegment(sketch, "E2684", {"start": v(1969.82, -1395.24) * mm, "end": v(1969.82, -1398.8) * mm});
            skLineSegment(sketch, "E2685", {"start": v(2687.87, -1865) * mm, "end": v(2687.87, -1860) * mm});
            skLineSegment(sketch, "E2686", {"start": v(2669.37, -1860) * mm, "end": v(2661.37, -1852) * mm});
            skLineSegment(sketch, "E2687", {"start": v(2661.37, -1852) * mm, "end": v(2661.37, -1846.5) * mm});
            skLineSegment(sketch, "E2688", {"start": v(2658.87, -1844) * mm, "end": v(2661.37, -1846.5) * mm});
            skLineSegment(sketch, "E2689", {"start": v(2655.37, -1840) * mm, "end": v(2658.87, -1843.5) * mm});
            skLineSegment(sketch, "E2690", {"start": v(2658.87, -1843.5) * mm, "end": v(2658.87, -1844) * mm});
            skLineSegment(sketch, "E2691", {"start": v(2647.87, -1840) * mm, "end": v(2647.87, -1834.67) * mm});
            skLineSegment(sketch, "E2692", {"start": v(2647.87, -1834.67) * mm, "end": v(2657.87, -1832) * mm});
            skLineSegment(sketch, "E2693", {"start": v(2657.87, -1832) * mm, "end": v(2657.87, -1432) * mm});
            skLineSegment(sketch, "E2694", {"start": v(2717.87, -1860) * mm, "end": v(2717.87, -1865) * mm});
            skLineSegment(sketch, "E2695", {"start": v(2757.87, -1834.67) * mm, "end": v(2647.87, -1834.67) * mm});
            skLineSegment(sketch, "E2696", {"start": v(2744.37, -1852) * mm, "end": v(2661.37, -1852) * mm});
            skLineSegment(sketch, "E2697", {"start": v(2736.37, -1860) * mm, "end": v(2669.37, -1860) * mm});
            skLineSegment(sketch, "E2698", {"start": v(2744.37, -1852) * mm, "end": v(2736.37, -1860) * mm});
            skLineSegment(sketch, "E2699", {"start": v(2744.37, -1846.5) * mm, "end": v(2744.37, -1852) * mm});
            skLineSegment(sketch, "E2700", {"start": v(2744.37, -1846.5) * mm, "end": v(2746.87, -1844) * mm});
            skLineSegment(sketch, "E2701", {"start": v(2746.87, -1843.5) * mm, "end": v(2750.37, -1840) * mm});
            skLineSegment(sketch, "E2702", {"start": v(2746.87, -1844) * mm, "end": v(2746.87, -1843.5) * mm});
            skLineSegment(sketch, "E2703", {"start": v(2657.87, -1832) * mm, "end": v(2747.87, -1832) * mm});
            skLineSegment(sketch, "E2704", {"start": v(2647.87, -1840) * mm, "end": v(2757.87, -1840) * mm});
            skLineSegment(sketch, "E2705", {"start": v(2757.87, -1834.67) * mm, "end": v(2757.87, -1840) * mm});
            skLineSegment(sketch, "E2706", {"start": v(2747.87, -1832) * mm, "end": v(2757.87, -1834.67) * mm});
            skLineSegment(sketch, "E2707", {"start": v(2702.87, -1405.05) * mm, "end": v(2702.87, -1864) * mm});
            skLineSegment(sketch, "E2708", {"start": v(2747.87, -1432) * mm, "end": v(2747.87, -1832) * mm});
            skLineSegment(sketch, "E2709", {"start": v(2741.47, -1893.1) * mm, "end": v(2741.47, -1865.94) * mm});
            skLineSegment(sketch, "E2710", {"start": v(2777.96, -1879.5) * mm, "end": v(2627.77, -1879.5) * mm});
            skLineSegment(sketch, "E2711", {"start": v(2755.37, -1891.3) * mm, "end": v(2755.37, -1867.6) * mm});
            skLineSegment(sketch, "E2712", {"start": v(2730.87, -1863.9) * mm, "end": v(2730.87, -1864.6) * mm});
            skLineSegment(sketch, "E2713", {"start": v(2769.47, -1860.5) * mm, "end": v(2734.27, -1860.5) * mm});
            skLineSegment(sketch, "E2714", {"start": v(2772.87, -1895.1) * mm, "end": v(2772.87, -1863.9) * mm});
            skLineSegment(sketch, "E2715", {"start": v(2734.27, -1898.5) * mm, "end": v(2769.47, -1898.5) * mm});
            skLineSegment(sketch, "E2716", {"start": v(2702.87, -1906.75) * mm, "end": v(2702.87, -1864) * mm});
            skLineSegment(sketch, "E2717", {"start": v(2688.86, -1869.07) * mm, "end": v(2716.88, -1869.07) * mm});
            skLineSegment(sketch, "E2718", {"start": v(2722.57, -1867.82) * mm, "end": v(2741.47, -1860.5) * mm});
            skLineSegment(sketch, "E2719", {"start": v(2716.88, -1889.92) * mm, "end": v(2688.86, -1889.92) * mm});
            skLineSegment(sketch, "E2720", {"start": v(2741.47, -1898.5) * mm, "end": v(2722.57, -1891.17) * mm});
            skLineSegment(sketch, "E2721", {"start": v(2730.87, -1894.38) * mm, "end": v(2730.87, -1895.1) * mm});
            skLineSegment(sketch, "E2722", {"start": v(2664.27, -1865.94) * mm, "end": v(2664.27, -1893.1) * mm});
            skLineSegment(sketch, "E2723", {"start": v(2650.37, -1867.6) * mm, "end": v(2650.37, -1891.3) * mm});
            skLineSegment(sketch, "E2724", {"start": v(2674.87, -1864.6) * mm, "end": v(2674.87, -1863.9) * mm});
            skLineSegment(sketch, "E2725", {"start": v(2671.47, -1860.5) * mm, "end": v(2636.27, -1860.5) * mm});
            skLineSegment(sketch, "E2726", {"start": v(2632.87, -1863.9) * mm, "end": v(2632.87, -1895.1) * mm});
            skLineSegment(sketch, "E2727", {"start": v(2636.27, -1898.5) * mm, "end": v(2671.47, -1898.5) * mm});
            skLineSegment(sketch, "E2728", {"start": v(2674.87, -1895.1) * mm, "end": v(2674.87, -1894.38) * mm});
            skLineSegment(sketch, "E2729", {"start": v(2664.27, -1860.5) * mm, "end": v(2683.17, -1867.82) * mm});
            skLineSegment(sketch, "E2730", {"start": v(2683.17, -1891.17) * mm, "end": v(2664.27, -1898.5) * mm});
            skLineSegment(sketch, "E2731", {"start": v(2685.92, -1890.24) * mm, "end": v(2685.92, -1899.2) * mm});
            skLineSegment(sketch, "E2732", {"start": v(2685.92, -1899.2) * mm, "end": v(2719.82, -1899.2) * mm});
            skLineSegment(sketch, "E2733", {"start": v(2719.82, -1899.2) * mm, "end": v(2719.82, -1890.24) * mm});
            skLineSegment(sketch, "E2734", {"start": v(2685.92, -1868.75) * mm, "end": v(2685.92, -1865.2) * mm});
            skLineSegment(sketch, "E2735", {"start": v(2685.92, -1865.2) * mm, "end": v(2719.82, -1865.2) * mm});
            skLineSegment(sketch, "E2736", {"start": v(2719.82, -1865.2) * mm, "end": v(2719.82, -1868.75) * mm});
            skLineSegment(sketch, "E2737", {"start": v(2687.87, -1404) * mm, "end": v(2687.87, -1399) * mm});
            skLineSegment(sketch, "E2738", {"start": v(2661.37, -1412) * mm, "end": v(2669.37, -1404) * mm});
            skLineSegment(sketch, "E2739", {"start": v(2661.37, -1417.5) * mm, "end": v(2661.37, -1412) * mm});
            skLineSegment(sketch, "E2740", {"start": v(2661.37, -1417.5) * mm, "end": v(2658.87, -1420) * mm});
            skLineSegment(sketch, "E2741", {"start": v(2658.87, -1420.5) * mm, "end": v(2655.37, -1424) * mm});
            skLineSegment(sketch, "E2742", {"start": v(2658.87, -1420) * mm, "end": v(2658.87, -1420.5) * mm});
            skLineSegment(sketch, "E2743", {"start": v(2647.87, -1429.31) * mm, "end": v(2647.87, -1424) * mm});
            skLineSegment(sketch, "E2744", {"start": v(2657.87, -1432) * mm, "end": v(2647.87, -1429.31) * mm});
            skLineSegment(sketch, "E2745", {"start": v(2717.87, -1399) * mm, "end": v(2717.87, -1404) * mm});
            skLineSegment(sketch, "E2746", {"start": v(2647.87, -1429.31) * mm, "end": v(2757.87, -1429.31) * mm});
            skLineSegment(sketch, "E2747", {"start": v(2661.37, -1412) * mm, "end": v(2744.37, -1412) * mm});
            skLineSegment(sketch, "E2748", {"start": v(2669.37, -1404) * mm, "end": v(2736.37, -1404) * mm});
            skLineSegment(sketch, "E2749", {"start": v(2736.37, -1404) * mm, "end": v(2744.37, -1412) * mm});
            skLineSegment(sketch, "E2750", {"start": v(2744.37, -1412) * mm, "end": v(2744.37, -1417.5) * mm});
            skLineSegment(sketch, "E2751", {"start": v(2746.87, -1420) * mm, "end": v(2744.37, -1417.5) * mm});
            skLineSegment(sketch, "E2752", {"start": v(2750.37, -1424) * mm, "end": v(2746.87, -1420.5) * mm});
            skLineSegment(sketch, "E2753", {"start": v(2746.87, -1420.5) * mm, "end": v(2746.87, -1420) * mm});
            skLineSegment(sketch, "E2754", {"start": v(2747.87, -1432) * mm, "end": v(2657.87, -1432) * mm});
            skLineSegment(sketch, "E2755", {"start": v(2757.87, -1424) * mm, "end": v(2647.87, -1424) * mm});
            skLineSegment(sketch, "E2756", {"start": v(2757.87, -1424) * mm, "end": v(2757.87, -1429.31) * mm});
            skLineSegment(sketch, "E2757", {"start": v(2757.87, -1429.31) * mm, "end": v(2747.87, -1432) * mm});
            skLineSegment(sketch, "E2758", {"start": v(2741.47, -1398.05) * mm, "end": v(2741.47, -1370.9) * mm});
            skLineSegment(sketch, "E2759", {"start": v(2627.77, -1384.5) * mm, "end": v(2777.96, -1384.5) * mm});
            skLineSegment(sketch, "E2760", {"start": v(2755.37, -1396.39) * mm, "end": v(2755.37, -1372.68) * mm});
            skLineSegment(sketch, "E2761", {"start": v(2730.87, -1399.38) * mm, "end": v(2730.87, -1400.1) * mm});
            skLineSegment(sketch, "E2762", {"start": v(2734.27, -1403.5) * mm, "end": v(2769.47, -1403.5) * mm});
            skLineSegment(sketch, "E2763", {"start": v(2772.87, -1400.1) * mm, "end": v(2772.87, -1368.9) * mm});
            skLineSegment(sketch, "E2764", {"start": v(2769.47, -1365.5) * mm, "end": v(2734.27, -1365.5) * mm});
            skLineSegment(sketch, "E2765", {"start": v(2741.47, -1403.5) * mm, "end": v(2722.57, -1396.17) * mm});
            skLineSegment(sketch, "E2766", {"start": v(2716.88, -1394.92) * mm, "end": v(2688.86, -1394.92) * mm});
            skLineSegment(sketch, "E2767", {"start": v(2688.86, -1374.07) * mm, "end": v(2716.88, -1374.07) * mm});
            skLineSegment(sketch, "E2768", {"start": v(2722.57, -1372.82) * mm, "end": v(2741.47, -1365.5) * mm});
            skLineSegment(sketch, "E2769", {"start": v(2730.87, -1368.9) * mm, "end": v(2730.87, -1369.6) * mm});
            skLineSegment(sketch, "E2770", {"start": v(2664.27, -1370.9) * mm, "end": v(2664.27, -1398.05) * mm});
            skLineSegment(sketch, "E2771", {"start": v(2650.37, -1372.68) * mm, "end": v(2650.37, -1396.39) * mm});
            skLineSegment(sketch, "E2772", {"start": v(2674.87, -1400.1) * mm, "end": v(2674.87, -1399.38) * mm});
            skLineSegment(sketch, "E2773", {"start": v(2636.27, -1403.5) * mm, "end": v(2671.47, -1403.5) * mm});
            skLineSegment(sketch, "E2774", {"start": v(2632.87, -1368.9) * mm, "end": v(2632.87, -1400.1) * mm});
            skLineSegment(sketch, "E2775", {"start": v(2671.47, -1365.5) * mm, "end": v(2636.27, -1365.5) * mm});
            skLineSegment(sketch, "E2776", {"start": v(2674.87, -1369.6) * mm, "end": v(2674.87, -1368.9) * mm});
            skLineSegment(sketch, "E2777", {"start": v(2683.17, -1396.17) * mm, "end": v(2664.27, -1403.5) * mm});
            skLineSegment(sketch, "E2778", {"start": v(2664.27, -1365.5) * mm, "end": v(2683.17, -1372.82) * mm});
            skLineSegment(sketch, "E2779", {"start": v(2685.92, -1364.8) * mm, "end": v(2685.92, -1373.75) * mm});
            skLineSegment(sketch, "E2780", {"start": v(2719.82, -1364.8) * mm, "end": v(2685.92, -1364.8) * mm});
            skLineSegment(sketch, "E2781", {"start": v(2719.82, -1373.75) * mm, "end": v(2719.82, -1364.8) * mm});
            skLineSegment(sketch, "E2782", {"start": v(2685.92, -1398.8) * mm, "end": v(2685.92, -1395.24) * mm});
            skLineSegment(sketch, "E2783", {"start": v(2719.82, -1398.8) * mm, "end": v(2685.92, -1398.8) * mm});
            skLineSegment(sketch, "E2784", {"start": v(2719.82, -1395.24) * mm, "end": v(2719.82, -1398.8) * mm});
            skLineSegment(sketch, "E2785", {"start": v(3437.87, -1865) * mm, "end": v(3437.87, -1860) * mm});
            skLineSegment(sketch, "E2786", {"start": v(3419.37, -1860) * mm, "end": v(3411.37, -1852) * mm});
            skLineSegment(sketch, "E2787", {"start": v(3411.37, -1852) * mm, "end": v(3411.37, -1846.5) * mm});
            skLineSegment(sketch, "E2788", {"start": v(3408.87, -1844) * mm, "end": v(3411.37, -1846.5) * mm});
            skLineSegment(sketch, "E2789", {"start": v(3405.37, -1840) * mm, "end": v(3408.87, -1843.5) * mm});
            skLineSegment(sketch, "E2790", {"start": v(3408.87, -1843.5) * mm, "end": v(3408.87, -1844) * mm});
            skLineSegment(sketch, "E2791", {"start": v(3397.87, -1840) * mm, "end": v(3397.87, -1834.67) * mm});
            skLineSegment(sketch, "E2792", {"start": v(3397.87, -1834.67) * mm, "end": v(3407.87, -1832) * mm});
            skLineSegment(sketch, "E2793", {"start": v(3407.87, -1832) * mm, "end": v(3407.87, -1432) * mm});
            skLineSegment(sketch, "E2794", {"start": v(3467.87, -1860) * mm, "end": v(3467.87, -1865) * mm});
            skLineSegment(sketch, "E2795", {"start": v(3507.87, -1834.67) * mm, "end": v(3397.87, -1834.67) * mm});
            skLineSegment(sketch, "E2796", {"start": v(3494.37, -1852) * mm, "end": v(3411.37, -1852) * mm});
            skLineSegment(sketch, "E2797", {"start": v(3486.37, -1860) * mm, "end": v(3419.37, -1860) * mm});
            skLineSegment(sketch, "E2798", {"start": v(3494.37, -1852) * mm, "end": v(3486.37, -1860) * mm});
            skLineSegment(sketch, "E2799", {"start": v(3494.37, -1846.5) * mm, "end": v(3494.37, -1852) * mm});
            skLineSegment(sketch, "E2800", {"start": v(3494.37, -1846.5) * mm, "end": v(3496.87, -1844) * mm});
            skLineSegment(sketch, "E2801", {"start": v(3496.87, -1843.5) * mm, "end": v(3500.37, -1840) * mm});
            skLineSegment(sketch, "E2802", {"start": v(3496.87, -1844) * mm, "end": v(3496.87, -1843.5) * mm});
            skLineSegment(sketch, "E2803", {"start": v(3407.87, -1832) * mm, "end": v(3497.87, -1832) * mm});
            skLineSegment(sketch, "E2804", {"start": v(3397.87, -1840) * mm, "end": v(3507.87, -1840) * mm});
            skLineSegment(sketch, "E2805", {"start": v(3507.87, -1834.67) * mm, "end": v(3507.87, -1840) * mm});
            skLineSegment(sketch, "E2806", {"start": v(3497.87, -1832) * mm, "end": v(3507.87, -1834.67) * mm});
            skLineSegment(sketch, "E2807", {"start": v(3452.87, -1405.05) * mm, "end": v(3452.87, -1854) * mm});
            skLineSegment(sketch, "E2808", {"start": v(3497.87, -1432) * mm, "end": v(3497.87, -1832) * mm});
            skLineSegment(sketch, "E2809", {"start": v(3491.47, -1893.1) * mm, "end": v(3491.47, -1865.94) * mm});
            skLineSegment(sketch, "E2810", {"start": v(3527.96, -1879.5) * mm, "end": v(3377.77, -1879.5) * mm});
            skLineSegment(sketch, "E2811", {"start": v(3505.37, -1891.3) * mm, "end": v(3505.37, -1867.6) * mm});
            skLineSegment(sketch, "E2812", {"start": v(3480.87, -1863.9) * mm, "end": v(3480.87, -1864.6) * mm});
            skLineSegment(sketch, "E2813", {"start": v(3519.47, -1860.5) * mm, "end": v(3484.27, -1860.5) * mm});
            skLineSegment(sketch, "E2814", {"start": v(3522.87, -1895.1) * mm, "end": v(3522.87, -1863.9) * mm});
            skLineSegment(sketch, "E2815", {"start": v(3484.27, -1898.5) * mm, "end": v(3519.47, -1898.5) * mm});
            skLineSegment(sketch, "E2816", {"start": v(3452.87, -1906.75) * mm, "end": v(3452.87, -1854) * mm});
            skLineSegment(sketch, "E2817", {"start": v(3472.57, -1867.82) * mm, "end": v(3491.47, -1860.5) * mm});
            skLineSegment(sketch, "E2818", {"start": v(3438.86, -1869.07) * mm, "end": v(3466.88, -1869.07) * mm});
            skLineSegment(sketch, "E2819", {"start": v(3466.88, -1889.92) * mm, "end": v(3438.86, -1889.92) * mm});
            skLineSegment(sketch, "E2820", {"start": v(3491.47, -1898.5) * mm, "end": v(3472.57, -1891.17) * mm});
            skLineSegment(sketch, "E2821", {"start": v(3480.87, -1894.38) * mm, "end": v(3480.87, -1895.1) * mm});
            skLineSegment(sketch, "E2822", {"start": v(3414.27, -1865.94) * mm, "end": v(3414.27, -1893.1) * mm});
            skLineSegment(sketch, "E2823", {"start": v(3400.37, -1867.6) * mm, "end": v(3400.37, -1891.3) * mm});
            skLineSegment(sketch, "E2824", {"start": v(3424.87, -1864.6) * mm, "end": v(3424.87, -1863.9) * mm});
            skLineSegment(sketch, "E2825", {"start": v(3421.47, -1860.5) * mm, "end": v(3386.27, -1860.5) * mm});
            skLineSegment(sketch, "E2826", {"start": v(3382.87, -1863.9) * mm, "end": v(3382.87, -1895.1) * mm});
            skLineSegment(sketch, "E2827", {"start": v(3386.27, -1898.5) * mm, "end": v(3421.47, -1898.5) * mm});
            skLineSegment(sketch, "E2828", {"start": v(3424.87, -1895.1) * mm, "end": v(3424.87, -1894.38) * mm});
            skLineSegment(sketch, "E2829", {"start": v(3414.27, -1860.5) * mm, "end": v(3433.17, -1867.82) * mm});
            skLineSegment(sketch, "E2830", {"start": v(3433.17, -1891.17) * mm, "end": v(3414.27, -1898.5) * mm});
            skLineSegment(sketch, "E2831", {"start": v(3435.92, -1890.24) * mm, "end": v(3435.92, -1899.2) * mm});
            skLineSegment(sketch, "E2832", {"start": v(3435.92, -1899.2) * mm, "end": v(3469.82, -1899.2) * mm});
            skLineSegment(sketch, "E2833", {"start": v(3469.82, -1899.2) * mm, "end": v(3469.82, -1890.24) * mm});
            skLineSegment(sketch, "E2834", {"start": v(3435.92, -1868.75) * mm, "end": v(3435.92, -1865.2) * mm});
            skLineSegment(sketch, "E2835", {"start": v(3435.92, -1865.2) * mm, "end": v(3469.82, -1865.2) * mm});
            skLineSegment(sketch, "E2836", {"start": v(3469.82, -1865.2) * mm, "end": v(3469.82, -1868.75) * mm});
            skLineSegment(sketch, "E2837", {"start": v(3437.87, -1404) * mm, "end": v(3437.87, -1399) * mm});
            skLineSegment(sketch, "E2838", {"start": v(3411.37, -1412) * mm, "end": v(3419.37, -1404) * mm});
            skLineSegment(sketch, "E2839", {"start": v(3411.37, -1417.5) * mm, "end": v(3411.37, -1412) * mm});
            skLineSegment(sketch, "E2840", {"start": v(3411.37, -1417.5) * mm, "end": v(3408.87, -1420) * mm});
            skLineSegment(sketch, "E2841", {"start": v(3408.87, -1420.5) * mm, "end": v(3405.37, -1424) * mm});
            skLineSegment(sketch, "E2842", {"start": v(3408.87, -1420) * mm, "end": v(3408.87, -1420.5) * mm});
            skLineSegment(sketch, "E2843", {"start": v(3397.87, -1429.31) * mm, "end": v(3397.87, -1424) * mm});
            skLineSegment(sketch, "E2844", {"start": v(3407.87, -1432) * mm, "end": v(3397.87, -1429.31) * mm});
            skLineSegment(sketch, "E2845", {"start": v(3467.87, -1399) * mm, "end": v(3467.87, -1404) * mm});
            skLineSegment(sketch, "E2846", {"start": v(3397.87, -1429.31) * mm, "end": v(3507.87, -1429.31) * mm});
            skLineSegment(sketch, "E2847", {"start": v(3411.37, -1412) * mm, "end": v(3494.37, -1412) * mm});
            skLineSegment(sketch, "E2848", {"start": v(3419.37, -1404) * mm, "end": v(3486.37, -1404) * mm});
            skLineSegment(sketch, "E2849", {"start": v(3486.37, -1404) * mm, "end": v(3494.37, -1412) * mm});
            skLineSegment(sketch, "E2850", {"start": v(3494.37, -1412) * mm, "end": v(3494.37, -1417.5) * mm});
            skLineSegment(sketch, "E2851", {"start": v(3496.87, -1420) * mm, "end": v(3494.37, -1417.5) * mm});
            skLineSegment(sketch, "E2852", {"start": v(3500.37, -1424) * mm, "end": v(3496.87, -1420.5) * mm});
            skLineSegment(sketch, "E2853", {"start": v(3496.87, -1420.5) * mm, "end": v(3496.87, -1420) * mm});
            skLineSegment(sketch, "E2854", {"start": v(3497.87, -1432) * mm, "end": v(3407.87, -1432) * mm});
            skLineSegment(sketch, "E2855", {"start": v(3507.87, -1424) * mm, "end": v(3397.87, -1424) * mm});
            skLineSegment(sketch, "E2856", {"start": v(3507.87, -1424) * mm, "end": v(3507.87, -1429.31) * mm});
            skLineSegment(sketch, "E2857", {"start": v(3507.87, -1429.31) * mm, "end": v(3497.87, -1432) * mm});
            skLineSegment(sketch, "E2858", {"start": v(3491.47, -1398.05) * mm, "end": v(3491.47, -1370.9) * mm});
            skLineSegment(sketch, "E2859", {"start": v(3377.77, -1384.5) * mm, "end": v(3527.96, -1384.5) * mm});
            skLineSegment(sketch, "E2860", {"start": v(3505.37, -1396.39) * mm, "end": v(3505.37, -1372.68) * mm});
            skLineSegment(sketch, "E2861", {"start": v(3480.87, -1399.38) * mm, "end": v(3480.87, -1400.1) * mm});
            skLineSegment(sketch, "E2862", {"start": v(3484.27, -1403.5) * mm, "end": v(3519.47, -1403.5) * mm});
            skLineSegment(sketch, "E2863", {"start": v(3522.87, -1400.1) * mm, "end": v(3522.87, -1368.9) * mm});
            skLineSegment(sketch, "E2864", {"start": v(3519.47, -1365.5) * mm, "end": v(3484.27, -1365.5) * mm});
            skLineSegment(sketch, "E2865", {"start": v(3491.47, -1403.5) * mm, "end": v(3472.57, -1396.17) * mm});
            skLineSegment(sketch, "E2866", {"start": v(3466.88, -1394.92) * mm, "end": v(3438.86, -1394.92) * mm});
            skLineSegment(sketch, "E2867", {"start": v(3438.86, -1374.07) * mm, "end": v(3466.88, -1374.07) * mm});
            skLineSegment(sketch, "E2868", {"start": v(3472.57, -1372.82) * mm, "end": v(3491.47, -1365.5) * mm});
            skLineSegment(sketch, "E2869", {"start": v(3480.87, -1368.9) * mm, "end": v(3480.87, -1369.6) * mm});
            skLineSegment(sketch, "E2870", {"start": v(3414.27, -1370.9) * mm, "end": v(3414.27, -1398.05) * mm});
            skLineSegment(sketch, "E2871", {"start": v(3400.37, -1372.68) * mm, "end": v(3400.37, -1396.39) * mm});
            skLineSegment(sketch, "E2872", {"start": v(3424.87, -1400.1) * mm, "end": v(3424.87, -1399.38) * mm});
            skLineSegment(sketch, "E2873", {"start": v(3386.27, -1403.5) * mm, "end": v(3421.47, -1403.5) * mm});
            skLineSegment(sketch, "E2874", {"start": v(3382.87, -1368.9) * mm, "end": v(3382.87, -1400.1) * mm});
            skLineSegment(sketch, "E2875", {"start": v(3421.47, -1365.5) * mm, "end": v(3386.27, -1365.5) * mm});
            skLineSegment(sketch, "E2876", {"start": v(3424.87, -1369.6) * mm, "end": v(3424.87, -1368.9) * mm});
            skLineSegment(sketch, "E2877", {"start": v(3433.17, -1396.17) * mm, "end": v(3414.27, -1403.5) * mm});
            skLineSegment(sketch, "E2878", {"start": v(3414.27, -1365.5) * mm, "end": v(3433.17, -1372.82) * mm});
            skLineSegment(sketch, "E2879", {"start": v(3435.92, -1364.8) * mm, "end": v(3435.92, -1373.75) * mm});
            skLineSegment(sketch, "E2880", {"start": v(3469.82, -1364.8) * mm, "end": v(3435.92, -1364.8) * mm});
            skLineSegment(sketch, "E2881", {"start": v(3469.82, -1373.75) * mm, "end": v(3469.82, -1364.8) * mm});
            skLineSegment(sketch, "E2882", {"start": v(3435.92, -1398.8) * mm, "end": v(3435.92, -1395.24) * mm});
            skLineSegment(sketch, "E2883", {"start": v(3469.82, -1398.8) * mm, "end": v(3435.92, -1398.8) * mm});
            skLineSegment(sketch, "E2884", {"start": v(3469.82, -1395.24) * mm, "end": v(3469.82, -1398.8) * mm});
            skLineSegment(sketch, "E2885", {"start": v(4187.87, -1865) * mm, "end": v(4187.87, -1860) * mm});
            skLineSegment(sketch, "E2886", {"start": v(4169.37, -1860) * mm, "end": v(4161.37, -1852) * mm});
            skLineSegment(sketch, "E2887", {"start": v(4161.37, -1852) * mm, "end": v(4161.37, -1846.5) * mm});
            skLineSegment(sketch, "E2888", {"start": v(4158.87, -1844) * mm, "end": v(4161.37, -1846.5) * mm});
            skLineSegment(sketch, "E2889", {"start": v(4155.37, -1840) * mm, "end": v(4158.87, -1843.5) * mm});
            skLineSegment(sketch, "E2890", {"start": v(4158.87, -1843.5) * mm, "end": v(4158.87, -1844) * mm});
            skLineSegment(sketch, "E2891", {"start": v(4147.87, -1840) * mm, "end": v(4147.87, -1834.67) * mm});
            skLineSegment(sketch, "E2892", {"start": v(4147.87, -1834.67) * mm, "end": v(4157.87, -1832) * mm});
            skLineSegment(sketch, "E2893", {"start": v(4157.87, -1832) * mm, "end": v(4157.87, -1432) * mm});
            skLineSegment(sketch, "E2894", {"start": v(4217.87, -1860) * mm, "end": v(4217.87, -1865) * mm});
            skLineSegment(sketch, "E2895", {"start": v(4257.87, -1834.67) * mm, "end": v(4147.87, -1834.67) * mm});
            skLineSegment(sketch, "E2896", {"start": v(4244.37, -1852) * mm, "end": v(4161.37, -1852) * mm});
            skLineSegment(sketch, "E2897", {"start": v(4236.37, -1860) * mm, "end": v(4169.37, -1860) * mm});
            skLineSegment(sketch, "E2898", {"start": v(4244.37, -1852) * mm, "end": v(4236.37, -1860) * mm});
            skLineSegment(sketch, "E2899", {"start": v(4244.37, -1846.5) * mm, "end": v(4244.37, -1852) * mm});
            skLineSegment(sketch, "E2900", {"start": v(4244.37, -1846.5) * mm, "end": v(4246.87, -1844) * mm});
            skLineSegment(sketch, "E2901", {"start": v(4246.87, -1843.5) * mm, "end": v(4250.37, -1840) * mm});
            skLineSegment(sketch, "E2902", {"start": v(4246.87, -1844) * mm, "end": v(4246.87, -1843.5) * mm});
            skLineSegment(sketch, "E2903", {"start": v(4157.87, -1832) * mm, "end": v(4247.87, -1832) * mm});
            skLineSegment(sketch, "E2904", {"start": v(4147.87, -1840) * mm, "end": v(4257.87, -1840) * mm});
            skLineSegment(sketch, "E2905", {"start": v(4257.87, -1834.67) * mm, "end": v(4257.87, -1840) * mm});
            skLineSegment(sketch, "E2906", {"start": v(4247.87, -1832) * mm, "end": v(4257.87, -1834.67) * mm});
            skLineSegment(sketch, "E2907", {"start": v(4202.87, -1405.05) * mm, "end": v(4202.87, -1912.7) * mm});
            skLineSegment(sketch, "E2908", {"start": v(4247.87, -1432) * mm, "end": v(4247.87, -1832) * mm});
            skLineSegment(sketch, "E2909", {"start": v(4241.47, -1893.1) * mm, "end": v(4241.47, -1865.94) * mm});
            skLineSegment(sketch, "E2910", {"start": v(4277.96, -1879.5) * mm, "end": v(4127.77, -1879.5) * mm});
            skLineSegment(sketch, "E2911", {"start": v(4255.37, -1891.3) * mm, "end": v(4255.37, -1867.6) * mm});
            skLineSegment(sketch, "E2912", {"start": v(4230.87, -1863.9) * mm, "end": v(4230.87, -1864.6) * mm});
            skLineSegment(sketch, "E2913", {"start": v(4269.47, -1860.5) * mm, "end": v(4234.27, -1860.5) * mm});
            skLineSegment(sketch, "E2914", {"start": v(4272.87, -1895.1) * mm, "end": v(4272.87, -1863.9) * mm});
            skLineSegment(sketch, "E2915", {"start": v(4234.27, -1898.5) * mm, "end": v(4269.47, -1898.5) * mm});
            skLineSegment(sketch, "E2916", {"start": v(4222.57, -1867.82) * mm, "end": v(4241.47, -1860.5) * mm});
            skLineSegment(sketch, "E2917", {"start": v(4188.86, -1869.07) * mm, "end": v(4216.88, -1869.07) * mm});
            skLineSegment(sketch, "E2918", {"start": v(4216.88, -1889.92) * mm, "end": v(4188.86, -1889.92) * mm});
            skLineSegment(sketch, "E2919", {"start": v(4241.47, -1898.5) * mm, "end": v(4222.57, -1891.17) * mm});
            skLineSegment(sketch, "E2920", {"start": v(4230.87, -1894.38) * mm, "end": v(4230.87, -1895.1) * mm});
            skLineSegment(sketch, "E2921", {"start": v(4164.27, -1865.94) * mm, "end": v(4164.27, -1893.1) * mm});
            skLineSegment(sketch, "E2922", {"start": v(4150.37, -1867.6) * mm, "end": v(4150.37, -1891.3) * mm});
            skLineSegment(sketch, "E2923", {"start": v(4174.87, -1864.6) * mm, "end": v(4174.87, -1863.9) * mm});
            skLineSegment(sketch, "E2924", {"start": v(4171.47, -1860.5) * mm, "end": v(4136.27, -1860.5) * mm});
            skLineSegment(sketch, "E2925", {"start": v(4132.87, -1863.9) * mm, "end": v(4132.87, -1895.1) * mm});
            skLineSegment(sketch, "E2926", {"start": v(4136.27, -1898.5) * mm, "end": v(4171.47, -1898.5) * mm});
            skLineSegment(sketch, "E2927", {"start": v(4174.87, -1895.1) * mm, "end": v(4174.87, -1894.38) * mm});
            skLineSegment(sketch, "E2928", {"start": v(4164.27, -1860.5) * mm, "end": v(4183.17, -1867.82) * mm});
            skLineSegment(sketch, "E2929", {"start": v(4183.17, -1891.17) * mm, "end": v(4164.27, -1898.5) * mm});
            skLineSegment(sketch, "E2930", {"start": v(4185.92, -1890.24) * mm, "end": v(4185.92, -1899.2) * mm});
            skLineSegment(sketch, "E2931", {"start": v(4185.92, -1899.2) * mm, "end": v(4219.82, -1899.2) * mm});
            skLineSegment(sketch, "E2932", {"start": v(4219.82, -1899.2) * mm, "end": v(4219.82, -1890.24) * mm});
            skLineSegment(sketch, "E2933", {"start": v(4185.92, -1868.75) * mm, "end": v(4185.92, -1865.2) * mm});
            skLineSegment(sketch, "E2934", {"start": v(4185.92, -1865.2) * mm, "end": v(4219.82, -1865.2) * mm});
            skLineSegment(sketch, "E2935", {"start": v(4219.82, -1865.2) * mm, "end": v(4219.82, -1868.75) * mm});
            skLineSegment(sketch, "E2936", {"start": v(4187.87, -1404) * mm, "end": v(4187.87, -1399) * mm});
            skLineSegment(sketch, "E2937", {"start": v(4161.37, -1412) * mm, "end": v(4169.37, -1404) * mm});
            skLineSegment(sketch, "E2938", {"start": v(4161.37, -1417.5) * mm, "end": v(4161.37, -1412) * mm});
            skLineSegment(sketch, "E2939", {"start": v(4161.37, -1417.5) * mm, "end": v(4158.87, -1420) * mm});
            skLineSegment(sketch, "E2940", {"start": v(4158.87, -1420.5) * mm, "end": v(4155.37, -1424) * mm});
            skLineSegment(sketch, "E2941", {"start": v(4158.87, -1420) * mm, "end": v(4158.87, -1420.5) * mm});
            skLineSegment(sketch, "E2942", {"start": v(4147.87, -1429.31) * mm, "end": v(4147.87, -1424) * mm});
            skLineSegment(sketch, "E2943", {"start": v(4157.87, -1432) * mm, "end": v(4147.87, -1429.31) * mm});
            skLineSegment(sketch, "E2944", {"start": v(4217.87, -1399) * mm, "end": v(4217.87, -1404) * mm});
            skLineSegment(sketch, "E2945", {"start": v(4147.87, -1429.31) * mm, "end": v(4257.87, -1429.31) * mm});
            skLineSegment(sketch, "E2946", {"start": v(4161.37, -1412) * mm, "end": v(4244.37, -1412) * mm});
            skLineSegment(sketch, "E2947", {"start": v(4169.37, -1404) * mm, "end": v(4236.37, -1404) * mm});
            skLineSegment(sketch, "E2948", {"start": v(4236.37, -1404) * mm, "end": v(4244.37, -1412) * mm});
            skLineSegment(sketch, "E2949", {"start": v(4244.37, -1412) * mm, "end": v(4244.37, -1417.5) * mm});
            skLineSegment(sketch, "E2950", {"start": v(4246.87, -1420) * mm, "end": v(4244.37, -1417.5) * mm});
            skLineSegment(sketch, "E2951", {"start": v(4250.37, -1424) * mm, "end": v(4246.87, -1420.5) * mm});
            skLineSegment(sketch, "E2952", {"start": v(4246.87, -1420.5) * mm, "end": v(4246.87, -1420) * mm});
            skLineSegment(sketch, "E2953", {"start": v(4247.87, -1432) * mm, "end": v(4157.87, -1432) * mm});
            skLineSegment(sketch, "E2954", {"start": v(4257.87, -1424) * mm, "end": v(4147.87, -1424) * mm});
            skLineSegment(sketch, "E2955", {"start": v(4257.87, -1424) * mm, "end": v(4257.87, -1429.31) * mm});
            skLineSegment(sketch, "E2956", {"start": v(4257.87, -1429.31) * mm, "end": v(4247.87, -1432) * mm});
            skLineSegment(sketch, "E2957", {"start": v(4241.47, -1398.05) * mm, "end": v(4241.47, -1370.9) * mm});
            skLineSegment(sketch, "E2958", {"start": v(4127.77, -1384.5) * mm, "end": v(4277.96, -1384.5) * mm});
            skLineSegment(sketch, "E2959", {"start": v(4255.37, -1396.39) * mm, "end": v(4255.37, -1372.68) * mm});
            skLineSegment(sketch, "E2960", {"start": v(4230.87, -1399.38) * mm, "end": v(4230.87, -1400.1) * mm});
            skLineSegment(sketch, "E2961", {"start": v(4234.27, -1403.5) * mm, "end": v(4269.47, -1403.5) * mm});
            skLineSegment(sketch, "E2962", {"start": v(4272.87, -1400.1) * mm, "end": v(4272.87, -1368.9) * mm});
            skLineSegment(sketch, "E2963", {"start": v(4269.47, -1365.5) * mm, "end": v(4234.27, -1365.5) * mm});
            skLineSegment(sketch, "E2964", {"start": v(4216.88, -1394.92) * mm, "end": v(4188.86, -1394.92) * mm});
            skLineSegment(sketch, "E2965", {"start": v(4241.47, -1403.5) * mm, "end": v(4222.57, -1396.17) * mm});
            skLineSegment(sketch, "E2966", {"start": v(4188.86, -1374.07) * mm, "end": v(4216.88, -1374.07) * mm});
            skLineSegment(sketch, "E2967", {"start": v(4222.57, -1372.82) * mm, "end": v(4241.47, -1365.5) * mm});
            skLineSegment(sketch, "E2968", {"start": v(4230.87, -1368.9) * mm, "end": v(4230.87, -1369.6) * mm});
            skLineSegment(sketch, "E2969", {"start": v(4164.27, -1370.9) * mm, "end": v(4164.27, -1398.05) * mm});
            skLineSegment(sketch, "E2970", {"start": v(4150.37, -1372.68) * mm, "end": v(4150.37, -1396.39) * mm});
            skLineSegment(sketch, "E2971", {"start": v(4174.87, -1400.1) * mm, "end": v(4174.87, -1399.38) * mm});
            skLineSegment(sketch, "E2972", {"start": v(4136.27, -1403.5) * mm, "end": v(4171.47, -1403.5) * mm});
            skLineSegment(sketch, "E2973", {"start": v(4132.87, -1368.9) * mm, "end": v(4132.87, -1400.1) * mm});
            skLineSegment(sketch, "E2974", {"start": v(4171.47, -1365.5) * mm, "end": v(4136.27, -1365.5) * mm});
            skLineSegment(sketch, "E2975", {"start": v(4174.87, -1369.6) * mm, "end": v(4174.87, -1368.9) * mm});
            skLineSegment(sketch, "E2976", {"start": v(4183.17, -1396.17) * mm, "end": v(4164.27, -1403.5) * mm});
            skLineSegment(sketch, "E2977", {"start": v(4164.27, -1365.5) * mm, "end": v(4183.17, -1372.82) * mm});
            skLineSegment(sketch, "E2978", {"start": v(4185.92, -1364.8) * mm, "end": v(4185.92, -1373.75) * mm});
            skLineSegment(sketch, "E2979", {"start": v(4219.82, -1364.8) * mm, "end": v(4185.92, -1364.8) * mm});
            skLineSegment(sketch, "E2980", {"start": v(4219.82, -1373.75) * mm, "end": v(4219.82, -1364.8) * mm});
            skLineSegment(sketch, "E2981", {"start": v(4185.92, -1398.8) * mm, "end": v(4185.92, -1395.24) * mm});
            skLineSegment(sketch, "E2982", {"start": v(4219.82, -1398.8) * mm, "end": v(4185.92, -1398.8) * mm});
            skLineSegment(sketch, "E2983", {"start": v(4219.82, -1395.24) * mm, "end": v(4219.82, -1398.8) * mm});
            skLineSegment(sketch, "E2984", {"start": v(4964.87, -1900) * mm, "end": v(4965.37, -1899.5) * mm});
            skLineSegment(sketch, "E2985", {"start": v(4937.87, -1865) * mm, "end": v(4937.87, -1860) * mm});
            skLineSegment(sketch, "E2986", {"start": v(4919.37, -1860) * mm, "end": v(4911.37, -1852) * mm});
            skLineSegment(sketch, "E2987", {"start": v(4911.37, -1852) * mm, "end": v(4911.37, -1846.5) * mm});
            skLineSegment(sketch, "E2988", {"start": v(4908.87, -1844) * mm, "end": v(4911.37, -1846.5) * mm});
            skLineSegment(sketch, "E2989", {"start": v(4905.37, -1840) * mm, "end": v(4908.87, -1843.5) * mm});
            skLineSegment(sketch, "E2990", {"start": v(4908.87, -1843.5) * mm, "end": v(4908.87, -1844) * mm});
            skLineSegment(sketch, "E2991", {"start": v(4897.87, -1840) * mm, "end": v(4897.87, -1834.67) * mm});
            skLineSegment(sketch, "E2992", {"start": v(4897.87, -1834.67) * mm, "end": v(4907.87, -1832) * mm});
            skLineSegment(sketch, "E2993", {"start": v(4907.87, -1832) * mm, "end": v(4907.87, -1432) * mm});
            skLineSegment(sketch, "E2994", {"start": v(4967.87, -1860) * mm, "end": v(4967.87, -1865) * mm});
            skLineSegment(sketch, "E2995", {"start": v(5007.87, -1834.67) * mm, "end": v(4897.87, -1834.67) * mm});
            skLineSegment(sketch, "E2996", {"start": v(4994.37, -1852) * mm, "end": v(4911.37, -1852) * mm});
            skLineSegment(sketch, "E2997", {"start": v(4986.37, -1860) * mm, "end": v(4919.37, -1860) * mm});
            skLineSegment(sketch, "E2998", {"start": v(4994.37, -1852) * mm, "end": v(4986.37, -1860) * mm});
            skLineSegment(sketch, "E2999", {"start": v(4994.37, -1846.5) * mm, "end": v(4994.37, -1852) * mm});
            skLineSegment(sketch, "E3000", {"start": v(4994.37, -1846.5) * mm, "end": v(4996.87, -1844) * mm});
            skLineSegment(sketch, "E3001", {"start": v(4996.87, -1843.5) * mm, "end": v(5000.37, -1840) * mm});
            skLineSegment(sketch, "E3002", {"start": v(4996.87, -1844) * mm, "end": v(4996.87, -1843.5) * mm});
            skLineSegment(sketch, "E3003", {"start": v(4907.87, -1832) * mm, "end": v(4997.87, -1832) * mm});
            skLineSegment(sketch, "E3004", {"start": v(4897.87, -1840) * mm, "end": v(5007.87, -1840) * mm});
            skLineSegment(sketch, "E3005", {"start": v(5007.87, -1834.67) * mm, "end": v(5007.87, -1840) * mm});
            skLineSegment(sketch, "E3006", {"start": v(4997.87, -1832) * mm, "end": v(5007.87, -1834.67) * mm});
            skLineSegment(sketch, "E3007", {"start": v(4952.87, -1405.05) * mm, "end": v(4952.87, -1854) * mm});
            skLineSegment(sketch, "E3008", {"start": v(4997.87, -1432) * mm, "end": v(4997.87, -1832) * mm});
            skLineSegment(sketch, "E3009", {"start": v(4991.47, -1893.1) * mm, "end": v(4991.47, -1865.94) * mm});
            skLineSegment(sketch, "E3010", {"start": v(5027.96, -1879.5) * mm, "end": v(4877.77, -1879.5) * mm});
            skLineSegment(sketch, "E3011", {"start": v(5005.37, -1891.3) * mm, "end": v(5005.37, -1867.6) * mm});
            skLineSegment(sketch, "E3012", {"start": v(4980.87, -1863.9) * mm, "end": v(4980.87, -1864.6) * mm});
            skLineSegment(sketch, "E3013", {"start": v(5019.47, -1860.5) * mm, "end": v(4984.27, -1860.5) * mm});
            skLineSegment(sketch, "E3014", {"start": v(5022.87, -1895.1) * mm, "end": v(5022.87, -1863.9) * mm});
            skLineSegment(sketch, "E3015", {"start": v(4984.27, -1898.5) * mm, "end": v(5019.47, -1898.5) * mm});
            skLineSegment(sketch, "E3016", {"start": v(4952.87, -1906.75) * mm, "end": v(4952.87, -1854) * mm});
            skLineSegment(sketch, "E3017", {"start": v(4972.57, -1867.82) * mm, "end": v(4991.47, -1860.5) * mm});
            skLineSegment(sketch, "E3018", {"start": v(4938.86, -1869.07) * mm, "end": v(4966.88, -1869.07) * mm});
            skLineSegment(sketch, "E3019", {"start": v(4966.88, -1889.92) * mm, "end": v(4938.86, -1889.92) * mm});
            skLineSegment(sketch, "E3020", {"start": v(4991.47, -1898.5) * mm, "end": v(4972.57, -1891.17) * mm});
            skLineSegment(sketch, "E3021", {"start": v(4980.87, -1894.38) * mm, "end": v(4980.87, -1895.1) * mm});
            skLineSegment(sketch, "E3022", {"start": v(4914.27, -1865.94) * mm, "end": v(4914.27, -1893.1) * mm});
            skLineSegment(sketch, "E3023", {"start": v(4900.37, -1867.6) * mm, "end": v(4900.37, -1891.3) * mm});
            skLineSegment(sketch, "E3024", {"start": v(4924.87, -1864.6) * mm, "end": v(4924.87, -1863.9) * mm});
            skLineSegment(sketch, "E3025", {"start": v(4921.47, -1860.5) * mm, "end": v(4886.27, -1860.5) * mm});
            skLineSegment(sketch, "E3026", {"start": v(4882.87, -1863.9) * mm, "end": v(4882.87, -1895.1) * mm});
            skLineSegment(sketch, "E3027", {"start": v(4886.27, -1898.5) * mm, "end": v(4921.47, -1898.5) * mm});
            skLineSegment(sketch, "E3028", {"start": v(4924.87, -1895.1) * mm, "end": v(4924.87, -1894.38) * mm});
            skLineSegment(sketch, "E3029", {"start": v(4914.27, -1860.5) * mm, "end": v(4933.17, -1867.82) * mm});
            skLineSegment(sketch, "E3030", {"start": v(4933.17, -1891.17) * mm, "end": v(4914.27, -1898.5) * mm});
            skLineSegment(sketch, "E3031", {"start": v(4935.92, -1890.24) * mm, "end": v(4935.92, -1899.2) * mm});
            skLineSegment(sketch, "E3032", {"start": v(4935.92, -1899.2) * mm, "end": v(4969.82, -1899.2) * mm});
            skLineSegment(sketch, "E3033", {"start": v(4969.82, -1899.2) * mm, "end": v(4969.82, -1890.24) * mm});
            skLineSegment(sketch, "E3034", {"start": v(4935.92, -1868.75) * mm, "end": v(4935.92, -1865.2) * mm});
            skLineSegment(sketch, "E3035", {"start": v(4935.92, -1865.2) * mm, "end": v(4969.82, -1865.2) * mm});
            skLineSegment(sketch, "E3036", {"start": v(4969.82, -1865.2) * mm, "end": v(4969.82, -1868.75) * mm});
            skLineSegment(sketch, "E3037", {"start": v(4937.87, -1404) * mm, "end": v(4937.87, -1399) * mm});
            skLineSegment(sketch, "E3038", {"start": v(4911.37, -1412) * mm, "end": v(4919.37, -1404) * mm});
            skLineSegment(sketch, "E3039", {"start": v(4911.37, -1417.5) * mm, "end": v(4911.37, -1412) * mm});
            skLineSegment(sketch, "E3040", {"start": v(4911.37, -1417.5) * mm, "end": v(4908.87, -1420) * mm});
            skLineSegment(sketch, "E3041", {"start": v(4908.87, -1420.5) * mm, "end": v(4905.37, -1424) * mm});
            skLineSegment(sketch, "E3042", {"start": v(4908.87, -1420) * mm, "end": v(4908.87, -1420.5) * mm});
            skLineSegment(sketch, "E3043", {"start": v(4897.87, -1429.31) * mm, "end": v(4897.87, -1424) * mm});
            skLineSegment(sketch, "E3044", {"start": v(4907.87, -1432) * mm, "end": v(4897.87, -1429.31) * mm});
            skLineSegment(sketch, "E3045", {"start": v(4967.87, -1399) * mm, "end": v(4967.87, -1404) * mm});
            skLineSegment(sketch, "E3046", {"start": v(4897.87, -1429.31) * mm, "end": v(5007.87, -1429.31) * mm});
            skLineSegment(sketch, "E3047", {"start": v(4911.37, -1412) * mm, "end": v(4994.37, -1412) * mm});
            skLineSegment(sketch, "E3048", {"start": v(4919.37, -1404) * mm, "end": v(4986.37, -1404) * mm});
            skLineSegment(sketch, "E3049", {"start": v(4986.37, -1404) * mm, "end": v(4994.37, -1412) * mm});
            skLineSegment(sketch, "E3050", {"start": v(4994.37, -1412) * mm, "end": v(4994.37, -1417.5) * mm});
            skLineSegment(sketch, "E3051", {"start": v(4996.87, -1420) * mm, "end": v(4994.37, -1417.5) * mm});
            skLineSegment(sketch, "E3052", {"start": v(5000.37, -1424) * mm, "end": v(4996.87, -1420.5) * mm});
            skLineSegment(sketch, "E3053", {"start": v(4996.87, -1420.5) * mm, "end": v(4996.87, -1420) * mm});
            skLineSegment(sketch, "E3054", {"start": v(4997.87, -1432) * mm, "end": v(4907.87, -1432) * mm});
            skLineSegment(sketch, "E3055", {"start": v(5007.87, -1424) * mm, "end": v(4897.87, -1424) * mm});
            skLineSegment(sketch, "E3056", {"start": v(5007.87, -1424) * mm, "end": v(5007.87, -1429.31) * mm});
            skLineSegment(sketch, "E3057", {"start": v(5007.87, -1429.31) * mm, "end": v(4997.87, -1432) * mm});
            skLineSegment(sketch, "E3058", {"start": v(4991.47, -1398.05) * mm, "end": v(4991.47, -1370.9) * mm});
            skLineSegment(sketch, "E3059", {"start": v(4877.77, -1384.5) * mm, "end": v(5027.96, -1384.5) * mm});
            skLineSegment(sketch, "E3060", {"start": v(5005.37, -1396.39) * mm, "end": v(5005.37, -1372.68) * mm});
            skLineSegment(sketch, "E3061", {"start": v(4980.87, -1399.38) * mm, "end": v(4980.87, -1400.1) * mm});
            skLineSegment(sketch, "E3062", {"start": v(4984.27, -1403.5) * mm, "end": v(5019.47, -1403.5) * mm});
            skLineSegment(sketch, "E3063", {"start": v(5022.87, -1400.1) * mm, "end": v(5022.87, -1368.9) * mm});
            skLineSegment(sketch, "E3064", {"start": v(5019.47, -1365.5) * mm, "end": v(4984.27, -1365.5) * mm});
            skLineSegment(sketch, "E3065", {"start": v(4966.88, -1394.92) * mm, "end": v(4938.86, -1394.92) * mm});
            skLineSegment(sketch, "E3066", {"start": v(4991.47, -1403.5) * mm, "end": v(4972.57, -1396.17) * mm});
            skLineSegment(sketch, "E3067", {"start": v(4938.86, -1374.07) * mm, "end": v(4966.88, -1374.07) * mm});
            skLineSegment(sketch, "E3068", {"start": v(4972.57, -1372.82) * mm, "end": v(4991.47, -1365.5) * mm});
            skLineSegment(sketch, "E3069", {"start": v(4980.87, -1368.9) * mm, "end": v(4980.87, -1369.6) * mm});
            skLineSegment(sketch, "E3070", {"start": v(4914.27, -1370.9) * mm, "end": v(4914.27, -1398.05) * mm});
            skLineSegment(sketch, "E3071", {"start": v(4900.37, -1372.68) * mm, "end": v(4900.37, -1396.39) * mm});
            skLineSegment(sketch, "E3072", {"start": v(4924.87, -1400.1) * mm, "end": v(4924.87, -1399.38) * mm});
            skLineSegment(sketch, "E3073", {"start": v(4886.27, -1403.5) * mm, "end": v(4921.47, -1403.5) * mm});
            skLineSegment(sketch, "E3074", {"start": v(4882.87, -1368.9) * mm, "end": v(4882.87, -1400.1) * mm});
            skLineSegment(sketch, "E3075", {"start": v(4921.47, -1365.5) * mm, "end": v(4886.27, -1365.5) * mm});
            skLineSegment(sketch, "E3076", {"start": v(4924.87, -1369.6) * mm, "end": v(4924.87, -1368.9) * mm});
            skLineSegment(sketch, "E3077", {"start": v(4933.17, -1396.17) * mm, "end": v(4914.27, -1403.5) * mm});
            skLineSegment(sketch, "E3078", {"start": v(4914.27, -1365.5) * mm, "end": v(4933.17, -1372.82) * mm});
            skLineSegment(sketch, "E3079", {"start": v(4935.92, -1364.8) * mm, "end": v(4935.92, -1373.75) * mm});
            skLineSegment(sketch, "E3080", {"start": v(4969.82, -1373.75) * mm, "end": v(4969.82, -1364.8) * mm});
            skLineSegment(sketch, "E3081", {"start": v(4935.92, -1398.8) * mm, "end": v(4935.92, -1395.24) * mm});
            skLineSegment(sketch, "E3082", {"start": v(4969.82, -1398.8) * mm, "end": v(4935.92, -1398.8) * mm});
            skLineSegment(sketch, "E3083", {"start": v(4969.82, -1395.24) * mm, "end": v(4969.82, -1398.8) * mm});
            skLineSegment(sketch, "E3084", {"start": v(4202.87, -1399.98) * mm, "end": v(4202.87, -1357.24) * mm});
            skLineSegment(sketch, "E3085", {"start": v(4952.87, -1906.75) * mm, "end": v(4952.87, -1912.7) * mm});
            skLineSegment(sketch, "E3086", {"start": v(-4797.13, -1357.24) * mm, "end": v(-4797.13, -1399.98) * mm});
            skLineSegment(sketch, "E3087", {"start": v(3452.87, -1409.98) * mm, "end": v(3452.87, -1357.24) * mm});
            skLineSegment(sketch, "E3088", {"start": v(452.87, -1399.98) * mm, "end": v(452.87, -1357.24) * mm});
            skLineSegment(sketch, "E3089", {"start": v(2702.87, -1357.24) * mm, "end": v(2702.87, -1399.98) * mm});
            skLineSegment(sketch, "E3090", {"start": v(-1047.13, -1357.24) * mm, "end": v(-1047.13, -1399.98) * mm});
            skLineSegment(sketch, "E3091", {"start": v(-297.13, -1399.98) * mm, "end": v(-297.13, -1357.24) * mm});
            skLineSegment(sketch, "E3092", {"start": v(-3297.13, -1409.98) * mm, "end": v(-3297.13, -1347.24) * mm});
            skLineSegment(sketch, "E3093", {"start": v(-1797.13, -1399.98) * mm, "end": v(-1797.13, -1357.24) * mm});
            skLineSegment(sketch, "E3094", {"start": v(-2547.13, -1399.98) * mm, "end": v(-2547.13, -1357.24) * mm});
            skLineSegment(sketch, "E3095", {"start": v(4952.87, -1357.24) * mm, "end": v(4952.87, -1399.98) * mm});
            skLineSegment(sketch, "E3096", {"start": v(-3077.13, -1907) * mm, "end": v(-3077.13, -2157.5) * mm});
            skLineSegment(sketch, "E3097", {"start": v(-3077.13, -2157.5) * mm, "end": v(-3029.63, -2157.5) * mm});
            skLineSegment(sketch, "E3098", {"start": v(-2917.13, -2157.5) * mm, "end": v(-2917.13, -1907) * mm});
            skLineSegment(sketch, "E3099", {"start": v(-3077.13, -1987.02) * mm, "end": v(-3247.13, -1987.02) * mm});
            skLineSegment(sketch, "E3100", {"start": v(-3077.13, -2042.02) * mm, "end": v(-3247.13, -2042.02) * mm});
            skLineSegment(sketch, "E3101", {"start": v(-4364.63, -3257.5) * mm, "end": v(-4245.63, -3257.5) * mm});
            skLineSegment(sketch, "E3102", {"start": v(-4364.63, -3302.5) * mm, "end": v(-4245.63, -3302.5) * mm});
            skLineSegment(sketch, "E3103", {"start": v(-4567.13, -3602.9) * mm, "end": v(-4567.13, -3302.5) * mm});
            skLineSegment(sketch, "E3104", {"start": v(-3029.63, -3087.5) * mm, "end": v(-4218.63, -3087.5) * mm});
            skLineSegment(sketch, "E3105", {"start": v(-3029.63, -3107.5) * mm, "end": v(-4218.63, -3107.5) * mm});
            skLineSegment(sketch, "E3106", {"start": v(-3029.63, -3157.5) * mm, "end": v(-4218.63, -3157.5) * mm});
            skLineSegment(sketch, "E3107", {"start": v(-2964.63, -3177.5) * mm, "end": v(-1629.63, -3177.5) * mm});
            skLineSegment(sketch, "E3108", {"start": v(-1629.63, -3087.5) * mm, "end": v(-2964.63, -3087.5) * mm});
            skLineSegment(sketch, "E3109", {"start": v(-1629.63, -3107.5) * mm, "end": v(-2964.63, -3107.5) * mm});
            skLineSegment(sketch, "E3110", {"start": v(-1629.63, -3157.5) * mm, "end": v(-2964.63, -3157.5) * mm});
            skLineSegment(sketch, "E3111", {"start": v(-1564.63, -3177.5) * mm, "end": v(-813.13, -3177.5) * mm});
            skLineSegment(sketch, "E3112", {"start": v(-1767.13, -3160.9) * mm, "end": v(-2197.13, -3160.9) * mm});
            skLineSegment(sketch, "E3113", {"start": v(-1917.98, -3790.9) * mm, "end": v(-1767.13, -3790.9) * mm});
            skLineSegment(sketch, "E3114", {"start": v(4567.87, -1460.5) * mm, "end": v(4567.87, -1803.5) * mm});
            skLineSegment(sketch, "E3115", {"start": v(-4502.13, -3735.9) * mm, "end": v(-4502.13, -3667.9) * mm});
            skLineSegment(sketch, "E3116", {"start": v(-4502.13, -3302.5) * mm, "end": v(-4502.13, -3215.9) * mm});
            skLineSegment(sketch, "E3117", {"start": v(-4532.13, -3252.04) * mm, "end": v(-4544.13, -3258.97) * mm});
            skLineSegment(sketch, "E3118", {"start": v(-4544.13, -3258.97) * mm, "end": v(-4544.13, -3272.82) * mm});
            skLineSegment(sketch, "E3119", {"start": v(-4544.13, -3272.82) * mm, "end": v(-4532.13, -3279.75) * mm});
            skLineSegment(sketch, "E3120", {"start": v(-4532.13, -3279.75) * mm, "end": v(-4520.13, -3272.82) * mm});
            skLineSegment(sketch, "E3121", {"start": v(-4520.13, -3272.82) * mm, "end": v(-4520.13, -3258.97) * mm});
            skLineSegment(sketch, "E3122", {"start": v(-4520.13, -3258.97) * mm, "end": v(-4532.13, -3252.04) * mm});
            skLineSegment(sketch, "E3123", {"start": v(-4532.13, -3244.9) * mm, "end": v(-4532.13, -3286.9) * mm});
            skLineSegment(sketch, "E3124", {"start": v(-4553.13, -3265.9) * mm, "end": v(-4511.13, -3265.9) * mm});
            skLineSegment(sketch, "E3125", {"start": v(-4532.13, -3672.04) * mm, "end": v(-4544.13, -3678.97) * mm});
            skLineSegment(sketch, "E3126", {"start": v(-4544.13, -3678.97) * mm, "end": v(-4544.13, -3692.82) * mm});
            skLineSegment(sketch, "E3127", {"start": v(-4544.13, -3692.82) * mm, "end": v(-4532.13, -3699.75) * mm});
            skLineSegment(sketch, "E3128", {"start": v(-4532.13, -3699.75) * mm, "end": v(-4520.13, -3692.82) * mm});
            skLineSegment(sketch, "E3129", {"start": v(-4520.13, -3692.82) * mm, "end": v(-4520.13, -3678.97) * mm});
            skLineSegment(sketch, "E3130", {"start": v(-4520.13, -3678.97) * mm, "end": v(-4532.13, -3672.04) * mm});
            skLineSegment(sketch, "E3131", {"start": v(-4532.13, -3664.9) * mm, "end": v(-4532.13, -3706.9) * mm});
            skLineSegment(sketch, "E3132", {"start": v(-4553.13, -3685.9) * mm, "end": v(-4511.13, -3685.9) * mm});
            skLineSegment(sketch, "E3133", {"start": v(-4502.13, -3602.9) * mm, "end": v(-4502.13, -3302.5) * mm});
            skLineSegment(sketch, "E3134", {"start": v(-4502.13, -3667.9) * mm, "end": v(-4502.13, -3602.9) * mm});
            skLineSegment(sketch, "E3135", {"start": v(4969.82, -1364.8) * mm, "end": v(4935.92, -1364.8) * mm});
            skLineSegment(sketch, "E3136", {"start": v(5027.87, -1290) * mm, "end": v(377.87, -1290) * mm});
            skLineSegment(sketch, "E3137", {"start": v(377.87, -1364) * mm, "end": v(5047.87, -1364) * mm});
            skLineSegment(sketch, "E3138", {"start": v(-222.13, -1290) * mm, "end": v(-4872.13, -1290) * mm});
            skLineSegment(sketch, "E3139", {"start": v(-4892.13, -1364) * mm, "end": v(-222.13, -1364) * mm});
            skLineSegment(sketch, "E3140", {"start": v(-222.13, -1290) * mm, "end": v(-222.13, -1364) * mm});
            skArc(sketch, "E3141", {"start": v(-3209, -3525) * mm, "mid": v(-3210.75, -3520.75) * mm, "end": v(-3215, -3519) * mm});
            skArc(sketch, "E3142", {"start": v(-3215, -3569) * mm, "mid": v(-3210.75, -3567.24) * mm, "end": v(-3209, -3563) * mm});
            skArc(sketch, "E3143", {"start": v(-3259, -3563) * mm, "mid": v(-3257.24, -3567.24) * mm, "end": v(-3253, -3569) * mm});
            skArc(sketch, "E3144", {"start": v(-3253, -3519) * mm, "mid": v(-3257, -3520.53) * mm, "end": v(-3258.96, -3524.35) * mm});
            skArc(sketch, "E3145", {"start": v(-3250.43, -3550) * mm, "mid": v(-3216.5, -3544) * mm, "end": v(-3250.43, -3538) * mm});
            skArc(sketch, "E3146", {"start": v(-3203, -3394.76) * mm, "mid": v(-3205.92, -3390.36) * mm, "end": v(-3210.96, -3388.75) * mm});
            skArc(sketch, "E3147", {"start": v(-3210.96, -3451.24) * mm, "mid": v(-3204.5, -3448.23) * mm, "end": v(-3203, -3441.26) * mm});
            skArc(sketch, "E3148", {"start": v(-3265, -3441.26) * mm, "mid": v(-3263.5, -3448.23) * mm, "end": v(-3257.04, -3451.24) * mm});
            skArc(sketch, "E3149", {"start": v(-3257.04, -3388.75) * mm, "mid": v(-3263.5, -3391.76) * mm, "end": v(-3265, -3398.73) * mm});
            skArc(sketch, "E3150", {"start": v(-3217.29, -3430.98) * mm, "mid": v(-3214, -3419.38) * mm, "end": v(-3218, -3408) * mm});
            skArc(sketch, "E3151", {"start": v(-1809, -3525) * mm, "mid": v(-1810.75, -3520.75) * mm, "end": v(-1815, -3519) * mm});
            skArc(sketch, "E3152", {"start": v(-1815, -3569) * mm, "mid": v(-1810.75, -3567.24) * mm, "end": v(-1809, -3563) * mm});
            skArc(sketch, "E3153", {"start": v(-1859, -3563) * mm, "mid": v(-1857.24, -3567.24) * mm, "end": v(-1853, -3569) * mm});
            skArc(sketch, "E3154", {"start": v(-1853, -3519) * mm, "mid": v(-1857, -3520.53) * mm, "end": v(-1858.96, -3524.35) * mm});
            skArc(sketch, "E3155", {"start": v(-1850.43, -3550) * mm, "mid": v(-1816.5, -3544) * mm, "end": v(-1850.43, -3538) * mm});
            skArc(sketch, "E3156", {"start": v(-1803, -3394.76) * mm, "mid": v(-1805.92, -3390.36) * mm, "end": v(-1810.96, -3388.75) * mm});
            skArc(sketch, "E3157", {"start": v(-1810.96, -3451.24) * mm, "mid": v(-1804.5, -3448.23) * mm, "end": v(-1803, -3441.26) * mm});
            skArc(sketch, "E3158", {"start": v(-1865, -3441.26) * mm, "mid": v(-1863.5, -3448.23) * mm, "end": v(-1857.04, -3451.24) * mm});
            skArc(sketch, "E3159", {"start": v(-1857.04, -3388.75) * mm, "mid": v(-1863.5, -3391.76) * mm, "end": v(-1865, -3398.73) * mm});
            skArc(sketch, "E3160", {"start": v(-1817.29, -3430.98) * mm, "mid": v(-1814, -3419.38) * mm, "end": v(-1818, -3408) * mm});
            skArc(sketch, "E3161", {"start": v(391, -3525) * mm, "mid": v(389.25, -3520.75) * mm, "end": v(385, -3519) * mm});
            skArc(sketch, "E3162", {"start": v(385, -3569) * mm, "mid": v(389.25, -3567.24) * mm, "end": v(391, -3563) * mm});
            skArc(sketch, "E3163", {"start": v(341, -3563) * mm, "mid": v(342.76, -3567.24) * mm, "end": v(347, -3569) * mm});
            skArc(sketch, "E3164", {"start": v(347, -3519) * mm, "mid": v(343, -3520.53) * mm, "end": v(341.04, -3524.35) * mm});
            skArc(sketch, "E3165", {"start": v(349.57, -3550) * mm, "mid": v(383.5, -3544) * mm, "end": v(349.57, -3538) * mm});
            skArc(sketch, "E3166", {"start": v(397, -3394.76) * mm, "mid": v(394.08, -3390.36) * mm, "end": v(389.04, -3388.75) * mm});
            skArc(sketch, "E3167", {"start": v(389.04, -3451.24) * mm, "mid": v(395.5, -3448.23) * mm, "end": v(397, -3441.26) * mm});
            skArc(sketch, "E3168", {"start": v(335, -3441.26) * mm, "mid": v(336.5, -3448.23) * mm, "end": v(342.96, -3451.24) * mm});
            skArc(sketch, "E3169", {"start": v(342.96, -3388.75) * mm, "mid": v(336.5, -3391.76) * mm, "end": v(335, -3398.73) * mm});
            skArc(sketch, "E3170", {"start": v(382.71, -3430.98) * mm, "mid": v(386, -3419.38) * mm, "end": v(382, -3408) * mm});
            skArc(sketch, "E3171", {"start": v(2891, -3525) * mm, "mid": v(2889.25, -3520.75) * mm, "end": v(2885, -3519) * mm});
            skArc(sketch, "E3172", {"start": v(2885, -3569) * mm, "mid": v(2889.25, -3567.24) * mm, "end": v(2891, -3563) * mm});
            skArc(sketch, "E3173", {"start": v(2841, -3563) * mm, "mid": v(2842.76, -3567.24) * mm, "end": v(2847, -3569) * mm});
            skArc(sketch, "E3174", {"start": v(2847, -3519) * mm, "mid": v(2843, -3520.53) * mm, "end": v(2841.04, -3524.35) * mm});
            skArc(sketch, "E3175", {"start": v(2849.57, -3550) * mm, "mid": v(2883.5, -3544) * mm, "end": v(2849.57, -3538) * mm});
            skArc(sketch, "E3176", {"start": v(2897, -3394.76) * mm, "mid": v(2894.08, -3390.36) * mm, "end": v(2889.04, -3388.75) * mm});
            skArc(sketch, "E3177", {"start": v(2889.04, -3451.24) * mm, "mid": v(2895.5, -3448.23) * mm, "end": v(2897, -3441.26) * mm});
            skArc(sketch, "E3178", {"start": v(2835, -3441.26) * mm, "mid": v(2836.5, -3448.23) * mm, "end": v(2842.96, -3451.24) * mm});
            skArc(sketch, "E3179", {"start": v(2842.96, -3388.75) * mm, "mid": v(2836.5, -3391.76) * mm, "end": v(2835, -3398.73) * mm});
            skArc(sketch, "E3180", {"start": v(2882.71, -3430.98) * mm, "mid": v(2886, -3419.38) * mm, "end": v(2882, -3408) * mm});
            skArc(sketch, "E3181", {"start": v(-1876.45, -3775.5) * mm, "mid": v(-1807.13, -3850) * mm, "end": v(-1737.81, -3775.5) * mm});
            skArc(sketch, "E3182", {"start": v(-1918.1, -3775.5) * mm, "mid": v(-1917.61, -3799.6) * mm, "end": v(-1915.47, -3823.6) * mm});
            skArc(sketch, "E3183", {"start": v(-2959.86, -3685.94) * mm, "mid": v(-2961.3, -3685.5) * mm, "end": v(-2962.75, -3685.94) * mm});
            skArc(sketch, "E3184", {"start": v(-2965.93, -3690.49) * mm, "mid": v(-2964.32, -3690.4) * mm, "end": v(-2962.75, -3690.05) * mm});
            skArc(sketch, "E3185", {"start": v(-2962.75, -3690.05) * mm, "mid": v(-2961.3, -3690.5) * mm, "end": v(-2959.86, -3690.05) * mm});
            skArc(sketch, "E3186", {"start": v(-3027.93, -3685.52) * mm, "mid": v(-3029.75, -3685.56) * mm, "end": v(-3031.52, -3685.94) * mm});
            skArc(sketch, "E3187", {"start": v(-3031.52, -3685.94) * mm, "mid": v(-3032.96, -3685.5) * mm, "end": v(-3034.4, -3685.94) * mm});
            skArc(sketch, "E3188", {"start": v(-3034.4, -3690.05) * mm, "mid": v(-3032.96, -3690.5) * mm, "end": v(-3031.52, -3690.05) * mm});
            skArc(sketch, "E3189", {"start": v(-2962.75, -3685.94) * mm, "mid": v(-2964.32, -3685.58) * mm, "end": v(-2965.93, -3685.5) * mm});
            skArc(sketch, "E3190", {"start": v(-3031.52, -3690.05) * mm, "mid": v(-3029.75, -3690.43) * mm, "end": v(-3027.93, -3690.47) * mm});
            skArc(sketch, "E3191", {"start": v(-4431.52, -3690.05) * mm, "mid": v(-4429.75, -3690.43) * mm, "end": v(-4427.93, -3690.47) * mm});
            skArc(sketch, "E3192", {"start": v(-4362.75, -3685.94) * mm, "mid": v(-4364.32, -3685.58) * mm, "end": v(-4365.93, -3685.5) * mm});
            skArc(sketch, "E3193", {"start": v(-4434.4, -3690.05) * mm, "mid": v(-4432.96, -3690.5) * mm, "end": v(-4431.52, -3690.05) * mm});
            skArc(sketch, "E3194", {"start": v(-4431.52, -3685.94) * mm, "mid": v(-4432.96, -3685.5) * mm, "end": v(-4434.4, -3685.94) * mm});
            skArc(sketch, "E3195", {"start": v(-4427.93, -3685.52) * mm, "mid": v(-4429.75, -3685.56) * mm, "end": v(-4431.52, -3685.94) * mm});
            skArc(sketch, "E3196", {"start": v(-4362.75, -3690.05) * mm, "mid": v(-4361.3, -3690.5) * mm, "end": v(-4359.86, -3690.05) * mm});
            skArc(sketch, "E3197", {"start": v(-4365.93, -3690.49) * mm, "mid": v(-4364.32, -3690.4) * mm, "end": v(-4362.75, -3690.05) * mm});
            skArc(sketch, "E3198", {"start": v(-4359.86, -3685.94) * mm, "mid": v(-4361.3, -3685.5) * mm, "end": v(-4362.75, -3685.94) * mm});
            skArc(sketch, "E3199", {"start": v(-4607.13, -3713.4) * mm, "mid": v(-4582.12, -3697.32) * mm, "end": v(-4586.34, -3667.9) * mm});
            skArc(sketch, "E3200", {"start": v(-4586.34, -3667.9) * mm, "mid": v(-4607.13, -3658.4) * mm, "end": v(-4627.92, -3667.9) * mm});
            skCircle(sketch, "E3201", {"center": v(-3557.13, -3265.9) * mm, "radius": 27.5 * mm});
            skCircle(sketch, "E3202", {"center": v(-3557.13, -3685.9) * mm, "radius": 27.5 * mm});
            skCircle(sketch, "E3203", {"center": v(-3207.13, -3265.9) * mm, "radius": 27.5 * mm});
            skCircle(sketch, "E3204", {"center": v(-3207.13, -3685.9) * mm, "radius": 27.5 * mm});
            skCircle(sketch, "E3205", {"center": v(-2157.13, -3265.9) * mm, "radius": 27.5 * mm});
            skCircle(sketch, "E3206", {"center": v(-2157.13, -3685.9) * mm, "radius": 27.5 * mm});
            skCircle(sketch, "E3207", {"center": v(-1807.13, -3265.9) * mm, "radius": 27.5 * mm});
            skCircle(sketch, "E3208", {"center": v(-1807.13, -3685.9) * mm, "radius": 27.5 * mm});
            skCircle(sketch, "E3209", {"center": v(42.87, -3265.9) * mm, "radius": 27.5 * mm});
            skCircle(sketch, "E3210", {"center": v(42.87, -3685.9) * mm, "radius": 27.5 * mm});
            skCircle(sketch, "E3211", {"center": v(392.87, -3265.9) * mm, "radius": 27.5 * mm});
            skCircle(sketch, "E3212", {"center": v(392.87, -3685.9) * mm, "radius": 27.5 * mm});
            skCircle(sketch, "E3213", {"center": v(2542.87, -3265.9) * mm, "radius": 27.5 * mm});
            skCircle(sketch, "E3214", {"center": v(2542.87, -3685.9) * mm, "radius": 27.5 * mm});
            skCircle(sketch, "E3215", {"center": v(2892.87, -3265.9) * mm, "radius": 27.5 * mm});
            skCircle(sketch, "E3216", {"center": v(2892.87, -3685.9) * mm, "radius": 27.5 * mm});
            skCircle(sketch, "E3217", {"center": v(-3037.63, -2167) * mm, "radius": 5 * mm});
            skCircle(sketch, "E3218", {"center": v(-3037.63, -2167) * mm, "radius": 2.89 * mm});
            skCircle(sketch, "E3219", {"center": v(-3037.63, -2117) * mm, "radius": 5 * mm});
            skCircle(sketch, "E3220", {"center": v(-3037.63, -2117) * mm, "radius": 2.89 * mm});
            skCircle(sketch, "E3221", {"center": v(-2956.63, -2167) * mm, "radius": 5 * mm});
            skCircle(sketch, "E3222", {"center": v(-2956.63, -2167) * mm, "radius": 2.89 * mm});
            skCircle(sketch, "E3223", {"center": v(-2956.63, -2117) * mm, "radius": 5 * mm});
            skCircle(sketch, "E3224", {"center": v(-2956.63, -2117) * mm, "radius": 2.89 * mm});
            skCircle(sketch, "E3225", {"center": v(-3037.63, -1997) * mm, "radius": 5 * mm});
            skCircle(sketch, "E3226", {"center": v(-3037.63, -1997) * mm, "radius": 2.89 * mm});
            skCircle(sketch, "E3227", {"center": v(-3037.63, -2047) * mm, "radius": 5 * mm});
            skCircle(sketch, "E3228", {"center": v(-3037.63, -2047) * mm, "radius": 2.89 * mm});
            skCircle(sketch, "E3229", {"center": v(-2956.63, -1997) * mm, "radius": 5 * mm});
            skCircle(sketch, "E3230", {"center": v(-2956.63, -1997) * mm, "radius": 2.89 * mm});
            skCircle(sketch, "E3231", {"center": v(-2956.63, -2047) * mm, "radius": 5 * mm});
            skCircle(sketch, "E3232", {"center": v(-2956.63, -2047) * mm, "radius": 2.89 * mm});
            skCircle(sketch, "E3233", {"center": v(-1807.13, -3780.5) * mm, "radius": 13.33 * mm});
            skCircle(sketch, "E3234", {"center": v(-4849.63, -1879.5) * mm, "radius": 10.5 * mm});
            skCircle(sketch, "E3235", {"center": v(-4744.63, -1879.5) * mm, "radius": 10.5 * mm});
            skCircle(sketch, "E3236", {"center": v(-3197.13, -1937.02) * mm, "radius": 22.5 * mm});
            skCircle(sketch, "E3237", {"center": v(-2797.13, -1937.02) * mm, "radius": 22.5 * mm});
            skCircle(sketch, "E3238", {"center": v(-2797.13, -1252) * mm, "radius": 22.5 * mm});
            skCircle(sketch, "E3239", {"center": v(-3197.13, -1252) * mm, "radius": 22.5 * mm});
            skCircle(sketch, "E3240", {"center": v(-3197.13, -2012.02) * mm, "radius": 22.5 * mm});
            skCircle(sketch, "E3241", {"center": v(-2797.13, -2012.02) * mm, "radius": 22.5 * mm});
            skCircle(sketch, "E3242", {"center": v(2902.87, -1937.02) * mm, "radius": 22.5 * mm});
            skCircle(sketch, "E3243", {"center": v(3302.87, -1937.02) * mm, "radius": 22.5 * mm});
            skCircle(sketch, "E3244", {"center": v(3302.87, -1252) * mm, "radius": 22.5 * mm});
            skCircle(sketch, "E3245", {"center": v(2902.87, -1252) * mm, "radius": 22.5 * mm});
            skCircle(sketch, "E3246", {"center": v(2902.87, -2012.02) * mm, "radius": 22.5 * mm});
            skCircle(sketch, "E3247", {"center": v(3302.87, -2012.02) * mm, "radius": 22.5 * mm});
            skCircle(sketch, "E3248", {"center": v(-4744.63, -1384.5) * mm, "radius": 10.5 * mm});
            skCircle(sketch, "E3249", {"center": v(-4849.63, -1384.5) * mm, "radius": 8 * mm});
            skCircle(sketch, "E3250", {"center": v(-4099.63, -1879.5) * mm, "radius": 10.5 * mm});
            skCircle(sketch, "E3251", {"center": v(-3994.63, -1879.5) * mm, "radius": 10.5 * mm});
            skCircle(sketch, "E3252", {"center": v(-4099.63, -1384.5) * mm, "radius": 10.5 * mm});
            skCircle(sketch, "E3253", {"center": v(-3994.63, -1384.5) * mm, "radius": 10.5 * mm});
            skCircle(sketch, "E3254", {"center": v(-3349.63, -1879.5) * mm, "radius": 10.5 * mm});
            skCircle(sketch, "E3255", {"center": v(-3244.63, -1879.5) * mm, "radius": 10.5 * mm});
            skCircle(sketch, "E3256", {"center": v(-3349.63, -1384.5) * mm, "radius": 10.5 * mm});
            skCircle(sketch, "E3257", {"center": v(-3244.63, -1384.5) * mm, "radius": 10.5 * mm});
            skCircle(sketch, "E3258", {"center": v(-2599.63, -1879.5) * mm, "radius": 10.5 * mm});
            skCircle(sketch, "E3259", {"center": v(-2494.63, -1879.5) * mm, "radius": 10.5 * mm});
            skCircle(sketch, "E3260", {"center": v(-2599.63, -1384.5) * mm, "radius": 10.5 * mm});
            skCircle(sketch, "E3261", {"center": v(-2494.63, -1384.5) * mm, "radius": 10.5 * mm});
            skCircle(sketch, "E3262", {"center": v(-1849.63, -1879.5) * mm, "radius": 10.5 * mm});
            skCircle(sketch, "E3263", {"center": v(-1744.63, -1879.5) * mm, "radius": 10.5 * mm});
            skCircle(sketch, "E3264", {"center": v(-1849.63, -1384.5) * mm, "radius": 10.5 * mm});
            skCircle(sketch, "E3265", {"center": v(-1744.63, -1384.5) * mm, "radius": 10.5 * mm});
            skCircle(sketch, "E3266", {"center": v(-1099.63, -1879.5) * mm, "radius": 10.5 * mm});
            skCircle(sketch, "E3267", {"center": v(-994.63, -1879.5) * mm, "radius": 10.5 * mm});
            skCircle(sketch, "E3268", {"center": v(-1099.63, -1384.5) * mm, "radius": 10.5 * mm});
            skCircle(sketch, "E3269", {"center": v(-994.63, -1384.5) * mm, "radius": 10.5 * mm});
            skCircle(sketch, "E3270", {"center": v(-349.63, -1879.5) * mm, "radius": 10.5 * mm});
            skCircle(sketch, "E3271", {"center": v(-244.63, -1879.5) * mm, "radius": 10.5 * mm});
            skCircle(sketch, "E3272", {"center": v(-349.63, -1384.5) * mm, "radius": 10.5 * mm});
            skCircle(sketch, "E3273", {"center": v(-244.63, -1384.5) * mm, "radius": 10.5 * mm});
            skCircle(sketch, "E3274", {"center": v(400.37, -1879.5) * mm, "radius": 10.5 * mm});
            skCircle(sketch, "E3275", {"center": v(505.37, -1879.5) * mm, "radius": 10.5 * mm});
            skCircle(sketch, "E3276", {"center": v(400.37, -1384.5) * mm, "radius": 10.5 * mm});
            skCircle(sketch, "E3277", {"center": v(505.37, -1384.5) * mm, "radius": 10.5 * mm});
            skCircle(sketch, "E3278", {"center": v(1150.37, -1879.5) * mm, "radius": 10.5 * mm});
            skCircle(sketch, "E3279", {"center": v(1255.37, -1879.5) * mm, "radius": 10.5 * mm});
            skCircle(sketch, "E3280", {"center": v(1150.37, -1384.5) * mm, "radius": 10.5 * mm});
            skCircle(sketch, "E3281", {"center": v(1255.37, -1384.5) * mm, "radius": 10.5 * mm});
            skCircle(sketch, "E3282", {"center": v(1900.37, -1879.5) * mm, "radius": 10.5 * mm});
            skCircle(sketch, "E3283", {"center": v(2005.37, -1879.5) * mm, "radius": 10.5 * mm});
            skCircle(sketch, "E3284", {"center": v(1900.37, -1384.5) * mm, "radius": 10.5 * mm});
            skCircle(sketch, "E3285", {"center": v(2005.37, -1384.5) * mm, "radius": 10.5 * mm});
            skCircle(sketch, "E3286", {"center": v(2650.37, -1879.5) * mm, "radius": 10.5 * mm});
            skCircle(sketch, "E3287", {"center": v(2755.37, -1879.5) * mm, "radius": 10.5 * mm});
            skCircle(sketch, "E3288", {"center": v(2650.37, -1384.5) * mm, "radius": 10.5 * mm});
            skCircle(sketch, "E3289", {"center": v(2755.37, -1384.5) * mm, "radius": 10.5 * mm});
            skCircle(sketch, "E3290", {"center": v(3400.37, -1879.5) * mm, "radius": 10.5 * mm});
            skCircle(sketch, "E3291", {"center": v(3505.37, -1879.5) * mm, "radius": 10.5 * mm});
            skCircle(sketch, "E3292", {"center": v(3400.37, -1384.5) * mm, "radius": 10.5 * mm});
            skCircle(sketch, "E3293", {"center": v(3505.37, -1384.5) * mm, "radius": 10.5 * mm});
            skCircle(sketch, "E3294", {"center": v(4150.37, -1879.5) * mm, "radius": 10.5 * mm});
            skCircle(sketch, "E3295", {"center": v(4255.37, -1879.5) * mm, "radius": 10.5 * mm});
            skCircle(sketch, "E3296", {"center": v(4150.37, -1384.5) * mm, "radius": 10.5 * mm});
            skCircle(sketch, "E3297", {"center": v(4255.37, -1384.5) * mm, "radius": 10.5 * mm});
            skCircle(sketch, "E3298", {"center": v(4900.37, -1879.5) * mm, "radius": 10.5 * mm});
            skCircle(sketch, "E3299", {"center": v(5005.37, -1879.5) * mm, "radius": 10.5 * mm});
            skCircle(sketch, "E3300", {"center": v(4900.37, -1384.5) * mm, "radius": 10.5 * mm});
            skCircle(sketch, "E3301", {"center": v(5005.37, -1384.5) * mm, "radius": 10.5 * mm});
            skArc(sketch, "E3302", {"start": v(-3474.13, -3557.5) * mm, "mid": v(-3471.09, -3564.85) * mm, "end": v(-3463.73, -3567.9) * mm});
            skArc(sketch, "E3303", {"start": v(-3482.13, -3557.5) * mm, "mid": v(-3476.74, -3570.5) * mm, "end": v(-3463.73, -3575.9) * mm});
            skArc(sketch, "E3304", {"start": v(-3463.73, -3383.9) * mm, "mid": v(-3471.09, -3386.94) * mm, "end": v(-3474.13, -3394.3) * mm});
            skArc(sketch, "E3305", {"start": v(-3463.73, -3375.9) * mm, "mid": v(-3476.74, -3381.28) * mm, "end": v(-3482.13, -3394.3) * mm});
            skArc(sketch, "E3306", {"start": v(-3300.53, -3567.9) * mm, "mid": v(-3293.18, -3564.85) * mm, "end": v(-3290.13, -3557.5) * mm});
            skArc(sketch, "E3307", {"start": v(-3300.53, -3575.9) * mm, "mid": v(-3287.52, -3570.5) * mm, "end": v(-3282.13, -3557.5) * mm});
            skArc(sketch, "E3308", {"start": v(-3290.13, -3394.3) * mm, "mid": v(-3293.18, -3386.94) * mm, "end": v(-3300.53, -3383.9) * mm});
            skArc(sketch, "E3309", {"start": v(-3282.13, -3394.3) * mm, "mid": v(-3287.52, -3381.28) * mm, "end": v(-3300.53, -3375.9) * mm});
            skArc(sketch, "E3310", {"start": v(-2074.13, -3557.5) * mm, "mid": v(-2071.09, -3564.85) * mm, "end": v(-2063.73, -3567.9) * mm});
            skArc(sketch, "E3311", {"start": v(-2082.13, -3557.5) * mm, "mid": v(-2076.74, -3570.5) * mm, "end": v(-2063.73, -3575.9) * mm});
            skArc(sketch, "E3312", {"start": v(-2063.73, -3383.9) * mm, "mid": v(-2071.09, -3386.94) * mm, "end": v(-2074.13, -3394.3) * mm});
            skArc(sketch, "E3313", {"start": v(-2063.73, -3375.9) * mm, "mid": v(-2076.74, -3381.28) * mm, "end": v(-2082.13, -3394.3) * mm});
            skArc(sketch, "E3314", {"start": v(-1900.53, -3567.9) * mm, "mid": v(-1893.18, -3564.85) * mm, "end": v(-1890.13, -3557.5) * mm});
            skArc(sketch, "E3315", {"start": v(-1900.53, -3575.9) * mm, "mid": v(-1887.52, -3570.5) * mm, "end": v(-1882.13, -3557.5) * mm});
            skArc(sketch, "E3316", {"start": v(-1890.13, -3394.3) * mm, "mid": v(-1893.18, -3386.94) * mm, "end": v(-1900.53, -3383.9) * mm});
            skArc(sketch, "E3317", {"start": v(-1882.13, -3394.3) * mm, "mid": v(-1887.52, -3381.28) * mm, "end": v(-1900.53, -3375.9) * mm});
            skArc(sketch, "E3318", {"start": v(125.87, -3557.5) * mm, "mid": v(128.91, -3564.85) * mm, "end": v(136.27, -3567.9) * mm});
            skArc(sketch, "E3319", {"start": v(117.87, -3557.5) * mm, "mid": v(123.26, -3570.5) * mm, "end": v(136.27, -3575.9) * mm});
            skArc(sketch, "E3320", {"start": v(136.27, -3383.9) * mm, "mid": v(128.91, -3386.94) * mm, "end": v(125.87, -3394.3) * mm});
            skArc(sketch, "E3321", {"start": v(136.27, -3375.9) * mm, "mid": v(123.26, -3381.28) * mm, "end": v(117.87, -3394.3) * mm});
            skArc(sketch, "E3322", {"start": v(299.47, -3567.9) * mm, "mid": v(306.82, -3564.85) * mm, "end": v(309.87, -3557.5) * mm});
            skArc(sketch, "E3323", {"start": v(299.47, -3575.9) * mm, "mid": v(312.48, -3570.5) * mm, "end": v(317.87, -3557.5) * mm});
            skArc(sketch, "E3324", {"start": v(309.87, -3394.3) * mm, "mid": v(306.82, -3386.94) * mm, "end": v(299.47, -3383.9) * mm});
            skArc(sketch, "E3325", {"start": v(317.87, -3394.3) * mm, "mid": v(312.48, -3381.28) * mm, "end": v(299.47, -3375.9) * mm});
            skArc(sketch, "E3326", {"start": v(2625.87, -3557.5) * mm, "mid": v(2628.91, -3564.85) * mm, "end": v(2636.27, -3567.9) * mm});
            skArc(sketch, "E3327", {"start": v(2617.87, -3557.5) * mm, "mid": v(2623.26, -3570.5) * mm, "end": v(2636.27, -3575.9) * mm});
            skArc(sketch, "E3328", {"start": v(2636.27, -3383.9) * mm, "mid": v(2628.91, -3386.94) * mm, "end": v(2625.87, -3394.3) * mm});
            skArc(sketch, "E3329", {"start": v(2636.27, -3375.9) * mm, "mid": v(2623.26, -3381.28) * mm, "end": v(2617.87, -3394.3) * mm});
            skArc(sketch, "E3330", {"start": v(2799.47, -3567.9) * mm, "mid": v(2806.82, -3564.85) * mm, "end": v(2809.87, -3557.5) * mm});
            skArc(sketch, "E3331", {"start": v(2799.47, -3575.9) * mm, "mid": v(2812.48, -3570.5) * mm, "end": v(2817.87, -3557.5) * mm});
            skArc(sketch, "E3332", {"start": v(2809.87, -3394.3) * mm, "mid": v(2806.82, -3386.94) * mm, "end": v(2799.47, -3383.9) * mm});
            skArc(sketch, "E3333", {"start": v(2817.87, -3394.3) * mm, "mid": v(2812.48, -3381.28) * mm, "end": v(2799.47, -3375.9) * mm});
            skArc(sketch, "E3334", {"start": v(-4765.73, -1860.5) * mm, "mid": v(-4768.14, -1861.49) * mm, "end": v(-4769.13, -1863.9) * mm});
            skArc(sketch, "E3335", {"start": v(-4727.13, -1863.9) * mm, "mid": v(-4728.13, -1861.49) * mm, "end": v(-4730.53, -1860.5) * mm});
            skArc(sketch, "E3336", {"start": v(-4730.53, -1898.5) * mm, "mid": v(-4728.13, -1897.5) * mm, "end": v(-4727.13, -1895.1) * mm});
            skArc(sketch, "E3337", {"start": v(-4769.13, -1895.1) * mm, "mid": v(-4768.14, -1897.5) * mm, "end": v(-4765.73, -1898.5) * mm});
            skArc(sketch, "E3338", {"start": v(-4783.12, -1869.07) * mm, "mid": v(-4780.21, -1868.75) * mm, "end": v(-4777.43, -1867.82) * mm});
            skArc(sketch, "E3339", {"start": v(-4816.83, -1867.82) * mm, "mid": v(-4814.05, -1868.75) * mm, "end": v(-4811.14, -1869.07) * mm});
            skArc(sketch, "E3340", {"start": v(-4777.43, -1891.17) * mm, "mid": v(-4780.21, -1890.23) * mm, "end": v(-4783.12, -1889.92) * mm});
            skArc(sketch, "E3341", {"start": v(-4811.14, -1889.92) * mm, "mid": v(-4814.05, -1890.23) * mm, "end": v(-4816.83, -1891.17) * mm});
            skArc(sketch, "E3342", {"start": v(-4825.13, -1863.9) * mm, "mid": v(-4826.13, -1861.49) * mm, "end": v(-4828.53, -1860.5) * mm});
            skArc(sketch, "E3343", {"start": v(-4863.73, -1860.5) * mm, "mid": v(-4866.14, -1861.49) * mm, "end": v(-4867.13, -1863.9) * mm});
            skArc(sketch, "E3344", {"start": v(-4867.13, -1895.1) * mm, "mid": v(-4866.14, -1897.5) * mm, "end": v(-4863.73, -1898.5) * mm});
            skArc(sketch, "E3345", {"start": v(-4828.53, -1898.5) * mm, "mid": v(-4826.13, -1897.5) * mm, "end": v(-4825.13, -1895.1) * mm});
            skArc(sketch, "E3346", {"start": v(-4769.13, -1400.1) * mm, "mid": v(-4768.14, -1402.5) * mm, "end": v(-4765.73, -1403.5) * mm});
            skArc(sketch, "E3347", {"start": v(-4730.53, -1403.5) * mm, "mid": v(-4728.13, -1402.5) * mm, "end": v(-4727.13, -1400.1) * mm});
            skArc(sketch, "E3348", {"start": v(-4727.13, -1368.9) * mm, "mid": v(-4728.13, -1366.49) * mm, "end": v(-4730.53, -1365.5) * mm});
            skArc(sketch, "E3349", {"start": v(-4765.73, -1365.5) * mm, "mid": v(-4768.14, -1366.49) * mm, "end": v(-4769.13, -1368.9) * mm});
            skArc(sketch, "E3350", {"start": v(-4777.43, -1396.17) * mm, "mid": v(-4780.21, -1395.23) * mm, "end": v(-4783.12, -1394.92) * mm});
            skArc(sketch, "E3351", {"start": v(-4811.14, -1394.92) * mm, "mid": v(-4814.05, -1395.23) * mm, "end": v(-4816.83, -1396.17) * mm});
            skArc(sketch, "E3352", {"start": v(-4783.12, -1374.07) * mm, "mid": v(-4780.21, -1373.75) * mm, "end": v(-4777.43, -1372.82) * mm});
            skArc(sketch, "E3353", {"start": v(-4816.83, -1372.82) * mm, "mid": v(-4814.05, -1373.75) * mm, "end": v(-4811.14, -1374.07) * mm});
            skArc(sketch, "E3354", {"start": v(-4828.53, -1403.5) * mm, "mid": v(-4826.13, -1402.5) * mm, "end": v(-4825.13, -1400.1) * mm});
            skArc(sketch, "E3355", {"start": v(-4867.13, -1400.1) * mm, "mid": v(-4866.14, -1402.5) * mm, "end": v(-4863.73, -1403.5) * mm});
            skArc(sketch, "E3356", {"start": v(-4863.73, -1365.5) * mm, "mid": v(-4866.14, -1366.49) * mm, "end": v(-4867.13, -1368.9) * mm});
            skArc(sketch, "E3357", {"start": v(-4825.13, -1368.9) * mm, "mid": v(-4826.13, -1366.49) * mm, "end": v(-4828.53, -1365.5) * mm});
            skArc(sketch, "E3358", {"start": v(-4015.73, -1860.5) * mm, "mid": v(-4018.14, -1861.49) * mm, "end": v(-4019.13, -1863.9) * mm});
            skArc(sketch, "E3359", {"start": v(-3977.13, -1863.9) * mm, "mid": v(-3978.13, -1861.49) * mm, "end": v(-3980.53, -1860.5) * mm});
            skArc(sketch, "E3360", {"start": v(-3980.53, -1898.5) * mm, "mid": v(-3978.13, -1897.5) * mm, "end": v(-3977.13, -1895.1) * mm});
            skArc(sketch, "E3361", {"start": v(-4019.13, -1895.1) * mm, "mid": v(-4018.14, -1897.5) * mm, "end": v(-4015.73, -1898.5) * mm});
            skArc(sketch, "E3362", {"start": v(-4033.12, -1869.07) * mm, "mid": v(-4030.21, -1868.75) * mm, "end": v(-4027.43, -1867.82) * mm});
            skArc(sketch, "E3363", {"start": v(-4066.83, -1867.82) * mm, "mid": v(-4064.05, -1868.75) * mm, "end": v(-4061.14, -1869.07) * mm});
            skArc(sketch, "E3364", {"start": v(-4027.43, -1891.17) * mm, "mid": v(-4030.21, -1890.23) * mm, "end": v(-4033.12, -1889.92) * mm});
            skArc(sketch, "E3365", {"start": v(-4061.14, -1889.92) * mm, "mid": v(-4064.05, -1890.23) * mm, "end": v(-4066.83, -1891.17) * mm});
            skArc(sketch, "E3366", {"start": v(-4075.13, -1863.9) * mm, "mid": v(-4076.13, -1861.49) * mm, "end": v(-4078.53, -1860.5) * mm});
            skArc(sketch, "E3367", {"start": v(-4113.73, -1860.5) * mm, "mid": v(-4116.14, -1861.49) * mm, "end": v(-4117.13, -1863.9) * mm});
            skArc(sketch, "E3368", {"start": v(-4117.13, -1895.1) * mm, "mid": v(-4116.14, -1897.5) * mm, "end": v(-4113.73, -1898.5) * mm});
            skArc(sketch, "E3369", {"start": v(-4078.53, -1898.5) * mm, "mid": v(-4076.13, -1897.5) * mm, "end": v(-4075.13, -1895.1) * mm});
            skArc(sketch, "E3370", {"start": v(-4019.13, -1400.1) * mm, "mid": v(-4018.14, -1402.5) * mm, "end": v(-4015.73, -1403.5) * mm});
            skArc(sketch, "E3371", {"start": v(-3980.53, -1403.5) * mm, "mid": v(-3978.13, -1402.5) * mm, "end": v(-3977.13, -1400.1) * mm});
            skArc(sketch, "E3372", {"start": v(-3977.13, -1368.9) * mm, "mid": v(-3978.13, -1366.49) * mm, "end": v(-3980.53, -1365.5) * mm});
            skArc(sketch, "E3373", {"start": v(-4015.73, -1365.5) * mm, "mid": v(-4018.14, -1366.49) * mm, "end": v(-4019.13, -1368.9) * mm});
            skArc(sketch, "E3374", {"start": v(-4027.43, -1396.17) * mm, "mid": v(-4030.21, -1395.23) * mm, "end": v(-4033.12, -1394.92) * mm});
            skArc(sketch, "E3375", {"start": v(-4061.14, -1394.92) * mm, "mid": v(-4064.05, -1395.23) * mm, "end": v(-4066.83, -1396.17) * mm});
            skArc(sketch, "E3376", {"start": v(-4033.12, -1374.07) * mm, "mid": v(-4030.21, -1373.75) * mm, "end": v(-4027.43, -1372.82) * mm});
            skArc(sketch, "E3377", {"start": v(-4066.83, -1372.82) * mm, "mid": v(-4064.05, -1373.75) * mm, "end": v(-4061.14, -1374.07) * mm});
            skArc(sketch, "E3378", {"start": v(-4078.53, -1403.5) * mm, "mid": v(-4076.13, -1402.5) * mm, "end": v(-4075.13, -1400.1) * mm});
            skArc(sketch, "E3379", {"start": v(-4117.13, -1400.1) * mm, "mid": v(-4116.14, -1402.5) * mm, "end": v(-4113.73, -1403.5) * mm});
            skArc(sketch, "E3380", {"start": v(-4113.73, -1365.5) * mm, "mid": v(-4116.14, -1366.49) * mm, "end": v(-4117.13, -1368.9) * mm});
            skArc(sketch, "E3381", {"start": v(-4075.13, -1368.9) * mm, "mid": v(-4076.13, -1366.49) * mm, "end": v(-4078.53, -1365.5) * mm});
            skArc(sketch, "E3382", {"start": v(-3265.73, -1860.5) * mm, "mid": v(-3268.14, -1861.49) * mm, "end": v(-3269.13, -1863.9) * mm});
            skArc(sketch, "E3383", {"start": v(-3227.13, -1863.9) * mm, "mid": v(-3228.13, -1861.49) * mm, "end": v(-3230.53, -1860.5) * mm});
            skArc(sketch, "E3384", {"start": v(-3230.53, -1898.5) * mm, "mid": v(-3228.13, -1897.5) * mm, "end": v(-3227.13, -1895.1) * mm});
            skArc(sketch, "E3385", {"start": v(-3269.13, -1895.1) * mm, "mid": v(-3268.14, -1897.5) * mm, "end": v(-3265.73, -1898.5) * mm});
            skArc(sketch, "E3386", {"start": v(-3283.12, -1869.07) * mm, "mid": v(-3280.21, -1868.75) * mm, "end": v(-3277.43, -1867.82) * mm});
            skArc(sketch, "E3387", {"start": v(-3316.83, -1867.82) * mm, "mid": v(-3314.05, -1868.75) * mm, "end": v(-3311.14, -1869.07) * mm});
            skArc(sketch, "E3388", {"start": v(-3277.43, -1891.17) * mm, "mid": v(-3280.21, -1890.23) * mm, "end": v(-3283.12, -1889.92) * mm});
            skArc(sketch, "E3389", {"start": v(-3311.14, -1889.92) * mm, "mid": v(-3314.05, -1890.23) * mm, "end": v(-3316.83, -1891.17) * mm});
            skArc(sketch, "E3390", {"start": v(-3325.13, -1863.9) * mm, "mid": v(-3326.13, -1861.49) * mm, "end": v(-3328.53, -1860.5) * mm});
            skArc(sketch, "E3391", {"start": v(-3363.73, -1860.5) * mm, "mid": v(-3366.14, -1861.49) * mm, "end": v(-3367.13, -1863.9) * mm});
            skArc(sketch, "E3392", {"start": v(-3367.13, -1895.1) * mm, "mid": v(-3366.14, -1897.5) * mm, "end": v(-3363.73, -1898.5) * mm});
            skArc(sketch, "E3393", {"start": v(-3328.53, -1898.5) * mm, "mid": v(-3326.13, -1897.5) * mm, "end": v(-3325.13, -1895.1) * mm});
            skArc(sketch, "E3394", {"start": v(-3269.13, -1400.1) * mm, "mid": v(-3268.14, -1402.5) * mm, "end": v(-3265.73, -1403.5) * mm});
            skArc(sketch, "E3395", {"start": v(-3230.53, -1403.5) * mm, "mid": v(-3228.13, -1402.5) * mm, "end": v(-3227.13, -1400.1) * mm});
            skArc(sketch, "E3396", {"start": v(-3227.13, -1368.9) * mm, "mid": v(-3228.13, -1366.49) * mm, "end": v(-3230.53, -1365.5) * mm});
            skArc(sketch, "E3397", {"start": v(-3265.73, -1365.5) * mm, "mid": v(-3268.14, -1366.49) * mm, "end": v(-3269.13, -1368.9) * mm});
            skArc(sketch, "E3398", {"start": v(-3277.43, -1396.17) * mm, "mid": v(-3280.21, -1395.23) * mm, "end": v(-3283.12, -1394.92) * mm});
            skArc(sketch, "E3399", {"start": v(-3311.14, -1394.92) * mm, "mid": v(-3314.05, -1395.23) * mm, "end": v(-3316.83, -1396.17) * mm});
            skArc(sketch, "E3400", {"start": v(-3283.12, -1374.07) * mm, "mid": v(-3280.21, -1373.75) * mm, "end": v(-3277.43, -1372.82) * mm});
            skArc(sketch, "E3401", {"start": v(-3316.83, -1372.82) * mm, "mid": v(-3314.05, -1373.75) * mm, "end": v(-3311.14, -1374.07) * mm});
            skArc(sketch, "E3402", {"start": v(-3328.53, -1403.5) * mm, "mid": v(-3326.13, -1402.5) * mm, "end": v(-3325.13, -1400.1) * mm});
            skArc(sketch, "E3403", {"start": v(-3367.13, -1400.1) * mm, "mid": v(-3366.14, -1402.5) * mm, "end": v(-3363.73, -1403.5) * mm});
            skArc(sketch, "E3404", {"start": v(-3363.73, -1365.5) * mm, "mid": v(-3366.14, -1366.49) * mm, "end": v(-3367.13, -1368.9) * mm});
            skArc(sketch, "E3405", {"start": v(-3325.13, -1368.9) * mm, "mid": v(-3326.13, -1366.49) * mm, "end": v(-3328.53, -1365.5) * mm});
            skArc(sketch, "E3406", {"start": v(-2515.73, -1860.5) * mm, "mid": v(-2518.14, -1861.49) * mm, "end": v(-2519.13, -1863.9) * mm});
            skArc(sketch, "E3407", {"start": v(-2477.13, -1863.9) * mm, "mid": v(-2478.13, -1861.49) * mm, "end": v(-2480.53, -1860.5) * mm});
            skArc(sketch, "E3408", {"start": v(-2480.53, -1898.5) * mm, "mid": v(-2478.13, -1897.5) * mm, "end": v(-2477.13, -1895.1) * mm});
            skArc(sketch, "E3409", {"start": v(-2519.13, -1895.1) * mm, "mid": v(-2518.14, -1897.5) * mm, "end": v(-2515.73, -1898.5) * mm});
            skArc(sketch, "E3410", {"start": v(-2533.12, -1869.07) * mm, "mid": v(-2530.21, -1868.75) * mm, "end": v(-2527.43, -1867.82) * mm});
            skArc(sketch, "E3411", {"start": v(-2566.83, -1867.82) * mm, "mid": v(-2564.05, -1868.75) * mm, "end": v(-2561.14, -1869.07) * mm});
            skArc(sketch, "E3412", {"start": v(-2527.43, -1891.17) * mm, "mid": v(-2530.21, -1890.23) * mm, "end": v(-2533.12, -1889.92) * mm});
            skArc(sketch, "E3413", {"start": v(-2561.14, -1889.92) * mm, "mid": v(-2564.05, -1890.23) * mm, "end": v(-2566.83, -1891.17) * mm});
            skArc(sketch, "E3414", {"start": v(-2575.13, -1863.9) * mm, "mid": v(-2576.13, -1861.49) * mm, "end": v(-2578.53, -1860.5) * mm});
            skArc(sketch, "E3415", {"start": v(-2613.73, -1860.5) * mm, "mid": v(-2616.14, -1861.49) * mm, "end": v(-2617.13, -1863.9) * mm});
            skArc(sketch, "E3416", {"start": v(-2617.13, -1895.1) * mm, "mid": v(-2616.14, -1897.5) * mm, "end": v(-2613.73, -1898.5) * mm});
            skArc(sketch, "E3417", {"start": v(-2578.53, -1898.5) * mm, "mid": v(-2576.13, -1897.5) * mm, "end": v(-2575.13, -1895.1) * mm});
            skArc(sketch, "E3418", {"start": v(-2519.13, -1400.1) * mm, "mid": v(-2518.14, -1402.5) * mm, "end": v(-2515.73, -1403.5) * mm});
            skArc(sketch, "E3419", {"start": v(-2480.53, -1403.5) * mm, "mid": v(-2478.13, -1402.5) * mm, "end": v(-2477.13, -1400.1) * mm});
            skArc(sketch, "E3420", {"start": v(-2477.13, -1368.9) * mm, "mid": v(-2478.13, -1366.49) * mm, "end": v(-2480.53, -1365.5) * mm});
            skArc(sketch, "E3421", {"start": v(-2515.73, -1365.5) * mm, "mid": v(-2518.14, -1366.49) * mm, "end": v(-2519.13, -1368.9) * mm});
            skArc(sketch, "E3422", {"start": v(-2527.43, -1396.17) * mm, "mid": v(-2530.21, -1395.23) * mm, "end": v(-2533.12, -1394.92) * mm});
            skArc(sketch, "E3423", {"start": v(-2561.14, -1394.92) * mm, "mid": v(-2564.05, -1395.23) * mm, "end": v(-2566.83, -1396.17) * mm});
            skArc(sketch, "E3424", {"start": v(-2533.12, -1374.07) * mm, "mid": v(-2530.21, -1373.75) * mm, "end": v(-2527.43, -1372.82) * mm});
            skArc(sketch, "E3425", {"start": v(-2566.83, -1372.82) * mm, "mid": v(-2564.05, -1373.75) * mm, "end": v(-2561.14, -1374.07) * mm});
            skArc(sketch, "E3426", {"start": v(-2578.53, -1403.5) * mm, "mid": v(-2576.13, -1402.5) * mm, "end": v(-2575.13, -1400.1) * mm});
            skArc(sketch, "E3427", {"start": v(-2617.13, -1400.1) * mm, "mid": v(-2616.14, -1402.5) * mm, "end": v(-2613.73, -1403.5) * mm});
            skArc(sketch, "E3428", {"start": v(-2613.73, -1365.5) * mm, "mid": v(-2616.14, -1366.49) * mm, "end": v(-2617.13, -1368.9) * mm});
            skArc(sketch, "E3429", {"start": v(-2575.13, -1368.9) * mm, "mid": v(-2576.13, -1366.49) * mm, "end": v(-2578.53, -1365.5) * mm});
            skArc(sketch, "E3430", {"start": v(-1765.73, -1860.5) * mm, "mid": v(-1768.14, -1861.49) * mm, "end": v(-1769.13, -1863.9) * mm});
            skArc(sketch, "E3431", {"start": v(-1727.13, -1863.9) * mm, "mid": v(-1728.13, -1861.49) * mm, "end": v(-1730.53, -1860.5) * mm});
            skArc(sketch, "E3432", {"start": v(-1730.53, -1898.5) * mm, "mid": v(-1728.13, -1897.5) * mm, "end": v(-1727.13, -1895.1) * mm});
            skArc(sketch, "E3433", {"start": v(-1769.13, -1895.1) * mm, "mid": v(-1768.14, -1897.5) * mm, "end": v(-1765.73, -1898.5) * mm});
            skArc(sketch, "E3434", {"start": v(-1783.12, -1869.07) * mm, "mid": v(-1780.21, -1868.75) * mm, "end": v(-1777.43, -1867.82) * mm});
            skArc(sketch, "E3435", {"start": v(-1816.83, -1867.82) * mm, "mid": v(-1814.05, -1868.75) * mm, "end": v(-1811.14, -1869.07) * mm});
            skArc(sketch, "E3436", {"start": v(-1777.43, -1891.17) * mm, "mid": v(-1780.21, -1890.23) * mm, "end": v(-1783.12, -1889.92) * mm});
            skArc(sketch, "E3437", {"start": v(-1811.14, -1889.92) * mm, "mid": v(-1814.05, -1890.23) * mm, "end": v(-1816.83, -1891.17) * mm});
            skArc(sketch, "E3438", {"start": v(-1825.13, -1863.9) * mm, "mid": v(-1826.13, -1861.49) * mm, "end": v(-1828.53, -1860.5) * mm});
            skArc(sketch, "E3439", {"start": v(-1863.73, -1860.5) * mm, "mid": v(-1866.14, -1861.49) * mm, "end": v(-1867.13, -1863.9) * mm});
            skArc(sketch, "E3440", {"start": v(-1867.13, -1895.1) * mm, "mid": v(-1866.14, -1897.5) * mm, "end": v(-1863.73, -1898.5) * mm});
            skArc(sketch, "E3441", {"start": v(-1828.53, -1898.5) * mm, "mid": v(-1826.13, -1897.5) * mm, "end": v(-1825.13, -1895.1) * mm});
            skArc(sketch, "E3442", {"start": v(-1769.13, -1400.1) * mm, "mid": v(-1768.14, -1402.5) * mm, "end": v(-1765.73, -1403.5) * mm});
            skArc(sketch, "E3443", {"start": v(-1730.53, -1403.5) * mm, "mid": v(-1728.13, -1402.5) * mm, "end": v(-1727.13, -1400.1) * mm});
            skArc(sketch, "E3444", {"start": v(-1727.13, -1368.9) * mm, "mid": v(-1728.13, -1366.49) * mm, "end": v(-1730.53, -1365.5) * mm});
            skArc(sketch, "E3445", {"start": v(-1765.73, -1365.5) * mm, "mid": v(-1768.14, -1366.49) * mm, "end": v(-1769.13, -1368.9) * mm});
            skArc(sketch, "E3446", {"start": v(-1777.43, -1396.17) * mm, "mid": v(-1780.21, -1395.23) * mm, "end": v(-1783.12, -1394.92) * mm});
            skArc(sketch, "E3447", {"start": v(-1811.14, -1394.92) * mm, "mid": v(-1814.05, -1395.23) * mm, "end": v(-1816.83, -1396.17) * mm});
            skArc(sketch, "E3448", {"start": v(-1783.12, -1374.07) * mm, "mid": v(-1780.21, -1373.75) * mm, "end": v(-1777.43, -1372.82) * mm});
            skArc(sketch, "E3449", {"start": v(-1816.83, -1372.82) * mm, "mid": v(-1814.05, -1373.75) * mm, "end": v(-1811.14, -1374.07) * mm});
            skArc(sketch, "E3450", {"start": v(-1828.53, -1403.5) * mm, "mid": v(-1826.13, -1402.5) * mm, "end": v(-1825.13, -1400.1) * mm});
            skArc(sketch, "E3451", {"start": v(-1867.13, -1400.1) * mm, "mid": v(-1866.14, -1402.5) * mm, "end": v(-1863.73, -1403.5) * mm});
            skArc(sketch, "E3452", {"start": v(-1863.73, -1365.5) * mm, "mid": v(-1866.14, -1366.49) * mm, "end": v(-1867.13, -1368.9) * mm});
            skArc(sketch, "E3453", {"start": v(-1825.13, -1368.9) * mm, "mid": v(-1826.13, -1366.49) * mm, "end": v(-1828.53, -1365.5) * mm});
            skArc(sketch, "E3454", {"start": v(-1015.73, -1860.5) * mm, "mid": v(-1018.14, -1861.49) * mm, "end": v(-1019.13, -1863.9) * mm});
            skArc(sketch, "E3455", {"start": v(-977.13, -1863.9) * mm, "mid": v(-978.13, -1861.49) * mm, "end": v(-980.53, -1860.5) * mm});
            skArc(sketch, "E3456", {"start": v(-980.53, -1898.5) * mm, "mid": v(-978.13, -1897.5) * mm, "end": v(-977.13, -1895.1) * mm});
            skArc(sketch, "E3457", {"start": v(-1019.13, -1895.1) * mm, "mid": v(-1018.14, -1897.5) * mm, "end": v(-1015.73, -1898.5) * mm});
            skArc(sketch, "E3458", {"start": v(-1033.12, -1869.07) * mm, "mid": v(-1030.21, -1868.75) * mm, "end": v(-1027.43, -1867.82) * mm});
            skArc(sketch, "E3459", {"start": v(-1066.83, -1867.82) * mm, "mid": v(-1064.05, -1868.75) * mm, "end": v(-1061.14, -1869.07) * mm});
            skArc(sketch, "E3460", {"start": v(-1027.43, -1891.17) * mm, "mid": v(-1030.21, -1890.23) * mm, "end": v(-1033.12, -1889.92) * mm});
            skArc(sketch, "E3461", {"start": v(-1061.14, -1889.92) * mm, "mid": v(-1064.05, -1890.23) * mm, "end": v(-1066.83, -1891.17) * mm});
            skArc(sketch, "E3462", {"start": v(-1075.13, -1863.9) * mm, "mid": v(-1076.13, -1861.49) * mm, "end": v(-1078.53, -1860.5) * mm});
            skArc(sketch, "E3463", {"start": v(-1113.73, -1860.5) * mm, "mid": v(-1116.14, -1861.49) * mm, "end": v(-1117.13, -1863.9) * mm});
            skArc(sketch, "E3464", {"start": v(-1117.13, -1895.1) * mm, "mid": v(-1116.14, -1897.5) * mm, "end": v(-1113.73, -1898.5) * mm});
            skArc(sketch, "E3465", {"start": v(-1078.53, -1898.5) * mm, "mid": v(-1076.13, -1897.5) * mm, "end": v(-1075.13, -1895.1) * mm});
            skArc(sketch, "E3466", {"start": v(-1019.13, -1400.1) * mm, "mid": v(-1018.14, -1402.5) * mm, "end": v(-1015.73, -1403.5) * mm});
            skArc(sketch, "E3467", {"start": v(-980.53, -1403.5) * mm, "mid": v(-978.13, -1402.5) * mm, "end": v(-977.13, -1400.1) * mm});
            skArc(sketch, "E3468", {"start": v(-977.13, -1368.9) * mm, "mid": v(-978.13, -1366.49) * mm, "end": v(-980.53, -1365.5) * mm});
            skArc(sketch, "E3469", {"start": v(-1015.73, -1365.5) * mm, "mid": v(-1018.14, -1366.49) * mm, "end": v(-1019.13, -1368.9) * mm});
            skArc(sketch, "E3470", {"start": v(-1027.43, -1396.17) * mm, "mid": v(-1030.21, -1395.23) * mm, "end": v(-1033.12, -1394.92) * mm});
            skArc(sketch, "E3471", {"start": v(-1061.14, -1394.92) * mm, "mid": v(-1064.05, -1395.23) * mm, "end": v(-1066.83, -1396.17) * mm});
            skArc(sketch, "E3472", {"start": v(-1033.12, -1374.07) * mm, "mid": v(-1030.21, -1373.75) * mm, "end": v(-1027.43, -1372.82) * mm});
            skArc(sketch, "E3473", {"start": v(-1066.83, -1372.82) * mm, "mid": v(-1064.05, -1373.75) * mm, "end": v(-1061.14, -1374.07) * mm});
            skArc(sketch, "E3474", {"start": v(-1078.53, -1403.5) * mm, "mid": v(-1076.13, -1402.5) * mm, "end": v(-1075.13, -1400.1) * mm});
            skArc(sketch, "E3475", {"start": v(-1117.13, -1400.1) * mm, "mid": v(-1116.14, -1402.5) * mm, "end": v(-1113.73, -1403.5) * mm});
            skArc(sketch, "E3476", {"start": v(-1113.73, -1365.5) * mm, "mid": v(-1116.14, -1366.49) * mm, "end": v(-1117.13, -1368.9) * mm});
            skArc(sketch, "E3477", {"start": v(-1075.13, -1368.9) * mm, "mid": v(-1076.13, -1366.49) * mm, "end": v(-1078.53, -1365.5) * mm});
            skArc(sketch, "E3478", {"start": v(-265.73, -1860.5) * mm, "mid": v(-268.14, -1861.49) * mm, "end": v(-269.13, -1863.9) * mm});
            skArc(sketch, "E3479", {"start": v(-227.13, -1863.9) * mm, "mid": v(-228.13, -1861.49) * mm, "end": v(-230.53, -1860.5) * mm});
            skArc(sketch, "E3480", {"start": v(-230.53, -1898.5) * mm, "mid": v(-228.13, -1897.5) * mm, "end": v(-227.13, -1895.1) * mm});
            skArc(sketch, "E3481", {"start": v(-269.13, -1895.1) * mm, "mid": v(-268.14, -1897.5) * mm, "end": v(-265.73, -1898.5) * mm});
            skArc(sketch, "E3482", {"start": v(-283.12, -1869.07) * mm, "mid": v(-280.21, -1868.75) * mm, "end": v(-277.43, -1867.82) * mm});
            skArc(sketch, "E3483", {"start": v(-316.83, -1867.82) * mm, "mid": v(-314.05, -1868.75) * mm, "end": v(-311.14, -1869.07) * mm});
            skArc(sketch, "E3484", {"start": v(-277.43, -1891.17) * mm, "mid": v(-280.21, -1890.23) * mm, "end": v(-283.12, -1889.92) * mm});
            skArc(sketch, "E3485", {"start": v(-311.14, -1889.92) * mm, "mid": v(-314.05, -1890.23) * mm, "end": v(-316.83, -1891.17) * mm});
            skArc(sketch, "E3486", {"start": v(-325.13, -1863.9) * mm, "mid": v(-326.13, -1861.49) * mm, "end": v(-328.53, -1860.5) * mm});
            skArc(sketch, "E3487", {"start": v(-363.73, -1860.5) * mm, "mid": v(-366.14, -1861.49) * mm, "end": v(-367.13, -1863.9) * mm});
            skArc(sketch, "E3488", {"start": v(-367.13, -1895.1) * mm, "mid": v(-366.14, -1897.5) * mm, "end": v(-363.73, -1898.5) * mm});
            skArc(sketch, "E3489", {"start": v(-328.53, -1898.5) * mm, "mid": v(-326.13, -1897.5) * mm, "end": v(-325.13, -1895.1) * mm});
            skArc(sketch, "E3490", {"start": v(-269.13, -1400.1) * mm, "mid": v(-268.14, -1402.5) * mm, "end": v(-265.73, -1403.5) * mm});
            skArc(sketch, "E3491", {"start": v(-230.53, -1403.5) * mm, "mid": v(-228.13, -1402.5) * mm, "end": v(-227.13, -1400.1) * mm});
            skArc(sketch, "E3492", {"start": v(-227.13, -1368.9) * mm, "mid": v(-228.13, -1366.49) * mm, "end": v(-230.53, -1365.5) * mm});
            skArc(sketch, "E3493", {"start": v(-265.73, -1365.5) * mm, "mid": v(-268.14, -1366.49) * mm, "end": v(-269.13, -1368.9) * mm});
            skArc(sketch, "E3494", {"start": v(-277.43, -1396.17) * mm, "mid": v(-280.21, -1395.23) * mm, "end": v(-283.12, -1394.92) * mm});
            skArc(sketch, "E3495", {"start": v(-311.14, -1394.92) * mm, "mid": v(-314.05, -1395.23) * mm, "end": v(-316.83, -1396.17) * mm});
            skArc(sketch, "E3496", {"start": v(-283.12, -1374.07) * mm, "mid": v(-280.21, -1373.75) * mm, "end": v(-277.43, -1372.82) * mm});
            skArc(sketch, "E3497", {"start": v(-316.83, -1372.82) * mm, "mid": v(-314.05, -1373.75) * mm, "end": v(-311.14, -1374.07) * mm});
            skArc(sketch, "E3498", {"start": v(-328.53, -1403.5) * mm, "mid": v(-326.13, -1402.5) * mm, "end": v(-325.13, -1400.1) * mm});
            skArc(sketch, "E3499", {"start": v(-367.13, -1400.1) * mm, "mid": v(-366.14, -1402.5) * mm, "end": v(-363.73, -1403.5) * mm});
            skArc(sketch, "E3500", {"start": v(-363.73, -1365.5) * mm, "mid": v(-366.14, -1366.49) * mm, "end": v(-367.13, -1368.9) * mm});
            skArc(sketch, "E3501", {"start": v(-325.13, -1368.9) * mm, "mid": v(-326.13, -1366.49) * mm, "end": v(-328.53, -1365.5) * mm});
            skArc(sketch, "E3502", {"start": v(484.27, -1860.5) * mm, "mid": v(481.86, -1861.49) * mm, "end": v(480.87, -1863.9) * mm});
            skArc(sketch, "E3503", {"start": v(522.87, -1863.9) * mm, "mid": v(521.87, -1861.49) * mm, "end": v(519.47, -1860.5) * mm});
            skArc(sketch, "E3504", {"start": v(519.47, -1898.5) * mm, "mid": v(521.87, -1897.5) * mm, "end": v(522.87, -1895.1) * mm});
            skArc(sketch, "E3505", {"start": v(480.87, -1895.1) * mm, "mid": v(481.86, -1897.5) * mm, "end": v(484.27, -1898.5) * mm});
            skArc(sketch, "E3506", {"start": v(466.88, -1869.07) * mm, "mid": v(469.79, -1868.75) * mm, "end": v(472.57, -1867.82) * mm});
            skArc(sketch, "E3507", {"start": v(433.17, -1867.82) * mm, "mid": v(435.95, -1868.75) * mm, "end": v(438.86, -1869.07) * mm});
            skArc(sketch, "E3508", {"start": v(472.57, -1891.17) * mm, "mid": v(469.79, -1890.23) * mm, "end": v(466.88, -1889.92) * mm});
            skArc(sketch, "E3509", {"start": v(438.86, -1889.92) * mm, "mid": v(435.95, -1890.23) * mm, "end": v(433.17, -1891.17) * mm});
            skArc(sketch, "E3510", {"start": v(424.87, -1863.9) * mm, "mid": v(423.87, -1861.49) * mm, "end": v(421.47, -1860.5) * mm});
            skArc(sketch, "E3511", {"start": v(386.27, -1860.5) * mm, "mid": v(383.86, -1861.49) * mm, "end": v(382.87, -1863.9) * mm});
            skArc(sketch, "E3512", {"start": v(382.87, -1895.1) * mm, "mid": v(383.86, -1897.5) * mm, "end": v(386.27, -1898.5) * mm});
            skArc(sketch, "E3513", {"start": v(421.47, -1898.5) * mm, "mid": v(423.87, -1897.5) * mm, "end": v(424.87, -1895.1) * mm});
            skArc(sketch, "E3514", {"start": v(480.87, -1400.1) * mm, "mid": v(481.86, -1402.5) * mm, "end": v(484.27, -1403.5) * mm});
            skArc(sketch, "E3515", {"start": v(519.47, -1403.5) * mm, "mid": v(521.87, -1402.5) * mm, "end": v(522.87, -1400.1) * mm});
            skArc(sketch, "E3516", {"start": v(522.87, -1368.9) * mm, "mid": v(521.87, -1366.49) * mm, "end": v(519.47, -1365.5) * mm});
            skArc(sketch, "E3517", {"start": v(484.27, -1365.5) * mm, "mid": v(481.86, -1366.49) * mm, "end": v(480.87, -1368.9) * mm});
            skArc(sketch, "E3518", {"start": v(472.57, -1396.17) * mm, "mid": v(469.79, -1395.23) * mm, "end": v(466.88, -1394.92) * mm});
            skArc(sketch, "E3519", {"start": v(438.86, -1394.92) * mm, "mid": v(435.95, -1395.23) * mm, "end": v(433.17, -1396.17) * mm});
            skArc(sketch, "E3520", {"start": v(466.88, -1374.07) * mm, "mid": v(469.79, -1373.75) * mm, "end": v(472.57, -1372.82) * mm});
            skArc(sketch, "E3521", {"start": v(433.17, -1372.82) * mm, "mid": v(435.95, -1373.75) * mm, "end": v(438.86, -1374.07) * mm});
            skArc(sketch, "E3522", {"start": v(421.47, -1403.5) * mm, "mid": v(423.87, -1402.5) * mm, "end": v(424.87, -1400.1) * mm});
            skArc(sketch, "E3523", {"start": v(382.87, -1400.1) * mm, "mid": v(383.86, -1402.5) * mm, "end": v(386.27, -1403.5) * mm});
            skArc(sketch, "E3524", {"start": v(386.27, -1365.5) * mm, "mid": v(383.86, -1366.49) * mm, "end": v(382.87, -1368.9) * mm});
            skArc(sketch, "E3525", {"start": v(424.87, -1368.9) * mm, "mid": v(423.87, -1366.49) * mm, "end": v(421.47, -1365.5) * mm});
            skArc(sketch, "E3526", {"start": v(1234.27, -1860.5) * mm, "mid": v(1231.86, -1861.49) * mm, "end": v(1230.87, -1863.9) * mm});
            skArc(sketch, "E3527", {"start": v(1272.87, -1863.9) * mm, "mid": v(1271.87, -1861.49) * mm, "end": v(1269.47, -1860.5) * mm});
            skArc(sketch, "E3528", {"start": v(1269.47, -1898.5) * mm, "mid": v(1271.87, -1897.5) * mm, "end": v(1272.87, -1895.1) * mm});
            skArc(sketch, "E3529", {"start": v(1230.87, -1895.1) * mm, "mid": v(1231.86, -1897.5) * mm, "end": v(1234.27, -1898.5) * mm});
            skArc(sketch, "E3530", {"start": v(1216.88, -1869.07) * mm, "mid": v(1219.79, -1868.75) * mm, "end": v(1222.57, -1867.82) * mm});
            skArc(sketch, "E3531", {"start": v(1183.17, -1867.82) * mm, "mid": v(1185.95, -1868.75) * mm, "end": v(1188.86, -1869.07) * mm});
            skArc(sketch, "E3532", {"start": v(1222.57, -1891.17) * mm, "mid": v(1219.79, -1890.23) * mm, "end": v(1216.88, -1889.92) * mm});
            skArc(sketch, "E3533", {"start": v(1188.86, -1889.92) * mm, "mid": v(1185.95, -1890.23) * mm, "end": v(1183.17, -1891.17) * mm});
            skArc(sketch, "E3534", {"start": v(1174.87, -1863.9) * mm, "mid": v(1173.87, -1861.49) * mm, "end": v(1171.47, -1860.5) * mm});
            skArc(sketch, "E3535", {"start": v(1136.27, -1860.5) * mm, "mid": v(1133.86, -1861.49) * mm, "end": v(1132.87, -1863.9) * mm});
            skArc(sketch, "E3536", {"start": v(1132.87, -1895.1) * mm, "mid": v(1133.86, -1897.5) * mm, "end": v(1136.27, -1898.5) * mm});
            skArc(sketch, "E3537", {"start": v(1171.47, -1898.5) * mm, "mid": v(1173.87, -1897.5) * mm, "end": v(1174.87, -1895.1) * mm});
            skArc(sketch, "E3538", {"start": v(1230.87, -1400.1) * mm, "mid": v(1231.86, -1402.5) * mm, "end": v(1234.27, -1403.5) * mm});
            skArc(sketch, "E3539", {"start": v(1269.47, -1403.5) * mm, "mid": v(1271.87, -1402.5) * mm, "end": v(1272.87, -1400.1) * mm});
            skArc(sketch, "E3540", {"start": v(1272.87, -1368.9) * mm, "mid": v(1271.87, -1366.49) * mm, "end": v(1269.47, -1365.5) * mm});
            skArc(sketch, "E3541", {"start": v(1234.27, -1365.5) * mm, "mid": v(1231.86, -1366.49) * mm, "end": v(1230.87, -1368.9) * mm});
            skArc(sketch, "E3542", {"start": v(1222.57, -1396.17) * mm, "mid": v(1219.79, -1395.23) * mm, "end": v(1216.88, -1394.92) * mm});
            skArc(sketch, "E3543", {"start": v(1188.86, -1394.92) * mm, "mid": v(1185.95, -1395.23) * mm, "end": v(1183.17, -1396.17) * mm});
            skArc(sketch, "E3544", {"start": v(1216.88, -1374.07) * mm, "mid": v(1219.79, -1373.75) * mm, "end": v(1222.57, -1372.82) * mm});
            skArc(sketch, "E3545", {"start": v(1183.17, -1372.82) * mm, "mid": v(1185.95, -1373.75) * mm, "end": v(1188.86, -1374.07) * mm});
            skArc(sketch, "E3546", {"start": v(1171.47, -1403.5) * mm, "mid": v(1173.87, -1402.5) * mm, "end": v(1174.87, -1400.1) * mm});
            skArc(sketch, "E3547", {"start": v(1132.87, -1400.1) * mm, "mid": v(1133.86, -1402.5) * mm, "end": v(1136.27, -1403.5) * mm});
            skArc(sketch, "E3548", {"start": v(1136.27, -1365.5) * mm, "mid": v(1133.86, -1366.49) * mm, "end": v(1132.87, -1368.9) * mm});
            skArc(sketch, "E3549", {"start": v(1174.87, -1368.9) * mm, "mid": v(1173.87, -1366.49) * mm, "end": v(1171.47, -1365.5) * mm});
            skArc(sketch, "E3550", {"start": v(1984.27, -1860.5) * mm, "mid": v(1981.86, -1861.49) * mm, "end": v(1980.87, -1863.9) * mm});
            skArc(sketch, "E3551", {"start": v(2022.87, -1863.9) * mm, "mid": v(2021.87, -1861.49) * mm, "end": v(2019.47, -1860.5) * mm});
            skArc(sketch, "E3552", {"start": v(2019.47, -1898.5) * mm, "mid": v(2021.87, -1897.5) * mm, "end": v(2022.87, -1895.1) * mm});
            skArc(sketch, "E3553", {"start": v(1980.87, -1895.1) * mm, "mid": v(1981.86, -1897.5) * mm, "end": v(1984.27, -1898.5) * mm});
            skArc(sketch, "E3554", {"start": v(1966.88, -1869.07) * mm, "mid": v(1969.79, -1868.75) * mm, "end": v(1972.57, -1867.82) * mm});
            skArc(sketch, "E3555", {"start": v(1933.17, -1867.82) * mm, "mid": v(1935.95, -1868.75) * mm, "end": v(1938.86, -1869.07) * mm});
            skArc(sketch, "E3556", {"start": v(1972.57, -1891.17) * mm, "mid": v(1969.79, -1890.23) * mm, "end": v(1966.88, -1889.92) * mm});
            skArc(sketch, "E3557", {"start": v(1938.86, -1889.92) * mm, "mid": v(1935.95, -1890.23) * mm, "end": v(1933.17, -1891.17) * mm});
            skArc(sketch, "E3558", {"start": v(1924.87, -1863.9) * mm, "mid": v(1923.87, -1861.49) * mm, "end": v(1921.47, -1860.5) * mm});
            skArc(sketch, "E3559", {"start": v(1886.27, -1860.5) * mm, "mid": v(1883.86, -1861.49) * mm, "end": v(1882.87, -1863.9) * mm});
            skArc(sketch, "E3560", {"start": v(1882.87, -1895.1) * mm, "mid": v(1883.86, -1897.5) * mm, "end": v(1886.27, -1898.5) * mm});
            skArc(sketch, "E3561", {"start": v(1921.47, -1898.5) * mm, "mid": v(1923.87, -1897.5) * mm, "end": v(1924.87, -1895.1) * mm});
            skArc(sketch, "E3562", {"start": v(1980.87, -1400.1) * mm, "mid": v(1981.86, -1402.5) * mm, "end": v(1984.27, -1403.5) * mm});
            skArc(sketch, "E3563", {"start": v(2019.47, -1403.5) * mm, "mid": v(2021.87, -1402.5) * mm, "end": v(2022.87, -1400.1) * mm});
            skArc(sketch, "E3564", {"start": v(2022.87, -1368.9) * mm, "mid": v(2021.87, -1366.49) * mm, "end": v(2019.47, -1365.5) * mm});
            skArc(sketch, "E3565", {"start": v(1984.27, -1365.5) * mm, "mid": v(1981.86, -1366.49) * mm, "end": v(1980.87, -1368.9) * mm});
            skArc(sketch, "E3566", {"start": v(1972.57, -1396.17) * mm, "mid": v(1969.79, -1395.23) * mm, "end": v(1966.88, -1394.92) * mm});
            skArc(sketch, "E3567", {"start": v(1938.86, -1394.92) * mm, "mid": v(1935.95, -1395.23) * mm, "end": v(1933.17, -1396.17) * mm});
            skArc(sketch, "E3568", {"start": v(1966.88, -1374.07) * mm, "mid": v(1969.79, -1373.75) * mm, "end": v(1972.57, -1372.82) * mm});
            skArc(sketch, "E3569", {"start": v(1933.17, -1372.82) * mm, "mid": v(1935.95, -1373.75) * mm, "end": v(1938.86, -1374.07) * mm});
            skArc(sketch, "E3570", {"start": v(1921.47, -1403.5) * mm, "mid": v(1923.87, -1402.5) * mm, "end": v(1924.87, -1400.1) * mm});
            skArc(sketch, "E3571", {"start": v(1882.87, -1400.1) * mm, "mid": v(1883.86, -1402.5) * mm, "end": v(1886.27, -1403.5) * mm});
            skArc(sketch, "E3572", {"start": v(1886.27, -1365.5) * mm, "mid": v(1883.86, -1366.49) * mm, "end": v(1882.87, -1368.9) * mm});
            skArc(sketch, "E3573", {"start": v(1924.87, -1368.9) * mm, "mid": v(1923.87, -1366.49) * mm, "end": v(1921.47, -1365.5) * mm});
            skArc(sketch, "E3574", {"start": v(2734.27, -1860.5) * mm, "mid": v(2731.86, -1861.49) * mm, "end": v(2730.87, -1863.9) * mm});
            skArc(sketch, "E3575", {"start": v(2772.87, -1863.9) * mm, "mid": v(2771.87, -1861.49) * mm, "end": v(2769.47, -1860.5) * mm});
            skArc(sketch, "E3576", {"start": v(2769.47, -1898.5) * mm, "mid": v(2771.87, -1897.5) * mm, "end": v(2772.87, -1895.1) * mm});
            skArc(sketch, "E3577", {"start": v(2730.87, -1895.1) * mm, "mid": v(2731.86, -1897.5) * mm, "end": v(2734.27, -1898.5) * mm});
            skArc(sketch, "E3578", {"start": v(2716.88, -1869.07) * mm, "mid": v(2719.79, -1868.75) * mm, "end": v(2722.57, -1867.82) * mm});
            skArc(sketch, "E3579", {"start": v(2683.17, -1867.82) * mm, "mid": v(2685.95, -1868.75) * mm, "end": v(2688.86, -1869.07) * mm});
            skArc(sketch, "E3580", {"start": v(2722.57, -1891.17) * mm, "mid": v(2719.79, -1890.23) * mm, "end": v(2716.88, -1889.92) * mm});
            skArc(sketch, "E3581", {"start": v(2688.86, -1889.92) * mm, "mid": v(2685.95, -1890.23) * mm, "end": v(2683.17, -1891.17) * mm});
            skArc(sketch, "E3582", {"start": v(2674.87, -1863.9) * mm, "mid": v(2673.87, -1861.49) * mm, "end": v(2671.47, -1860.5) * mm});
            skArc(sketch, "E3583", {"start": v(2636.27, -1860.5) * mm, "mid": v(2633.86, -1861.49) * mm, "end": v(2632.87, -1863.9) * mm});
            skArc(sketch, "E3584", {"start": v(2632.87, -1895.1) * mm, "mid": v(2633.86, -1897.5) * mm, "end": v(2636.27, -1898.5) * mm});
            skArc(sketch, "E3585", {"start": v(2671.47, -1898.5) * mm, "mid": v(2673.87, -1897.5) * mm, "end": v(2674.87, -1895.1) * mm});
            skArc(sketch, "E3586", {"start": v(2730.87, -1400.1) * mm, "mid": v(2731.86, -1402.5) * mm, "end": v(2734.27, -1403.5) * mm});
            skArc(sketch, "E3587", {"start": v(2769.47, -1403.5) * mm, "mid": v(2771.87, -1402.5) * mm, "end": v(2772.87, -1400.1) * mm});
            skArc(sketch, "E3588", {"start": v(2772.87, -1368.9) * mm, "mid": v(2771.87, -1366.49) * mm, "end": v(2769.47, -1365.5) * mm});
            skArc(sketch, "E3589", {"start": v(2734.27, -1365.5) * mm, "mid": v(2731.86, -1366.49) * mm, "end": v(2730.87, -1368.9) * mm});
            skArc(sketch, "E3590", {"start": v(2722.57, -1396.17) * mm, "mid": v(2719.79, -1395.23) * mm, "end": v(2716.88, -1394.92) * mm});
            skArc(sketch, "E3591", {"start": v(2688.86, -1394.92) * mm, "mid": v(2685.95, -1395.23) * mm, "end": v(2683.17, -1396.17) * mm});
            skArc(sketch, "E3592", {"start": v(2716.88, -1374.07) * mm, "mid": v(2719.79, -1373.75) * mm, "end": v(2722.57, -1372.82) * mm});
            skArc(sketch, "E3593", {"start": v(2683.17, -1372.82) * mm, "mid": v(2685.95, -1373.75) * mm, "end": v(2688.86, -1374.07) * mm});
            skArc(sketch, "E3594", {"start": v(2671.47, -1403.5) * mm, "mid": v(2673.87, -1402.5) * mm, "end": v(2674.87, -1400.1) * mm});
            skArc(sketch, "E3595", {"start": v(2632.87, -1400.1) * mm, "mid": v(2633.86, -1402.5) * mm, "end": v(2636.27, -1403.5) * mm});
            skArc(sketch, "E3596", {"start": v(2636.27, -1365.5) * mm, "mid": v(2633.86, -1366.49) * mm, "end": v(2632.87, -1368.9) * mm});
            skArc(sketch, "E3597", {"start": v(2674.87, -1368.9) * mm, "mid": v(2673.87, -1366.49) * mm, "end": v(2671.47, -1365.5) * mm});
            skArc(sketch, "E3598", {"start": v(3484.27, -1860.5) * mm, "mid": v(3481.86, -1861.49) * mm, "end": v(3480.87, -1863.9) * mm});
            skArc(sketch, "E3599", {"start": v(3522.87, -1863.9) * mm, "mid": v(3521.87, -1861.49) * mm, "end": v(3519.47, -1860.5) * mm});
            skArc(sketch, "E3600", {"start": v(3519.47, -1898.5) * mm, "mid": v(3521.87, -1897.5) * mm, "end": v(3522.87, -1895.1) * mm});
            skArc(sketch, "E3601", {"start": v(3480.87, -1895.1) * mm, "mid": v(3481.86, -1897.5) * mm, "end": v(3484.27, -1898.5) * mm});
            skArc(sketch, "E3602", {"start": v(3466.88, -1869.07) * mm, "mid": v(3469.79, -1868.75) * mm, "end": v(3472.57, -1867.82) * mm});
            skArc(sketch, "E3603", {"start": v(3433.17, -1867.82) * mm, "mid": v(3435.95, -1868.75) * mm, "end": v(3438.86, -1869.07) * mm});
            skArc(sketch, "E3604", {"start": v(3472.57, -1891.17) * mm, "mid": v(3469.79, -1890.23) * mm, "end": v(3466.88, -1889.92) * mm});
            skArc(sketch, "E3605", {"start": v(3438.86, -1889.92) * mm, "mid": v(3435.95, -1890.23) * mm, "end": v(3433.17, -1891.17) * mm});
            skArc(sketch, "E3606", {"start": v(3424.87, -1863.9) * mm, "mid": v(3423.87, -1861.49) * mm, "end": v(3421.47, -1860.5) * mm});
            skArc(sketch, "E3607", {"start": v(3386.27, -1860.5) * mm, "mid": v(3383.86, -1861.49) * mm, "end": v(3382.87, -1863.9) * mm});
            skArc(sketch, "E3608", {"start": v(3382.87, -1895.1) * mm, "mid": v(3383.86, -1897.5) * mm, "end": v(3386.27, -1898.5) * mm});
            skArc(sketch, "E3609", {"start": v(3421.47, -1898.5) * mm, "mid": v(3423.87, -1897.5) * mm, "end": v(3424.87, -1895.1) * mm});
            skArc(sketch, "E3610", {"start": v(3480.87, -1400.1) * mm, "mid": v(3481.86, -1402.5) * mm, "end": v(3484.27, -1403.5) * mm});
            skArc(sketch, "E3611", {"start": v(3519.47, -1403.5) * mm, "mid": v(3521.87, -1402.5) * mm, "end": v(3522.87, -1400.1) * mm});
            skArc(sketch, "E3612", {"start": v(3522.87, -1368.9) * mm, "mid": v(3521.87, -1366.49) * mm, "end": v(3519.47, -1365.5) * mm});
            skArc(sketch, "E3613", {"start": v(3484.27, -1365.5) * mm, "mid": v(3481.86, -1366.49) * mm, "end": v(3480.87, -1368.9) * mm});
            skArc(sketch, "E3614", {"start": v(3472.57, -1396.17) * mm, "mid": v(3469.79, -1395.23) * mm, "end": v(3466.88, -1394.92) * mm});
            skArc(sketch, "E3615", {"start": v(3438.86, -1394.92) * mm, "mid": v(3435.95, -1395.23) * mm, "end": v(3433.17, -1396.17) * mm});
            skArc(sketch, "E3616", {"start": v(3466.88, -1374.07) * mm, "mid": v(3469.79, -1373.75) * mm, "end": v(3472.57, -1372.82) * mm});
            skArc(sketch, "E3617", {"start": v(3433.17, -1372.82) * mm, "mid": v(3435.95, -1373.75) * mm, "end": v(3438.86, -1374.07) * mm});
            skArc(sketch, "E3618", {"start": v(3421.47, -1403.5) * mm, "mid": v(3423.87, -1402.5) * mm, "end": v(3424.87, -1400.1) * mm});
            skArc(sketch, "E3619", {"start": v(3382.87, -1400.1) * mm, "mid": v(3383.86, -1402.5) * mm, "end": v(3386.27, -1403.5) * mm});
            skArc(sketch, "E3620", {"start": v(3386.27, -1365.5) * mm, "mid": v(3383.86, -1366.49) * mm, "end": v(3382.87, -1368.9) * mm});
            skArc(sketch, "E3621", {"start": v(3424.87, -1368.9) * mm, "mid": v(3423.87, -1366.49) * mm, "end": v(3421.47, -1365.5) * mm});
            skArc(sketch, "E3622", {"start": v(4234.27, -1860.5) * mm, "mid": v(4231.86, -1861.49) * mm, "end": v(4230.87, -1863.9) * mm});
            skArc(sketch, "E3623", {"start": v(4272.87, -1863.9) * mm, "mid": v(4271.87, -1861.49) * mm, "end": v(4269.47, -1860.5) * mm});
            skArc(sketch, "E3624", {"start": v(4269.47, -1898.5) * mm, "mid": v(4271.87, -1897.5) * mm, "end": v(4272.87, -1895.1) * mm});
            skArc(sketch, "E3625", {"start": v(4230.87, -1895.1) * mm, "mid": v(4231.86, -1897.5) * mm, "end": v(4234.27, -1898.5) * mm});
            skArc(sketch, "E3626", {"start": v(4216.88, -1869.07) * mm, "mid": v(4219.79, -1868.75) * mm, "end": v(4222.57, -1867.82) * mm});
            skArc(sketch, "E3627", {"start": v(4183.17, -1867.82) * mm, "mid": v(4185.95, -1868.75) * mm, "end": v(4188.86, -1869.07) * mm});
            skArc(sketch, "E3628", {"start": v(4222.57, -1891.17) * mm, "mid": v(4219.79, -1890.23) * mm, "end": v(4216.88, -1889.92) * mm});
            skArc(sketch, "E3629", {"start": v(4188.86, -1889.92) * mm, "mid": v(4185.95, -1890.23) * mm, "end": v(4183.17, -1891.17) * mm});
            skArc(sketch, "E3630", {"start": v(4174.87, -1863.9) * mm, "mid": v(4173.87, -1861.49) * mm, "end": v(4171.47, -1860.5) * mm});
            skArc(sketch, "E3631", {"start": v(4136.27, -1860.5) * mm, "mid": v(4133.86, -1861.49) * mm, "end": v(4132.87, -1863.9) * mm});
            skArc(sketch, "E3632", {"start": v(4132.87, -1895.1) * mm, "mid": v(4133.86, -1897.5) * mm, "end": v(4136.27, -1898.5) * mm});
            skArc(sketch, "E3633", {"start": v(4171.47, -1898.5) * mm, "mid": v(4173.87, -1897.5) * mm, "end": v(4174.87, -1895.1) * mm});
            skArc(sketch, "E3634", {"start": v(4230.87, -1400.1) * mm, "mid": v(4231.86, -1402.5) * mm, "end": v(4234.27, -1403.5) * mm});
            skArc(sketch, "E3635", {"start": v(4269.47, -1403.5) * mm, "mid": v(4271.87, -1402.5) * mm, "end": v(4272.87, -1400.1) * mm});
            skArc(sketch, "E3636", {"start": v(4272.87, -1368.9) * mm, "mid": v(4271.87, -1366.49) * mm, "end": v(4269.47, -1365.5) * mm});
            skArc(sketch, "E3637", {"start": v(4234.27, -1365.5) * mm, "mid": v(4231.86, -1366.49) * mm, "end": v(4230.87, -1368.9) * mm});
            skArc(sketch, "E3638", {"start": v(4222.57, -1396.17) * mm, "mid": v(4219.79, -1395.23) * mm, "end": v(4216.88, -1394.92) * mm});
            skArc(sketch, "E3639", {"start": v(4188.86, -1394.92) * mm, "mid": v(4185.95, -1395.23) * mm, "end": v(4183.17, -1396.17) * mm});
            skArc(sketch, "E3640", {"start": v(4216.88, -1374.07) * mm, "mid": v(4219.79, -1373.75) * mm, "end": v(4222.57, -1372.82) * mm});
            skArc(sketch, "E3641", {"start": v(4183.17, -1372.82) * mm, "mid": v(4185.95, -1373.75) * mm, "end": v(4188.86, -1374.07) * mm});
            skArc(sketch, "E3642", {"start": v(4171.47, -1403.5) * mm, "mid": v(4173.87, -1402.5) * mm, "end": v(4174.87, -1400.1) * mm});
            skArc(sketch, "E3643", {"start": v(4132.87, -1400.1) * mm, "mid": v(4133.86, -1402.5) * mm, "end": v(4136.27, -1403.5) * mm});
            skArc(sketch, "E3644", {"start": v(4136.27, -1365.5) * mm, "mid": v(4133.86, -1366.49) * mm, "end": v(4132.87, -1368.9) * mm});
            skArc(sketch, "E3645", {"start": v(4174.87, -1368.9) * mm, "mid": v(4173.87, -1366.49) * mm, "end": v(4171.47, -1365.5) * mm});
            skArc(sketch, "E3646", {"start": v(4984.27, -1860.5) * mm, "mid": v(4981.86, -1861.49) * mm, "end": v(4980.87, -1863.9) * mm});
            skArc(sketch, "E3647", {"start": v(5022.87, -1863.9) * mm, "mid": v(5021.87, -1861.49) * mm, "end": v(5019.47, -1860.5) * mm});
            skArc(sketch, "E3648", {"start": v(5019.47, -1898.5) * mm, "mid": v(5021.87, -1897.5) * mm, "end": v(5022.87, -1895.1) * mm});
            skArc(sketch, "E3649", {"start": v(4980.87, -1895.1) * mm, "mid": v(4981.86, -1897.5) * mm, "end": v(4984.27, -1898.5) * mm});
            skArc(sketch, "E3650", {"start": v(4966.88, -1869.07) * mm, "mid": v(4969.79, -1868.75) * mm, "end": v(4972.57, -1867.82) * mm});
            skArc(sketch, "E3651", {"start": v(4933.17, -1867.82) * mm, "mid": v(4935.95, -1868.75) * mm, "end": v(4938.86, -1869.07) * mm});
            skArc(sketch, "E3652", {"start": v(4972.57, -1891.17) * mm, "mid": v(4969.79, -1890.23) * mm, "end": v(4966.88, -1889.92) * mm});
            skArc(sketch, "E3653", {"start": v(4938.86, -1889.92) * mm, "mid": v(4935.95, -1890.23) * mm, "end": v(4933.17, -1891.17) * mm});
            skArc(sketch, "E3654", {"start": v(4924.87, -1863.9) * mm, "mid": v(4923.87, -1861.49) * mm, "end": v(4921.47, -1860.5) * mm});
            skArc(sketch, "E3655", {"start": v(4886.27, -1860.5) * mm, "mid": v(4883.86, -1861.49) * mm, "end": v(4882.87, -1863.9) * mm});
            skArc(sketch, "E3656", {"start": v(4882.87, -1895.1) * mm, "mid": v(4883.86, -1897.5) * mm, "end": v(4886.27, -1898.5) * mm});
            skArc(sketch, "E3657", {"start": v(4921.47, -1898.5) * mm, "mid": v(4923.87, -1897.5) * mm, "end": v(4924.87, -1895.1) * mm});
            skArc(sketch, "E3658", {"start": v(4980.87, -1400.1) * mm, "mid": v(4981.86, -1402.5) * mm, "end": v(4984.27, -1403.5) * mm});
            skArc(sketch, "E3659", {"start": v(5019.47, -1403.5) * mm, "mid": v(5021.87, -1402.5) * mm, "end": v(5022.87, -1400.1) * mm});
            skArc(sketch, "E3660", {"start": v(5022.87, -1368.9) * mm, "mid": v(5021.87, -1366.49) * mm, "end": v(5019.47, -1365.5) * mm});
            skArc(sketch, "E3661", {"start": v(4984.27, -1365.5) * mm, "mid": v(4981.86, -1366.49) * mm, "end": v(4980.87, -1368.9) * mm});
            skArc(sketch, "E3662", {"start": v(4972.57, -1396.17) * mm, "mid": v(4969.79, -1395.23) * mm, "end": v(4966.88, -1394.92) * mm});
            skArc(sketch, "E3663", {"start": v(4938.86, -1394.92) * mm, "mid": v(4935.95, -1395.23) * mm, "end": v(4933.17, -1396.17) * mm});
            skArc(sketch, "E3664", {"start": v(4966.88, -1374.07) * mm, "mid": v(4969.79, -1373.75) * mm, "end": v(4972.57, -1372.82) * mm});
            skArc(sketch, "E3665", {"start": v(4933.17, -1372.82) * mm, "mid": v(4935.95, -1373.75) * mm, "end": v(4938.86, -1374.07) * mm});
            skArc(sketch, "E3666", {"start": v(4921.47, -1403.5) * mm, "mid": v(4923.87, -1402.5) * mm, "end": v(4924.87, -1400.1) * mm});
            skArc(sketch, "E3667", {"start": v(4882.87, -1400.1) * mm, "mid": v(4883.86, -1402.5) * mm, "end": v(4886.27, -1403.5) * mm});
            skArc(sketch, "E3668", {"start": v(4886.27, -1365.5) * mm, "mid": v(4883.86, -1366.49) * mm, "end": v(4882.87, -1368.9) * mm});
            skArc(sketch, "E3669", {"start": v(4924.87, -1368.9) * mm, "mid": v(4923.87, -1366.49) * mm, "end": v(4921.47, -1365.5) * mm});
            skLineSegment(sketch, "E3670", {"start": v(-1982.13, 2130.41) * mm, "end": v(-2282.13, 2130.41) * mm});
            skLineSegment(sketch, "E3671", {"start": v(-1982.13, 4139.49) * mm, "end": v(-1982.13, 2080.41) * mm});
            skLineSegment(sketch, "E3672", {"start": v(217.87, 2130.41) * mm, "end": v(-82.13, 2130.41) * mm});
            skLineSegment(sketch, "E3673", {"start": v(217.87, 4139.49) * mm, "end": v(217.87, 2080.41) * mm});
            skSolve(sketch);
        }
        {
            var Q0;
            Q0=qCreatedBy(makeId("Front.planeOp"),FACE);
            var sketch = newSketch(context, id + "F1", { "sketchPlane" : qUnion([Q0])});
            skPoint(sketch, "E3674.0", {"position": v(-3047.13, -1982) * mm});
            skPoint(sketch, "E3675.0", {"position": v(-2947.13, -2182) * mm});
            skLineSegment(sketch, "E3676.bottom", {"start": v(-3047.13, -1982) * mm, "end": v(-2947.13, -1982) * mm});
            skLineSegment(sketch, "E3676.top", {"start": v(-3047.13, -2182) * mm, "end": v(-2947.13, -2182) * mm});
            skLineSegment(sketch, "E3676.left", {"start": v(-3047.13, -1982) * mm, "end": v(-3047.13, -2182) * mm});
            skLineSegment(sketch, "E3676.right", {"start": v(-2947.13, -1982) * mm, "end": v(-2947.13, -2182) * mm});
            skPoint(sketch, "E3677.0", {"position": v(-3037.63, -1997) * mm});
            skPoint(sketch, "E3678.0", {"position": v(-2956.63, -1997) * mm});
            skPoint(sketch, "E3679.0", {"position": v(-2956.63, -2047) * mm});
            skPoint(sketch, "E3680.0", {"position": v(-3037.63, -2047) * mm});
            skPoint(sketch, "E3681.0", {"position": v(-3037.63, -2117) * mm});
            skPoint(sketch, "E3682.0", {"position": v(-2956.63, -2117) * mm});
            skPoint(sketch, "E3683.0", {"position": v(-3037.63, -2167) * mm});
            skPoint(sketch, "E3684.0", {"position": v(-2956.63, -2167) * mm});
            skSolve(sketch);
        }
        {
            var Q0;
            Q0 = qSketchRegion(id + "F1", true);
            extrude(context, id + "F2", {"entities" : qUnion([Q0]), "depth" : 15 * mm, "offsetDistance" : 25 * mm});
        }
        {
            var Q0;
            Q0=sQuery(id+"F1.wireOp",VERTEX,"E3677.0");
            var Q1;
            Q1=sQuery(id+"F1.wireOp",VERTEX,"E3678.0");
            var Q2;
            Q2=sQuery(id+"F1.wireOp",VERTEX,"E3679.0");
            var Q3;
            Q3=sQuery(id+"F1.wireOp",VERTEX,"E3680.0");
            var Q4;
            Q4=sQuery(id+"F1.wireOp",VERTEX,"E3681.0");
            var Q5;
            Q5=sQuery(id+"F1.wireOp",VERTEX,"E3682.0");
            var Q6;
            Q6=sQuery(id+"F1.wireOp",VERTEX,"E3683.0");
            var Q7;
            Q7=sQuery(id+"F1.wireOp",VERTEX,"E3684.0");
            var Q8;
            Q8=makeQuery(id+"F2.opExtrude","SWEPT_BODY",BODY,{"disambiguationData":[OSD([sQuery(id+"F1.wireOp",EDGE,"E3676.bottom"),sQuery(id+"F1.wireOp",EDGE,"E3676.top"),sQuery(id+"F1.wireOp",EDGE,"E3676.left"),sQuery(id+"F1.wireOp",EDGE,"E3676.right")])]});
            hole(context, id + "F3", {"style" : HoleStyle.SIMPLE, "endStyle" : HoleEndStyle.THROUGH, "oppositeDirection" : true, "standardTappedOrClearance" : lookupTablePath({ "standard" : "ISO", "engagement" : "75%", "pitch" : "1 mm", "size" : "M6", "type" : "Tapped" }), "standardBlindInLast" : lookupTablePath({ "standard" : "ISO", "engagement" : "75%", "pitch" : "1 mm", "size" : "M6", "type" : "Tapped" }), "holeDiameter" : 5 * mm, "majorDiameter" : 6 * mm, "showTappedDepth" : true, "isTappedThrough" : true, "tappedDepth" : 6.25 * mm, "tapClearance" : 3, "locations" : qUnion([Q0, Q1, Q2, Q3, Q4, Q5, Q6, Q7]), "scope" : qUnion([Q8])});
        }
        {
            var Q0;
            Q0=makeQuery(id+"F2.opExtrude","CAP_FACE",FACE,{"disambiguationData":[OSD([sQuery(id+"F1.wireOp",EDGE,"E3676.bottom"),sQuery(id+"F1.wireOp",EDGE,"E3676.top"),sQuery(id+"F1.wireOp",EDGE,"E3676.left"),sQuery(id+"F1.wireOp",EDGE,"E3676.right")])],"isStart":false});
            var sketch = newSketch(context, id + "F4", { "sketchPlane" : qUnion([Q0])});
            skPoint(sketch, "E3685.0", {"position": v(-3044.63, -1983) * mm});
            skPoint(sketch, "E3686.0", {"position": v(-3029.63, -2061) * mm});
            skLineSegment(sketch, "E3687.bottom", {"start": v(-3044.63, -1983) * mm, "end": v(-3029.63, -1983) * mm});
            skLineSegment(sketch, "E3687.top", {"start": v(-3044.63, -2061) * mm, "end": v(-3029.63, -2061) * mm});
            skLineSegment(sketch, "E3687.left", {"start": v(-3044.63, -1983) * mm, "end": v(-3044.63, -2061) * mm});
            skLineSegment(sketch, "E3687.right", {"start": v(-3029.63, -1983) * mm, "end": v(-3029.63, -2061) * mm});
            skSolve(sketch);
        }
        {
            var Q0;
            Q0=makeQuery(id+"F4.imprint","IMPRINT",FACE,{"disambiguationData":[TD([[makeQuery(id+"F4.imprint","IMPRINT",EDGE,{"derivedFrom":sQuery(id+"F4.wireOp",EDGE,"E3687.bottom")}),-1.0]])]});
            var Q1;
            Q1=makeQuery(id+"F4.imprint","IMPRINT",FACE,{"disambiguationData":[TD([[makeQuery(id+"F4.imprint","IMPRINT",EDGE,{"derivedFrom":makeQuery(id+"F3.hole-3.boolean.opBoolean","INTERSECT",EDGE,{"derivedFrom":[makeQuery(id+"F2.opExtrude","CAP_FACE",FACE,{"disambiguationData":[OSD([sQuery(id+"F1.wireOp",EDGE,"E3676.bottom"),sQuery(id+"F1.wireOp",EDGE,"E3676.top"),sQuery(id+"F1.wireOp",EDGE,"E3676.left"),sQuery(id+"F1.wireOp",EDGE,"E3676.right")])],"isStart":false}),makeQuery(id+"F3.hole-3.opRevolve","SWEPT_FACE",FACE,{"disambiguationData":[OSD([sQuery(id+"F3.hole-3.sketch.wireOp",EDGE,"core_line_2")])]})]})}),-1.0]])]});
            var Q2;
            Q2=makeQuery(id+"F4.imprint","IMPRINT",FACE,{"disambiguationData":[TD([[makeQuery(id+"F4.imprint","IMPRINT",EDGE,{"derivedFrom":makeQuery(id+"F3.hole-0.boolean.opBoolean","INTERSECT",EDGE,{"derivedFrom":[makeQuery(id+"F2.opExtrude","CAP_FACE",FACE,{"disambiguationData":[OSD([sQuery(id+"F1.wireOp",EDGE,"E3676.bottom"),sQuery(id+"F1.wireOp",EDGE,"E3676.top"),sQuery(id+"F1.wireOp",EDGE,"E3676.left"),sQuery(id+"F1.wireOp",EDGE,"E3676.right")])],"isStart":false}),makeQuery(id+"F3.hole-0.opRevolve","SWEPT_FACE",FACE,{"disambiguationData":[OSD([sQuery(id+"F3.hole-0.sketch.wireOp",EDGE,"core_line_2")])]})]})}),-1.0]])]});
            extrude(context, id + "F5", {"entities" : qUnion([Q0, Q1, Q2]), "depth" : 20 * mm, "offsetDistance" : 25 * mm});
        }
        {
            var Q0;
            Q0=makeQuery(id+"F5.opExtrude","CAP_FACE",FACE,{"disambiguationData":[OSD([sQuery(id+"F4.wireOp",EDGE,"E3687.bottom"),sQuery(id+"F4.wireOp",EDGE,"E3687.top"),sQuery(id+"F4.wireOp",EDGE,"E3687.left"),sQuery(id+"F4.wireOp",EDGE,"E3687.right")])],"isStart":false});
            var sketch = newSketch(context, id + "F6", { "sketchPlane" : qUnion([Q0])});
            skPoint(sketch, "E3688.0", {"position": v(-3037.63, -1997) * mm});
            skPoint(sketch, "E3689.0", {"position": v(-3037.63, -2047) * mm});
            skSolve(sketch);
        }
        {
            var Q0;
            Q0=sQuery(id+"F6.wireOp",VERTEX,"E3688.0");
            var Q1;
            Q1=sQuery(id+"F6.wireOp",VERTEX,"E3689.0");
            var Q2;
            Q2=makeQuery(id+"F5.opExtrude","SWEPT_BODY",BODY,{"disambiguationData":[OSD([sQuery(id+"F4.wireOp",EDGE,"E3687.bottom"),sQuery(id+"F4.wireOp",EDGE,"E3687.top"),sQuery(id+"F4.wireOp",EDGE,"E3687.left"),sQuery(id+"F4.wireOp",EDGE,"E3687.right")])]});
            hole(context, id + "F7", {"style" : HoleStyle.C_BORE, "endStyle" : HoleEndStyle.THROUGH, "standardTappedOrClearance" : lookupTablePath({ "standard" : "ISO", "fit" : "Normal", "size" : "M6", "type" : "Clearance" }), "standardBlindInLast" : lookupTablePath({ "fit" : "Standard", "standard" : "ISO", "size" : "M6", "type" : "Clearance" }), "holeDiameter" : 6.6 * mm, "cBoreDiameter" : 11.25 * mm, "cBoreDepth" : 6 * mm, "majorDiameter" : 6 * mm, "isTappedThrough" : true, "tappedDepth" : 6.25 * mm, "tapClearance" : 3, "locations" : qUnion([Q0, Q1]), "scope" : qUnion([Q2])});
        }
        {
            var Q0;
            Q0=makeQuery(id+"F5.opExtrude","SWEPT_FACE",FACE,{"disambiguationData":[OSD([sQuery(id+"F4.wireOp",EDGE,"E3687.right")])]});
            var sketch = newSketch(context, id + "F8", { "sketchPlane" : qUnion([Q0])});
            skLineSegment(sketch, "E3690.bottom", {"start": v(-35, -2061) * mm, "end": v(-30, -2061) * mm});
            skLineSegment(sketch, "E3690.top", {"start": v(-35, -1983) * mm, "end": v(-30, -1983) * mm});
            skLineSegment(sketch, "E3690.left", {"start": v(-35, -2061) * mm, "end": v(-35, -1983) * mm});
            skLineSegment(sketch, "E3690.right", {"start": v(-30, -2061) * mm, "end": v(-30, -1983) * mm});
            skSolve(sketch);
        }
        {
            var Q0;
            Q0 = qSketchRegion(id + "F8", true);
            var Q1;
            Q1=makeQuery(id+"F8.imprint","IMPRINT",FACE,{"disambiguationData":[TD([[makeQuery(id+"F8.imprint","IMPRINT",EDGE,{"derivedFrom":sQuery(id+"F8.wireOp",EDGE,"E3690.bottom")}),1.0]])]});
            extrude(context, id + "F9", {"entities" : qUnion([Q0, Q1]), "operationType" : NewBodyOperationType.ADD, "depth" : 5 * mm, "offsetDistance" : 25 * mm});
        }
        {
            var Q0;
            {var subQ0=sQuery(id+"F0.wireOp",EDGE,"E996");Q0=makeQuery(id+"F0.imprint","IMPRINT",FACE,{"disambiguationData":[TD([[makeQuery(id+"F0.imprint","IMPRINT",EDGE,{"derivedFrom":subQ0}),-1.0]])]});}
            var sketch = newSketch(context, id + "F10", { "sketchPlane" : qUnion([Q0])});
            skPoint(sketch, "E3691.0", {"position": v(-3047.13, -3575) * mm});
            skPoint(sketch, "E3692.0", {"position": v(-2947.13, -3655) * mm});
            skLineSegment(sketch, "E3693.bottom", {"start": v(-3047.13, -3575) * mm, "end": v(-2947.13, -3575) * mm});
            skLineSegment(sketch, "E3693.top", {"start": v(-3047.13, -3655) * mm, "end": v(-2947.13, -3655) * mm});
            skLineSegment(sketch, "E3693.left", {"start": v(-3047.13, -3575) * mm, "end": v(-3047.13, -3655) * mm});
            skLineSegment(sketch, "E3693.right", {"start": v(-2947.13, -3575) * mm, "end": v(-2947.13, -3655) * mm});
            skSolve(sketch);
        }
        {
            var Q0;
            Q0 = qSketchRegion(id + "F10", true);
            extrude(context, id + "F11", {"entities" : qUnion([Q0]), "depth" : 15 * mm, "offsetDistance" : 25 * mm});
        }
        {
            var Q0;
            Q0=makeQuery(id+"F11.opExtrude","CAP_FACE",FACE,{"disambiguationData":[OSD([sQuery(id+"F10.wireOp",EDGE,"E3693.bottom"),sQuery(id+"F10.wireOp",EDGE,"E3693.top"),sQuery(id+"F10.wireOp",EDGE,"E3693.left"),sQuery(id+"F10.wireOp",EDGE,"E3693.right")])],"isStart":false});
            var sketch = newSketch(context, id + "F12", { "sketchPlane" : qUnion([Q0])});
            skPoint(sketch, "E3694.0", {"position": v(-3044.63, -3576) * mm});
            skPoint(sketch, "E3695.0", {"position": v(-3029.63, -3654) * mm});
            skLineSegment(sketch, "E3696.bottom", {"start": v(-3029.63, -3654) * mm, "end": v(-3044.63, -3654) * mm});
            skLineSegment(sketch, "E3696.top", {"start": v(-3029.63, -3576) * mm, "end": v(-3044.63, -3576) * mm});
            skLineSegment(sketch, "E3696.left", {"start": v(-3029.63, -3654) * mm, "end": v(-3029.63, -3576) * mm});
            skLineSegment(sketch, "E3696.right", {"start": v(-3044.63, -3654) * mm, "end": v(-3044.63, -3576) * mm});
            skPoint(sketch, "E3697", {"position": v(-3037.13, -3591) * mm});
            skPoint(sketch, "E3698", {"position": v(-3036.64, -3641) * mm});
            skSolve(sketch);
        }
        {
            var Q0;
            Q0=makeQuery(id+"F12.imprint","IMPRINT",FACE,{"disambiguationData":[TD([[makeQuery(id+"F12.imprint","IMPRINT",EDGE,{"derivedFrom":sQuery(id+"F12.wireOp",EDGE,"E3696.bottom")}),-1.0]])]});
            extrude(context, id + "F13", {"entities" : qUnion([Q0]), "depth" : 20 * mm, "offsetDistance" : 25 * mm});
        }
        {
            var Q0;
            Q0=makeQuery(id+"F13.opExtrude","CAP_FACE",FACE,{"disambiguationData":[OSD([sQuery(id+"F12.wireOp",EDGE,"E3696.bottom"),sQuery(id+"F12.wireOp",EDGE,"E3696.top"),sQuery(id+"F12.wireOp",EDGE,"E3696.left"),sQuery(id+"F12.wireOp",EDGE,"E3696.right")])],"isStart":false});
            var sketch = newSketch(context, id + "F14", { "sketchPlane" : qUnion([Q0])});
            skPoint(sketch, "E3699", {"position": v(-3037.13, -3591) * mm});
            skPoint(sketch, "E3699.positionSnap0", {"position": v(-3037.13, -3576) * mm});
            skPoint(sketch, "E3700", {"position": v(-3037.13, -3641) * mm});
            skSolve(sketch);
        }
        {
            var Q0;
            Q0=sQuery(id+"F14.wireOp",VERTEX,"E3699");
            var Q1;
            Q1=sQuery(id+"F14.wireOp",VERTEX,"E3700");
            var Q2;
            Q2=makeQuery(id+"F11.opExtrude","SWEPT_BODY",BODY,{"disambiguationData":[OSD([sQuery(id+"F10.wireOp",EDGE,"E3693.bottom"),sQuery(id+"F10.wireOp",EDGE,"E3693.top"),sQuery(id+"F10.wireOp",EDGE,"E3693.left"),sQuery(id+"F10.wireOp",EDGE,"E3693.right")])]});
            var Q3;
            Q3=makeQuery(id+"F13.opExtrude","SWEPT_BODY",BODY,{"disambiguationData":[OSD([sQuery(id+"F12.wireOp",EDGE,"E3696.bottom"),sQuery(id+"F12.wireOp",EDGE,"E3696.top"),sQuery(id+"F12.wireOp",EDGE,"E3696.left"),sQuery(id+"F12.wireOp",EDGE,"E3696.right")])]});
            hole(context, id + "F15", {"style" : HoleStyle.SIMPLE, "endStyle" : HoleEndStyle.THROUGH, "standardTappedOrClearance" : lookupTablePath({ "standard" : "ISO", "engagement" : "75%", "pitch" : "1 mm", "size" : "M6", "type" : "Tapped" }), "standardBlindInLast" : lookupTablePath({ "standard" : "ISO", "engagement" : "75%", "pitch" : "1 mm", "size" : "M6", "type" : "Tapped" }), "holeDiameter" : 5 * mm, "majorDiameter" : 6 * mm, "showTappedDepth" : true, "isTappedThrough" : true, "tappedDepth" : 6.25 * mm, "tapClearance" : 3, "locations" : qUnion([Q0, Q1]), "scope" : qUnion([Q2, Q3])});
        }
        {
            var Q0;
            Q0=makeQuery(id+"F11.opExtrude","SWEPT_FACE",FACE,{"disambiguationData":[OSD([sQuery(id+"F10.wireOp",EDGE,"E3693.left")])]});
            var Q1;
            Q1=makeQuery(id+"F11.opExtrude","SWEPT_FACE",FACE,{"disambiguationData":[OSD([sQuery(id+"F10.wireOp",EDGE,"E3693.right")])]});
            cPlane(context, id + "F16", {"entities" : qUnion([Q0, Q1]), "cplaneType" : CPlaneType.MID_PLANE, "offset" : 25 * mm, "width" : 150 * mm, "height" : 150 * mm});
        }
        {
            var Q0;
            Q0=makeQuery(id+"F2.opExtrude","SWEPT_FACE",FACE,{"disambiguationData":[OSD([sQuery(id+"F1.wireOp",EDGE,"E3676.left")])]});
            var Q1;
            Q1=makeQuery(id+"F2.opExtrude","SWEPT_FACE",FACE,{"disambiguationData":[OSD([sQuery(id+"F1.wireOp",EDGE,"E3676.right")])]});
            cPlane(context, id + "F17", {"entities" : qUnion([Q0, Q1]), "cplaneType" : CPlaneType.MID_PLANE, "offset" : 25 * mm, "width" : 150 * mm, "height" : 150 * mm});
        }
        {
            var Q0;
            Q0=makeQuery(id+"F2.opExtrude","SWEPT_FACE",FACE,{"disambiguationData":[OSD([sQuery(id+"F1.wireOp",EDGE,"E3676.top")])]});
            var Q1;
            Q1=makeQuery(id+"F2.opExtrude","SWEPT_FACE",FACE,{"disambiguationData":[OSD([sQuery(id+"F1.wireOp",EDGE,"E3676.bottom")])]});
            cPlane(context, id + "F18", {"entities" : qUnion([Q0, Q1]), "cplaneType" : CPlaneType.MID_PLANE, "offset" : 25 * mm, "width" : 150 * mm, "height" : 150 * mm});
        }
        {
            var Q0;
            Q0=makeQuery(id+"F5.opExtrude","SWEPT_BODY",BODY,{"disambiguationData":[OSD([sQuery(id+"F4.wireOp",EDGE,"E3687.bottom"),sQuery(id+"F4.wireOp",EDGE,"E3687.top"),sQuery(id+"F4.wireOp",EDGE,"E3687.left"),sQuery(id+"F4.wireOp",EDGE,"E3687.right")])]});
            var Q1;
            Q1=qCreatedBy(id+"F17.planeOp",FACE);
            mirror(context, id + "F19", {"entities" : qUnion([Q0]), "mirrorPlane" : qUnion([Q1])});
        }
        {
            var Q0;
            Q0=makeQuery(id+"F5.opExtrude","SWEPT_BODY",BODY,{"disambiguationData":[OSD([sQuery(id+"F4.wireOp",EDGE,"E3687.bottom"),sQuery(id+"F4.wireOp",EDGE,"E3687.top"),sQuery(id+"F4.wireOp",EDGE,"E3687.left"),sQuery(id+"F4.wireOp",EDGE,"E3687.right")])]});
            var Q1;
            Q1=makeQuery(id+"F19.opPattern","COPY",BODY,{"derivedFrom":makeQuery(id+"F5.opExtrude","SWEPT_BODY",BODY,{"disambiguationData":[OSD([sQuery(id+"F4.wireOp",EDGE,"E3687.bottom"),sQuery(id+"F4.wireOp",EDGE,"E3687.top"),sQuery(id+"F4.wireOp",EDGE,"E3687.left"),sQuery(id+"F4.wireOp",EDGE,"E3687.right")])]}),"instanceName":"1"});
            var Q2;
            Q2=qCreatedBy(id+"F18.planeOp",FACE);
            mirror(context, id + "F20", {"entities" : qUnion([Q0, Q1]), "mirrorPlane" : qUnion([Q2])});
        }
        {
            var Q0;
            Q0=qCreatedBy(makeId("Top.planeOp"),FACE);
            var sketch = newSketch(context, id + "F21", { "sketchPlane" : qUnion([Q0])});
            skLineSegment(sketch, "E3701", {"start": v(-13.33, 49.59) * mm, "end": v(-11.05, 51.87) * mm});
            skLineSegment(sketch, "E3702", {"start": v(-15.55, 43.2) * mm, "end": v(-10.38, 48.37) * mm});
            skLineSegment(sketch, "E3703", {"start": v(-12.23, 42.34) * mm, "end": v(-10.38, 44.19) * mm});
            skLineSegment(sketch, "E3704", {"start": v(-58.62, 50.25) * mm, "end": v(-54.72, 54.15) * mm});
            skLineSegment(sketch, "E3705", {"start": v(-60.84, 43.86) * mm, "end": v(-50.54, 54.15) * mm});
            skLineSegment(sketch, "E3706", {"start": v(-58.18, 42.34) * mm, "end": v(-46.36, 54.15) * mm});
            skLineSegment(sketch, "E3707", {"start": v(-54, 42.34) * mm, "end": v(-42.18, 54.15) * mm});
            skLineSegment(sketch, "E3708", {"start": v(-49.82, 42.34) * mm, "end": v(-38, 54.15) * mm});
            skLineSegment(sketch, "E3709", {"start": v(-45.65, 42.34) * mm, "end": v(-33.83, 54.15) * mm});
            skLineSegment(sketch, "E3710", {"start": v(-41.47, 42.34) * mm, "end": v(-29.65, 54.15) * mm});
            skLineSegment(sketch, "E3711", {"start": v(-37.3, 42.34) * mm, "end": v(-25.8, 53.83) * mm});
            skLineSegment(sketch, "E3712", {"start": v(-33.11, 42.34) * mm, "end": v(-23.18, 52.28) * mm});
            skLineSegment(sketch, "E3713", {"start": v(-28.94, 42.34) * mm, "end": v(-23.18, 48.1) * mm});
            skLineSegment(sketch, "E3714", {"start": v(-24.76, 42.34) * mm, "end": v(-20.96, 46.14) * mm});
            skLineSegment(sketch, "E3715", {"start": v(-22.2, 39.34) * mm, "end": v(-21.65, 39.88) * mm});
            skLineSegment(sketch, "E3716", {"start": v(-22.2, 37.94) * mm, "end": v(-20.26, 39.88) * mm});
            skLineSegment(sketch, "E3717", {"start": v(-22.2, 36.55) * mm, "end": v(-20.23, 38.5) * mm});
            skLineSegment(sketch, "E3718", {"start": v(-21.41, 35.94) * mm, "end": v(-20.23, 37.12) * mm});
            skLineSegment(sketch, "E3719", {"start": v(-16.27, 39.68) * mm, "end": v(-16.08, 39.88) * mm});
            skLineSegment(sketch, "E3720", {"start": v(-16.27, 38.3) * mm, "end": v(-14.69, 39.88) * mm});
            skLineSegment(sketch, "E3721", {"start": v(-16.27, 36.9) * mm, "end": v(-14.31, 38.86) * mm});
            skLineSegment(sketch, "E3722", {"start": v(-15.84, 35.94) * mm, "end": v(-14.31, 37.47) * mm});
            skLineSegment(sketch, "E3723", {"start": v(-14.45, 35.94) * mm, "end": v(-14.31, 36.07) * mm});
            skLineSegment(sketch, "E3724", {"start": v(-71.42, 49.98) * mm, "end": v(-68.47, 52.93) * mm});
            skLineSegment(sketch, "E3725", {"start": v(-71.42, 45.8) * mm, "end": v(-68.47, 48.76) * mm});
            skLineSegment(sketch, "E3726", {"start": v(-70.7, 42.34) * mm, "end": v(-66.28, 46.77) * mm});
            skLineSegment(sketch, "E3727", {"start": v(-66.53, 42.34) * mm, "end": v(-66.25, 42.62) * mm});
            skLineSegment(sketch, "E3728", {"start": v(-61.57, 38.95) * mm, "end": v(-60.64, 39.88) * mm});
            skLineSegment(sketch, "E3729", {"start": v(-61.57, 37.56) * mm, "end": v(-59.6, 39.52) * mm});
            skLineSegment(sketch, "E3730", {"start": v(-61.57, 36.16) * mm, "end": v(-59.6, 38.12) * mm});
            skLineSegment(sketch, "E3731", {"start": v(-60.4, 35.94) * mm, "end": v(-59.6, 36.73) * mm});
            skLineSegment(sketch, "E3732", {"start": v(-67.48, 38.6) * mm, "end": v(-66.2, 39.88) * mm});
            skLineSegment(sketch, "E3733", {"start": v(-67.48, 37.2) * mm, "end": v(-65.52, 39.17) * mm});
            skLineSegment(sketch, "E3734", {"start": v(-67.36, 35.94) * mm, "end": v(-65.52, 37.78) * mm});
            skLineSegment(sketch, "E3735", {"start": v(-65.97, 35.94) * mm, "end": v(-65.52, 36.38) * mm});
            skLineSegment(sketch, "E3736", {"start": v(-26.13, 59.08) * mm, "end": v(-55.67, 59.08) * mm});
            skLineSegment(sketch, "E3737", {"start": v(-55.67, 54.15) * mm, "end": v(-55.67, 59.08) * mm});
            skLineSegment(sketch, "E3738", {"start": v(-26.13, 54.15) * mm, "end": v(-26.13, 59.08) * mm});
            skLineSegment(sketch, "E3739", {"start": v(-1.02, -38.4) * mm, "end": v(-1.02, -59.08) * mm});
            skLineSegment(sketch, "E3740", {"start": v(-83.73, -53.17) * mm, "end": v(-77.82, -53.17) * mm});
            skLineSegment(sketch, "E3741", {"start": v(-77.82, -41.35) * mm, "end": v(-77.82, -53.17) * mm});
            skLineSegment(sketch, "E3742", {"start": v(-83.73, -41.35) * mm, "end": v(-83.73, -53.17) * mm});
            skLineSegment(sketch, "E3743", {"start": v(-83.12, -54.77) * mm, "end": v(-78.43, -54.77) * mm});
            skLineSegment(sketch, "E3744", {"start": v(-78.43, -54.77) * mm, "end": v(-80.78, -56.12) * mm});
            skLineSegment(sketch, "E3745", {"start": v(-83.12, -54.77) * mm, "end": v(-80.78, -56.12) * mm});
            skLineSegment(sketch, "E3746", {"start": v(-78.43, -41.35) * mm, "end": v(-83.12, -41.35) * mm});
            skLineSegment(sketch, "E3747", {"start": v(-78.43, -41.35) * mm, "end": v(-78.43, -54.77) * mm});
            skLineSegment(sketch, "E3748", {"start": v(-83.12, -41.35) * mm, "end": v(-90.13, -41.35) * mm});
            skLineSegment(sketch, "E3749", {"start": v(-83.12, -41.35) * mm, "end": v(-83.12, -54.77) * mm});
            skLineSegment(sketch, "E3750", {"start": v(-3.98, -53.17) * mm, "end": v(1.93, -53.17) * mm});
            skLineSegment(sketch, "E3751", {"start": v(1.93, -41.35) * mm, "end": v(1.93, -53.17) * mm});
            skLineSegment(sketch, "E3752", {"start": v(-3.98, -41.35) * mm, "end": v(-3.98, -53.17) * mm});
            skLineSegment(sketch, "E3753", {"start": v(-3.37, -54.77) * mm, "end": v(1.33, -54.77) * mm});
            skLineSegment(sketch, "E3754", {"start": v(1.33, -54.77) * mm, "end": v(-1.02, -56.12) * mm});
            skLineSegment(sketch, "E3755", {"start": v(-3.37, -54.77) * mm, "end": v(-1.02, -56.12) * mm});
            skLineSegment(sketch, "E3756", {"start": v(1.33, -41.35) * mm, "end": v(-3.37, -41.35) * mm});
            skLineSegment(sketch, "E3757", {"start": v(1.33, -41.35) * mm, "end": v(1.33, -54.77) * mm});
            skLineSegment(sketch, "E3758", {"start": v(-3.37, -41.35) * mm, "end": v(-78.43, -41.35) * mm});
            skLineSegment(sketch, "E3759", {"start": v(-3.37, -41.35) * mm, "end": v(-3.37, -54.77) * mm});
            skLineSegment(sketch, "E3760", {"start": v(8.33, -56.12) * mm, "end": v(8.33, -41.35) * mm});
            skLineSegment(sketch, "E3761", {"start": v(-90.13, -56.12) * mm, "end": v(8.33, -56.12) * mm});
            skLineSegment(sketch, "E3762", {"start": v(-90.13, -41.35) * mm, "end": v(-90.13, -56.12) * mm});
            skLineSegment(sketch, "E3763", {"start": v(8.33, -41.35) * mm, "end": v(1.33, -41.35) * mm});
            skLineSegment(sketch, "E3764", {"start": v(-71.42, 51.2) * mm, "end": v(-69.45, 53.17) * mm});
            skLineSegment(sketch, "E3765", {"start": v(-56.65, 53.17) * mm, "end": v(-55.67, 54.15) * mm});
            skLineSegment(sketch, "E3766", {"start": v(-58.62, 53.17) * mm, "end": v(-56.65, 53.17) * mm});
            skLineSegment(sketch, "E3767", {"start": v(-63.55, 32.98) * mm, "end": v(-63.55, 57.1) * mm});
            skLineSegment(sketch, "E3768", {"start": v(-60.84, 42.34) * mm, "end": v(-66.25, 42.34) * mm});
            skLineSegment(sketch, "E3769", {"start": v(-66.25, 42.34) * mm, "end": v(-66.25, 46.77) * mm});
            skLineSegment(sketch, "E3770", {"start": v(-60.84, 42.34) * mm, "end": v(-60.84, 46.77) * mm});
            skLineSegment(sketch, "E3771", {"start": v(-66.25, 46.77) * mm, "end": v(-60.84, 46.77) * mm});
            skLineSegment(sketch, "E3772", {"start": v(-66.25, 46.77) * mm, "end": v(-68.47, 46.77) * mm});
            skLineSegment(sketch, "E3773", {"start": v(-60.84, 46.77) * mm, "end": v(-58.62, 46.77) * mm});
            skLineSegment(sketch, "E3774", {"start": v(-69.45, 53.17) * mm, "end": v(-68.47, 53.17) * mm});
            skLineSegment(sketch, "E3775", {"start": v(-68.47, 46.77) * mm, "end": v(-68.47, 53.17) * mm});
            skLineSegment(sketch, "E3776", {"start": v(-68.47, 53.17) * mm, "end": v(-58.62, 53.17) * mm});
            skLineSegment(sketch, "E3777", {"start": v(-58.62, 46.77) * mm, "end": v(-58.62, 53.17) * mm});
            skLineSegment(sketch, "E3778", {"start": v(-66, 35.94) * mm, "end": v(-66, 39.88) * mm});
            skLineSegment(sketch, "E3779", {"start": v(-61.08, 35.94) * mm, "end": v(-61.08, 39.88) * mm});
            skLineSegment(sketch, "E3780", {"start": v(-67.48, 39.88) * mm, "end": v(-65.52, 39.88) * mm});
            skLineSegment(sketch, "E3781", {"start": v(-61.57, 35.94) * mm, "end": v(-65.52, 35.94) * mm});
            skLineSegment(sketch, "E3782", {"start": v(-65.52, 35.94) * mm, "end": v(-65.52, 39.88) * mm});
            skLineSegment(sketch, "E3783", {"start": v(-59.6, 35.94) * mm, "end": v(-61.57, 35.94) * mm});
            skLineSegment(sketch, "E3784", {"start": v(-65.52, 39.88) * mm, "end": v(-61.57, 39.88) * mm});
            skLineSegment(sketch, "E3785", {"start": v(-61.57, 35.94) * mm, "end": v(-61.57, 39.88) * mm});
            skLineSegment(sketch, "E3786", {"start": v(-59.6, 39.88) * mm, "end": v(-59.6, 35.94) * mm});
            skLineSegment(sketch, "E3787", {"start": v(-65.52, 35.94) * mm, "end": v(-67.48, 35.94) * mm});
            skLineSegment(sketch, "E3788", {"start": v(-67.48, 35.94) * mm, "end": v(-67.48, 39.88) * mm});
            skLineSegment(sketch, "E3789", {"start": v(-61.57, 39.88) * mm, "end": v(-59.6, 39.88) * mm});
            skLineSegment(sketch, "E3790", {"start": v(-71.42, 42.34) * mm, "end": v(-71.42, 51.2) * mm});
            skLineSegment(sketch, "E3791", {"start": v(-66.25, 42.34) * mm, "end": v(-71.42, 42.34) * mm});
            skLineSegment(sketch, "E3792", {"start": v(-12.35, 53.17) * mm, "end": v(-10.38, 51.2) * mm});
            skLineSegment(sketch, "E3793", {"start": v(-26.13, 54.15) * mm, "end": v(-25.15, 53.17) * mm});
            skLineSegment(sketch, "E3794", {"start": v(-25.15, 53.17) * mm, "end": v(-23.18, 53.17) * mm});
            skLineSegment(sketch, "E3795", {"start": v(-18.25, 57.1) * mm, "end": v(-18.25, 32.98) * mm});
            skLineSegment(sketch, "E3796", {"start": v(-15.55, 42.34) * mm, "end": v(-20.96, 42.34) * mm});
            skLineSegment(sketch, "E3797", {"start": v(-15.55, 46.77) * mm, "end": v(-15.55, 42.34) * mm});
            skLineSegment(sketch, "E3798", {"start": v(-20.96, 42.34) * mm, "end": v(-60.84, 42.34) * mm});
            skLineSegment(sketch, "E3799", {"start": v(-20.96, 46.77) * mm, "end": v(-20.96, 42.34) * mm});
            skLineSegment(sketch, "E3800", {"start": v(-20.96, 46.77) * mm, "end": v(-15.55, 46.77) * mm});
            skLineSegment(sketch, "E3801", {"start": v(-13.33, 46.77) * mm, "end": v(-15.55, 46.77) * mm});
            skLineSegment(sketch, "E3802", {"start": v(-23.18, 46.77) * mm, "end": v(-20.96, 46.77) * mm});
            skLineSegment(sketch, "E3803", {"start": v(-13.33, 53.17) * mm, "end": v(-12.35, 53.17) * mm});
            skLineSegment(sketch, "E3804", {"start": v(-13.33, 53.17) * mm, "end": v(-13.33, 46.77) * mm});
            skLineSegment(sketch, "E3805", {"start": v(-23.18, 53.17) * mm, "end": v(-13.33, 53.17) * mm});
            skLineSegment(sketch, "E3806", {"start": v(-23.18, 53.17) * mm, "end": v(-23.18, 46.77) * mm});
            skLineSegment(sketch, "E3807", {"start": v(-15.8, 39.88) * mm, "end": v(-15.8, 35.94) * mm});
            skLineSegment(sketch, "E3808", {"start": v(-20.71, 39.88) * mm, "end": v(-20.71, 35.94) * mm});
            skLineSegment(sketch, "E3809", {"start": v(-16.27, 39.88) * mm, "end": v(-14.31, 39.88) * mm});
            skLineSegment(sketch, "E3810", {"start": v(-16.27, 35.94) * mm, "end": v(-20.23, 35.94) * mm});
            skLineSegment(sketch, "E3811", {"start": v(-16.27, 39.88) * mm, "end": v(-16.27, 35.94) * mm});
            skLineSegment(sketch, "E3812", {"start": v(-20.23, 35.94) * mm, "end": v(-22.2, 35.94) * mm});
            skLineSegment(sketch, "E3813", {"start": v(-20.23, 39.88) * mm, "end": v(-16.27, 39.88) * mm});
            skLineSegment(sketch, "E3814", {"start": v(-20.23, 39.88) * mm, "end": v(-20.23, 35.94) * mm});
            skLineSegment(sketch, "E3815", {"start": v(-22.2, 35.94) * mm, "end": v(-22.2, 39.88) * mm});
            skLineSegment(sketch, "E3816", {"start": v(-14.31, 35.94) * mm, "end": v(-16.27, 35.94) * mm});
            skLineSegment(sketch, "E3817", {"start": v(-14.31, 39.88) * mm, "end": v(-14.31, 35.94) * mm});
            skLineSegment(sketch, "E3818", {"start": v(-22.2, 39.88) * mm, "end": v(-20.23, 39.88) * mm});
            skLineSegment(sketch, "E3819", {"start": v(-55.67, 54.15) * mm, "end": v(-26.13, 54.15) * mm});
            skLineSegment(sketch, "E3820", {"start": v(-10.38, 51.2) * mm, "end": v(-10.38, 42.34) * mm});
            skLineSegment(sketch, "E3821", {"start": v(-10.38, 42.34) * mm, "end": v(-15.55, 42.34) * mm});
            skLineSegment(sketch, "E3822", {"start": v(8, 27.53) * mm, "end": v(65.7, 27.53) * mm});
            skLineSegment(sketch, "E3823", {"start": v(65.7, 27.53) * mm, "end": v(65.7, 43.28) * mm});
            skLineSegment(sketch, "E3824", {"start": v(65.7, 43.28) * mm, "end": v(8, 43.28) * mm});
            skLineSegment(sketch, "E3825", {"start": v(8, 43.28) * mm, "end": v(8, 27.53) * mm});
            skCircle(sketch, "E3826", {"center": v(-56.44, 5.36) * mm, "radius": 1.97 * mm});
            skCircle(sketch, "E3827", {"center": v(-66.28, 36.86) * mm, "radius": 1.97 * mm});
            skCircle(sketch, "E3828", {"center": v(-48.56, 45.72) * mm, "radius": 1.97 * mm});
            skLineSegment(sketch, "E3829", {"start": v(-77.82, -51.97) * mm, "end": v(-83.73, -51.97) * mm});
            skLineSegment(sketch, "E3830", {"start": v(-77.82, -51.97) * mm, "end": v(-78.43, -52.58) * mm});
            skLineSegment(sketch, "E3831", {"start": v(-78.43, -52.58) * mm, "end": v(-83.12, -52.58) * mm});
            skLineSegment(sketch, "E3832", {"start": v(-83.12, -52.58) * mm, "end": v(-83.73, -51.97) * mm});
            skLineSegment(sketch, "E3833", {"start": v(-85.7, -27.96) * mm, "end": v(-75.85, -27.96) * mm});
            skLineSegment(sketch, "E3834", {"start": v(-74.54, -40.86) * mm, "end": v(-73.88, -40.2) * mm});
            skLineSegment(sketch, "E3835", {"start": v(-77.63, -40.86) * mm, "end": v(-83.93, -40.86) * mm});
            skLineSegment(sketch, "E3836", {"start": v(-83.93, -40.86) * mm, "end": v(-83.93, -27.96) * mm});
            skLineSegment(sketch, "E3837", {"start": v(-73.88, -40.86) * mm, "end": v(-77.63, -40.86) * mm});
            skLineSegment(sketch, "E3838", {"start": v(-77.63, -40.86) * mm, "end": v(-77.63, -27.96) * mm});
            skLineSegment(sketch, "E3839", {"start": v(-83.93, -27.96) * mm, "end": v(-77.63, -27.96) * mm});
            skLineSegment(sketch, "E3840", {"start": v(-83.93, -27.96) * mm, "end": v(-85.9, -27.96) * mm});
            skLineSegment(sketch, "E3841", {"start": v(-77.63, -27.96) * mm, "end": v(-75.66, -27.96) * mm});
            skLineSegment(sketch, "E3842", {"start": v(-87.67, -21.66) * mm, "end": v(-85.9, -21.66) * mm});
            skLineSegment(sketch, "E3843", {"start": v(-85.9, -27.96) * mm, "end": v(-85.9, -21.66) * mm});
            skLineSegment(sketch, "E3844", {"start": v(-85.9, -21.66) * mm, "end": v(-75.66, -21.66) * mm});
            skLineSegment(sketch, "E3845", {"start": v(-75.66, -27.96) * mm, "end": v(-75.66, -21.66) * mm});
            skLineSegment(sketch, "E3846", {"start": v(-67.67, -21.66) * mm, "end": v(-67.67, -26.68) * mm});
            skLineSegment(sketch, "E3847", {"start": v(-67.98, -26.68) * mm, "end": v(-70.44, -26.68) * mm});
            skLineSegment(sketch, "E3848", {"start": v(-70.44, -26.68) * mm, "end": v(-70.44, -26.2) * mm});
            skLineSegment(sketch, "E3849", {"start": v(-70.44, -26.2) * mm, "end": v(-73.88, -26.2) * mm});
            skLineSegment(sketch, "E3850", {"start": v(-73.88, -26.2) * mm, "end": v(-73.88, -40.86) * mm});
            skLineSegment(sketch, "E3851", {"start": v(-83.93, -40.86) * mm, "end": v(-84.71, -40.86) * mm});
            skLineSegment(sketch, "E3852", {"start": v(-84.81, -40.86) * mm, "end": v(-84.81, -41.35) * mm});
            skLineSegment(sketch, "E3853", {"start": v(-84.71, -41.35) * mm, "end": v(-87.67, -41.35) * mm});
            skLineSegment(sketch, "E3854", {"start": v(-87.67, -41.35) * mm, "end": v(-87.67, -21.35) * mm});
            skLineSegment(sketch, "E3855", {"start": v(-75.66, -21.66) * mm, "end": v(-67.98, -21.66) * mm});
            skLineSegment(sketch, "E3856", {"start": v(-5.95, -22.65) * mm, "end": v(-5.95, -27.96) * mm});
            skLineSegment(sketch, "E3857", {"start": v(-5.95, -27.96) * mm, "end": v(3.9, -27.96) * mm});
            skLineSegment(sketch, "E3858", {"start": v(3.9, -27.96) * mm, "end": v(3.9, -22.65) * mm});
            skLineSegment(sketch, "E3859", {"start": v(-5.35, -22.06) * mm, "end": v(3.31, -22.06) * mm});
            skLineSegment(sketch, "E3860", {"start": v(1.93, -27.96) * mm, "end": v(1.93, -51.97) * mm});
            skLineSegment(sketch, "E3861", {"start": v(1.93, -51.97) * mm, "end": v(1.33, -52.58) * mm});
            skLineSegment(sketch, "E3862", {"start": v(1.33, -52.58) * mm, "end": v(-3.37, -52.58) * mm});
            skLineSegment(sketch, "E3863", {"start": v(-3.37, -52.58) * mm, "end": v(-3.98, -51.97) * mm});
            skLineSegment(sketch, "E3864", {"start": v(-3.98, -51.97) * mm, "end": v(-3.98, -27.96) * mm});
            skLineSegment(sketch, "E3865", {"start": v(1.93, -51.97) * mm, "end": v(-3.98, -51.97) * mm});
            skLineSegment(sketch, "E3866", {"start": v(1.93, -29.93) * mm, "end": v(-3.98, -29.93) * mm});
            skLineSegment(sketch, "E3867", {"start": v(1.33, -52.58) * mm, "end": v(1.33, -29.93) * mm});
            skLineSegment(sketch, "E3868", {"start": v(-3.37, -52.58) * mm, "end": v(-3.37, -29.93) * mm});
            skArc(sketch, "E3869", {"start": v(-5.35, -20.28) * mm, "mid": v(-7.03, -20.98) * mm, "end": v(-7.72, -22.65) * mm});
            skArc(sketch, "E3870", {"start": v(5.67, -22.65) * mm, "mid": v(4.98, -20.98) * mm, "end": v(3.31, -20.28) * mm});
            skLineSegment(sketch, "E3871", {"start": v(4.1, -24.89) * mm, "end": v(5.87, -23.11) * mm});
            skLineSegment(sketch, "E3872", {"start": v(2.13, -31.03) * mm, "end": v(5.87, -27.3) * mm});
            skLineSegment(sketch, "E3873", {"start": v(2.13, -35.2) * mm, "end": v(5.87, -31.47) * mm});
            skLineSegment(sketch, "E3874", {"start": v(2.13, -39.39) * mm, "end": v(5.87, -35.64) * mm});
            skLineSegment(sketch, "E3875", {"start": v(4.34, -41.35) * mm, "end": v(5.87, -39.82) * mm});
            skLineSegment(sketch, "E3876", {"start": v(-13.82, -21.92) * mm, "end": v(-13.57, -21.66) * mm});
            skLineSegment(sketch, "E3877", {"start": v(-13.82, -26.1) * mm, "end": v(-9.39, -21.66) * mm});
            skLineSegment(sketch, "E3878", {"start": v(-9.74, -26.2) * mm, "end": v(-6.14, -22.6) * mm});
            skLineSegment(sketch, "E3879", {"start": v(-7.91, -28.54) * mm, "end": v(-6.14, -26.77) * mm});
            skLineSegment(sketch, "E3880", {"start": v(-7.91, -32.72) * mm, "end": v(-4.17, -28.98) * mm});
            skLineSegment(sketch, "E3881", {"start": v(-7.91, -36.9) * mm, "end": v(-4.17, -33.16) * mm});
            skLineSegment(sketch, "E3882", {"start": v(-7.7, -40.86) * mm, "end": v(-4.17, -37.33) * mm});
            skLineSegment(sketch, "E3883", {"start": v(-13.82, -21.66) * mm, "end": v(-6.14, -21.66) * mm});
            skLineSegment(sketch, "E3884", {"start": v(5.87, -21.66) * mm, "end": v(5.87, -41.35) * mm});
            skLineSegment(sketch, "E3885", {"start": v(5.87, -41.35) * mm, "end": v(2.92, -41.35) * mm});
            skLineSegment(sketch, "E3886", {"start": v(2.92, -41.35) * mm, "end": v(2.92, -40.86) * mm});
            skLineSegment(sketch, "E3887", {"start": v(2.92, -40.86) * mm, "end": v(2.13, -40.86) * mm});
            skLineSegment(sketch, "E3888", {"start": v(-7.91, -40.86) * mm, "end": v(-7.91, -26.2) * mm});
            skLineSegment(sketch, "E3889", {"start": v(-7.91, -26.2) * mm, "end": v(-11.36, -26.2) * mm});
            skLineSegment(sketch, "E3890", {"start": v(-11.36, -26.2) * mm, "end": v(-11.36, -26.68) * mm});
            skLineSegment(sketch, "E3891", {"start": v(-11.36, -26.68) * mm, "end": v(-13.82, -26.68) * mm});
            skLineSegment(sketch, "E3892", {"start": v(-13.82, -26.68) * mm, "end": v(-13.82, -21.66) * mm});
            skLineSegment(sketch, "E3893", {"start": v(-6.14, -21.66) * mm, "end": v(-6.14, -27.96) * mm});
            skLineSegment(sketch, "E3894", {"start": v(-6.14, -21.66) * mm, "end": v(4.1, -21.66) * mm});
            skLineSegment(sketch, "E3895", {"start": v(4.1, -21.66) * mm, "end": v(4.1, -27.96) * mm});
            skLineSegment(sketch, "E3896", {"start": v(4.1, -21.66) * mm, "end": v(5.87, -21.66) * mm});
            skLineSegment(sketch, "E3897", {"start": v(-6.14, -27.96) * mm, "end": v(-4.17, -27.96) * mm});
            skLineSegment(sketch, "E3898", {"start": v(4.1, -27.96) * mm, "end": v(2.13, -27.96) * mm});
            skLineSegment(sketch, "E3899", {"start": v(-4.17, -27.96) * mm, "end": v(2.13, -27.96) * mm});
            skLineSegment(sketch, "E3900", {"start": v(-4.17, -27.96) * mm, "end": v(-4.17, -40.86) * mm});
            skLineSegment(sketch, "E3901", {"start": v(-4.17, -40.86) * mm, "end": v(-7.91, -40.86) * mm});
            skLineSegment(sketch, "E3902", {"start": v(2.13, -27.96) * mm, "end": v(2.13, -40.86) * mm});
            skLineSegment(sketch, "E3903", {"start": v(2.13, -40.86) * mm, "end": v(-4.17, -40.86) * mm});
            skLineSegment(sketch, "E3904", {"start": v(-1.02, -18.7) * mm, "end": v(-1.02, -43.82) * mm});
            skLineSegment(sketch, "E3905", {"start": v(-61.57, 44.8) * mm, "end": v(-61.57, 34.95) * mm});
            skLineSegment(sketch, "E3906", {"start": v(-65.52, 44.8) * mm, "end": v(-65.52, 34.95) * mm});
            skLineSegment(sketch, "E3907", {"start": v(-61.08, 44.8) * mm, "end": v(-66, 44.8) * mm});
            skLineSegment(sketch, "E3908", {"start": v(-61.08, 35.44) * mm, "end": v(-66, 35.44) * mm});
            skLineSegment(sketch, "E3909", {"start": v(-61.08, 46.77) * mm, "end": v(-61.08, 35.44) * mm});
            skLineSegment(sketch, "E3910", {"start": v(-61.08, 35.44) * mm, "end": v(-61.57, 34.95) * mm});
            skLineSegment(sketch, "E3911", {"start": v(-61.57, 34.95) * mm, "end": v(-65.52, 34.95) * mm});
            skLineSegment(sketch, "E3912", {"start": v(-65.52, 34.95) * mm, "end": v(-66, 35.44) * mm});
            skLineSegment(sketch, "E3913", {"start": v(-66, 35.44) * mm, "end": v(-66, 46.77) * mm});
            skLineSegment(sketch, "E3914", {"start": v(-67.48, 51.7) * mm, "end": v(-59.6, 51.7) * mm});
            skLineSegment(sketch, "E3915", {"start": v(-67.98, 51.2) * mm, "end": v(-67.98, 46.77) * mm});
            skLineSegment(sketch, "E3916", {"start": v(-67.98, 46.77) * mm, "end": v(-59.11, 46.77) * mm});
            skLineSegment(sketch, "E3917", {"start": v(-59.11, 46.77) * mm, "end": v(-59.11, 51.2) * mm});
            skArc(sketch, "E3918", {"start": v(-67.48, 53.17) * mm, "mid": v(-68.88, 52.6) * mm, "end": v(-69.45, 51.2) * mm});
            skArc(sketch, "E3919", {"start": v(-57.64, 51.2) * mm, "mid": v(-58.21, 52.6) * mm, "end": v(-59.6, 53.17) * mm});
            skLineSegment(sketch, "E3920", {"start": v(-22.68, 51.2) * mm, "end": v(-22.68, 46.77) * mm});
            skLineSegment(sketch, "E3921", {"start": v(-22.68, 46.77) * mm, "end": v(-13.82, 46.77) * mm});
            skLineSegment(sketch, "E3922", {"start": v(-13.82, 46.77) * mm, "end": v(-13.82, 51.2) * mm});
            skLineSegment(sketch, "E3923", {"start": v(-22.2, 51.7) * mm, "end": v(-14.31, 51.7) * mm});
            skLineSegment(sketch, "E3924", {"start": v(-15.8, 46.77) * mm, "end": v(-15.8, 35.44) * mm});
            skLineSegment(sketch, "E3925", {"start": v(-15.8, 35.44) * mm, "end": v(-16.27, 34.95) * mm});
            skLineSegment(sketch, "E3926", {"start": v(-16.27, 34.95) * mm, "end": v(-20.23, 34.95) * mm});
            skLineSegment(sketch, "E3927", {"start": v(-20.23, 34.95) * mm, "end": v(-20.71, 35.44) * mm});
            skLineSegment(sketch, "E3928", {"start": v(-20.71, 35.44) * mm, "end": v(-20.71, 46.77) * mm});
            skLineSegment(sketch, "E3929", {"start": v(-15.8, 35.44) * mm, "end": v(-20.71, 35.44) * mm});
            skLineSegment(sketch, "E3930", {"start": v(-15.8, 44.8) * mm, "end": v(-20.71, 44.8) * mm});
            skLineSegment(sketch, "E3931", {"start": v(-16.27, 34.95) * mm, "end": v(-16.27, 44.8) * mm});
            skLineSegment(sketch, "E3932", {"start": v(-20.23, 34.95) * mm, "end": v(-20.23, 44.8) * mm});
            skArc(sketch, "E3933", {"start": v(-22.2, 53.17) * mm, "mid": v(-23.58, 52.6) * mm, "end": v(-24.16, 51.2) * mm});
            skArc(sketch, "E3934", {"start": v(-12.35, 51.2) * mm, "mid": v(-12.92, 52.6) * mm, "end": v(-14.31, 53.17) * mm});
            skLineSegment(sketch, "E3935", {"start": v(-58.62, 29.83) * mm, "end": v(-73.4, 29.83) * mm});
            skLineSegment(sketch, "E3936", {"start": v(-23.18, 29.83) * mm, "end": v(-8.4, 29.83) * mm});
            skLineSegment(sketch, "E3937", {"start": v(-63.55, 45.3) * mm, "end": v(-63.55, 33.43) * mm});
            skLineSegment(sketch, "E3938", {"start": v(-18.25, 45.3) * mm, "end": v(-18.25, 33.14) * mm});
            skLineSegment(sketch, "E3939", {"start": v(-11.36, 42.34) * mm, "end": v(-15.7, 42.34) * mm});
            skLineSegment(sketch, "E3940", {"start": v(-40.9, 47.27) * mm, "end": v(-40.9, -44.3) * mm});
            skLineSegment(sketch, "E3941", {"start": v(8.82, -9.35) * mm, "end": v(-88.61, -9.35) * mm});
            skLineSegment(sketch, "E3942", {"start": v(-61.58, 22.65) * mm, "end": v(-20.22, 22.65) * mm});
            skLineSegment(sketch, "E3943", {"start": v(-72.9, -40.37) * mm, "end": v(-72.9, -26.2) * mm});
            skLineSegment(sketch, "E3944", {"start": v(-9.88, -41.35) * mm, "end": v(-23.18, -41.35) * mm});
            skLineSegment(sketch, "E3945", {"start": v(-72.9, -10.04) * mm, "end": v(-70.44, -10.04) * mm});
            skLineSegment(sketch, "E3946", {"start": v(-70.44, -10.04) * mm, "end": v(-70.44, -8.96) * mm});
            skLineSegment(sketch, "E3947", {"start": v(-70.44, -8.96) * mm, "end": v(-68.67, -8.96) * mm});
            skLineSegment(sketch, "E3948", {"start": v(-68.67, -8.96) * mm, "end": v(-68.67, -16.25) * mm});
            skLineSegment(sketch, "E3949", {"start": v(-68.67, -16.25) * mm, "end": v(-70.44, -16.25) * mm});
            skLineSegment(sketch, "E3950", {"start": v(-70.44, -16.25) * mm, "end": v(-70.44, -15.16) * mm});
            skLineSegment(sketch, "E3951", {"start": v(-70.44, -15.16) * mm, "end": v(-72.9, -15.16) * mm});
            skLineSegment(sketch, "E3952", {"start": v(-72.9, -10.04) * mm, "end": v(-72.9, -0.6) * mm});
            skLineSegment(sketch, "E3953", {"start": v(-76.24, -12.6) * mm, "end": v(-65.71, -12.6) * mm});
            skLineSegment(sketch, "E3954", {"start": v(-72.9, -21.07) * mm, "end": v(-70.44, -21.07) * mm});
            skLineSegment(sketch, "E3955", {"start": v(-70.44, -21.07) * mm, "end": v(-70.44, -19.2) * mm});
            skLineSegment(sketch, "E3956", {"start": v(-70.44, -19.2) * mm, "end": v(-65.51, -19.2) * mm});
            skLineSegment(sketch, "E3957", {"start": v(-65.51, -19.2) * mm, "end": v(-65.51, -21.07) * mm});
            skLineSegment(sketch, "E3958", {"start": v(-65.51, -21.07) * mm, "end": v(-64.53, -21.07) * mm});
            skLineSegment(sketch, "E3959", {"start": v(-64.53, -21.07) * mm, "end": v(-64.53, -26.2) * mm});
            skLineSegment(sketch, "E3960", {"start": v(-64.53, -26.2) * mm, "end": v(-65.51, -26.2) * mm});
            skLineSegment(sketch, "E3961", {"start": v(-65.51, -26.2) * mm, "end": v(-65.51, -28.06) * mm});
            skLineSegment(sketch, "E3962", {"start": v(-65.51, -28.06) * mm, "end": v(-70.44, -28.06) * mm});
            skLineSegment(sketch, "E3963", {"start": v(-70.44, -28.06) * mm, "end": v(-70.44, -26.2) * mm});
            skLineSegment(sketch, "E3964", {"start": v(-70.44, -26.2) * mm, "end": v(-72.9, -26.2) * mm});
            skLineSegment(sketch, "E3965", {"start": v(-72.9, -21.07) * mm, "end": v(-72.9, -15.16) * mm});
            skLineSegment(sketch, "E3966", {"start": v(-72.9, 4.53) * mm, "end": v(-70.44, 4.53) * mm});
            skLineSegment(sketch, "E3967", {"start": v(-70.44, 4.53) * mm, "end": v(-70.44, 6.4) * mm});
            skLineSegment(sketch, "E3968", {"start": v(-70.44, 6.4) * mm, "end": v(-65.51, 6.4) * mm});
            skLineSegment(sketch, "E3969", {"start": v(-65.51, 6.4) * mm, "end": v(-65.51, 4.53) * mm});
            skLineSegment(sketch, "E3970", {"start": v(-65.51, 4.53) * mm, "end": v(-64.53, 4.53) * mm});
            skLineSegment(sketch, "E3971", {"start": v(-64.53, 4.53) * mm, "end": v(-64.53, -0.6) * mm});
            skLineSegment(sketch, "E3972", {"start": v(-64.53, -0.6) * mm, "end": v(-65.51, -0.6) * mm});
            skLineSegment(sketch, "E3973", {"start": v(-65.51, -0.6) * mm, "end": v(-65.51, -2.46) * mm});
            skLineSegment(sketch, "E3974", {"start": v(-65.51, -2.46) * mm, "end": v(-70.44, -2.46) * mm});
            skLineSegment(sketch, "E3975", {"start": v(-70.44, -2.46) * mm, "end": v(-70.44, -0.6) * mm});
            skLineSegment(sketch, "E3976", {"start": v(-70.44, -0.6) * mm, "end": v(-72.9, -0.6) * mm});
            skLineSegment(sketch, "E3977", {"start": v(-61.58, 1.97) * mm, "end": v(-75.85, 1.97) * mm});
            skLineSegment(sketch, "E3978", {"start": v(-72.9, 4.53) * mm, "end": v(-72.9, 17.72) * mm});
            skLineSegment(sketch, "E3979", {"start": v(-11.36, -10.04) * mm, "end": v(-8.9, -10.04) * mm});
            skLineSegment(sketch, "E3980", {"start": v(-11.36, -8.96) * mm, "end": v(-11.36, -10.04) * mm});
            skLineSegment(sketch, "E3981", {"start": v(-13.13, -8.96) * mm, "end": v(-11.36, -8.96) * mm});
            skLineSegment(sketch, "E3982", {"start": v(-13.13, -16.25) * mm, "end": v(-13.13, -8.96) * mm});
            skLineSegment(sketch, "E3983", {"start": v(-11.36, -16.25) * mm, "end": v(-13.13, -16.25) * mm});
            skLineSegment(sketch, "E3984", {"start": v(-11.36, -15.16) * mm, "end": v(-11.36, -16.25) * mm});
            skLineSegment(sketch, "E3985", {"start": v(-8.9, -15.16) * mm, "end": v(-11.36, -15.16) * mm});
            skLineSegment(sketch, "E3986", {"start": v(-8.9, -0.6) * mm, "end": v(-8.9, -10.04) * mm});
            skLineSegment(sketch, "E3987", {"start": v(-16.09, -12.6) * mm, "end": v(-5.56, -12.6) * mm});
            skLineSegment(sketch, "E3988", {"start": v(-11.36, -21.07) * mm, "end": v(-8.9, -21.07) * mm});
            skLineSegment(sketch, "E3989", {"start": v(-11.36, -19.2) * mm, "end": v(-11.36, -21.07) * mm});
            skLineSegment(sketch, "E3990", {"start": v(-16.28, -19.2) * mm, "end": v(-11.36, -19.2) * mm});
            skLineSegment(sketch, "E3991", {"start": v(-16.28, -21.07) * mm, "end": v(-16.28, -19.2) * mm});
            skLineSegment(sketch, "E3992", {"start": v(-17.27, -21.07) * mm, "end": v(-16.28, -21.07) * mm});
            skLineSegment(sketch, "E3993", {"start": v(-17.27, -26.2) * mm, "end": v(-17.27, -21.07) * mm});
            skLineSegment(sketch, "E3994", {"start": v(-16.28, -26.2) * mm, "end": v(-17.27, -26.2) * mm});
            skLineSegment(sketch, "E3995", {"start": v(-16.28, -28.06) * mm, "end": v(-16.28, -26.2) * mm});
            skLineSegment(sketch, "E3996", {"start": v(-11.36, -28.06) * mm, "end": v(-16.28, -28.06) * mm});
            skLineSegment(sketch, "E3997", {"start": v(-11.36, -26.2) * mm, "end": v(-11.36, -28.06) * mm});
            skLineSegment(sketch, "E3998", {"start": v(-8.9, -26.2) * mm, "end": v(-11.36, -26.2) * mm});
            skLineSegment(sketch, "E3999", {"start": v(-8.9, -15.16) * mm, "end": v(-8.9, -21.07) * mm});
            skLineSegment(sketch, "E4000", {"start": v(-11.36, 4.53) * mm, "end": v(-8.9, 4.53) * mm});
            skLineSegment(sketch, "E4001", {"start": v(-11.36, 6.4) * mm, "end": v(-11.36, 4.53) * mm});
            skLineSegment(sketch, "E4002", {"start": v(-16.28, 6.4) * mm, "end": v(-11.36, 6.4) * mm});
            skLineSegment(sketch, "E4003", {"start": v(-16.28, 4.53) * mm, "end": v(-16.28, 6.4) * mm});
            skLineSegment(sketch, "E4004", {"start": v(-17.27, 4.53) * mm, "end": v(-16.28, 4.53) * mm});
            skLineSegment(sketch, "E4005", {"start": v(-17.27, -0.6) * mm, "end": v(-17.27, 4.53) * mm});
            skLineSegment(sketch, "E4006", {"start": v(-16.28, -0.6) * mm, "end": v(-17.27, -0.6) * mm});
            skLineSegment(sketch, "E4007", {"start": v(-16.28, -2.46) * mm, "end": v(-16.28, -0.6) * mm});
            skLineSegment(sketch, "E4008", {"start": v(-11.36, -2.46) * mm, "end": v(-16.28, -2.46) * mm});
            skLineSegment(sketch, "E4009", {"start": v(-11.36, -0.6) * mm, "end": v(-11.36, -2.46) * mm});
            skLineSegment(sketch, "E4010", {"start": v(-8.9, -0.6) * mm, "end": v(-11.36, -0.6) * mm});
            skLineSegment(sketch, "E4011", {"start": v(-5.95, 1.97) * mm, "end": v(-20.22, 1.97) * mm});
            skLineSegment(sketch, "E4012", {"start": v(-8.9, -26.2) * mm, "end": v(-8.9, -40.37) * mm});
            skLineSegment(sketch, "E4013", {"start": v(-8.9, 17.72) * mm, "end": v(-8.9, 4.53) * mm});
            skLineSegment(sketch, "E4014", {"start": v(-60.99, 42.34) * mm, "end": v(-60.99, 39.88) * mm});
            skLineSegment(sketch, "E4015", {"start": v(-60.99, 39.88) * mm, "end": v(-59.11, 39.88) * mm});
            skLineSegment(sketch, "E4016", {"start": v(-59.11, 39.88) * mm, "end": v(-59.11, 34.95) * mm});
            skLineSegment(sketch, "E4017", {"start": v(-59.11, 34.95) * mm, "end": v(-60.99, 34.95) * mm});
            skLineSegment(sketch, "E4018", {"start": v(-60.99, 34.95) * mm, "end": v(-60.99, 33.97) * mm});
            skLineSegment(sketch, "E4019", {"start": v(-60.99, 33.97) * mm, "end": v(-66.1, 33.97) * mm});
            skLineSegment(sketch, "E4020", {"start": v(-66.1, 33.97) * mm, "end": v(-66.1, 34.95) * mm});
            skLineSegment(sketch, "E4021", {"start": v(-66.1, 34.95) * mm, "end": v(-67.98, 34.95) * mm});
            skLineSegment(sketch, "E4022", {"start": v(-67.98, 34.95) * mm, "end": v(-67.98, 39.88) * mm});
            skLineSegment(sketch, "E4023", {"start": v(-67.98, 39.88) * mm, "end": v(-66.1, 39.88) * mm});
            skLineSegment(sketch, "E4024", {"start": v(-66.1, 39.88) * mm, "end": v(-66.1, 42.34) * mm});
            skLineSegment(sketch, "E4025", {"start": v(-20.81, 39.88) * mm, "end": v(-20.81, 42.34) * mm});
            skLineSegment(sketch, "E4026", {"start": v(-22.68, 39.88) * mm, "end": v(-20.81, 39.88) * mm});
            skLineSegment(sketch, "E4027", {"start": v(-22.68, 34.95) * mm, "end": v(-22.68, 39.88) * mm});
            skLineSegment(sketch, "E4028", {"start": v(-20.81, 34.95) * mm, "end": v(-22.68, 34.95) * mm});
            skLineSegment(sketch, "E4029", {"start": v(-20.81, 33.97) * mm, "end": v(-20.81, 34.95) * mm});
            skLineSegment(sketch, "E4030", {"start": v(-15.7, 33.97) * mm, "end": v(-20.81, 33.97) * mm});
            skLineSegment(sketch, "E4031", {"start": v(-15.7, 34.95) * mm, "end": v(-15.7, 33.97) * mm});
            skLineSegment(sketch, "E4032", {"start": v(-13.82, 34.95) * mm, "end": v(-15.7, 34.95) * mm});
            skLineSegment(sketch, "E4033", {"start": v(-13.82, 39.88) * mm, "end": v(-13.82, 34.95) * mm});
            skLineSegment(sketch, "E4034", {"start": v(-15.7, 39.88) * mm, "end": v(-13.82, 39.88) * mm});
            skLineSegment(sketch, "E4035", {"start": v(-15.7, 42.34) * mm, "end": v(-15.7, 39.88) * mm});
            skLineSegment(sketch, "E4036", {"start": v(-20.81, 42.34) * mm, "end": v(-60.99, 42.34) * mm});
            skLineSegment(sketch, "E4037", {"start": v(-66.1, 42.34) * mm, "end": v(-70.44, 42.34) * mm});
            skLineSegment(sketch, "E4038", {"start": v(-10.38, 41.35) * mm, "end": v(-10.38, 31.46) * mm});
            skLineSegment(sketch, "E4039", {"start": v(-71.42, 19.7) * mm, "end": v(-71.42, 28.2) * mm});
            skLineSegment(sketch, "E4040", {"start": v(-58.62, -41.35) * mm, "end": v(-71.91, -41.35) * mm});
            skLineSegment(sketch, "E4041", {"start": v(-57.64, -40.37) * mm, "end": v(-58.62, -41.35) * mm});
            skLineSegment(sketch, "E4042", {"start": v(-24.16, -40.37) * mm, "end": v(-57.64, -40.37) * mm});
            skLineSegment(sketch, "E4043", {"start": v(-23.18, -41.35) * mm, "end": v(-24.16, -40.37) * mm});
            skLineSegment(sketch, "E4044", {"start": v(-71.91, -41.35) * mm, "end": v(-72.9, -40.37) * mm});
            skLineSegment(sketch, "E4045", {"start": v(-8.9, -40.37) * mm, "end": v(-9.88, -41.35) * mm});
            skLineSegment(sketch, "E4046", {"start": v(-61.58, 22.65) * mm, "end": v(-61.58, 19.7) * mm});
            skLineSegment(sketch, "E4047", {"start": v(-61.58, 19.7) * mm, "end": v(-67.48, 19.7) * mm});
            skLineSegment(sketch, "E4048", {"start": v(-67.48, 19.7) * mm, "end": v(-68.47, 18.7) * mm});
            skLineSegment(sketch, "E4049", {"start": v(-68.47, 18.7) * mm, "end": v(-71.91, 18.7) * mm});
            skLineSegment(sketch, "E4050", {"start": v(-50.75, 22.65) * mm, "end": v(-50.75, 23.14) * mm});
            skLineSegment(sketch, "E4051", {"start": v(-62.07, 23.14) * mm, "end": v(-62.07, 20.18) * mm});
            skLineSegment(sketch, "E4052", {"start": v(-62.07, 20.18) * mm, "end": v(-67.69, 20.18) * mm});
            skLineSegment(sketch, "E4053", {"start": v(-67.69, 20.18) * mm, "end": v(-68.67, 19.2) * mm});
            skLineSegment(sketch, "E4054", {"start": v(-68.67, 19.2) * mm, "end": v(-70.93, 19.2) * mm});
            skLineSegment(sketch, "E4055", {"start": v(-62.07, 23.14) * mm, "end": v(-50.75, 23.14) * mm});
            skLineSegment(sketch, "E4056", {"start": v(-20.22, 19.7) * mm, "end": v(-20.22, 22.65) * mm});
            skLineSegment(sketch, "E4057", {"start": v(-14.31, 19.7) * mm, "end": v(-20.22, 19.7) * mm});
            skLineSegment(sketch, "E4058", {"start": v(-13.33, 18.7) * mm, "end": v(-14.31, 19.7) * mm});
            skLineSegment(sketch, "E4059", {"start": v(-9.88, 18.7) * mm, "end": v(-13.33, 18.7) * mm});
            skLineSegment(sketch, "E4060", {"start": v(-31.05, 23.14) * mm, "end": v(-31.05, 22.65) * mm});
            skLineSegment(sketch, "E4061", {"start": v(-19.73, 20.18) * mm, "end": v(-19.73, 23.14) * mm});
            skLineSegment(sketch, "E4062", {"start": v(-14.11, 20.18) * mm, "end": v(-19.73, 20.18) * mm});
            skLineSegment(sketch, "E4063", {"start": v(-13.13, 19.2) * mm, "end": v(-14.11, 20.18) * mm});
            skLineSegment(sketch, "E4064", {"start": v(-10.87, 19.2) * mm, "end": v(-13.13, 19.2) * mm});
            skLineSegment(sketch, "E4065", {"start": v(-31.05, 23.14) * mm, "end": v(-19.73, 23.14) * mm});
            skLineSegment(sketch, "E4066", {"start": v(-9.88, 18.7) * mm, "end": v(-8.9, 17.72) * mm});
            skLineSegment(sketch, "E4067", {"start": v(-10.38, 41.35) * mm, "end": v(-11.36, 42.34) * mm});
            skLineSegment(sketch, "E4068", {"start": v(-71.42, 41.35) * mm, "end": v(-70.44, 42.34) * mm});
            skLineSegment(sketch, "E4069", {"start": v(-71.91, 18.7) * mm, "end": v(-72.9, 17.72) * mm});
            skLineSegment(sketch, "E4070", {"start": v(-70.93, 19.2) * mm, "end": v(-71.42, 19.7) * mm});
            skLineSegment(sketch, "E4071", {"start": v(-10.87, 19.2) * mm, "end": v(-10.38, 19.7) * mm});
            skLineSegment(sketch, "E4072", {"start": v(-71.42, 28.2) * mm, "end": v(-61.53, 28.2) * mm});
            skLineSegment(sketch, "E4073", {"start": v(-71.42, 28.2) * mm, "end": v(-71.42, 31.46) * mm});
            skLineSegment(sketch, "E4074", {"start": v(-71.42, 31.46) * mm, "end": v(-61.53, 31.46) * mm});
            skLineSegment(sketch, "E4075", {"start": v(-71.42, 31.46) * mm, "end": v(-71.42, 41.35) * mm});
            skLineSegment(sketch, "E4076", {"start": v(-61.53, 28.2) * mm, "end": v(-60.6, 29.83) * mm});
            skLineSegment(sketch, "E4077", {"start": v(-61.53, 31.46) * mm, "end": v(-60.6, 29.83) * mm});
            skLineSegment(sketch, "E4078", {"start": v(-61.53, 28.2) * mm, "end": v(-61.53, 31.46) * mm});
            skLineSegment(sketch, "E4079", {"start": v(-71.42, 27.86) * mm, "end": v(-62.56, 27.86) * mm});
            skLineSegment(sketch, "E4080", {"start": v(-71.42, 31.8) * mm, "end": v(-62.56, 31.8) * mm});
            skLineSegment(sketch, "E4081", {"start": v(-62.56, 27.86) * mm, "end": v(-62.56, 31.8) * mm});
            skLineSegment(sketch, "E4082", {"start": v(-10.38, 31.46) * mm, "end": v(-20.27, 31.46) * mm});
            skLineSegment(sketch, "E4083", {"start": v(-10.38, 31.46) * mm, "end": v(-10.38, 28.2) * mm});
            skLineSegment(sketch, "E4084", {"start": v(-10.38, 28.2) * mm, "end": v(-20.27, 28.2) * mm});
            skLineSegment(sketch, "E4085", {"start": v(-10.38, 28.2) * mm, "end": v(-10.38, 19.7) * mm});
            skLineSegment(sketch, "E4086", {"start": v(-20.27, 31.46) * mm, "end": v(-21.2, 29.83) * mm});
            skLineSegment(sketch, "E4087", {"start": v(-20.27, 28.2) * mm, "end": v(-21.2, 29.83) * mm});
            skLineSegment(sketch, "E4088", {"start": v(-20.27, 31.46) * mm, "end": v(-20.27, 28.2) * mm});
            skLineSegment(sketch, "E4089", {"start": v(-10.38, 31.8) * mm, "end": v(-19.24, 31.8) * mm});
            skLineSegment(sketch, "E4090", {"start": v(-10.38, 27.86) * mm, "end": v(-19.24, 27.86) * mm});
            skLineSegment(sketch, "E4091", {"start": v(-19.24, 31.8) * mm, "end": v(-19.24, 27.86) * mm});
            skSolve(sketch);
        }
        {
            var Q0;
            Q0=qCreatedBy(makeId("Top.planeOp"),FACE);
            var sketch = newSketch(context, id + "F22", { "sketchPlane" : qUnion([Q0])});
            skLineSegment(sketch, "E4092.0", {"start": v(-13.82, -26.68) * mm, "end": v(-13.82, -21.66) * mm});
            skLineSegment(sketch, "E4093.0", {"start": v(-13.82, -21.66) * mm, "end": v(-6.14, -21.66) * mm});
            skPoint(sketch, "E4094.0", {"position": v(-12.6, -26.68) * mm});
            skLineSegment(sketch, "E4095.0", {"start": v(-7.91, -26.2) * mm, "end": v(-11.36, -26.2) * mm});
            skLineSegment(sketch, "E4096.0", {"start": v(-11.36, -26.2) * mm, "end": v(-11.36, -26.68) * mm});
            skLineSegment(sketch, "E4097.0", {"start": v(-11.36, -26.68) * mm, "end": v(-13.82, -26.68) * mm});
            skLineSegment(sketch, "E4098.0", {"start": v(-7.91, -40.86) * mm, "end": v(-7.91, -26.2) * mm});
            skLineSegment(sketch, "E4099.0", {"start": v(-4.17, -40.86) * mm, "end": v(-7.91, -40.86) * mm});
            skLineSegment(sketch, "E4100.0", {"start": v(2.13, -40.86) * mm, "end": v(-4.17, -40.86) * mm});
            skPoint(sketch, "E4101.0", {"position": v(2.52, -40.86) * mm});
            skLineSegment(sketch, "E4102.0", {"start": v(2.92, -40.86) * mm, "end": v(2.13, -40.86) * mm});
            skPoint(sketch, "E4103.0", {"position": v(2.92, -41.1) * mm});
            skLineSegment(sketch, "E4104.0", {"start": v(2.92, -41.35) * mm, "end": v(2.92, -40.86) * mm});
            skLineSegment(sketch, "E4105.0", {"start": v(5.87, -41.35) * mm, "end": v(2.92, -41.35) * mm});
            skLineSegment(sketch, "E4106.0", {"start": v(5.87, -21.66) * mm, "end": v(5.87, -41.35) * mm});
            skLineSegment(sketch, "E4107.0", {"start": v(4.1, -21.66) * mm, "end": v(5.87, -21.66) * mm});
            skLineSegment(sketch, "E4108.0", {"start": v(-6.14, -21.66) * mm, "end": v(4.1, -21.66) * mm});
            skSolve(sketch);
        }
        {
            var Q0;
            Q0 = qSketchRegion(id + "F22", true);
            extrude(context, id + "F23", {"entities" : qUnion([Q0]), "depth" : 78 * mm, "offsetDistance" : 25 * mm});
        }
    });
